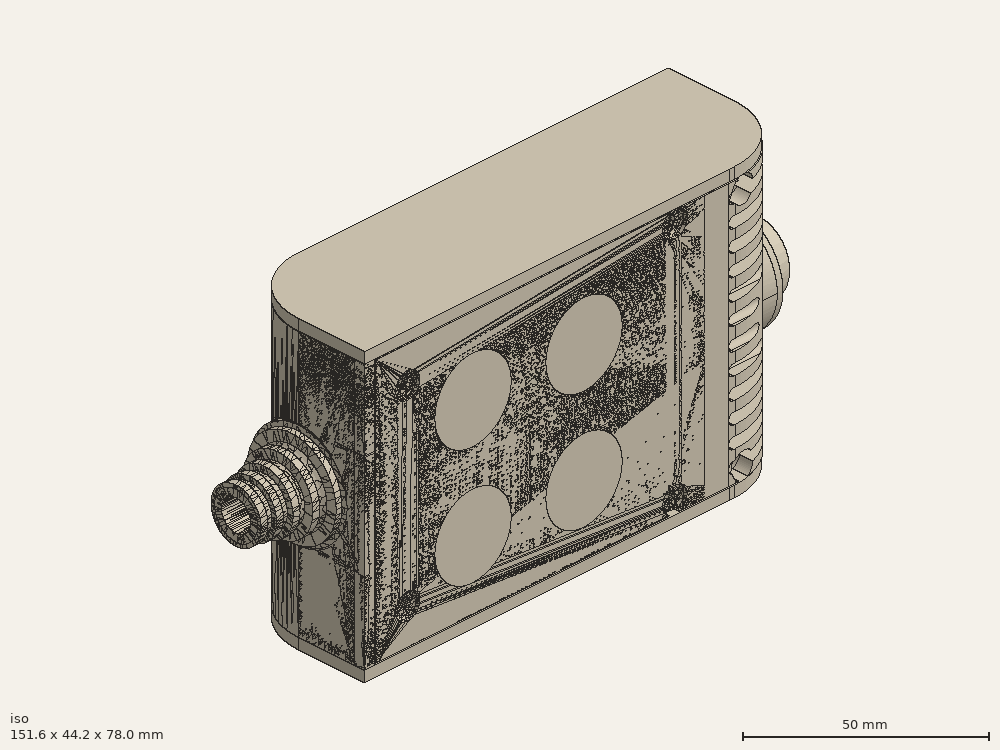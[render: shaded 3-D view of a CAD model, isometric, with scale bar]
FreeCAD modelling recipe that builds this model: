
FCSTD DOCUMENT  (FreeCAD 0.19R0.19.2)
Label: enclosure_185FCStd
License: All rights reserved
LicenseURL: http://en.wikipedia.org/wiki/All_rights_reserved
objects: Part::Revolution×152, Part::MultiFuse×146, Part::Feature×146, Sketcher::SketchObject×84, Part::Cut×70, Part::Cylinder×70, Part::Extrusion×67, Part::Fillet×58, Part::Box×36, App::MeasureDistance×4, PartDesign::Body×2, Image::ImagePlane×1
note: 831 computed .brp shape members not serialized (recipe doc carries the construction recipe); baked Part::Feature solids carry a one-line shape summary decoded from their .brp

FEATURE [Sketcher::SketchObject] Sketch  label="topSketch"
  FullyConstrained = true
  sketch-geometry (20):
    g0: LineSegment StartX=5.21097e-06 StartY=3 StartZ=0 EndX=5.21097e-06 EndY=19 EndZ=0
    g1: ArcOfCircle CenterX=19 CenterY=19 CenterZ=0 NormalX=0 NormalY=0 NormalZ=1 AngleXU=0 Radius=19 StartAngle=1.5708 EndAngle=3.14159
    g2: ArcOfCircle CenterX=19 CenterY=19 CenterZ=0 NormalX=0 NormalY=0 NormalZ=1 AngleXU=0 Radius=16 StartAngle=1.5708 EndAngle=3.14159
    g3: LineSegment StartX=114 StartY=35 StartZ=0 EndX=19 EndY=35 EndZ=0
    g4: LineSegment StartX=5.21097e-06 StartY=3 StartZ=0 EndX=5.21097e-06 EndY=0 EndZ=0
    g5: LineSegment StartX=3 StartY=0 StartZ=0 EndX=5.21097e-06 EndY=0 EndZ=0
    g6: LineSegment StartX=3 StartY=19 StartZ=0 EndX=3 EndY=0 EndZ=0
    g7: LineSegment StartX=19 StartY=38 StartZ=0 EndX=124 EndY=38 EndZ=0
    g8: Circle CenterX=119 CenterY=35 CenterZ=0 NormalX=0 NormalY=0 NormalZ=1 AngleXU=0 Radius=1
    g9: Circle CenterX=121 CenterY=35 CenterZ=0 NormalX=0 NormalY=0 NormalZ=1 AngleXU=0 Radius=1
    g10: Circle CenterX=121 CenterY=33 CenterZ=0 NormalX=0 NormalY=0 NormalZ=1 AngleXU=0 Radius=1
    g11: BSplineCurve PolesCount=3 KnotsCount=2 Degree=2 IsPeriodic=0
    g12: GeomPoint X=119 Y=35 Z=0
    g13: GeomPoint X=121 Y=33 Z=0
    g14: LineSegment StartX=119 StartY=35 StartZ=0 EndX=114 EndY=35 EndZ=0
    g15: ArcOfCircle CenterX=105 CenterY=19 CenterZ=0 NormalX=0 NormalY=0 NormalZ=1 AngleXU=0 Radius=19 StartAngle=5.7297 EndAngle=6.28319
    g16: ArcOfCircle CenterX=105 CenterY=19 CenterZ=0 NormalX=0 NormalY=0 NormalZ=1 AngleXU=0 Radius=16 StartAngle=5.60905 EndAngle=6.28319
    g17: LineSegment StartX=121 StartY=33 StartZ=0 EndX=121 EndY=19 EndZ=0
    g18: LineSegment StartX=124 StartY=38 StartZ=0 EndX=124 EndY=19 EndZ=0
    g19: LineSegment StartX=117.5 StartY=9.01251 StartZ=0 EndX=121.163 EndY=9.0125 EndZ=0
  constraints (46):
    c: Vertical(g0)
    c: Block(g0)
    c: Coincident(g1,g0)
    c: Block(g1)
    c: Coincident(g2,g1)
    c: Block(g2)
    c: Coincident(g3,g2)
    c: Horizontal(g3)
    c: Tangent(g3,g2)
    c: Coincident(g4,g0)
    c: Distance(g4) = 3
    c: Vertical(g4)
    c: Coincident(g5,g4)
    c: Horizontal(g5)
    c: Coincident(g6,g2)
    c: Coincident(g6,g5)
    c: Vertical(g6)
    c: Horizontal(g7)
    c: Distance(g7) = 105
    c: Coincident(g7,g1)
    c: Block(g3)
    c: Weight(g8) = 1
    c: Equal(g8,g9)
    c: Equal(g8,g10)
    c: InternalAlignment(g8,g11)
    c: InternalAlignment(g9,g11)
    c: InternalAlignment(g10,g11)
    c: InternalAlignment(g12,g11)
    c: InternalAlignment(g13,g11)
    c: Block(g11)
    c: Coincident(g14,g11)
    c: Coincident(g14,g3)
    c: Horizontal(g14)
    c: Block(g15)
    c: Coincident(g16,g15)
    c: Block(g16)
    c: Coincident(g17,g11)
    c: Coincident(g17,g16)
    c: Vertical(g17)
    c: Distance(g17) = 14
    c: Coincident(g18,g7)
    c: Coincident(g18,g15)
    c: Vertical(g18)
    c: Distance(g18) = 19
    c: Coincident(g19,g16)
    c: Coincident(g19,g15)
FEATURE [Sketcher::SketchObject] Sketch001  label="bottomSketch"
  FullyConstrained = true
  sketch-geometry (32):
    g0: LineSegment StartX=3.3 StartY=-6.03275e-07 StartZ=0 EndX=98 EndY=-6.03275e-07 EndZ=0
    g1: ArcOfCircle CenterX=98 CenterY=19 CenterZ=0 NormalX=0 NormalY=0 NormalZ=1 AngleXU=0 Radius=19 StartAngle=4.71239 EndAngle=5.71103
    g2: LineSegment StartX=6.3 StartY=8 StartZ=0 EndX=3.3 EndY=8 EndZ=0
    g3: LineSegment StartX=3.3 StartY=8 StartZ=0 EndX=3.3 EndY=-6.03275e-07 EndZ=0
    g4: ArcOfCircle CenterX=8.3 CenterY=5 CenterZ=0 NormalX=0 NormalY=0 NormalZ=1 AngleXU=0 Radius=2 StartAngle=3.14159 EndAngle=4.71239
    g5: LineSegment StartX=6.3 StartY=8 StartZ=0 EndX=6.3 EndY=5 EndZ=0
    g6: ArcOfCircle CenterX=98 CenterY=19 CenterZ=0 NormalX=0 NormalY=0 NormalZ=1 AngleXU=0 Radius=12.7 StartAngle=4.71239 EndAngle=6.28319
    g7: LineSegment StartX=94.7 StartY=3 StartZ=0 EndX=8.3 EndY=3 EndZ=0
    g8-g12: Circle x5 (B-spline internal-alignment scaffolding for g13; pole/knot coordinates omitted)
    g13: BSplineCurve PolesCount=5 KnotsCount=3 Degree=3 IsPeriodic=0
    g14: GeomPoint X=98 Y=6.3 Z=0
    g15: GeomPoint X=96.3938 Y=4.71946 Z=0
    g16: GeomPoint X=94.7 Y=3 Z=0
    g17-g23: Circle x7 (B-spline internal-alignment scaffolding for g24; pole/knot coordinates omitted)
    g24: BSplineCurve PolesCount=7 KnotsCount=5 Degree=3 IsPeriodic=0
    g25-g29: GeomPoint x5 (B-spline internal-alignment scaffolding for g24; pole/knot coordinates omitted)
    g30: ArcOfCircle CenterX=98 CenterY=19 CenterZ=0 NormalX=0 NormalY=0 NormalZ=1 AngleXU=0 Radius=15.7 StartAngle=5.81226 EndAngle=6.28319
    g31: LineSegment StartX=110.7 StartY=19 StartZ=0 EndX=113.7 EndY=19 EndZ=0
  constraints (41):
    c: Horizontal(g0)
    c: Coincident(g1,g0)
    c: Block(g1)
    c: Horizontal(g2)
    c: Distance(g2) = 3
    c: Coincident(g3,g2)
    c: Vertical(g3)
    c: Coincident(g3,g0)
    c: Block(g4)
    c: Block(g2)
    c: Coincident(g5,g2)
    c: Coincident(g5,g4)
    c: Vertical(g5)
    c: Coincident(g6,g1)
    c: Block(g6)
    c: Coincident(g7,g4)
    c: Horizontal(g7)
    c: Block(g0)
    c: Block(g7)
    c: Block(g3)
    c: Coincident(g13,g6)
    c: Weight(g8) = 1
    c: Equal(g8, g9-g12) x4
    c: Coincident(g13,g7)
    c: InternalAlignment(g8-g12 -> g13) x5
    c: InternalAlignment(g14,g13)
    c: InternalAlignment(g15,g13)
    c: InternalAlignment(g16,g13)
    c: Block(g13)
    c: Weight(g17) = 1
    c: Equal(g17, g18-g23) x6
    c: Coincident(g24,g1)
    c: InternalAlignment(g17-g23 -> g24) x7
    c: InternalAlignment(g25-g29 -> g24) x5
    c: Block(g24)
    c: Coincident(g30,g24)
    c: Coincident(g31,g6)
    c: Coincident(g31,g30)
    c: Horizontal(g31)
    c: Block(g31)
    c: Block(g30)
FEATURE [Part::Extrusion] Extrude  label="top"
  Base = -> Sketch
  Dir = (0,0,1)
  DirMode = 2
  FaceMakerClass = Part::FaceMakerBullseye
  LengthFwd = 72
  LengthRev = 0
  Solid = true
  Symmetric = false
FEATURE [Part::Extrusion] Extrude001  label="bottom"
  Base = -> Sketch001
  Dir = (0,0,1)
  DirMode = 2
  FaceMakerClass = Part::FaceMakerBullseye
  LengthFwd = 71.4
  LengthRev = 0
  Placement = pos=(0,0,0.3) rot=(0,0,1;0rad)
  Solid = true
  Symmetric = false
FEATURE [Sketcher::SketchObject] Sketch002  label="topSketch001"
  FullyConstrained = true
  sketch-geometry (8):
    g0: ArcOfCircle CenterX=19 CenterY=19.0975 CenterZ=0 NormalX=0 NormalY=0 NormalZ=1 AngleXU=0 Radius=18.9025 StartAngle=1.5708 EndAngle=3.14674
    g1: LineSegment StartX=0.0977805 StartY=19.0003 StartZ=0 EndX=0.0977805 EndY=0.000251602 EndZ=0
    g2: LineSegment StartX=19 StartY=38 StartZ=0 EndX=124 EndY=38 EndZ=0
    g3: LineSegment StartX=0.0977805 StartY=0.000251602 StartZ=0 EndX=105.098 EndY=0.000251602 EndZ=0
    g4: LineSegment StartX=124 StartY=38 StartZ=0 EndX=125.616 EndY=38 EndZ=0
    g5: LineSegment StartX=105.098 StartY=0.000251602 StartZ=0 EndX=106.713 EndY=0.000251602 EndZ=0
    g6: ArcOfCircle CenterX=106.616 CenterY=19 CenterZ=0 NormalX=0 NormalY=0 NormalZ=1 AngleXU=0 Radius=19 StartAngle=4.71754 EndAngle=6.28319
    g7: LineSegment StartX=125.616 StartY=38 StartZ=0 EndX=125.616 EndY=19 EndZ=0
  constraints (21):
    c: Block(g0)
    c: Coincident(g1,g0)
    c: Vertical(g1)
    c: Horizontal(g2)
    c: Distance(g2) = 105
    c: Coincident(g2,g0)
    c: Distance(g1) = 19
    c: Coincident(g3,g1)
    c: Horizontal(g3)
    c: Distance(g3) = 105
    c: Coincident(g4,g2)
    c: Horizontal(g4)
    c: Distance(g4) = 1.61553
    c: Horizontal(g5)
    c: Equal(g4,g5) = 1.61553
    c: Coincident(g5,g3)
    c: Block(g6)
    c: Coincident(g6,g5)
    c: Coincident(g7,g4)
    c: Coincident(g7,g6)
    c: Vertical(g7)
FEATURE [Part::Extrusion] Extrude002  label="sideA"
  Base = -> Sketch002
  Dir = (0,0,1)
  DirMode = 2
  FaceMakerClass = Part::FaceMakerBullseye
  LengthFwd = 3
  LengthRev = 0
  Placement = pos=(0,0,-3) rot=(0,0,1;0rad)
  Solid = true
  Symmetric = false
FEATURE [Sketcher::SketchObject] Sketch003  label="topSketch002"
  FullyConstrained = true
  sketch-geometry (6):
    g0: LineSegment StartX=19 StartY=38 StartZ=0 EndX=117 EndY=38 EndZ=0
    g1: ArcOfCircle CenterX=19 CenterY=19 CenterZ=0 NormalX=0 NormalY=0 NormalZ=1 AngleXU=0 Radius=19 StartAngle=1.5708 EndAngle=3.14159
    g2: LineSegment StartX=117 StartY=38 StartZ=0 EndX=117 EndY=19 EndZ=0
    g3: LineSegment StartX=98 StartY=1.0161e-12 StartZ=0 EndX=5.22862e-06 EndY=1.0161e-12 EndZ=0
    g4: LineSegment StartX=5.22862e-06 StartY=19 StartZ=0 EndX=5.22862e-06 EndY=1.0161e-12 EndZ=0
    g5: ArcOfCircle CenterX=98 CenterY=19 CenterZ=0 NormalX=0 NormalY=0 NormalZ=1 AngleXU=0 Radius=19 StartAngle=4.71239 EndAngle=6.28319
  constraints (16):
    c: Horizontal(g0)
    c: Distance(g0) = 98
    c: Coincident(g1,g0)
    c: Block(g1)
    c: Coincident(g2,g0)
    c: Vertical(g2)
    c: Distance(g2) = 19
    c: Horizontal(g3)
    c: Coincident(g4,g1)
    c: Vertical(g4)
    c: Coincident(g3,g4)
    c: Block(g3)
    c: Coincident(g5,g2)
    c: Coincident(g5,g3)
    c: Block(g0)
    c: Block(g5)
FEATURE [Sketcher::SketchObject] Sketch004
  FullyConstrained = true
  MapMode = 3
  Placement = pos=(0,0,0) rot=(1,0,0;1.5708rad)
  Support = -> [Extrude]
  sketch-geometry (8):
    g0: Circle CenterX=80.351 CenterY=-67.6202 CenterZ=0 NormalX=0 NormalY=0 NormalZ=1 AngleXU=0 Radius=2
    g1: Circle CenterX=80.351 CenterY=-67.6202 CenterZ=0 NormalX=0 NormalY=0 NormalZ=1 AngleXU=0 Radius=3
    g2: Circle CenterX=80.351 CenterY=-4.92017 CenterZ=0 NormalX=0 NormalY=0 NormalZ=1 AngleXU=0 Radius=2
    g3: Circle CenterX=80.351 CenterY=-4.92017 CenterZ=0 NormalX=0 NormalY=0 NormalZ=1 AngleXU=0 Radius=3
    g4: Circle CenterX=23.851 CenterY=-4.92017 CenterZ=0 NormalX=0 NormalY=0 NormalZ=1 AngleXU=0 Radius=2
    g5: Circle CenterX=23.851 CenterY=-4.92017 CenterZ=0 NormalX=0 NormalY=0 NormalZ=1 AngleXU=0 Radius=3
    g6: Circle CenterX=23.851 CenterY=-67.6202 CenterZ=0 NormalX=0 NormalY=0 NormalZ=1 AngleXU=0 Radius=2
    g7: Circle CenterX=23.851 CenterY=-67.6202 CenterZ=0 NormalX=0 NormalY=0 NormalZ=1 AngleXU=0 Radius=3
  constraints (8):
    c: Block(g3)
    c: Block(g2)
    c: Block(g1)
    c: Block(g0)
    c: Block(g6)
    c: Block(g7)
    c: Block(g4)
    c: Block(g5)
FEATURE [Part::Extrusion] Extrude004
  Base = -> Sketch004
  Dir = (0,-1,2e-16)
  DirMode = 2
  FaceMakerClass = Part::FaceMakerBullseye
  LengthFwd = 6
  LengthRev = 0
  Placement = pos=(0,9,0) rot=(0,0,1;0rad)
  Solid = true
  Symmetric = false
FEATURE [Sketcher::SketchObject] Sketch005
  FullyConstrained = true
  MapMode = 3
  Placement = pos=(0,0,0) rot=(1,0,0;1.5708rad)
  Support = -> [Extrude]
  sketch-geometry (8):
    g0: Circle CenterX=80.351 CenterY=-67.6202 CenterZ=0 NormalX=0 NormalY=0 NormalZ=1 AngleXU=0 Radius=3
    g1: Circle CenterX=80.351 CenterY=-4.92017 CenterZ=0 NormalX=0 NormalY=0 NormalZ=1 AngleXU=0 Radius=3
    g2: Circle CenterX=23.851 CenterY=-4.92017 CenterZ=0 NormalX=0 NormalY=0 NormalZ=1 AngleXU=0 Radius=3
    g3: Circle CenterX=23.851 CenterY=-67.6202 CenterZ=0 NormalX=0 NormalY=0 NormalZ=1 AngleXU=0 Radius=3
    g4: Circle CenterX=23.851 CenterY=-67.6202 CenterZ=0 NormalX=0 NormalY=0 NormalZ=1 AngleXU=0 Radius=5
    g5: Circle CenterX=80.351 CenterY=-67.6202 CenterZ=0 NormalX=0 NormalY=0 NormalZ=1 AngleXU=0 Radius=5
    g6: Circle CenterX=23.851 CenterY=-4.92017 CenterZ=0 NormalX=0 NormalY=0 NormalZ=1 AngleXU=0 Radius=5
    g7: Circle CenterX=80.351 CenterY=-4.92017 CenterZ=0 NormalX=0 NormalY=0 NormalZ=1 AngleXU=0 Radius=5
  constraints (8):
    c: Block(g1)
    c: Block(g0)
    c: Block(g3)
    c: Block(g2)
    c: Block(g5)
    c: Block(g4)
    c: Block(g6)
    c: Block(g7)
FEATURE [Part::Extrusion] Extrude005
  Base = -> Sketch005
  Dir = (0,-1,2e-16)
  DirMode = 2
  FaceMakerClass = Part::FaceMakerBullseye
  LengthFwd = 2
  LengthRev = 0
  Solid = true
  Symmetric = false
FEATURE [Sketcher::SketchObject] Sketch006
  FullyConstrained = true
  MapMode = 3
  Placement = pos=(0,0,0) rot=(1,0,0;1.5708rad)
  sketch-geometry (8):
    g0: Circle CenterX=80.351 CenterY=-67.6202 CenterZ=0 NormalX=0 NormalY=0 NormalZ=1 AngleXU=0 Radius=3
    g1: Circle CenterX=80.351 CenterY=-4.92017 CenterZ=0 NormalX=0 NormalY=0 NormalZ=1 AngleXU=0 Radius=3
    g2: Circle CenterX=23.851 CenterY=-4.92017 CenterZ=0 NormalX=0 NormalY=0 NormalZ=1 AngleXU=0 Radius=3
    g3: Circle CenterX=23.851 CenterY=-67.6202 CenterZ=0 NormalX=0 NormalY=0 NormalZ=1 AngleXU=0 Radius=3
    g4: Circle CenterX=23.851 CenterY=-67.6202 CenterZ=0 NormalX=0 NormalY=0 NormalZ=1 AngleXU=0 Radius=5
    g5: Circle CenterX=80.351 CenterY=-67.6202 CenterZ=0 NormalX=0 NormalY=0 NormalZ=1 AngleXU=0 Radius=5
    g6: Circle CenterX=23.851 CenterY=-4.92017 CenterZ=0 NormalX=0 NormalY=0 NormalZ=1 AngleXU=0 Radius=5
    g7: Circle CenterX=80.351 CenterY=-4.92017 CenterZ=0 NormalX=0 NormalY=0 NormalZ=1 AngleXU=0 Radius=5
  constraints (8):
    c: Block(g1)
    c: Block(g0)
    c: Block(g3)
    c: Block(g2)
    c: Block(g5)
    c: Block(g4)
    c: Block(g6)
    c: Block(g7)
FEATURE [Part::Extrusion] Extrude007
  Base = -> Sketch006
  Dir = (0,-1,2e-16)
  DirMode = 2
  FaceMakerClass = Part::FaceMakerBullseye
  LengthFwd = 2
  LengthRev = 0
  Solid = true
  Symmetric = false
FEATURE [Part::Fillet] Fillet
  Base = -> Extrude007
  Edges = 4 edges r=1.99: [Edge6,Edge12,Edge18,Edge24]
FEATURE [Part::Cut] Cut
  Base = -> Extrude005
  Placement = pos=(0,5,0) rot=(0,0,1;0rad)
  Tool = -> Fillet
FEATURE [Part::MultiFuse] Fusion  label="pCBScrews"
  Placement = pos=(-2.5,0,72.3) rot=(0,0,1;0rad)
  Shapes = -> [Extrude004,Cut]
FEATURE [App::MeasureDistance] Distance  label="Distance: 0.69 mm"
  Distance = 0.685967
  P1 = (24.0138,2.9647,0.3)
  P2 = (23.8901,3,-0.373787)
FEATURE [App::MeasureDistance] Distance001  label="Distance: 0.53 mm"
  Distance = 0.533607
  P1 = (80.2939,3,72.2334)
  P2 = (80.281,2.99661,71.7)
FEATURE [Part::Fillet] Fillet001
  Base = -> Extrude001
  Edges = 1 edges r=2.4: [Edge17]
FEATURE [Part::Fillet] Fillet002  label="bottom001"
  Base = -> Fillet001
  Edges = 1 edges r=2.4: [Edge36]
FEATURE [Part::Fillet] Fillet003  label="top001"
  Base = -> Extrude
  Edges = 1 edges r=2: [Edge1]
FEATURE [Sketcher::SketchObject] Sketch007
  FullyConstrained = true
  sketch-geometry (16):
    g0: LineSegment StartX=4 StartY=0 StartZ=0 EndX=4 EndY=2.4 EndZ=0
    g1: LineSegment StartX=4 StartY=2.4 StartZ=0 EndX=7 EndY=2.4 EndZ=0
    g2: LineSegment StartX=4 StartY=0 StartZ=0 EndX=5.7 EndY=0 EndZ=0
    g3: LineSegment StartX=5.7 StartY=0 StartZ=0 EndX=5.7 EndY=-5.6 EndZ=0
    g4-g8: Circle x5 (B-spline internal-alignment scaffolding for g9; pole/knot coordinates omitted)
    g9: BSplineCurve PolesCount=5 KnotsCount=3 Degree=3 IsPeriodic=0
    g10: GeomPoint X=7 Y=2.4 Z=0
    g11: GeomPoint X=10.4582 Y=-1.55472 Z=0
    g12: GeomPoint X=14 Y=-5.6 Z=0
    g13: LineSegment StartX=14 StartY=-5.6 StartZ=0 EndX=14 EndY=-14.1 EndZ=0
    g14: LineSegment StartX=14 StartY=-14.1 StartZ=0 EndX=6.5 EndY=-14.1 EndZ=0
    g15: LineSegment StartX=5.7 StartY=-5.6 StartZ=0 EndX=6.5 EndY=-14.1 EndZ=0
  constraints (28):
    c: Distance(g0) = 2.4
    c: Vertical(g0)
    c: Block(g0)
    c: Coincident(g1,g0)
    c: Horizontal(g1)
    c: Distance(g1) = 3
    c: Coincident(g2,g0)
    c: Horizontal(g2)
    c: Distance(g2) = 1.7
    c: Coincident(g3,g2)
    c: Vertical(g3)
    c: Distance(g3) = 5.6
    c: Coincident(g9,g1)
    c: Weight(g4) = 1
    c: Equal(g4, g5-g8) x4
    c: InternalAlignment(g4-g8 -> g9) x5
    c: InternalAlignment(g10,g9)
    c: InternalAlignment(g11,g9)
    c: InternalAlignment(g12,g9)
    c: Block(g9)
    c: Coincident(g13,g9)
    c: Vertical(g13)
    c: Distance(g13) = 8.5
    c: Coincident(g14,g13)
    c: Horizontal(g14)
    c: Distance(g14) = 7.5
    c: Coincident(g15,g3)
    c: Coincident(g15,g14)
FEATURE [Part::Feature] Face
  shape: bbox 10 x 16.5 x 2e-07 mm, 1 faces, 0 solids (baked)
FEATURE [Part::Revolution] Revolve  label="plugHousing"
  Angle = 360
  Axis = (0,1,0)
  Base = (0,0,0)
  FaceMakerClass = Part::FaceMakerBullseye
  Placement = pos=(0,0,36.15) rot=(0,0,1;0rad)
  Solid = false
  Source = -> Face
  Symmetric = false
FEATURE [Part::Feature] Face001
  shape: bbox 10 x 16.5 x 2e-07 mm, 1 faces, 0 solids (baked)
FEATURE [Part::Revolution] Revolve001  label="plugHousing001"
  Angle = 360
  Axis = (0,1,0)
  Base = (0,0,0)
  FaceMakerClass = Part::FaceMakerBullseye
  Placement = pos=(0,0,36.15) rot=(0,0,1;0rad)
  Solid = false
  Source = -> Face001
  Symmetric = false
FEATURE [Part::MultiFuse] Fusion001  label="plugHousing002"
  Placement = pos=(0,0,0) rot=(0,0,1;1.5708rad)
  Shapes = -> [Revolve001,Revolve]
FEATURE [Part::Feature] Face002
  shape: bbox 10 x 16.5 x 2e-07 mm, 1 faces, 0 solids (baked)
FEATURE [Part::Revolution] Revolve003  label="plugHousing005"
  Angle = 360
  Axis = (0,1,0)
  Base = (0,0,0)
  FaceMakerClass = Part::FaceMakerBullseye
  Placement = pos=(0,0,36.15) rot=(0,0,1;0rad)
  Solid = false
  Source = -> Face002
  Symmetric = false
FEATURE [Part::Feature] Face003
  shape: bbox 10 x 16.5 x 2e-07 mm, 1 faces, 0 solids (baked)
FEATURE [Part::Revolution] Revolve002  label="plugHousing003"
  Angle = 360
  Axis = (0,1,0)
  Base = (0,0,0)
  FaceMakerClass = Part::FaceMakerBullseye
  Placement = pos=(0,0,36.15) rot=(0,0,1;0rad)
  Solid = false
  Source = -> Face003
  Symmetric = false
FEATURE [Part::MultiFuse] Fusion002  label="plugHousing004"
  Placement = pos=(0,0,0) rot=(0,0,1;1.5708rad)
  Shapes = -> [Revolve002,Revolve003]
FEATURE [Part::MultiFuse] Fusion003  label="plugHousing006"
  Placement = pos=(0,19,0) rot=(0,0,1;3.14159rad)
  Shapes = -> [Fusion002,Fusion001]
FEATURE [Part::Feature] Face004
  shape: bbox 10 x 16.5 x 2e-07 mm, 1 faces, 0 solids (baked)
FEATURE [Part::Revolution] Revolve006  label="plugHousing010"
  Angle = 360
  Axis = (0,1,0)
  Base = (0,0,0)
  FaceMakerClass = Part::FaceMakerBullseye
  Placement = pos=(0,0,36.15) rot=(0,0,1;0rad)
  Solid = false
  Source = -> Face004
  Symmetric = false
FEATURE [Part::Feature] Face005
  shape: bbox 10 x 16.5 x 2e-07 mm, 1 faces, 0 solids (baked)
FEATURE [Part::Revolution] Revolve007  label="plugHousing011"
  Angle = 360
  Axis = (0,1,0)
  Base = (0,0,0)
  FaceMakerClass = Part::FaceMakerBullseye
  Placement = pos=(0,0,36.15) rot=(0,0,1;0rad)
  Solid = false
  Source = -> Face005
  Symmetric = false
FEATURE [Part::Feature] Face006
  shape: bbox 10 x 16.5 x 2e-07 mm, 1 faces, 0 solids (baked)
FEATURE [Part::Revolution] Revolve004  label="plugHousing007"
  Angle = 360
  Axis = (0,1,0)
  Base = (0,0,0)
  FaceMakerClass = Part::FaceMakerBullseye
  Placement = pos=(0,0,36.15) rot=(0,0,1;0rad)
  Solid = false
  Source = -> Face006
  Symmetric = false
FEATURE [Part::MultiFuse] Fusion004  label="plugHousing009"
  Placement = pos=(0,0,0) rot=(0,0,1;1.5708rad)
  Shapes = -> [Revolve004,Revolve007]
FEATURE [Part::Feature] Face007
  shape: bbox 10 x 16.5 x 2e-07 mm, 1 faces, 0 solids (baked)
FEATURE [Part::Revolution] Revolve005  label="plugHousing008"
  Angle = 360
  Axis = (0,1,0)
  Base = (0,0,0)
  FaceMakerClass = Part::FaceMakerBullseye
  Placement = pos=(0,0,36.15) rot=(0,0,1;0rad)
  Solid = false
  Source = -> Face007
  Symmetric = false
FEATURE [Part::MultiFuse] Fusion005  label="plugHousing012"
  Placement = pos=(0,0,0) rot=(0,0,1;1.5708rad)
  Shapes = -> [Revolve006,Revolve005]
FEATURE [Part::MultiFuse] Fusion006  label="plugHousing013"
  Placement = pos=(0,19,0) rot=(0,0,1;3.14159rad)
  Shapes = -> [Fusion005,Fusion004]
FEATURE [Part::MultiFuse] Fusion007  label="plugHousing014"
  Placement = pos=(122.621,0,-0.15) rot=(0,0,1;0rad)
  Shapes = -> [Fusion003,Fusion006]
FEATURE [Part::Cylinder] Cylinder002
  Angle = 360
  AttacherType = Attacher::AttachEngine3D
  Height = 20
  Placement = pos=(0,0,36.15) rot=(0,0,1;0rad)
  Radius = 4
FEATURE [Part::Cylinder] Cylinder003
  Angle = 360
  AttacherType = Attacher::AttachEngine3D
  Height = 10
  Placement = pos=(0,0,36.15) rot=(0,0,1;0rad)
  Radius = 4
FEATURE [Part::MultiFuse] Fusion009  label="removeToCreateHoleForPlugHousing"
  Placement = pos=(70,19,36.15) rot=(0,1,0;1.5708rad)
  Shapes = -> [Cylinder002,Cylinder003]
FEATURE [Part::Cylinder] Cylinder004
  Angle = 360
  AttacherType = Attacher::AttachEngine3D
  Height = 20
  Placement = pos=(0,0,36.15) rot=(0,0,1;0rad)
  Radius = 4
FEATURE [Part::Cylinder] Cylinder005
  Angle = 360
  AttacherType = Attacher::AttachEngine3D
  Height = 10
  Placement = pos=(0,0,36.15) rot=(0,0,1;0rad)
  Radius = 4
FEATURE [Part::MultiFuse] Fusion010  label="removeToCreateHoleForPlugHousing001"
  Placement = pos=(70,19,36.15) rot=(0,1,0;1.5708rad)
  Shapes = -> [Cylinder004,Cylinder005]
FEATURE [Part::Cut] Cut001
  Base = -> Fillet003
  Tool = -> Fusion010
FEATURE [Part::Cut] Cut002  label="Bottom"
  Base = -> Fillet002
  Tool = -> Fusion009
FEATURE [Part::Feature] Face008
  shape: bbox 10 x 16.5 x 2e-07 mm, 1 faces, 0 solids (baked)
FEATURE [Part::Revolution] Revolve011  label="plugHousing021"
  Angle = 360
  Axis = (0,1,0)
  Base = (0,0,0)
  FaceMakerClass = Part::FaceMakerBullseye
  Placement = pos=(0,0,36.15) rot=(0,0,1;0rad)
  Solid = false
  Source = -> Face008
  Symmetric = false
FEATURE [Part::Feature] Face009
  shape: bbox 10 x 16.5 x 2e-07 mm, 1 faces, 0 solids (baked)
FEATURE [Part::Revolution] Revolve012  label="plugHousing022"
  Angle = 360
  Axis = (0,1,0)
  Base = (0,0,0)
  FaceMakerClass = Part::FaceMakerBullseye
  Placement = pos=(0,0,36.15) rot=(0,0,1;0rad)
  Solid = false
  Source = -> Face009
  Symmetric = false
FEATURE [Part::Feature] Face010 .. Face013  x4 (patterned run collapsed; names and placements below)
  shape: bbox 10 x 16.5 x 2e-07 mm, 1 faces, 0 solids (baked)
FEATURE [Part::Revolution] Revolve015  label="plugHousing027"
  Angle = 360
  Axis = (0,1,0)
  Base = (0,0,0)
  FaceMakerClass = Part::FaceMakerBullseye
  Placement = pos=(0,0,36.15) rot=(0,0,1;0rad)
  Solid = false
  Source = -> Face013
  Symmetric = false
FEATURE [Part::Feature] Face014
  shape: bbox 10 x 16.5 x 2e-07 mm, 1 faces, 0 solids (baked)
FEATURE [Part::Feature] Face015
  shape: bbox 10 x 16.5 x 2e-07 mm, 1 faces, 0 solids (baked)
FEATURE [Part::Feature] Face016
  shape: bbox 10 x 16.5 x 2e-07 mm, 1 faces, 0 solids (baked)
FEATURE [Part::Revolution] Revolve019  label="plugHousing033"
  Angle = 360
  Axis = (0,1,0)
  Base = (0,0,0)
  FaceMakerClass = Part::FaceMakerBullseye
  Placement = pos=(0,0,36.15) rot=(0,0,1;0rad)
  Solid = false
  Source = -> Face016
  Symmetric = false
FEATURE [Part::Feature] Face017
  shape: bbox 10 x 16.5 x 2e-07 mm, 1 faces, 0 solids (baked)
FEATURE [Part::Revolution] Revolve020  label="plugHousing034"
  Angle = 360
  Axis = (0,1,0)
  Base = (0,0,0)
  FaceMakerClass = Part::FaceMakerBullseye
  Placement = pos=(0,0,36.15) rot=(0,0,1;0rad)
  Solid = false
  Source = -> Face017
  Symmetric = false
FEATURE [Part::Feature] Face018
  shape: bbox 10 x 16.5 x 2e-07 mm, 1 faces, 0 solids (baked)
FEATURE [Part::Revolution] Revolve016  label="plugHousing030"
  Angle = 360
  Axis = (0,1,0)
  Base = (0,0,0)
  FaceMakerClass = Part::FaceMakerBullseye
  Placement = pos=(0,0,36.15) rot=(0,0,1;0rad)
  Solid = false
  Source = -> Face018
  Symmetric = false
FEATURE [Part::MultiFuse] Fusion020  label="plugHousing038"
  Placement = pos=(0,0,0) rot=(0,0,1;1.5708rad)
  Shapes = -> [Revolve016,Revolve020]
FEATURE [Part::Feature] Face019
  shape: bbox 10 x 16.5 x 2e-07 mm, 1 faces, 0 solids (baked)
FEATURE [Part::Feature] Face020
  shape: bbox 10 x 16.5 x 2e-07 mm, 1 faces, 0 solids (baked)
FEATURE [Part::Revolution] Revolve017  label="plugHousing031"
  Angle = 360
  Axis = (0,1,0)
  Base = (0,0,0)
  FaceMakerClass = Part::FaceMakerBullseye
  Placement = pos=(0,0,36.15) rot=(0,0,1;0rad)
  Solid = false
  Source = -> Face020
  Symmetric = false
FEATURE [Part::MultiFuse] Fusion021  label="plugHousing039"
  Placement = pos=(0,0,0) rot=(0,0,1;1.5708rad)
  Shapes = -> [Revolve019,Revolve017]
FEATURE [Part::MultiFuse] Fusion023  label="plugHousing041"
  Placement = pos=(0,19,0) rot=(0,0,1;3.14159rad)
  Shapes = -> [Fusion021,Fusion020]
FEATURE [Part::Revolution] Revolve022  label="plugHousing043"
  Angle = 360
  Axis = (0,1,0)
  Base = (0,0,0)
  FaceMakerClass = Part::FaceMakerBullseye
  Placement = pos=(0,0,36.15) rot=(0,0,1;0rad)
  Solid = false
  Source = -> Face019
  Symmetric = false
FEATURE [Part::Feature] Face021
  shape: bbox 10 x 16.5 x 2e-07 mm, 1 faces, 0 solids (baked)
FEATURE [Part::Revolution] Revolve023  label="plugHousing044"
  Angle = 360
  Axis = (0,1,0)
  Base = (0,0,0)
  FaceMakerClass = Part::FaceMakerBullseye
  Placement = pos=(0,0,36.15) rot=(0,0,1;0rad)
  Solid = false
  Source = -> Face021
  Symmetric = false
FEATURE [Part::Feature] Face022
  shape: bbox 10 x 16.5 x 2e-07 mm, 1 faces, 0 solids (baked)
FEATURE [Part::Revolution] Revolve018  label="plugHousing032"
  Angle = 360
  Axis = (0,1,0)
  Base = (0,0,0)
  FaceMakerClass = Part::FaceMakerBullseye
  Placement = pos=(0,0,36.15) rot=(0,0,1;0rad)
  Solid = false
  Source = -> Face022
  Symmetric = false
FEATURE [Part::MultiFuse] Fusion022  label="plugHousing040"
  Placement = pos=(0,0,0) rot=(0,0,1;1.5708rad)
  Shapes = -> [Revolve018,Revolve023]
FEATURE [Part::Feature] Face023
  shape: bbox 10 x 16.5 x 2e-07 mm, 1 faces, 0 solids (baked)
FEATURE [Part::Revolution] Revolve021  label="plugHousing035"
  Angle = 360
  Axis = (0,1,0)
  Base = (0,0,0)
  FaceMakerClass = Part::FaceMakerBullseye
  Placement = pos=(0,0,36.15) rot=(0,0,1;0rad)
  Solid = false
  Source = -> Face023
  Symmetric = false
FEATURE [Part::MultiFuse] Fusion018  label="plugHousing036"
  Placement = pos=(0,0,0) rot=(0,0,1;1.5708rad)
  Shapes = -> [Revolve022,Revolve021]
FEATURE [Part::MultiFuse] Fusion019  label="plugHousing037"
  Placement = pos=(0,19,0) rot=(0,0,1;3.14159rad)
  Shapes = -> [Fusion018,Fusion022]
FEATURE [Part::MultiFuse] Fusion024  label="plugHousing042"
  Placement = pos=(122.621,0,-0.15) rot=(0,0,1;0rad)
  Shapes = -> [Fusion023,Fusion019]
FEATURE [Part::Cylinder] Cylinder006
  Angle = 360
  AttacherType = Attacher::AttachEngine3D
  Height = 20
  Placement = pos=(0,0,36.15) rot=(0,0,1;0rad)
  Radius = 14.3
FEATURE [Part::Cylinder] Cylinder007
  Angle = 360
  AttacherType = Attacher::AttachEngine3D
  Height = 10
  Placement = pos=(0,0,36.15) rot=(0,0,1;0rad)
  Radius = 4
FEATURE [Part::MultiFuse] Fusion026  label="removeToCreteHoleForPlugHousing"
  Placement = pos=(70,19,36) rot=(0,1,0;1.5708rad)
  Shapes = -> [Cylinder006,Cylinder007]
FEATURE [Part::Box] Box001  label="Cube001"
  AttacherType = Attacher::AttachEngine3D
  Height = 28
  Length = 3
  Placement = pos=(110.7,19,22) rot=(0,0,1;0rad)
  Width = 15.7
FEATURE [Part::Cut] Cut003  label="top002"
  Base = -> Cut001
  Tool = -> Fusion007
FEATURE [Part::Revolution] Revolve008  label="plugHousing015"
  Angle = 360
  Axis = (0,1,0)
  Base = (0,0,0)
  FaceMakerClass = Part::FaceMakerBullseye
  Placement = pos=(0,0,36.15) rot=(0,0,1;0rad)
  Solid = false
  Source = -> Face010
  Symmetric = false
FEATURE [Part::MultiFuse] Fusion013  label="plugHousing020"
  Placement = pos=(0,0,0) rot=(0,0,1;1.5708rad)
  Shapes = -> [Revolve008,Revolve012]
FEATURE [Part::Cut] Cut004  label="top003"
  Base = -> Cut003
  Placement = pos=(1,0,0) rot=(0,0,1;0rad)
  Tool = -> Fusion026
FEATURE [Part::Cylinder] Cylinder008
  Angle = 360
  AttacherType = Attacher::AttachEngine3D
  Height = 20
  Placement = pos=(0,0,36.15) rot=(0,0,1;0rad)
  Radius = 10.3
FEATURE [Part::Cylinder] Cylinder009
  Angle = 360
  AttacherType = Attacher::AttachEngine3D
  Height = 10
  Placement = pos=(0,0,36.15) rot=(0,0,1;0rad)
  Radius = 4
FEATURE [Part::MultiFuse] Fusion027  label="removeToCreteHoleForPlugHousing001"
  Placement = pos=(70,19,36) rot=(0,1,0;1.5708rad)
  Shapes = -> [Cylinder008,Cylinder009]
FEATURE [Part::Cut] Cut005  label="plugHousingTab"
  Base = -> Box001
  Tool = -> Fusion027
FEATURE [Part::MultiFuse] Fusion028  label="plugHousing045"
  Shapes = -> [Fusion024,Cut005]
FEATURE [Part::Box] Box002  label="Cube002"
  AttacherType = Attacher::AttachEngine3D
  Height = 28.8
  Length = 3
  Placement = pos=(107.3,28,21.6) rot=(0,0,1;0rad)
  Width = 7
FEATURE [Part::Box] Box003  label="Cube003"
  AttacherType = Attacher::AttachEngine3D
  Height = 3
  Length = 6.4
  Placement = pos=(107.3,28,18.6) rot=(0,0,1;0rad)
  Width = 7
FEATURE [Part::Box] Box004  label="Cube004"
  AttacherType = Attacher::AttachEngine3D
  Height = 3
  Length = 6.4
  Placement = pos=(107.3,28,50.4) rot=(0,0,1;0rad)
  Width = 7
FEATURE [Part::MultiFuse] Fusion029  label="plugHousingBracketHolder"
  Shapes = -> [Box004,Box002,Box003]
FEATURE [Part::Cylinder] Cylinder010
  Angle = 360
  AttacherType = Attacher::AttachEngine3D
  Height = 20
  Placement = pos=(0,0,36.15) rot=(0,0,1;0rad)
  Radius = 14.3
FEATURE [Part::Cylinder] Cylinder011
  Angle = 360
  AttacherType = Attacher::AttachEngine3D
  Height = 10
  Placement = pos=(0,0,36.15) rot=(0,0,1;0rad)
  Radius = 4
FEATURE [Part::MultiFuse] Fusion030  label="removeToCreteHoleForPlugHousing002"
  Placement = pos=(70,19,36) rot=(0,1,0;1.5708rad)
  Shapes = -> [Cylinder010,Cylinder011]
FEATURE [Part::Cut] Cut006  label="plugHousingBracketHolder001"
  Base = -> Fusion029
  Tool = -> Fusion030
FEATURE [Part::Cylinder] Cylinder012
  Angle = 360
  AttacherType = Attacher::AttachEngine3D
  Height = 20
  Placement = pos=(0,0,36.15) rot=(0,0,1;0rad)
  Radius = 7
FEATURE [Part::Cylinder] Cylinder013
  Angle = 360
  AttacherType = Attacher::AttachEngine3D
  Height = 10
  Placement = pos=(0,0,36.15) rot=(0,0,1;0rad)
  Radius = 4
FEATURE [Part::MultiFuse] Fusion032  label="removeToCreteHoleForPlugHousing003"
  Placement = pos=(70,19,36) rot=(0,1,0;1.5708rad)
  Shapes = -> [Cylinder012,Cylinder013]
FEATURE [Part::Cut] Cut007  label="bottom002"
  Base = -> Cut002
  Tool = -> Fusion032
FEATURE [Sketcher::SketchObject] Sketch008
  FullyConstrained = true
  sketch-geometry (54):
    g0: LineSegment StartX=-4.2 StartY=0 StartZ=0 EndX=-6.2 EndY=0 EndZ=0
    g1: LineSegment StartX=-14 StartY=-18 StartZ=0 EndX=-14 EndY=-26.5 EndZ=0
    g2: LineSegment StartX=-4.2 StartY=0 StartZ=0 EndX=-4.2 EndY=-13.4877 EndZ=0
    g3: Circle CenterX=-4.2 CenterY=-13.4877 CenterZ=0 NormalX=0 NormalY=0 NormalZ=1 AngleXU=0 Radius=1
    g4: Circle CenterX=-4.2 CenterY=-26.5 CenterZ=0 NormalX=0 NormalY=0 NormalZ=1 AngleXU=0 Radius=1
    g5: Circle CenterX=-8.2 CenterY=-26.5 CenterZ=0 NormalX=0 NormalY=0 NormalZ=1 AngleXU=0 Radius=1
    g6: BSplineCurve PolesCount=3 KnotsCount=2 Degree=2 IsPeriodic=0
    g7: GeomPoint X=-4.2 Y=-13.4877 Z=0
    g8: GeomPoint X=-8.2 Y=-26.5 Z=0
    g9: LineSegment StartX=-14 StartY=-26.5 StartZ=0 EndX=-8.2 EndY=-26.5 EndZ=0
    g10: LineSegment StartX=-10.15 StartY=-12 StartZ=0 EndX=-10.15 EndY=-14 EndZ=0
    g11: LineSegment StartX=-12.8401 StartY=-16 StartZ=0 EndX=-10.1571 EndY=-16 EndZ=0
    g12: LineSegment StartX=-10.15 StartY=-14 StartZ=0 EndX=-8.70761 EndY=-14 EndZ=0
    g13: LineSegment StartX=-12.8401 StartY=-16 StartZ=0 EndX=-12.8401 EndY=-17.6958 EndZ=0
    g14: LineSegment StartX=-10.15 StartY=-12 StartZ=0 EndX=-7.79258 EndY=-12 EndZ=0
    g15: Circle CenterX=-6.2215 CenterY=-2 CenterZ=0 NormalX=0 NormalY=0 NormalZ=1 AngleXU=0 Radius=1
    g16: Circle CenterX=-6.22762 CenterY=-2.58724 CenterZ=0 NormalX=0 NormalY=0 NormalZ=1 AngleXU=0 Radius=1
    g17: Circle CenterX=-6.32538 CenterY=-4 CenterZ=0 NormalX=0 NormalY=0 NormalZ=1 AngleXU=0 Radius=1
    g18: BSplineCurve PolesCount=3 KnotsCount=2 Degree=2 IsPeriodic=0
    g19: GeomPoint X=-6.2215 Y=-2 Z=0
    g20: GeomPoint X=-6.32538 Y=-4 Z=0
    g21: Circle CenterX=-6.48644 CenterY=-5.99526 CenterZ=0 NormalX=0 NormalY=0 NormalZ=1 AngleXU=0 Radius=1
    g22: Circle CenterX=-6.58486 CenterY=-6.99526 CenterZ=0 NormalX=0 NormalY=0 NormalZ=1 AngleXU=0 Radius=1
    g23: Circle CenterX=-6.77343 CenterY=-8 CenterZ=0 NormalX=0 NormalY=0 NormalZ=1 AngleXU=0 Radius=1
    g24: BSplineCurve PolesCount=3 KnotsCount=2 Degree=2 IsPeriodic=0
    g25: GeomPoint X=-6.48644 Y=-5.99526 Z=0
    g26: GeomPoint X=-6.77343 Y=-8 Z=0
    g27: Circle CenterX=-7.19003 CenterY=-10 CenterZ=0 NormalX=0 NormalY=0 NormalZ=1 AngleXU=0 Radius=1
    g28: Circle CenterX=-7.44407 CenterY=-11.0915 CenterZ=0 NormalX=0 NormalY=0 NormalZ=1 AngleXU=0 Radius=1
    g29: Circle CenterX=-7.79258 CenterY=-12 CenterZ=0 NormalX=0 NormalY=0 NormalZ=1 AngleXU=0 Radius=1
    g30: BSplineCurve PolesCount=3 KnotsCount=2 Degree=2 IsPeriodic=0
    g31: GeomPoint X=-7.19003 Y=-10 Z=0
    g32: GeomPoint X=-7.79258 Y=-12 Z=0
    g33: Circle CenterX=-8.70761 CenterY=-14 CenterZ=0 NormalX=0 NormalY=0 NormalZ=1 AngleXU=0 Radius=1
    g34: Circle CenterX=-9.33087 CenterY=-15.1837 CenterZ=0 NormalX=0 NormalY=0 NormalZ=1 AngleXU=0 Radius=1
    g35: Circle CenterX=-10.1571 CenterY=-16 CenterZ=0 NormalX=0 NormalY=0 NormalZ=1 AngleXU=0 Radius=1
    g36: BSplineCurve PolesCount=3 KnotsCount=2 Degree=2 IsPeriodic=0
    g37: GeomPoint X=-8.70761 Y=-14 Z=0
    g38: GeomPoint X=-10.1571 Y=-16 Z=0
    g39: Circle CenterX=-12.8401 CenterY=-17.6958 CenterZ=0 NormalX=0 NormalY=0 NormalZ=1 AngleXU=0 Radius=1
    g40: Circle CenterX=-13.3521 CenterY=-17.9027 CenterZ=0 NormalX=0 NormalY=0 NormalZ=1 AngleXU=0 Radius=1
    g41: Circle CenterX=-14 CenterY=-18 CenterZ=0 NormalX=0 NormalY=0 NormalZ=1 AngleXU=0 Radius=1
    g42: BSplineCurve PolesCount=3 KnotsCount=2 Degree=2 IsPeriodic=0
    g43: GeomPoint X=-12.8401 Y=-17.6958 Z=0
    g44: GeomPoint X=-14 Y=-18 Z=0
    g45: LineSegment StartX=-6.2 StartY=0 StartZ=0 EndX=-7.2 EndY=0 EndZ=0
    g46: LineSegment StartX=-7.2 StartY=0 StartZ=0 EndX=-7.2 EndY=-2 EndZ=0
    g47: LineSegment StartX=-7.2 StartY=-2 StartZ=0 EndX=-6.2215 EndY=-2 EndZ=0
    g48: LineSegment StartX=-6.32538 StartY=-4 StartZ=0 EndX=-7.65538 EndY=-4 EndZ=0
    g49: LineSegment StartX=-7.65538 StartY=-4 StartZ=0 EndX=-7.65538 EndY=-5.99526 EndZ=0
    g50: LineSegment StartX=-7.65538 StartY=-5.99526 StartZ=0 EndX=-6.48644 EndY=-5.99526 EndZ=0
    g51: LineSegment StartX=-6.77343 StartY=-8 StartZ=0 EndX=-8.43343 EndY=-8 EndZ=0
    g52: LineSegment StartX=-8.43343 StartY=-8 StartZ=0 EndX=-8.43343 EndY=-10 EndZ=0
    g53: LineSegment StartX=-8.43343 StartY=-10 StartZ=0 EndX=-7.19003 EndY=-10 EndZ=0
  constraints (112):
    c: Horizontal(g0)
    c: Distance(g0) = 2
    c: Block(g0)
    c: Vertical(g1)
    c: Coincident(g2,g0)
    c: Vertical(g2)
    c: Block(g2)
    c: Coincident(g6,g2)
    c: Weight(g3) = 1
    c: Equal(g3,g4)
    c: Equal(g3,g5)
    c: InternalAlignment(g3,g6)
    c: InternalAlignment(g4,g6)
    c: InternalAlignment(g5,g6)
    c: InternalAlignment(g7,g6)
    c: InternalAlignment(g8,g6)
    c: Block(g6)
    c: Coincident(g9,g1)
    c: Coincident(g9,g6)
    c: Horizontal(g9)
    c: Vertical(g10)
    c: Block(g10)
    c: Horizontal(g11)
    c: Block(g11)
    c: Coincident(g12,g10)
    c: Horizontal(g12)
    c: Block(g12)
    c: Coincident(g13,g11)
    c: Vertical(g13)
    c: Block(g13)
    c: Coincident(g14,g10)
    c: Horizontal(g14)
    c: Block(g14)
    c: Block(g9)
    c: Block(g1)
    c: Weight(g15) = 1
    c: Equal(g15,g16)
    c: Equal(g15,g17)
    c: InternalAlignment(g15,g18)
    c: InternalAlignment(g16,g18)
    c: InternalAlignment(g17,g18)
    c: InternalAlignment(g19,g18)
    c: InternalAlignment(g20,g18)
    c: Weight(g21) = 1
    c: Equal(g21,g22)
    c: Equal(g21,g23)
    c: InternalAlignment(g21,g24)
    c: InternalAlignment(g22,g24)
    c: InternalAlignment(g23,g24)
    c: InternalAlignment(g25,g24)
    c: InternalAlignment(g26,g24)
    c: Weight(g27) = 1
    c: Equal(g27,g28)
    c: Equal(g27,g29)
    c: Coincident(g30,g14)
    c: InternalAlignment(g27,g30)
    c: InternalAlignment(g28,g30)
    c: InternalAlignment(g29,g30)
    c: InternalAlignment(g31,g30)
    c: InternalAlignment(g32,g30)
    c: Coincident(g36,g12)
    c: Weight(g33) = 1
    c: Equal(g33,g34)
    c: Equal(g33,g35)
    c: Coincident(g36,g11)
    c: InternalAlignment(g33,g36)
    c: InternalAlignment(g34,g36)
    c: InternalAlignment(g35,g36)
    c: InternalAlignment(g37,g36)
    c: InternalAlignment(g38,g36)
    c: Coincident(g42,g13)
    c: Weight(g39) = 1
    c: Equal(g39,g40)
    c: Equal(g39,g41)
    c: Coincident(g42,g1)
    c: InternalAlignment(g39,g42)
    c: InternalAlignment(g40,g42)
    c: InternalAlignment(g41,g42)
    c: InternalAlignment(g43,g42)
    c: InternalAlignment(g44,g42)
    c: Block(g18)
    c: Block(g24)
    c: Block(g30)
    c: Block(g36)
    c: Block(g42)
    c: Horizontal(g45)
    c: Coincident(g45,g0)
    c: Vertical(g46)
    c: Coincident(g46,g45)
    c: Coincident(g47,g46)
    c: Coincident(g47,g18)
    c: Horizontal(g47)
    c: Block(g46)
    c: Coincident(g48,g18)
    c: Horizontal(g48)
    c: Distance(g48) = 1.33
    c: Vertical(g49)
    c: Coincident(g49,g48)
    c: Coincident(g50,g49)
    c: Coincident(g50,g24)
    c: Horizontal(g50)
    c: Tangent(g50,g22)
    c: Horizontal(g51)
    c: Coincident(g51,g24)
    c: Block(g51)
    c: Vertical(g52)
    c: Block(g52)
    c: Coincident(g52,g51)
    c: Coincident(g53,g52)
    c: Coincident(g53,g30)
    c: Horizontal(g53)
    c: Distance(g1) = 8.5
FEATURE [Part::Feature] Face024
  shape: bbox 9.8 x 26.5 x 2e-07 mm, 1 faces, 0 solids (baked)
FEATURE [Part::Revolution] Revolve024
  Angle = 360
  Axis = (0,1,0)
  Base = (0,0,0)
  FaceMakerClass = Part::FaceMakerBullseye
  Placement = pos=(0,0,0) rot=(0,0,1;1.5708rad)
  Solid = false
  Source = -> Face024
  Symmetric = false
FEATURE [Part::Feature] Face025
  shape: bbox 9.8 x 26.5 x 2e-07 mm, 1 faces, 0 solids (baked)
FEATURE [Part::Revolution] Revolve025
  Angle = 360
  Axis = (0,1,0)
  Base = (0,0,0)
  FaceMakerClass = Part::FaceMakerBullseye
  Placement = pos=(0,0,0) rot=(0,0,1;1.5708rad)
  Solid = false
  Source = -> Face025
  Symmetric = false
FEATURE [Part::MultiFuse] Fusion033
  Placement = pos=(-18,19,36) rot=(0,0,1;0rad)
  Shapes = -> [Revolve025,Revolve024]
FEATURE [Part::Cylinder] Cylinder014
  Angle = 360
  AttacherType = Attacher::AttachEngine3D
  Height = 20
  Placement = pos=(0,0,36.15) rot=(0,0,1;0rad)
  Radius = 14.3
FEATURE [Part::Cylinder] Cylinder015
  Angle = 360
  AttacherType = Attacher::AttachEngine3D
  Height = 10
  Placement = pos=(0,0,36.15) rot=(0,0,1;0rad)
  Radius = 4
FEATURE [Part::MultiFuse] Fusion034  label="removeToCreteHoleForPlugHousing004"
  Placement = pos=(-42,19,36) rot=(0,1,0;1.5708rad)
  Shapes = -> [Cylinder014,Cylinder015]
FEATURE [Part::Cut] Cut008  label="top004"
  Base = -> Cut004
  Placement = pos=(-1,0,0) rot=(0,0,1;0rad)
  Tool = -> Fusion034
FEATURE [Part::Box] Box005  label="Cube005"
  AttacherType = Attacher::AttachEngine3D
  Height = 28
  Length = 3
  Placement = pos=(110.7,19,22) rot=(0,0,1;0rad)
  Width = 15.7
FEATURE [Part::Cylinder] Cylinder016
  Angle = 360
  AttacherType = Attacher::AttachEngine3D
  Height = 10
  Placement = pos=(0,0,36.15) rot=(0,0,1;0rad)
  Radius = 4
FEATURE [Part::Cylinder] Cylinder017
  Angle = 360
  AttacherType = Attacher::AttachEngine3D
  Height = 20
  Placement = pos=(0,0,36.15) rot=(0,0,1;0rad)
  Radius = 10.3
FEATURE [Part::MultiFuse] Fusion035  label="removeToCreteHoleForPlugHousing005"
  Placement = pos=(70,19,36) rot=(0,1,0;1.5708rad)
  Shapes = -> [Cylinder017,Cylinder016]
FEATURE [Part::Cut] Cut009  label="plugHousingTab001"
  Base = -> Box005
  Placement = pos=(-107.4,-14,0) rot=(0,0,1;0rad)
  Tool = -> Fusion035
FEATURE [Part::Box] Box006  label="Cube006"
  AttacherType = Attacher::AttachEngine3D
  Height = 28
  Length = 3
  Placement = pos=(110.7,19,22) rot=(0,0,1;0rad)
  Width = 15.7
FEATURE [Part::Cylinder] Cylinder018
  Angle = 360
  AttacherType = Attacher::AttachEngine3D
  Height = 10
  Placement = pos=(0,0,36.15) rot=(0,0,1;0rad)
  Radius = 4
FEATURE [Part::Cylinder] Cylinder019
  Angle = 360
  AttacherType = Attacher::AttachEngine3D
  Height = 20
  Placement = pos=(0,0,36.15) rot=(0,0,1;0rad)
  Radius = 10.3
FEATURE [Part::MultiFuse] Fusion036  label="removeToCreteHoleForPlugHousing006"
  Placement = pos=(70,19,36) rot=(0,1,0;1.5708rad)
  Shapes = -> [Cylinder019,Cylinder018]
FEATURE [Part::Cut] Cut010  label="plugHousingTab002"
  Base = -> Box006
  Placement = pos=(-107.4,-14,0) rot=(0,0,1;0rad)
  Tool = -> Fusion036
FEATURE [Part::MultiFuse] Fusion037
  Placement = pos=(9.6,23,0) rot=(0,0,1;3.14159rad)
  Shapes = -> [Cut009,Cut010]
FEATURE [Part::Box] Box  label="Cube"
  AttacherType = Attacher::AttachEngine3D
  Height = 10
  Length = 3
  Placement = pos=(3.3,4,12) rot=(0,0,1;0rad)
  Width = 10
FEATURE [Part::Fillet] Fillet004
  Base = -> Fusion028
  Edges = 1 edges r=2: [Edge25]
FEATURE [Part::Fillet] Fillet005  label="plugHousing046"
  Base = -> Fillet004
  Edges = 1 edges r=2: [Edge8]
FEATURE [Part::Fillet] Fillet006
  Base = -> Box
  Edges = 1 edges r=2: [Edge11]
FEATURE [Part::Box] Box007  label="Cube007"
  AttacherType = Attacher::AttachEngine3D
  Height = 10
  Length = 3
  Placement = pos=(3.3,4,50) rot=(0,0,1;0rad)
  Width = 10
FEATURE [Part::Fillet] Fillet007
  Base = -> Box007
  Edges = 1 edges r=2: [Edge12]
FEATURE [Part::Box] Box008  label="Cube008"
  AttacherType = Attacher::AttachEngine3D
  Height = 28
  Length = 4
  Placement = pos=(5,0,22) rot=(0,0,1;0rad)
  Width = 10
FEATURE [Part::Fillet] Fillet008
  Base = -> Box008
  Edges = 1 edges r=1: [Edge7]
FEATURE [Part::Fillet] Fillet009
  Base = -> Fillet008
  Edges = 1 edges r=2: [Edge5]
FEATURE [Part::Fillet] Fillet010
  Base = -> Fillet009
  Edges = 1 edges r=2: [Edge2]
FEATURE [Sketcher::SketchObject] Sketch009  label="topSketch003"
  FullyConstrained = true
  sketch-geometry (4):
    g0: LineSegment StartX=16.8446 StartY=31.512 StartZ=0 EndX=16.3251 EndY=34.4666 EndZ=0
    g1: ArcOfCircle CenterX=19 CenterY=19.2524 CenterZ=0 NormalX=0 NormalY=0 NormalZ=1 AngleXU=0 Radius=15.4476 StartAngle=1.74483 EndAngle=2.72717
    g2: ArcOfCircle CenterX=19 CenterY=19.2524 CenterZ=0 NormalX=0 NormalY=0 NormalZ=1 AngleXU=0 Radius=12.4476 StartAngle=1.74483 EndAngle=2.73189
    g3: LineSegment StartX=4.86004 StartY=25.4725 StartZ=0 EndX=7.58253 EndY=24.2107 EndZ=0
  constraints (7):
    c: Block(g0)
    c: Coincident(g1,g0)
    c: Coincident(g2,g0)
    c: Coincident(g3,g1)
    c: Coincident(g3,g2)
    c: Block(g1)
    c: Block(g2)
FEATURE [Part::Extrusion] Extrude008
  Base = -> Sketch009
  Dir = (0,0,1)
  DirMode = 2
  FaceMakerClass = Part::FaceMakerBullseye
  LengthFwd = 10
  LengthRev = 0
  Placement = pos=(0,0,31) rot=(0,0,1;0rad)
  Solid = true
  Symmetric = false
FEATURE [Part::Cylinder] Cylinder020
  Angle = 360
  AttacherType = Attacher::AttachEngine3D
  Height = 20
  Placement = pos=(0,0,36.15) rot=(0,0,1;0rad)
  Radius = 8.2
FEATURE [Part::Cylinder] Cylinder021
  Angle = 360
  AttacherType = Attacher::AttachEngine3D
  Height = 10
  Placement = pos=(0,0,36.15) rot=(0,0,1;0rad)
  Radius = 4
FEATURE [Part::MultiFuse] Fusion038  label="removeToCreteHoleForPlugHousing007"
  Placement = pos=(-42,19,36) rot=(0,1,0;1.5708rad)
  Shapes = -> [Cylinder020,Cylinder021]
FEATURE [Part::Cut] Cut011
  Base = -> Extrude008
  Tool = -> Fusion038
FEATURE [Part::Fillet] Fillet011
  Base = -> Cut011
  Edges = 1 edges r=2: [Edge1]
FEATURE [Part::Fillet] Fillet012
  Base = -> Fillet011
  Edges = 1 edges r=2.5: [Edge1]
FEATURE [Part::Fillet] Fillet013
  Base = -> Fillet012
  Edges = 1 edges r=2.5: [Edge2]
FEATURE [Part::Box] Box010  label="Cube010"
  AttacherType = Attacher::AttachEngine3D
  Height = 16
  Length = 8
  Placement = pos=(12.7,31.52,28) rot=(0,0,1;0rad)
  Width = 4
FEATURE [Sketcher::SketchObject] Sketch010  label="topSketch004"
  FullyConstrained = true
  sketch-geometry (4):
    g0: LineSegment StartX=16.8446 StartY=31.512 StartZ=0 EndX=16.3251 EndY=34.4666 EndZ=0
    g1: ArcOfCircle CenterX=19 CenterY=19.2524 CenterZ=0 NormalX=0 NormalY=0 NormalZ=1 AngleXU=0 Radius=15.4476 StartAngle=1.74483 EndAngle=2.72717
    g2: ArcOfCircle CenterX=19 CenterY=19.2524 CenterZ=0 NormalX=0 NormalY=0 NormalZ=1 AngleXU=0 Radius=12.4476 StartAngle=1.74483 EndAngle=2.73189
    g3: LineSegment StartX=4.86004 StartY=25.4725 StartZ=0 EndX=7.58253 EndY=24.2107 EndZ=0
  constraints (7):
    c: Block(g0)
    c: Coincident(g1,g0)
    c: Coincident(g2,g0)
    c: Coincident(g3,g1)
    c: Coincident(g3,g2)
    c: Block(g1)
    c: Block(g2)
FEATURE [Part::Cylinder] Cylinder022
  Angle = 360
  AttacherType = Attacher::AttachEngine3D
  Height = 10
  Placement = pos=(0,0,36.15) rot=(0,0,1;0rad)
  Radius = 4
FEATURE [Sketcher::SketchObject] Sketch011  label="topSketch005"
  FullyConstrained = true
  sketch-geometry (4):
    g0: LineSegment StartX=16.8446 StartY=31.512 StartZ=0 EndX=16.3251 EndY=34.4666 EndZ=0
    g1: ArcOfCircle CenterX=19 CenterY=19.2524 CenterZ=0 NormalX=0 NormalY=0 NormalZ=1 AngleXU=0 Radius=15.4476 StartAngle=1.74483 EndAngle=2.72717
    g2: ArcOfCircle CenterX=19 CenterY=19.2524 CenterZ=0 NormalX=0 NormalY=0 NormalZ=1 AngleXU=0 Radius=12.4476 StartAngle=1.74483 EndAngle=2.73189
    g3: LineSegment StartX=4.86004 StartY=25.4725 StartZ=0 EndX=7.58253 EndY=24.2107 EndZ=0
  constraints (7):
    c: Block(g0)
    c: Coincident(g1,g0)
    c: Coincident(g2,g0)
    c: Coincident(g3,g1)
    c: Coincident(g3,g2)
    c: Block(g1)
    c: Block(g2)
FEATURE [Part::Extrusion] Extrude010
  Base = -> Sketch011
  Dir = (0,0,1)
  DirMode = 2
  FaceMakerClass = Part::FaceMakerBullseye
  LengthFwd = 10.6
  LengthRev = 0
  Placement = pos=(0,0,31) rot=(0,0,1;0rad)
  Solid = true
  Symmetric = false
FEATURE [Part::Cylinder] Cylinder023
  Angle = 360
  AttacherType = Attacher::AttachEngine3D
  Height = 20
  Placement = pos=(0,0,36.15) rot=(0,0,1;0rad)
  Radius = 8.2
FEATURE [Part::MultiFuse] Fusion039  label="removeToCreteHoleForPlugHousing008"
  Placement = pos=(-42,19,36) rot=(0,1,0;1.5708rad)
  Shapes = -> [Cylinder023,Cylinder022]
FEATURE [Part::Cut] Cut012
  Base = -> Extrude010
  Placement = pos=(0,0,-0.3) rot=(0,0,1;0rad)
  Tool = -> Fusion039
FEATURE [Part::Cut] Cut013
  Base = -> Box010
  Tool = -> Cut012
FEATURE [Part::Fillet] Fillet014
  Base = -> Cut013
  Edges = 1 edges r=0.7: [Edge13]
FEATURE [Part::Fillet] Fillet015
  Base = -> Fillet014
  Edges = 1 edges r=0.7: [Edge13]
FEATURE [Part::Fillet] Fillet016
  Base = -> Fillet015
  Edges = 1 edges r=0.7: [Edge16]
FEATURE [Part::Fillet] Fillet017
  Base = -> Fillet016
  Edges = 1 edges r=0.7: [Edge11]
FEATURE [Part::Fillet] Fillet018
  Base = -> Fillet017
  Edges = 1 edges r=0.7: [Edge10]
FEATURE [Part::Fillet] Fillet019
  Base = -> Fillet018
  Edges = 1 edges r=1.2: [Edge5]
FEATURE [Part::Fillet] Fillet020
  Base = -> Fillet019
  Edges = 1 edges r=1.2: [Edge12]
FEATURE [Part::Fillet] Fillet021
  Base = -> Fillet020
  Edges = 1 edges r=2: [Edge1]
  Placement = pos=(0.3,0,0) rot=(0,0,1;0rad)
FEATURE [Part::MultiFuse] Fusion040  label="top005"
  Shapes = -> [Cut008,Fillet021]
FEATURE [Part::MultiFuse] Fusion041  label="wireHolder"
  Shapes = -> [Fusion033,Fillet013]
FEATURE [Part::MultiFuse] Fusion042
  Shapes = -> [Fillet007,Fusion041]
FEATURE [Part::MultiFuse] Fusion043  label="wireHolder001"
  Shapes = -> [Fusion042,Fillet010]
FEATURE [Part::MultiFuse] Fusion044  label="wireHolder002"
  Shapes = -> [Fillet006,Fusion037,Fusion043]
FEATURE [Part::Feature] Face026
  shape: bbox 11 x 6 x 2e-07 mm, 1 faces, 0 solids (baked)
FEATURE [Part::Revolution] Revolve026
  Angle = 360
  Axis = (0,1,0)
  Base = (0,0,0)
  FaceMakerClass = Part::FaceMakerBullseye
  Placement = pos=(30.3,-1,19.7) rot=(0,0,1;0rad)
  Solid = false
  Source = -> Face026
  Symmetric = false
FEATURE [Sketcher::SketchObject] Sketch013  label="topSketch006"
  FullyConstrained = true
  sketch-geometry (13):
    g0: LineSegment StartX=117 StartY=19 StartZ=0 EndX=117 EndY=38 EndZ=0
    g1: ArcOfCircle CenterX=98 CenterY=19 CenterZ=0 NormalX=0 NormalY=0 NormalZ=1 AngleXU=0 Radius=19 StartAngle=5.7297 EndAngle=6.28319
    g2: LineSegment StartX=0 StartY=3 StartZ=0 EndX=0 EndY=19 EndZ=0
    g3: LineSegment StartX=19 StartY=38 StartZ=0 EndX=117 EndY=38 EndZ=0
    g4: ArcOfCircle CenterX=19 CenterY=19 CenterZ=0 NormalX=0 NormalY=0 NormalZ=1 AngleXU=0 Radius=19 StartAngle=1.5708 EndAngle=3.14159
    g5: ArcOfCircle CenterX=19 CenterY=19 CenterZ=0 NormalX=0 NormalY=0 NormalZ=1 AngleXU=0 Radius=16 StartAngle=1.5708 EndAngle=3.14159
    g6: ArcOfCircle CenterX=98 CenterY=19 CenterZ=0 NormalX=0 NormalY=0 NormalZ=1 AngleXU=0 Radius=16 StartAngle=5.60905 EndAngle=6.28319
    g7: LineSegment StartX=114 StartY=19 StartZ=0 EndX=114 EndY=35 EndZ=0
    g8: LineSegment StartX=110.5 StartY=9.01251 StartZ=0 EndX=114.163 EndY=9.01251 EndZ=0
    g9: LineSegment StartX=114 StartY=35 StartZ=0 EndX=19 EndY=35 EndZ=0
    g10: LineSegment StartX=0 StartY=3 StartZ=0 EndX=0 EndY=0 EndZ=0
    g11: LineSegment StartX=3 StartY=0 StartZ=0 EndX=0 EndY=0 EndZ=0
    g12: LineSegment StartX=3 StartY=19 StartZ=0 EndX=3 EndY=0 EndZ=0
  constraints (33):
    c: Vertical(g0)
    c: Distance(g0) = 19
    c: Block(g0)
    c: Coincident(g1,g0)
    c: Block(g1)
    c: Vertical(g2)
    c: Block(g2)
    c: Coincident(g3,g0)
    c: Horizontal(g3)
    c: Distance(g3) = 98
    c: Coincident(g4,g3)
    c: Coincident(g4,g2)
    c: Block(g4)
    c: Coincident(g5,g4)
    c: Coincident(g6,g1)
    c: Block(g6)
    c: Block(g5)
    c: Coincident(g7,g6)
    c: Vertical(g7)
    c: Coincident(g8,g6)
    c: Coincident(g8,g1)
    c: Coincident(g9,g7)
    c: Coincident(g9,g5)
    c: Horizontal(g9)
    c: Tangent(g9,g5)
    c: Coincident(g10,g2)
    c: Distance(g10) = 3
    c: Vertical(g10)
    c: Coincident(g11,g10)
    c: Horizontal(g11)
    c: Coincident(g12,g5)
    c: Coincident(g12,g11)
    c: Vertical(g12)
FEATURE [Part::Extrusion] Extrude011  label="top006"
  Base = -> Sketch013
  Dir = (0,0,1)
  DirMode = 2
  FaceMakerClass = Part::FaceMakerBullseye
  LengthFwd = 72
  LengthRev = 0
  Solid = true
  Symmetric = false
FEATURE [Sketcher::SketchObject] Sketch014
  FullyConstrained = true
  MapMode = 3
  Placement = pos=(0,0,0) rot=(1,0,0;1.5708rad)
  Support = -> [Extrude011]
  sketch-geometry (8):
    g0: Circle CenterX=80.351 CenterY=-67.6202 CenterZ=0 NormalX=0 NormalY=0 NormalZ=1 AngleXU=0 Radius=2
    g1: Circle CenterX=80.351 CenterY=-67.6202 CenterZ=0 NormalX=0 NormalY=0 NormalZ=1 AngleXU=0 Radius=3
    g2: Circle CenterX=80.351 CenterY=-4.92017 CenterZ=0 NormalX=0 NormalY=0 NormalZ=1 AngleXU=0 Radius=2
    g3: Circle CenterX=80.351 CenterY=-4.92017 CenterZ=0 NormalX=0 NormalY=0 NormalZ=1 AngleXU=0 Radius=3
    g4: Circle CenterX=23.851 CenterY=-4.92017 CenterZ=0 NormalX=0 NormalY=0 NormalZ=1 AngleXU=0 Radius=2
    g5: Circle CenterX=23.851 CenterY=-4.92017 CenterZ=0 NormalX=0 NormalY=0 NormalZ=1 AngleXU=0 Radius=3
    g6: Circle CenterX=23.851 CenterY=-67.6202 CenterZ=0 NormalX=0 NormalY=0 NormalZ=1 AngleXU=0 Radius=2
    g7: Circle CenterX=23.851 CenterY=-67.6202 CenterZ=0 NormalX=0 NormalY=0 NormalZ=1 AngleXU=0 Radius=3
  constraints (8):
    c: Block(g3)
    c: Block(g2)
    c: Block(g1)
    c: Block(g0)
    c: Block(g6)
    c: Block(g7)
    c: Block(g4)
    c: Block(g5)
FEATURE [Part::Feature] Face027
  shape: bbox 11 x 6 x 2e-07 mm, 1 faces, 0 solids (baked)
FEATURE [Part::Revolution] Revolve027
  Angle = 360
  Axis = (0,1,0)
  Base = (0,0,0)
  FaceMakerClass = Part::FaceMakerBullseye
  Placement = pos=(30.3,-1,51.7) rot=(0,0,1;0rad)
  Solid = false
  Source = -> Face027
  Symmetric = false
FEATURE [Part::Feature] Face028
  shape: bbox 11 x 6 x 2e-07 mm, 1 faces, 0 solids (baked)
FEATURE [Part::Revolution] Revolve028
  Angle = 360
  Axis = (0,1,0)
  Base = (0,0,0)
  FaceMakerClass = Part::FaceMakerBullseye
  Placement = pos=(62.3,-1,19.7) rot=(0,0,1;0rad)
  Solid = false
  Source = -> Face028
  Symmetric = false
FEATURE [Part::Feature] Face029
  shape: bbox 11 x 6 x 2e-07 mm, 1 faces, 0 solids (baked)
FEATURE [Part::Revolution] Revolve029
  Angle = 360
  Axis = (0,1,0)
  Base = (0,0,0)
  FaceMakerClass = Part::FaceMakerBullseye
  Placement = pos=(62.3,-1,51.7) rot=(0,0,1;0rad)
  Solid = false
  Source = -> Face029
  Symmetric = false
FEATURE [Part::Feature] Wire
  shape: bbox 11 x 5.2 x 2e-07 mm, 0 faces, 0 solids (baked)
FEATURE [Part::Revolution] Revolve030
  Angle = 360
  Axis = (0,1,0)
  Base = (0,0,0)
  FaceMakerClass = Part::FaceMakerBullseye
  Placement = pos=(30.3,38,19.7) rot=(0,0,1;0rad)
  Solid = true
  Source = -> Wire
  Symmetric = false
FEATURE [Part::Feature] Wire001
  shape: bbox 11 x 5.2 x 2e-07 mm, 0 faces, 0 solids (baked)
FEATURE [Part::Revolution] Revolve031
  Angle = 360
  Axis = (0,1,0)
  Base = (0,0,0)
  FaceMakerClass = Part::FaceMakerBullseye
  Placement = pos=(30.3,38,51.7) rot=(0,0,1;0rad)
  Solid = true
  Source = -> Wire001
  Symmetric = false
FEATURE [Part::Feature] Wire002
  shape: bbox 11 x 5.2 x 2e-07 mm, 0 faces, 0 solids (baked)
FEATURE [Part::Revolution] Revolve032
  Angle = 360
  Axis = (0,1,0)
  Base = (0,0,0)
  FaceMakerClass = Part::FaceMakerBullseye
  Placement = pos=(62.3,38,51.7) rot=(0,0,1;0rad)
  Solid = true
  Source = -> Wire002
  Symmetric = false
FEATURE [Part::Feature] Wire003
  shape: bbox 11 x 5.2 x 2e-07 mm, 0 faces, 0 solids (baked)
FEATURE [Part::Revolution] Revolve033
  Angle = 360
  Axis = (0,1,0)
  Base = (0,0,0)
  FaceMakerClass = Part::FaceMakerBullseye
  Placement = pos=(62.3,38,19.7) rot=(0,0,1;0rad)
  Solid = true
  Source = -> Wire003
  Symmetric = false
FEATURE [Part::MultiFuse] Fusion045  label="altRandScrewHousing"
  Shapes = -> [Revolve029,Revolve027,Revolve028,Revolve026]
FEATURE [Part::MultiFuse] Fusion046  label="fanScrewHousing"
  Shapes = -> [Revolve033,Revolve032,Revolve031,Revolve030]
FEATURE [Sketcher::SketchObject] Sketch015
  FullyConstrained = true
  sketch-geometry (17):
    g0: Circle CenterX=-3.5 CenterY=23.5 CenterZ=0 NormalX=0 NormalY=0 NormalZ=1 AngleXU=0 Radius=1
    g1: Circle CenterX=-1 CenterY=15.25 CenterZ=0 NormalX=0 NormalY=0 NormalZ=1 AngleXU=0 Radius=1
    g2: Circle CenterX=-3.5 CenterY=7 CenterZ=0 NormalX=0 NormalY=0 NormalZ=1 AngleXU=0 Radius=1
    g3: BSplineCurve PolesCount=3 KnotsCount=2 Degree=2 IsPeriodic=0
    g4: GeomPoint X=-3.5 Y=23.5 Z=0
    g5: GeomPoint X=-3.5 Y=7 Z=0
    g6: Circle CenterX=-4.8 CenterY=30.5 CenterZ=0 NormalX=0 NormalY=0 NormalZ=1 AngleXU=0 Radius=1
    g7: Circle CenterX=-3.5 CenterY=30.5 CenterZ=0 NormalX=0 NormalY=0 NormalZ=1 AngleXU=0 Radius=1
    g8: Circle CenterX=-3.5 CenterY=29.2 CenterZ=0 NormalX=0 NormalY=0 NormalZ=1 AngleXU=0 Radius=1
    g9: BSplineCurve PolesCount=3 KnotsCount=2 Degree=2 IsPeriodic=0
    g10: GeomPoint X=-4.8 Y=30.5 Z=0
    g11: GeomPoint X=-3.5 Y=29.2 Z=0
    g12: LineSegment StartX=-3.5 StartY=29.2 StartZ=0 EndX=-3.5 EndY=23.5 EndZ=0
    g13: LineSegment StartX=-4.8 StartY=30.5 StartZ=0 EndX=0 EndY=30.5 EndZ=0
    g14: LineSegment StartX=-3.5 StartY=0.3 StartZ=0 EndX=0 EndY=0.3 EndZ=0
    g15: LineSegment StartX=-3.5 StartY=0.3 StartZ=0 EndX=-3.5 EndY=7 EndZ=0
    g16: LineSegment StartX=0 StartY=0.3 StartZ=0 EndX=0 EndY=30.5 EndZ=0
  constraints (33):
    c: Weight(g0) = 1
    c: Equal(g0,g1)
    c: Equal(g0,g2)
    c: InternalAlignment(g0,g3)
    c: InternalAlignment(g1,g3)
    c: InternalAlignment(g2,g3)
    c: InternalAlignment(g4,g3)
    c: InternalAlignment(g5,g3)
    c: Block(g3)
    c: Weight(g6) = 1
    c: Equal(g6,g7)
    c: Equal(g6,g8)
    c: InternalAlignment(g6,g9)
    c: InternalAlignment(g7,g9)
    c: InternalAlignment(g8,g9)
    c: InternalAlignment(g10,g9)
    c: InternalAlignment(g11,g9)
    c: Block(g9)
    c: Coincident(g12,g9)
    c: Coincident(g12,g3)
    c: Vertical(g12)
    c: Coincident(g13,g9)
    c: Horizontal(g13)
    c: Distance(g13) = 4.8
    c: Horizontal(g14)
    c: Block(g14)
    c: Coincident(g15,g14)
    c: Coincident(g15,g3)
    c: Vertical(g15)
    c: Coincident(g16,g14)
    c: Coincident(g16,g13)
    c: Vertical(g16)
    c: Tangent(g16,g1)
FEATURE [Sketcher::SketchObject] Sketch016
  FullyConstrained = true
  sketch-geometry (16):
    g0: Circle CenterX=-3.5 CenterY=23.5 CenterZ=0 NormalX=0 NormalY=0 NormalZ=1 AngleXU=0 Radius=1
    g1: Circle CenterX=-1 CenterY=15.25 CenterZ=0 NormalX=0 NormalY=0 NormalZ=1 AngleXU=0 Radius=1
    g2: Circle CenterX=-3.5 CenterY=7 CenterZ=0 NormalX=0 NormalY=0 NormalZ=1 AngleXU=0 Radius=1
    g3: BSplineCurve PolesCount=3 KnotsCount=2 Degree=2 IsPeriodic=0
    g4: GeomPoint X=-3.5 Y=23.5 Z=0
    g5: GeomPoint X=-3.5 Y=7 Z=0
    g6: LineSegment StartX=-3.5 StartY=28.2 StartZ=0 EndX=-3.5 EndY=23.5 EndZ=0
    g7: LineSegment StartX=0 StartY=29.5 StartZ=0 EndX=0 EndY=30 EndZ=0
    g8: LineSegment StartX=-3.5 StartY=28.2 StartZ=0 EndX=-3.5 EndY=30 EndZ=0
    g9: LineSegment StartX=0 StartY=30 StartZ=0 EndX=0 EndY=30.5 EndZ=0
    g10: LineSegment StartX=0 StartY=30.5 StartZ=0 EndX=-3.5 EndY=30.5 EndZ=0
    g11: LineSegment StartX=-3.5 StartY=30.5 StartZ=0 EndX=-3.5 EndY=30 EndZ=0
    g12: LineSegment StartX=0 StartY=29.5 StartZ=0 EndX=0 EndY=5 EndZ=0
    g13: LineSegment StartX=-3.5 StartY=0.3 StartZ=0 EndX=-3.5 EndY=7 EndZ=0
    g14: LineSegment StartX=-3.5 StartY=0.3 StartZ=0 EndX=0 EndY=0.3 EndZ=0
    g15: LineSegment StartX=0 StartY=5 StartZ=0 EndX=0 EndY=0.3 EndZ=0
  constraints (39):
    c: Weight(g0) = 1
    c: Equal(g0,g1)
    c: Equal(g0,g2)
    c: InternalAlignment(g0,g3)
    c: InternalAlignment(g1,g3)
    c: InternalAlignment(g2,g3)
    c: InternalAlignment(g4,g3)
    c: InternalAlignment(g5,g3)
    c: Block(g3)
    c: Coincident(g6,g3)
    c: Vertical(g6)
    c: Vertical(g7)
    c: Distance(g7) = 0.5
    c: Coincident(g8,g6)
    c: Vertical(g8)
    c: Block(g6)
    c: Block(g7)
    c: Vertical(g9)
    c: Equal(g7,g9) = 0.5
    c: Block(g9)
    c: Coincident(g9,g7)
    c: Horizontal(g10)
    c: Coincident(g10,g9)
    c: Coincident(g11,g10)
    c: Coincident(g11,g8)
    c: Vertical(g11)
    c: Block(g11)
    c: Coincident(g12,g7)
    c: Vertical(g12)
    c: Coincident(g13,g3)
    c: Vertical(g13)
    c: Distance(g13) = 6.7
    c: Coincident(g14,g13)
    c: Horizontal(g14)
    c: Block(g14)
    c: Coincident(g15,g12)
    c: Coincident(g15,g14)
    c: Vertical(g15)
    c: Block(g15)
FEATURE [Sketcher::SketchObject] Sketch017
  FullyConstrained = true
  sketch-geometry (11):
    g0: LineSegment StartX=-3.5 StartY=1e-16 StartZ=0 EndX=-1.6 EndY=1e-16 EndZ=0
    g1: LineSegment StartX=-1.6 StartY=1e-16 StartZ=0 EndX=-1.6 EndY=1.5 EndZ=0
    g2: LineSegment StartX=-3.5 StartY=1.5 StartZ=0 EndX=-1.6 EndY=1.5 EndZ=0
    g3: LineSegment StartX=-3.5 StartY=1e-16 StartZ=0 EndX=-4.8 EndY=1e-16 EndZ=0
    g4: Circle CenterX=-3.5 CenterY=1.3 CenterZ=0 NormalX=0 NormalY=0 NormalZ=1 AngleXU=0 Radius=1
    g5: Circle CenterX=-3.5 CenterY=1e-16 CenterZ=0 NormalX=0 NormalY=0 NormalZ=1 AngleXU=0 Radius=1
    g6: Circle CenterX=-4.8 CenterY=1e-16 CenterZ=0 NormalX=0 NormalY=0 NormalZ=1 AngleXU=0 Radius=1
    g7: BSplineCurve PolesCount=3 KnotsCount=2 Degree=2 IsPeriodic=0
    g8: GeomPoint X=-3.5 Y=1.3 Z=0
    g9: GeomPoint X=-4.8 Y=1e-16 Z=0
    g10: LineSegment StartX=-3.5 StartY=1.3 StartZ=0 EndX=-3.5 EndY=1.5 EndZ=0
  constraints (24):
    c: Horizontal(g0)
    c: Distance(g0) = 1.9
    c: Block(g0)
    c: Coincident(g1,g0)
    c: Vertical(g1)
    c: Coincident(g2,g1)
    c: Horizontal(g2)
    c: Coincident(g3,g0)
    c: Horizontal(g3)
    c: Distance(g3) = 1.3
    c: Weight(g4) = 1
    c: Equal(g4,g5)
    c: Coincident(g5,g0)
    c: Equal(g4,g6)
    c: Coincident(g7,g3)
    c: InternalAlignment(g4,g7)
    c: InternalAlignment(g5,g7)
    c: InternalAlignment(g6,g7)
    c: InternalAlignment(g8,g7)
    c: InternalAlignment(g9,g7)
    c: Coincident(g10,g7)
    c: Coincident(g10,g2)
    c: Vertical(g10)
    c: Block(g10)
FEATURE [Part::Feature] Face035
  shape: bbox 3.2 x 1.5 x 2e-07 mm, 1 faces, 0 solids (baked)
FEATURE [Part::Revolution] Revolve039  label="backCaseScrewRetainer"
  Angle = 360
  Axis = (0,1,0)
  Base = (0,0,0)
  FaceMakerClass = Part::FaceMakerBullseye
  Placement = pos=(12.5,3,62) rot=(0,0,1;0rad)
  Solid = false
  Source = -> Face035
  Symmetric = false
FEATURE [Part::Feature] Face036
  shape: bbox 3.2 x 1.5 x 2e-07 mm, 1 faces, 0 solids (baked)
FEATURE [Part::Feature] Face039
  shape: bbox 4.8 x 30.2 x 2e-07 mm, 1 faces, 0 solids (baked)
FEATURE [Part::Revolution] Revolve043  label="frontCaseScrewPost002"
  Angle = 360
  Axis = (0,1,0)
  Base = (0,0,0)
  FaceMakerClass = Part::FaceMakerBullseye
  Placement = pos=(89.5,4.5,3.5) rot=(0,0,1;0rad)
  Solid = false
  Source = -> Face039
  Symmetric = false
FEATURE [Part::Feature] Face042
  shape: bbox 4.8 x 30.2 x 2e-07 mm, 1 faces, 0 solids (baked)
FEATURE [Part::Revolution] Revolve046  label="frontCaseScrewPost003"
  Angle = 360
  Axis = (0,1,0)
  Base = (0,0,0)
  FaceMakerClass = Part::FaceMakerBullseye
  Placement = pos=(89.5,4.5,68.5) rot=(0,0,1;0rad)
  Solid = false
  Source = -> Face042
  Symmetric = false
FEATURE [Part::Feature] Face043
  shape: bbox 3.2 x 1.5 x 2e-07 mm, 1 faces, 0 solids (baked)
FEATURE [Part::Revolution] Revolve047  label="frontCaseScrewRetainer002"
  Angle = 360
  Axis = (0,1,0)
  Base = (0,0,0)
  FaceMakerClass = Part::FaceMakerBullseye
  Placement = pos=(89.5,3,68.5) rot=(0,0,1;0rad)
  Solid = false
  Source = -> Face043
  Symmetric = false
FEATURE [Part::Feature] Face044
  shape: bbox 3.2 x 1.5 x 2e-07 mm, 1 faces, 0 solids (baked)
FEATURE [Part::Revolution] Revolve048  label="frontCaseScrewRetainer003"
  Angle = 360
  Axis = (0,1,0)
  Base = (0,0,0)
  FaceMakerClass = Part::FaceMakerBullseye
  Placement = pos=(89.5,3,3.5) rot=(0,0,1;0rad)
  Solid = false
  Source = -> Face044
  Symmetric = false
FEATURE [App::MeasureDistance] Distance002  label="Distance: 1.67 mm"
  Distance = 1.66921
  P1 = (99.2361,4.7524,71.7)
  P2 = (99.2347,6.42161,71.7)
FEATURE [Sketcher::SketchObject] Sketch018
  FullyConstrained = true
  sketch-geometry (7):
    g0: LineSegment StartX=0 StartY=0 StartZ=0 EndX=0 EndY=6 EndZ=0
    g1: Circle CenterX=0 CenterY=0 CenterZ=0 NormalX=0 NormalY=0 NormalZ=1 AngleXU=0 Radius=1
    g2: Circle CenterX=8 CenterY=6 CenterZ=0 NormalX=0 NormalY=0 NormalZ=1 AngleXU=0 Radius=1
    g3: BSplineCurve PolesCount=3 KnotsCount=2 Degree=2 IsPeriodic=0
    g4: GeomPoint X=0 Y=0 Z=0
    g5: GeomPoint X=8 Y=6 Z=0
    g6: LineSegment StartX=0 StartY=6 StartZ=0 EndX=8 EndY=6 EndZ=0
  constraints (14):
    c: Coincident(g0,g-1)
    c: Distance(g0) = 6
    c: Vertical(g0)
    c: Coincident(g3,g0)
    c: Weight(g1) = 1
    c: Equal(g1,g2)
    c: InternalAlignment(g1,g3)
    c: InternalAlignment(g2,g3)
    c: InternalAlignment(g4,g3)
    c: InternalAlignment(g5,g3)
    c: Block(g3)
    c: Coincident(g6,g0)
    c: Coincident(g6,g3)
    c: Horizontal(g6)
FEATURE [Part::Extrusion] Extrude012  label="caseScrewPillarBracket"
  Base = -> Sketch018
  Dir = (0,0,1)
  DirMode = 2
  FaceMakerClass = Part::FaceMakerBullseye
  LengthFwd = 2.4
  LengthRev = 0
  Placement = pos=(15.76,29,8.8) rot=(0,1,0;0rad)
  Solid = true
  Symmetric = false
FEATURE [Sketcher::SketchObject] Sketch019
  FullyConstrained = true
  sketch-geometry (7):
    g0: LineSegment StartX=0 StartY=0 StartZ=0 EndX=0 EndY=6 EndZ=0
    g1: Circle CenterX=0 CenterY=0 CenterZ=0 NormalX=0 NormalY=0 NormalZ=1 AngleXU=0 Radius=1
    g2: Circle CenterX=8 CenterY=6 CenterZ=0 NormalX=0 NormalY=0 NormalZ=1 AngleXU=0 Radius=1
    g3: BSplineCurve PolesCount=3 KnotsCount=2 Degree=2 IsPeriodic=0
    g4: GeomPoint X=0 Y=0 Z=0
    g5: GeomPoint X=8 Y=6 Z=0
    g6: LineSegment StartX=0 StartY=6 StartZ=0 EndX=8 EndY=6 EndZ=0
  constraints (14):
    c: Coincident(g0,g-1)
    c: Distance(g0) = 6
    c: Vertical(g0)
    c: Coincident(g3,g0)
    c: Weight(g1) = 1
    c: Equal(g1,g2)
    c: InternalAlignment(g1,g3)
    c: InternalAlignment(g2,g3)
    c: InternalAlignment(g4,g3)
    c: InternalAlignment(g5,g3)
    c: Block(g3)
    c: Coincident(g6,g0)
    c: Coincident(g6,g3)
    c: Horizontal(g6)
FEATURE [Part::Extrusion] Extrude013  label="caseScrewPillarBracket001"
  Base = -> Sketch019
  Dir = (0,0,1)
  DirMode = 2
  FaceMakerClass = Part::FaceMakerBullseye
  LengthFwd = 2.4
  LengthRev = 0
  Placement = pos=(15.76,29,60.8) rot=(0,0,1;0rad)
  Solid = true
  Symmetric = false
FEATURE [Sketcher::SketchObject] Sketch020
  FullyConstrained = true
  sketch-geometry (7):
    g0: LineSegment StartX=0 StartY=0 StartZ=0 EndX=0 EndY=6 EndZ=0
    g1: Circle CenterX=0 CenterY=0 CenterZ=0 NormalX=0 NormalY=0 NormalZ=1 AngleXU=0 Radius=1
    g2: Circle CenterX=8 CenterY=6 CenterZ=0 NormalX=0 NormalY=0 NormalZ=1 AngleXU=0 Radius=1
    g3: BSplineCurve PolesCount=3 KnotsCount=2 Degree=2 IsPeriodic=0
    g4: GeomPoint X=0 Y=0 Z=0
    g5: GeomPoint X=8 Y=6 Z=0
    g6: LineSegment StartX=0 StartY=6 StartZ=0 EndX=8 EndY=6 EndZ=0
  constraints (14):
    c: Coincident(g0,g-1)
    c: Distance(g0) = 6
    c: Vertical(g0)
    c: Coincident(g3,g0)
    c: Weight(g1) = 1
    c: Equal(g1,g2)
    c: InternalAlignment(g1,g3)
    c: InternalAlignment(g2,g3)
    c: InternalAlignment(g4,g3)
    c: InternalAlignment(g5,g3)
    c: Block(g3)
    c: Coincident(g6,g0)
    c: Coincident(g6,g3)
    c: Horizontal(g6)
FEATURE [Part::Extrusion] Extrude014  label="caseScrewPillarBracket002"
  Base = -> Sketch020
  Dir = (0,0,1)
  DirMode = 2
  FaceMakerClass = Part::FaceMakerBullseye
  LengthFwd = 2.4
  LengthRev = 0
  Placement = pos=(13.7,29,13.26) rot=(0,-1,0;1.5708rad)
  Solid = true
  Symmetric = false
FEATURE [Sketcher::SketchObject] Sketch021
  FullyConstrained = true
  sketch-geometry (7):
    g0: LineSegment StartX=0 StartY=0 StartZ=0 EndX=0 EndY=6 EndZ=0
    g1: Circle CenterX=0 CenterY=0 CenterZ=0 NormalX=0 NormalY=0 NormalZ=1 AngleXU=0 Radius=1
    g2: Circle CenterX=8 CenterY=6 CenterZ=0 NormalX=0 NormalY=0 NormalZ=1 AngleXU=0 Radius=1
    g3: BSplineCurve PolesCount=3 KnotsCount=2 Degree=2 IsPeriodic=0
    g4: GeomPoint X=0 Y=0 Z=0
    g5: GeomPoint X=8 Y=6 Z=0
    g6: LineSegment StartX=0 StartY=6 StartZ=0 EndX=8 EndY=6 EndZ=0
  constraints (14):
    c: Coincident(g0,g-1)
    c: Distance(g0) = 6
    c: Vertical(g0)
    c: Coincident(g3,g0)
    c: Weight(g1) = 1
    c: Equal(g1,g2)
    c: InternalAlignment(g1,g3)
    c: InternalAlignment(g2,g3)
    c: InternalAlignment(g4,g3)
    c: InternalAlignment(g5,g3)
    c: Block(g3)
    c: Coincident(g6,g0)
    c: Coincident(g6,g3)
    c: Horizontal(g6)
FEATURE [Part::Extrusion] Extrude015  label="caseScrewPillarBracket003"
  Base = -> Sketch021
  Dir = (0,0,1)
  DirMode = 2
  FaceMakerClass = Part::FaceMakerBullseye
  LengthFwd = 2.4
  LengthRev = 0
  Placement = pos=(11.3,29,58.74) rot=(0,1,0;1.5708rad)
  Solid = true
  Symmetric = false
FEATURE [Sketcher::SketchObject] Sketch022
  FullyConstrained = true
  sketch-geometry (7):
    g0: LineSegment StartX=0 StartY=0 StartZ=0 EndX=0 EndY=6 EndZ=0
    g1: Circle CenterX=0 CenterY=0 CenterZ=0 NormalX=0 NormalY=0 NormalZ=1 AngleXU=0 Radius=1
    g2: Circle CenterX=8 CenterY=6 CenterZ=0 NormalX=0 NormalY=0 NormalZ=1 AngleXU=0 Radius=1
    g3: BSplineCurve PolesCount=3 KnotsCount=2 Degree=2 IsPeriodic=0
    g4: GeomPoint X=0 Y=0 Z=0
    g5: GeomPoint X=8 Y=6 Z=0
    g6: LineSegment StartX=0 StartY=6 StartZ=0 EndX=8 EndY=6 EndZ=0
  constraints (14):
    c: Coincident(g0,g-1)
    c: Distance(g0) = 6
    c: Vertical(g0)
    c: Coincident(g3,g0)
    c: Weight(g1) = 1
    c: Equal(g1,g2)
    c: InternalAlignment(g1,g3)
    c: InternalAlignment(g2,g3)
    c: InternalAlignment(g4,g3)
    c: InternalAlignment(g5,g3)
    c: Block(g3)
    c: Coincident(g6,g0)
    c: Coincident(g6,g3)
    c: Horizontal(g6)
FEATURE [Part::Extrusion] Extrude016  label="caseScrewPillarBracket004"
  Base = -> Sketch022
  Dir = (0,0,1)
  DirMode = 2
  FaceMakerClass = Part::FaceMakerBullseye
  LengthFwd = 2.4
  LengthRev = 0
  Placement = pos=(88.3,29,65.23) rot=(0,1,0;1.5708rad)
  Solid = true
  Symmetric = false
FEATURE [Sketcher::SketchObject] Sketch023
  FullyConstrained = true
  sketch-geometry (7):
    g0: LineSegment StartX=0 StartY=0 StartZ=0 EndX=0 EndY=6 EndZ=0
    g1: Circle CenterX=0 CenterY=0 CenterZ=0 NormalX=0 NormalY=0 NormalZ=1 AngleXU=0 Radius=1
    g2: Circle CenterX=8 CenterY=6 CenterZ=0 NormalX=0 NormalY=0 NormalZ=1 AngleXU=0 Radius=1
    g3: BSplineCurve PolesCount=3 KnotsCount=2 Degree=2 IsPeriodic=0
    g4: GeomPoint X=0 Y=0 Z=0
    g5: GeomPoint X=8 Y=6 Z=0
    g6: LineSegment StartX=0 StartY=6 StartZ=0 EndX=8 EndY=6 EndZ=0
  constraints (14):
    c: Coincident(g0,g-1)
    c: Distance(g0) = 6
    c: Vertical(g0)
    c: Coincident(g3,g0)
    c: Weight(g1) = 1
    c: Equal(g1,g2)
    c: InternalAlignment(g1,g3)
    c: InternalAlignment(g2,g3)
    c: InternalAlignment(g4,g3)
    c: InternalAlignment(g5,g3)
    c: Block(g3)
    c: Coincident(g6,g0)
    c: Coincident(g6,g3)
    c: Horizontal(g6)
FEATURE [Part::Extrusion] Extrude017  label="caseScrewPillarBracket005"
  Base = -> Sketch023
  Dir = (0,0,1)
  DirMode = 2
  FaceMakerClass = Part::FaceMakerBullseye
  LengthFwd = 2.4
  LengthRev = 0
  Placement = pos=(90.7,29,6.77) rot=(0,-1,0;1.5708rad)
  Solid = true
  Symmetric = false
FEATURE [Sketcher::SketchObject] Sketch024
  FullyConstrained = true
  sketch-geometry (7):
    g0: LineSegment StartX=0 StartY=0 StartZ=0 EndX=0 EndY=6 EndZ=0
    g1: Circle CenterX=0 CenterY=0 CenterZ=0 NormalX=0 NormalY=0 NormalZ=1 AngleXU=0 Radius=1
    g2: Circle CenterX=8 CenterY=6 CenterZ=0 NormalX=0 NormalY=0 NormalZ=1 AngleXU=0 Radius=1
    g3: BSplineCurve PolesCount=3 KnotsCount=2 Degree=2 IsPeriodic=0
    g4: GeomPoint X=0 Y=0 Z=0
    g5: GeomPoint X=8 Y=6 Z=0
    g6: LineSegment StartX=0 StartY=6 StartZ=0 EndX=8 EndY=6 EndZ=0
  constraints (14):
    c: Coincident(g0,g-1)
    c: Distance(g0) = 6
    c: Vertical(g0)
    c: Coincident(g3,g0)
    c: Weight(g1) = 1
    c: Equal(g1,g2)
    c: InternalAlignment(g1,g3)
    c: InternalAlignment(g2,g3)
    c: InternalAlignment(g4,g3)
    c: InternalAlignment(g5,g3)
    c: Block(g3)
    c: Coincident(g6,g0)
    c: Coincident(g6,g3)
    c: Horizontal(g6)
FEATURE [Part::Extrusion] Extrude018  label="caseScrewPillarBracket006"
  Base = -> Sketch024
  Dir = (0,0,1)
  DirMode = 2
  FaceMakerClass = Part::FaceMakerBullseye
  LengthFwd = 2.4
  LengthRev = 0
  Placement = pos=(103.7,29,6.77) rot=(0,-1,0;1.5708rad)
  Solid = true
  Symmetric = false
FEATURE [Sketcher::SketchObject] Sketch025
  FullyConstrained = true
  sketch-geometry (7):
    g0: LineSegment StartX=0 StartY=0 StartZ=0 EndX=0 EndY=6 EndZ=0
    g1: Circle CenterX=0 CenterY=0 CenterZ=0 NormalX=0 NormalY=0 NormalZ=1 AngleXU=0 Radius=1
    g2: Circle CenterX=8 CenterY=6 CenterZ=0 NormalX=0 NormalY=0 NormalZ=1 AngleXU=0 Radius=1
    g3: BSplineCurve PolesCount=3 KnotsCount=2 Degree=2 IsPeriodic=0
    g4: GeomPoint X=0 Y=0 Z=0
    g5: GeomPoint X=8 Y=6 Z=0
    g6: LineSegment StartX=0 StartY=6 StartZ=0 EndX=8 EndY=6 EndZ=0
  constraints (14):
    c: Coincident(g0,g-1)
    c: Distance(g0) = 6
    c: Vertical(g0)
    c: Coincident(g3,g0)
    c: Weight(g1) = 1
    c: Equal(g1,g2)
    c: InternalAlignment(g1,g3)
    c: InternalAlignment(g2,g3)
    c: InternalAlignment(g4,g3)
    c: InternalAlignment(g5,g3)
    c: Block(g3)
    c: Coincident(g6,g0)
    c: Coincident(g6,g3)
    c: Horizontal(g6)
FEATURE [Part::Extrusion] Extrude019  label="caseScrewPillarBracket007"
  Base = -> Sketch025
  Dir = (0,0,1)
  DirMode = 2
  FaceMakerClass = Part::FaceMakerBullseye
  LengthFwd = 2.4
  LengthRev = 0
  Placement = pos=(101.3,29,65.23) rot=(0,1,0;1.5708rad)
  Solid = true
  Symmetric = false
FEATURE [Part::Box] Box011  label="frontCaseScrewPillarBracket"
  AttacherType = Attacher::AttachEngine3D
  Height = 2.4
  Length = 16
  Placement = pos=(87,28,2.3) rot=(0,0,1;0rad)
  Width = 7
FEATURE [Part::Box] Box012  label="frontCaseScrewPillarBracket001"
  AttacherType = Attacher::AttachEngine3D
  Height = 2.4
  Length = 16
  Placement = pos=(87,28,67.3) rot=(0,0,1;0rad)
  Width = 7
FEATURE [Sketcher::SketchObject] Sketch026
  FullyConstrained = true
  sketch-geometry (17):
    g0: Circle CenterX=-3.5 CenterY=23.5 CenterZ=0 NormalX=0 NormalY=0 NormalZ=1 AngleXU=0 Radius=1
    g1: Circle CenterX=-1 CenterY=15.25 CenterZ=0 NormalX=0 NormalY=0 NormalZ=1 AngleXU=0 Radius=1
    g2: Circle CenterX=-3.5 CenterY=7 CenterZ=0 NormalX=0 NormalY=0 NormalZ=1 AngleXU=0 Radius=1
    g3: BSplineCurve PolesCount=3 KnotsCount=2 Degree=2 IsPeriodic=0
    g4: GeomPoint X=-3.5 Y=23.5 Z=0
    g5: GeomPoint X=-3.5 Y=7 Z=0
    g6: Circle CenterX=-4.8 CenterY=30.5 CenterZ=0 NormalX=0 NormalY=0 NormalZ=1 AngleXU=0 Radius=1
    g7: Circle CenterX=-3.5 CenterY=30.5 CenterZ=0 NormalX=0 NormalY=0 NormalZ=1 AngleXU=0 Radius=1
    g8: Circle CenterX=-3.5 CenterY=29.2 CenterZ=0 NormalX=0 NormalY=0 NormalZ=1 AngleXU=0 Radius=1
    g9: BSplineCurve PolesCount=3 KnotsCount=2 Degree=2 IsPeriodic=0
    g10: GeomPoint X=-4.8 Y=30.5 Z=0
    g11: GeomPoint X=-3.5 Y=29.2 Z=0
    g12: LineSegment StartX=-3.5 StartY=29.2 StartZ=0 EndX=-3.5 EndY=23.5 EndZ=0
    g13: LineSegment StartX=-4.8 StartY=30.5 StartZ=0 EndX=0 EndY=30.5 EndZ=0
    g14: LineSegment StartX=-3.5 StartY=5 StartZ=0 EndX=-3.5 EndY=7 EndZ=0
    g15: LineSegment StartX=0 StartY=5 StartZ=0 EndX=0 EndY=30.5 EndZ=0
    g16: LineSegment StartX=-3.5 StartY=5 StartZ=0 EndX=0 EndY=5 EndZ=0
  constraints (33):
    c: Weight(g0) = 1
    c: Equal(g0,g1)
    c: Equal(g0,g2)
    c: InternalAlignment(g0,g3)
    c: InternalAlignment(g1,g3)
    c: InternalAlignment(g2,g3)
    c: InternalAlignment(g4,g3)
    c: InternalAlignment(g5,g3)
    c: Block(g3)
    c: Weight(g6) = 1
    c: Equal(g6,g7)
    c: Equal(g6,g8)
    c: InternalAlignment(g6,g9)
    c: InternalAlignment(g7,g9)
    c: InternalAlignment(g8,g9)
    c: InternalAlignment(g10,g9)
    c: InternalAlignment(g11,g9)
    c: Block(g9)
    c: Coincident(g12,g9)
    c: Coincident(g12,g3)
    c: Vertical(g12)
    c: Coincident(g13,g9)
    c: Horizontal(g13)
    c: Distance(g13) = 4.8
    c: Coincident(g14,g3)
    c: Vertical(g14)
    c: Coincident(g15,g13)
    c: Vertical(g15)
    c: Tangent(g15,g1)
    c: Distance(g14) = 2
    c: Coincident(g16,g14)
    c: Horizontal(g16)
    c: Coincident(g15,g16)
FEATURE [Part::Feature] Face050
  shape: bbox 4.8 x 25.5 x 2e-07 mm, 1 faces, 0 solids (baked)
FEATURE [Part::Revolution] Revolve054  label="moreFrontCaseScrewPost001"
  Angle = 360
  Axis = (0,1,0)
  Base = (0,0,0)
  FaceMakerClass = Part::FaceMakerBullseye
  Placement = pos=(102.5,4.5,3.5) rot=(0,0,1;0rad)
  Solid = false
  Source = -> Face050
  Symmetric = false
FEATURE [Part::Feature] Face051
  shape: bbox 4.8 x 25.5 x 2e-07 mm, 1 faces, 0 solids (baked)
FEATURE [Part::Revolution] Revolve055  label="moreFrontCaseScrewPost002"
  Angle = 360
  Axis = (0,1,0)
  Base = (0,0,0)
  FaceMakerClass = Part::FaceMakerBullseye
  Placement = pos=(102.5,4.5,68.5) rot=(0,0,1;0rad)
  Solid = false
  Source = -> Face051
  Symmetric = false
FEATURE [Sketcher::SketchObject] Sketch027
  FullyConstrained = true
  sketch-geometry (10):
    g0: LineSegment StartX=-1.6 StartY=4.7 StartZ=0 EndX=-1.6 EndY=1.7 EndZ=0
    g1: LineSegment StartX=-3.5 StartY=4.7 StartZ=0 EndX=-1.6 EndY=4.7 EndZ=0
    g2: LineSegment StartX=-1.6 StartY=1.7 StartZ=0 EndX=-1.6 EndY=1.5 EndZ=0
    g3: LineSegment StartX=-1.6 StartY=1.5 StartZ=0 EndX=-5.2 EndY=1.5 EndZ=0
    g4: Circle CenterX=-3.5 CenterY=4.7 CenterZ=0 NormalX=0 NormalY=0 NormalZ=1 AngleXU=0 Radius=1
    g5: Circle CenterX=-3.59627 CenterY=2.99743 CenterZ=0 NormalX=0 NormalY=0 NormalZ=1 AngleXU=0 Radius=1
    g6: Circle CenterX=-5.2 CenterY=1.5 CenterZ=0 NormalX=0 NormalY=0 NormalZ=1 AngleXU=0 Radius=1
    g7: BSplineCurve PolesCount=3 KnotsCount=2 Degree=2 IsPeriodic=0
    g8: GeomPoint X=-3.5 Y=4.7 Z=0
    g9: GeomPoint X=-5.2 Y=1.5 Z=0
  constraints (23):
    c: Vertical(g0)
    c: Distance(g0) = 3
    c: Coincident(g1,g0)
    c: Horizontal(g1)
    c: Block(g0)
    c: Block(g1)
    c: Coincident(g2,g0)
    c: Vertical(g2)
    c: Distance(g2) = 0.2
    c: Coincident(g3,g2)
    c: Horizontal(g3)
    c: Block(g3)
    c: Coincident(g7,g1)
    c: Weight(g4) = 1
    c: Equal(g4,g5)
    c: Equal(g4,g6)
    c: Coincident(g7,g3)
    c: InternalAlignment(g4,g7)
    c: InternalAlignment(g5,g7)
    c: InternalAlignment(g6,g7)
    c: InternalAlignment(g8,g7)
    c: InternalAlignment(g9,g7)
    c: Block(g7)
FEATURE [Sketcher::SketchObject] Sketch028
  FullyConstrained = true
  sketch-geometry (18):
    g0: LineSegment StartX=0 StartY=3e-16 StartZ=0 EndX=0 EndY=1.7 EndZ=0
    g1: LineSegment StartX=-3.5 StartY=0 StartZ=0 EndX=-3.5 EndY=0.9 EndZ=0
    g2: Circle CenterX=-2.7 CenterY=1.7 CenterZ=0 NormalX=0 NormalY=0 NormalZ=1 AngleXU=0 Radius=1
    g3: Circle CenterX=-3.5 CenterY=1.7 CenterZ=0 NormalX=0 NormalY=0 NormalZ=1 AngleXU=0 Radius=1
    g4: Circle CenterX=-3.5 CenterY=0.9 CenterZ=0 NormalX=0 NormalY=0 NormalZ=1 AngleXU=0 Radius=1
    g5: BSplineCurve PolesCount=3 KnotsCount=2 Degree=2 IsPeriodic=0
    g6: GeomPoint X=-2.7 Y=1.7 Z=0
    g7: GeomPoint X=-3.5 Y=0.9 Z=0
    g8: LineSegment StartX=-3.5 StartY=0 StartZ=0 EndX=-3.5 EndY=-7 EndZ=0
    g9: LineSegment StartX=0 StartY=3e-16 StartZ=0 EndX=0 EndY=-7 EndZ=0
    g10: LineSegment StartX=-3.5 StartY=-7 StartZ=0 EndX=0 EndY=-7 EndZ=0
    g11: LineSegment StartX=-2.7 StartY=1.7 StartZ=0 EndX=-1.6 EndY=1.7 EndZ=0
    g12: LineSegment StartX=0 StartY=1.7 StartZ=0 EndX=0 EndY=4.5 EndZ=0
    g13: LineSegment StartX=0 StartY=4.5 StartZ=0 EndX=0 EndY=10.8 EndZ=0
    g14: LineSegment StartX=0 StartY=10.8 StartZ=0 EndX=-2 EndY=10.8 EndZ=0
    g15: LineSegment StartX=-1.6 StartY=4.7 StartZ=0 EndX=-1.6 EndY=1.7 EndZ=0
    g16: LineSegment StartX=-1.6 StartY=4.7 StartZ=0 EndX=-2 EndY=4.7 EndZ=0
    g17: LineSegment StartX=-2 StartY=4.7 StartZ=0 EndX=-2 EndY=10.8 EndZ=0
  constraints (44):
    c: Vertical(g0)
    c: Vertical(g1)
    c: Distance(g1) = 0.9
    c: Block(g0)
    c: Distance(g0) = 1.7
    c: Weight(g2) = 1
    c: Equal(g2,g3)
    c: Equal(g2,g4)
    c: Coincident(g5,g1)
    c: InternalAlignment(g2,g5)
    c: InternalAlignment(g3,g5)
    c: InternalAlignment(g4,g5)
    c: InternalAlignment(g6,g5)
    c: InternalAlignment(g7,g5)
    c: Block(g5)
    c: Coincident(g8,g1)
    c: Vertical(g8)
    c: Distance(g8) = 7
    c: Vertical(g9)
    c: Equal(g8,g9) = 7
    c: Coincident(g9,g0)
    c: Coincident(g10,g8)
    c: Coincident(g10,g9)
    c: Horizontal(g10)
    c: Coincident(g11,g5)
    c: Horizontal(g11)
    c: Coincident(g12,g0)
    c: Vertical(g12)
    c: Distance(g12) = 2.8
    c: Coincident(g13,g12)
    c: Vertical(g13)
    c: Distance(g13) = 6.3
    c: Coincident(g14,g13)
    c: Horizontal(g14)
    c: Distance(g14) = 2
    c: Vertical(g15)
    c: Distance(g15) = 3
    c: Block(g11)
    c: Coincident(g15,g11)
    c: Coincident(g16,g15)
    c: Horizontal(g16)
    c: Coincident(g17,g16)
    c: Coincident(g17,g14)
    c: Vertical(g17)
FEATURE [Part::Revolution] Revolve040  label="backCaseScrewRetainer001"
  Angle = 360
  Axis = (0,1,0)
  Base = (0,0,0)
  FaceMakerClass = Part::FaceMakerBullseye
  Placement = pos=(12.5,3,10) rot=(0,0,1;0rad)
  Solid = false
  Source = -> Face036
  Symmetric = false
FEATURE [Part::Feature] Face055
  shape: bbox 3.5 x 30.2 x 2e-07 mm, 1 faces, 0 solids (baked)
FEATURE [Part::Revolution] Revolve059  label="backCaseScrewPost"
  Angle = 360
  Axis = (0,1,0)
  Base = (0,0,0)
  FaceMakerClass = Part::FaceMakerBullseye
  Placement = pos=(12.5,4.5,10) rot=(0,0,1;0rad)
  Solid = false
  Source = -> Face055
  Symmetric = false
FEATURE [Part::Feature] Face056
  shape: bbox 3.5 x 30.2 x 2e-07 mm, 1 faces, 0 solids (baked)
FEATURE [Part::Revolution] Revolve060  label="backCaseScrewPost001"
  Angle = 360
  Axis = (0,1,0)
  Base = (0,0,0)
  FaceMakerClass = Part::FaceMakerBullseye
  Placement = pos=(12.5,4.5,62) rot=(0,0,1;0rad)
  Solid = false
  Source = -> Face056
  Symmetric = false
FEATURE [Part::Feature] Face057
  shape: bbox 3.5 x 17.8 x 2e-07 mm, 1 faces, 0 solids (baked)
FEATURE [Part::Revolution] Revolve061  label="removeToCreateScrewAndThreadedInsertHole"
  Angle = 360
  Axis = (0,1,0)
  Base = (0,0,0)
  FaceMakerClass = Part::FaceMakerBullseye
  Placement = pos=(12.5,0,10) rot=(0,0,1;0rad)
  Solid = false
  Source = -> Face057
  Symmetric = false
FEATURE [Part::Feature] Face058
  shape: bbox 3.5 x 17.8 x 2e-07 mm, 1 faces, 0 solids (baked)
FEATURE [Part::Revolution] Revolve062  label="removeToCreateScrewAndThreadedInsertHole001"
  Angle = 360
  Axis = (0,1,0)
  Base = (0,0,0)
  FaceMakerClass = Part::FaceMakerBullseye
  Placement = pos=(12.5,0,62) rot=(0,0,1;0rad)
  Solid = false
  Source = -> Face058
  Symmetric = false
FEATURE [Part::Feature] Face059
  shape: bbox 3.5 x 17.8 x 2e-07 mm, 1 faces, 0 solids (baked)
FEATURE [Part::Revolution] Revolve063  label="removeToCreateScrewAndThreadedInsertHole002"
  Angle = 360
  Axis = (0,1,0)
  Base = (0,0,0)
  FaceMakerClass = Part::FaceMakerBullseye
  Placement = pos=(89.5,0,68.5) rot=(0,0,1;0rad)
  Solid = false
  Source = -> Face059
  Symmetric = false
FEATURE [Part::Feature] Face060
  shape: bbox 3.5 x 17.8 x 2e-07 mm, 1 faces, 0 solids (baked)
FEATURE [Part::Revolution] Revolve064  label="removeToCreateScrewAndThreadedInsertHole003"
  Angle = 360
  Axis = (0,1,0)
  Base = (0,0,0)
  FaceMakerClass = Part::FaceMakerBullseye
  Placement = pos=(89.5,0,3.5) rot=(0,0,1;0rad)
  Solid = false
  Source = -> Face060
  Symmetric = false
FEATURE [Part::Feature] Face061
  shape: bbox 3.5 x 17.8 x 2e-07 mm, 1 faces, 0 solids (baked)
FEATURE [Part::Revolution] Revolve065  label="removeToCreateScrewAndThreadedInsertHole004"
  Angle = 360
  Axis = (0,1,0)
  Base = (0,0,0)
  FaceMakerClass = Part::FaceMakerBullseye
  Placement = pos=(102.5,4.7,3.5) rot=(0,0,1;0rad)
  Solid = false
  Source = -> Face061
  Symmetric = false
FEATURE [Part::Feature] Face062
  shape: bbox 3.5 x 17.8 x 2e-07 mm, 1 faces, 0 solids (baked)
FEATURE [Part::Revolution] Revolve066  label="removeToCreateScrewAndThreadedInsertHole005"
  Angle = 360
  Axis = (0,1,0)
  Base = (0,0,0)
  FaceMakerClass = Part::FaceMakerBullseye
  Placement = pos=(102.5,4.7,68.5) rot=(0,0,1;0rad)
  Solid = false
  Source = -> Face062
  Symmetric = false
FEATURE [Part::MultiFuse] Fusion047  label="makeHoles"
  Shapes = -> [Revolve066,Revolve065,Revolve064,Revolve063,Revolve062,Revolve061]
FEATURE [Part::Feature] Face063
  shape: bbox 3.6 x 3.2 x 2e-07 mm, 1 faces, 0 solids (baked)
FEATURE [Part::Revolution] Revolve067  label="moreFrontCaseScrewRetainer002"
  Angle = 360
  Axis = (0,1,0)
  Base = (0,0,0)
  FaceMakerClass = Part::FaceMakerBullseye
  Placement = pos=(102.5,4.5,68.5) rot=(0,0,1;0rad)
  Solid = false
  Source = -> Face063
  Symmetric = false
FEATURE [Part::Feature] Face064
  shape: bbox 3.6 x 3.2 x 2e-07 mm, 1 faces, 0 solids (baked)
FEATURE [Part::Revolution] Revolve068  label="moreFrontCaseScrewRetainer003"
  Angle = 360
  Axis = (0,1,0)
  Base = (0,0,0)
  FaceMakerClass = Part::FaceMakerBullseye
  Placement = pos=(102.5,4.5,3.5) rot=(0,0,1;0rad)
  Solid = false
  Source = -> Face064
  Symmetric = false
FEATURE [Part::Feature] Face065
  shape: bbox 3.5 x 17.8 x 2e-07 mm, 1 faces, 0 solids (baked)
FEATURE [Part::Revolution] Revolve069  label="removeToCreateScrewAndThreadedInsertHole006"
  Angle = 360
  Axis = (0,1,0)
  Base = (0,0,0)
  FaceMakerClass = Part::FaceMakerBullseye
  Placement = pos=(12.5,0,10) rot=(0,0,1;0rad)
  Solid = false
  Source = -> Face065
  Symmetric = false
FEATURE [Part::Feature] Face066
  shape: bbox 3.5 x 17.8 x 2e-07 mm, 1 faces, 0 solids (baked)
FEATURE [Part::Revolution] Revolve070  label="removeToCreateScrewAndThreadedInsertHole007"
  Angle = 360
  Axis = (0,1,0)
  Base = (0,0,0)
  FaceMakerClass = Part::FaceMakerBullseye
  Placement = pos=(12.5,0,62) rot=(0,0,1;0rad)
  Solid = false
  Source = -> Face066
  Symmetric = false
FEATURE [Part::Feature] Face067
  shape: bbox 3.5 x 17.8 x 2e-07 mm, 1 faces, 0 solids (baked)
FEATURE [Part::Revolution] Revolve071  label="removeToCreateScrewAndThreadedInsertHole008"
  Angle = 360
  Axis = (0,1,0)
  Base = (0,0,0)
  FaceMakerClass = Part::FaceMakerBullseye
  Placement = pos=(89.5,0,68.5) rot=(0,0,1;0rad)
  Solid = false
  Source = -> Face067
  Symmetric = false
FEATURE [Part::Feature] Face068
  shape: bbox 3.5 x 17.8 x 2e-07 mm, 1 faces, 0 solids (baked)
FEATURE [Part::Revolution] Revolve072  label="removeToCreateScrewAndThreadedInsertHole009"
  Angle = 360
  Axis = (0,1,0)
  Base = (0,0,0)
  FaceMakerClass = Part::FaceMakerBullseye
  Placement = pos=(89.5,0,3.5) rot=(0,0,1;0rad)
  Solid = false
  Source = -> Face068
  Symmetric = false
FEATURE [Part::Feature] Face069
  shape: bbox 3.5 x 17.8 x 2e-07 mm, 1 faces, 0 solids (baked)
FEATURE [Part::Feature] Face070
  shape: bbox 3.5 x 17.8 x 2e-07 mm, 1 faces, 0 solids (baked)
FEATURE [Part::Revolution] Revolve073  label="removeToCreateScrewAndThreadedInsertHole010"
  Angle = 360
  Axis = (0,1,0)
  Base = (0,0,0)
  FaceMakerClass = Part::FaceMakerBullseye
  Placement = pos=(102.5,4.7,3.5) rot=(0,0,1;0rad)
  Solid = false
  Source = -> Face069
  Symmetric = false
FEATURE [Part::Revolution] Revolve074  label="removeToCreateScrewAndThreadedInsertHole011"
  Angle = 360
  Axis = (0,1,0)
  Base = (0,0,0)
  FaceMakerClass = Part::FaceMakerBullseye
  Placement = pos=(102.5,4.7,68.5) rot=(0,0,1;0rad)
  Solid = false
  Source = -> Face070
  Symmetric = false
FEATURE [Part::MultiFuse] Fusion048  label="makeHoles001"
  Shapes = -> [Revolve074,Revolve073,Revolve072,Revolve071,Revolve070,Revolve069]
FEATURE [Part::MultiFuse] Fusion049  label="caseScrewRetainers"
  Shapes = -> [Revolve067,Revolve068,Revolve048,Revolve047,Revolve039,Revolve040]
FEATURE [Part::Cut] Cut015  label="caseScrewRetainers001"
  Base = -> Fusion049
  Tool = -> Fusion048
FEATURE [Part::MultiFuse] Fusion050  label="casePillars"
  Shapes = -> [Revolve055,Revolve054,Revolve043,Revolve046,Revolve059,Revolve060]
FEATURE [Part::Feature] Face071 .. Face076  x6 (patterned run collapsed; names and placements below)
  shape: bbox 3.5 x 17.8 x 2e-07 mm, 1 faces, 0 solids (baked)
FEATURE [Part::Revolution] Revolve075  label="removeToCreateScrewAndThreadedInsertHole012"
  Angle = 360
  Axis = (0,1,0)
  Base = (0,0,0)
  FaceMakerClass = Part::FaceMakerBullseye
  Placement = pos=(12.5,0,10) rot=(0,0,1;0rad)
  Solid = false
  Source = -> Face071
  Symmetric = false
FEATURE [Part::Revolution] Revolve076  label="removeToCreateScrewAndThreadedInsertHole013"
  Angle = 360
  Axis = (0,1,0)
  Base = (0,0,0)
  FaceMakerClass = Part::FaceMakerBullseye
  Placement = pos=(12.5,0,62) rot=(0,0,1;0rad)
  Solid = false
  Source = -> Face072
  Symmetric = false
FEATURE [Part::Revolution] Revolve077  label="removeToCreateScrewAndThreadedInsertHole014"
  Angle = 360
  Axis = (0,1,0)
  Base = (0,0,0)
  FaceMakerClass = Part::FaceMakerBullseye
  Placement = pos=(89.5,0,68.5) rot=(0,0,1;0rad)
  Solid = false
  Source = -> Face073
  Symmetric = false
FEATURE [Part::Revolution] Revolve078  label="removeToCreateScrewAndThreadedInsertHole015"
  Angle = 360
  Axis = (0,1,0)
  Base = (0,0,0)
  FaceMakerClass = Part::FaceMakerBullseye
  Placement = pos=(89.5,0,3.5) rot=(0,0,1;0rad)
  Solid = false
  Source = -> Face074
  Symmetric = false
FEATURE [Part::Revolution] Revolve079  label="removeToCreateScrewAndThreadedInsertHole016"
  Angle = 360
  Axis = (0,1,0)
  Base = (0,0,0)
  FaceMakerClass = Part::FaceMakerBullseye
  Placement = pos=(102.5,4.7,3.5) rot=(0,0,1;0rad)
  Solid = false
  Source = -> Face075
  Symmetric = false
FEATURE [Part::Revolution] Revolve080  label="removeToCreateScrewAndThreadedInsertHole017"
  Angle = 360
  Axis = (0,1,0)
  Base = (0,0,0)
  FaceMakerClass = Part::FaceMakerBullseye
  Placement = pos=(102.5,4.7,68.5) rot=(0,0,1;0rad)
  Solid = false
  Source = -> Face076
  Symmetric = false
FEATURE [Part::MultiFuse] Fusion051  label="makeHoles002"
  Shapes = -> [Revolve080,Revolve079,Revolve078,Revolve077,Revolve076,Revolve075]
FEATURE [Part::Cut] Cut016  label="caesPillars"
  Base = -> Fusion050
  Tool = -> Fusion051
FEATURE [Part::Revolution] Revolve009  label="plugHousing016"
  Angle = 360
  Axis = (0,1,0)
  Base = (0,0,0)
  FaceMakerClass = Part::FaceMakerBullseye
  Placement = pos=(0,0,36.15) rot=(0,0,1;0rad)
  Solid = false
  Source = -> Face012
  Symmetric = false
FEATURE [Part::MultiFuse] Fusion014  label="plugHousing023"
  Placement = pos=(0,0,0) rot=(0,0,1;1.5708rad)
  Shapes = -> [Revolve011,Revolve009]
FEATURE [Part::Revolution] Revolve010  label="plugHousing017"
  Angle = 360
  Axis = (0,1,0)
  Base = (0,0,0)
  FaceMakerClass = Part::FaceMakerBullseye
  Placement = pos=(0,0,36.15) rot=(0,0,1;0rad)
  Solid = false
  Source = -> Face014
  Symmetric = false
FEATURE [Part::MultiFuse] Fusion015  label="plugHousing024"
  Placement = pos=(0,0,0) rot=(0,0,1;1.5708rad)
  Shapes = -> [Revolve010,Revolve015]
FEATURE [Part::Revolution] Revolve014  label="plugHousing026"
  Angle = 360
  Axis = (0,1,0)
  Base = (0,0,0)
  FaceMakerClass = Part::FaceMakerBullseye
  Placement = pos=(0,0,36.15) rot=(0,0,1;0rad)
  Solid = false
  Source = -> Face011
  Symmetric = false
FEATURE [Part::Revolution] Revolve013  label="plugHousing025"
  Angle = 360
  Axis = (0,1,0)
  Base = (0,0,0)
  FaceMakerClass = Part::FaceMakerBullseye
  Placement = pos=(0,0,36.15) rot=(0,0,1;0rad)
  Solid = false
  Source = -> Face015
  Symmetric = false
FEATURE [Part::MultiFuse] Fusion016  label="plugHousing028"
  Placement = pos=(0,19,0) rot=(0,0,1;3.14159rad)
  Shapes = -> [Fusion014,Fusion013]
FEATURE [Part::MultiFuse] Fusion011  label="plugHousing018"
  Placement = pos=(0,0,0) rot=(0,0,1;1.5708rad)
  Shapes = -> [Revolve014,Revolve013]
FEATURE [Part::MultiFuse] Fusion012  label="plugHousing019"
  Placement = pos=(0,19,0) rot=(0,0,1;3.14159rad)
  Shapes = -> [Fusion011,Fusion015]
FEATURE [Part::MultiFuse] Fusion017  label="plugHousing029"
  Placement = pos=(122.621,0,-0.15) rot=(0,0,1;0rad)
  Shapes = -> [Fusion016,Fusion012]
FEATURE [Part::MultiFuse] Fusion052  label="casePillarRetainers"
  Shapes = -> [Extrude012,Extrude013,Extrude014,Extrude015,Extrude016,Extrude017,Extrude018,Extrude019,Box011,Box012]
FEATURE [Part::Feature] Face077
  shape: bbox 3.5 x 17.8 x 2e-07 mm, 1 faces, 0 solids (baked)
FEATURE [Part::Revolution] Revolve081  label="removeToCreateScrewAndThreadedInsertHole018"
  Angle = 360
  Axis = (0,1,0)
  Base = (0,0,0)
  FaceMakerClass = Part::FaceMakerBullseye
  Placement = pos=(62.3,30.3,19.7) rot=(0,0,1;0rad)
  Solid = false
  Source = -> Face077
  Symmetric = false
FEATURE [Part::Feature] Face078
  shape: bbox 3.5 x 17.8 x 2e-07 mm, 1 faces, 0 solids (baked)
FEATURE [Part::Revolution] Revolve082  label="removeToCreateScrewAndThreadedInsertHole019"
  Angle = 360
  Axis = (0,1,0)
  Base = (0,0,0)
  FaceMakerClass = Part::FaceMakerBullseye
  Placement = pos=(62.3,30.3,51.7) rot=(0,0,1;0rad)
  Solid = false
  Source = -> Face078
  Symmetric = false
FEATURE [Part::Feature] Face079
  shape: bbox 3.5 x 17.8 x 2e-07 mm, 1 faces, 0 solids (baked)
FEATURE [Part::Revolution] Revolve083  label="removeToCreateScrewAndThreadedInsertHole020"
  Angle = 360
  Axis = (0,1,0)
  Base = (0,0,0)
  FaceMakerClass = Part::FaceMakerBullseye
  Placement = pos=(30.3,30.3,19.7) rot=(0,0,1;0rad)
  Solid = false
  Source = -> Face079
  Symmetric = false
FEATURE [Part::Feature] Face080
  shape: bbox 3.5 x 17.8 x 2e-07 mm, 1 faces, 0 solids (baked)
FEATURE [Part::Revolution] Revolve084  label="removeToCreateScrewAndThreadedInsertHole021"
  Angle = 360
  Axis = (0,1,0)
  Base = (0,0,0)
  FaceMakerClass = Part::FaceMakerBullseye
  Placement = pos=(30.3,30.3,51.7) rot=(0,0,1;0rad)
  Solid = false
  Source = -> Face080
  Symmetric = false
FEATURE [Part::MultiFuse] Fusion053  label="createThreadedInsertHolesForFan"
  Shapes = -> [Revolve081,Revolve082,Revolve083,Revolve084]
FEATURE [Part::Cut] Cut017  label="fanScrewHousing001"
  Base = -> Fusion046
  Tool = -> Fusion053
FEATURE [Part::Feature] Face081
  shape: bbox 3.5 x 17.8 x 2e-07 mm, 1 faces, 0 solids (baked)
FEATURE [Part::Revolution] Revolve085  label="removeToCreateScrewAndThreadedInsertHole022"
  Angle = 360
  Axis = (0,1,0)
  Base = (0,0,0)
  FaceMakerClass = Part::FaceMakerBullseye
  Placement = pos=(62.3,30.3,19.7) rot=(0,0,1;0rad)
  Solid = false
  Source = -> Face081
  Symmetric = false
FEATURE [Part::Feature] Face082
  shape: bbox 3.5 x 17.8 x 2e-07 mm, 1 faces, 0 solids (baked)
FEATURE [Part::Revolution] Revolve086  label="removeToCreateScrewAndThreadedInsertHole023"
  Angle = 360
  Axis = (0,1,0)
  Base = (0,0,0)
  FaceMakerClass = Part::FaceMakerBullseye
  Placement = pos=(62.3,30.3,51.7) rot=(0,0,1;0rad)
  Solid = false
  Source = -> Face082
  Symmetric = false
FEATURE [Part::Feature] Face083
  shape: bbox 3.5 x 17.8 x 2e-07 mm, 1 faces, 0 solids (baked)
FEATURE [Part::Revolution] Revolve087  label="removeToCreateScrewAndThreadedInsertHole024"
  Angle = 360
  Axis = (0,1,0)
  Base = (0,0,0)
  FaceMakerClass = Part::FaceMakerBullseye
  Placement = pos=(30.3,30.3,19.7) rot=(0,0,1;0rad)
  Solid = false
  Source = -> Face083
  Symmetric = false
FEATURE [Part::Feature] Face084
  shape: bbox 3.5 x 17.8 x 2e-07 mm, 1 faces, 0 solids (baked)
FEATURE [Part::Revolution] Revolve088  label="removeToCreateScrewAndThreadedInsertHole025"
  Angle = 360
  Axis = (0,1,0)
  Base = (0,0,0)
  FaceMakerClass = Part::FaceMakerBullseye
  Placement = pos=(30.3,30.3,51.7) rot=(0,0,1;0rad)
  Solid = false
  Source = -> Face084
  Symmetric = false
FEATURE [Part::MultiFuse] Fusion054  label="createThreadedInsertHolesForFan001"
  Shapes = -> [Revolve085,Revolve086,Revolve087,Revolve088]
FEATURE [Part::Cut] Cut018  label="top007"
  Base = -> Fusion040
  Tool = -> Fusion054
FEATURE [Sketcher::SketchObject] Sketch029
  FullyConstrained = false
  Placement = pos=(0,0,0) rot=(1,0,0;1.5708rad)
  sketch-geometry (24):
    g0: ArcOfCircle CenterX=-4 CenterY=-10.5 CenterZ=0 NormalX=0 NormalY=0 NormalZ=1 AngleXU=0 Radius=1.5 StartAngle=6e-16 EndAngle=3.14159
    g1: ArcOfCircle CenterX=-34.2 CenterY=-10.5 CenterZ=0 NormalX=0 NormalY=0 NormalZ=1 AngleXU=0 Radius=1.5 StartAngle=0 EndAngle=3.14159
    g2: ArcOfCircle CenterX=-34.2 CenterY=-27.7 CenterZ=0 NormalX=0 NormalY=0 NormalZ=1 AngleXU=0 Radius=1.5 StartAngle=3.14159 EndAngle=6.28319
    g3: ArcOfCircle CenterX=-4 CenterY=-27.7 CenterZ=0 NormalX=0 NormalY=0 NormalZ=1 AngleXU=0 Radius=1.5 StartAngle=3.1416 EndAngle=6.28319
    g4: ArcOfCircle CenterX=-10 CenterY=-4.3 CenterZ=0 NormalX=0 NormalY=0 NormalZ=1 AngleXU=0 Radius=1.5 StartAngle=2e-16 EndAngle=3.14159
    g5: ArcOfCircle CenterX=-16.1 CenterY=-1.8 CenterZ=0 NormalX=0 NormalY=0 NormalZ=1 AngleXU=0 Radius=1.5 StartAngle=5e-16 EndAngle=3.14159
    g6: ArcOfCircle CenterX=-22.1 CenterY=-1.8 CenterZ=0 NormalX=0 NormalY=0 NormalZ=1 AngleXU=0 Radius=1.5 StartAngle=5e-16 EndAngle=3.14159
    g7: ArcOfCircle CenterX=-28.2 CenterY=-4.3 CenterZ=0 NormalX=0 NormalY=0 NormalZ=1 AngleXU=0 Radius=1.5 StartAngle=2e-16 EndAngle=3.14159
    g8: ArcOfCircle CenterX=-10 CenterY=-33.9 CenterZ=0 NormalX=0 NormalY=0 NormalZ=1 AngleXU=0 Radius=1.5 StartAngle=3.14159 EndAngle=6.28319
    g9: ArcOfCircle CenterX=-16.1 CenterY=-36.4 CenterZ=0 NormalX=0 NormalY=0 NormalZ=1 AngleXU=0 Radius=1.5 StartAngle=3.14159 EndAngle=6.28319
    g10: ArcOfCircle CenterX=-22.1 CenterY=-36.4 CenterZ=0 NormalX=0 NormalY=0 NormalZ=1 AngleXU=0 Radius=1.5 StartAngle=3.14159 EndAngle=6.28319
    g11: ArcOfCircle CenterX=-28.2 CenterY=-33.9 CenterZ=0 NormalX=0 NormalY=0 NormalZ=1 AngleXU=0 Radius=1.5 StartAngle=3.14159 EndAngle=6.28319
    g12: LineSegment StartX=-35.7 StartY=-10.5 StartZ=0 EndX=-35.7 EndY=-27.7 EndZ=0
    g13: LineSegment StartX=-32.7 StartY=-10.5 StartZ=0 EndX=-32.7 EndY=-27.7 EndZ=0
    g14: LineSegment StartX=-29.7 StartY=-33.9 StartZ=0 EndX=-29.7 EndY=-4.3 EndZ=0
    g15: LineSegment StartX=-26.7 StartY=-33.9 StartZ=0 EndX=-26.7 EndY=-4.3 EndZ=0
    g16: LineSegment StartX=-2.5 StartY=-10.5 StartZ=0 EndX=-2.5 EndY=-27.7 EndZ=0
    g17: LineSegment StartX=-8.5 StartY=-4.3 StartZ=0 EndX=-8.5 EndY=-33.9 EndZ=0
    g18: LineSegment StartX=-5.5 StartY=-10.5 StartZ=0 EndX=-5.5 EndY=-27.7 EndZ=0
    g19: LineSegment StartX=-11.5 StartY=-4.3 StartZ=0 EndX=-11.5 EndY=-33.9 EndZ=0
    g20: LineSegment StartX=-14.6 StartY=-1.8 StartZ=0 EndX=-14.6 EndY=-36.4 EndZ=0
    g21: LineSegment StartX=-17.6 StartY=-1.8 StartZ=0 EndX=-17.6 EndY=-36.4 EndZ=0
    g22: LineSegment StartX=-20.6 StartY=-36.4 StartZ=0 EndX=-20.6 EndY=-1.8 EndZ=0
    g23: LineSegment StartX=-23.6 StartY=-1.8 StartZ=0 EndX=-23.6 EndY=-36.4 EndZ=0
  constraints (48):
    c: Block(g0)
    c: Block(g1)
    c: Block(g2)
    c: Block(g3)
    c: Block(g4)
    c: Block(g5)
    c: Block(g6)
    c: Block(g7)
    c: Block(g8)
    c: Block(g9)
    c: Block(g10)
    c: Block(g11)
    c: Coincident(g12,g1)
    c: Coincident(g12,g2)
    c: Vertical(g12)
    c: Coincident(g13,g1)
    c: Coincident(g13,g2)
    c: Vertical(g13)
    c: Coincident(g14,g11)
    c: Coincident(g14,g7)
    c: Vertical(g14)
    c: Coincident(g15,g11)
    c: Coincident(g15,g7)
    c: Vertical(g15)
    c: Coincident(g16,g0)
    c: Coincident(g16,g3)
    c: Vertical(g16)
    c: Coincident(g17,g4)
    c: Coincident(g17,g8)
    c: Vertical(g17)
    c: Coincident(g18,g0)
    c: Coincident(g18,g3)
    c: Vertical(g18)
    c: Coincident(g19,g4)
    c: Coincident(g19,g8)
    c: Vertical(g19)
    c: Coincident(g20,g5)
    c: Coincident(g20,g9)
    c: Vertical(g20)
    c: Coincident(g21,g5)
    c: Coincident(g21,g9)
    c: Vertical(g21)
    c: Coincident(g22,g10)
    c: Coincident(g22,g6)
    c: Vertical(g22)
    c: Coincident(g23,g6)
    c: Coincident(g23,g10)
    c: Vertical(g23)
FEATURE [Part::Extrusion] Extrude020  label="removeToCreateFanGrillHoles"
  Base = -> Sketch029
  Dir = (0,-1,6e-16)
  DirMode = 2
  FaceMakerClass = Part::FaceMakerBullseye
  LengthFwd = 10
  LengthRev = 0
  Placement = pos=(65.4,44,54.82) rot=(0,0,1;0rad)
  Solid = true
  Symmetric = false
FEATURE [Part::MultiFuse] Fusion055  label="top008"
  Shapes = -> [Cut017,Cut018]
FEATURE [Part::Cut] Cut019  label="top009"
  Base = -> Fusion055
  Tool = -> Extrude020
FEATURE [App::MeasureDistance] Distance003  label="Distance: 71.95 mm"
  Distance = 71.9513
  P1 = (117,38,72)
  P2 = (117,38,0.0487319)
FEATURE [Sketcher::SketchObject] Sketch030
  FullyConstrained = true
  Placement = pos=(117,19,0) rot=(0.57735,0.57735,0.57735;2.0944rad)
  sketch-geometry (48):
    g0: LineSegment StartX=-49.19 StartY=69.25 StartZ=0 EndX=-49.19 EndY=66.25 EndZ=0
    g1: LineSegment StartX=-49.19 StartY=63.5 StartZ=0 EndX=-49.19 EndY=60.5 EndZ=0
    g2: LineSegment StartX=-49.19 StartY=57.75 StartZ=0 EndX=-49.19 EndY=54.75 EndZ=0
    g3: LineSegment StartX=-49.19 StartY=52 StartZ=0 EndX=-49.19 EndY=49 EndZ=0
    g4: LineSegment StartX=-49.19 StartY=46.25 StartZ=0 EndX=-49.19 EndY=43.25 EndZ=0
    g5: LineSegment StartX=-49.19 StartY=40.5 StartZ=0 EndX=-49.19 EndY=37.5 EndZ=0
    g6: LineSegment StartX=-49.19 StartY=34.5 StartZ=0 EndX=-49.19 EndY=31.5 EndZ=0
    g7: LineSegment StartX=-49.19 StartY=28.75 StartZ=0 EndX=-49.19 EndY=25.75 EndZ=0
    g8: LineSegment StartX=-49.19 StartY=23 StartZ=0 EndX=-49.19 EndY=20 EndZ=0
    g9: LineSegment StartX=-49.19 StartY=17.25 StartZ=0 EndX=-49.19 EndY=14.25 EndZ=0
    g10: LineSegment StartX=-49.19 StartY=11.5 StartZ=0 EndX=-49.19 EndY=8.5 EndZ=0
    g11: LineSegment StartX=-49.19 StartY=5.75 StartZ=0 EndX=-49.19 EndY=2.75 EndZ=0
    g12: ArcOfCircle CenterX=-1.5 CenterY=67.75 CenterZ=0 NormalX=0 NormalY=0 NormalZ=1 AngleXU=0 Radius=1.5 StartAngle=4.71239 EndAngle=7.85398
    g13: ArcOfCircle CenterX=-1.5 CenterY=62 CenterZ=0 NormalX=0 NormalY=0 NormalZ=1 AngleXU=0 Radius=1.5 StartAngle=4.71239 EndAngle=7.85398
    g14: ArcOfCircle CenterX=-1.5 CenterY=56.25 CenterZ=0 NormalX=0 NormalY=0 NormalZ=1 AngleXU=0 Radius=1.5 StartAngle=4.71239 EndAngle=7.85398
    g15: ArcOfCircle CenterX=-11.49 CenterY=50.5 CenterZ=0 NormalX=0 NormalY=0 NormalZ=1 AngleXU=0 Radius=1.5 StartAngle=4.71239 EndAngle=7.85398
    g16: ArcOfCircle CenterX=-16.28 CenterY=44.75 CenterZ=0 NormalX=0 NormalY=0 NormalZ=1 AngleXU=0 Radius=1.5 StartAngle=4.71239 EndAngle=7.85398
    g17: ArcOfCircle CenterX=-18.2337 CenterY=39 CenterZ=0 NormalX=0 NormalY=0 NormalZ=1 AngleXU=0 Radius=1.5 StartAngle=4.71485 EndAngle=7.85398
    g18: ArcOfCircle CenterX=-16.2837 CenterY=27.25 CenterZ=0 NormalX=0 NormalY=0 NormalZ=1 AngleXU=0 Radius=1.5 StartAngle=4.71485 EndAngle=7.85398
    g19: ArcOfCircle CenterX=-18.2337 CenterY=33 CenterZ=0 NormalX=0 NormalY=0 NormalZ=1 AngleXU=0 Radius=1.5 StartAngle=4.71485 EndAngle=7.85398
    g20: ArcOfCircle CenterX=-11.49 CenterY=21.5 CenterZ=0 NormalX=0 NormalY=0 NormalZ=1 AngleXU=0 Radius=1.5 StartAngle=4.71239 EndAngle=7.85398
    g21: ArcOfCircle CenterX=-1.5 CenterY=4.25 CenterZ=0 NormalX=0 NormalY=0 NormalZ=1 AngleXU=0 Radius=1.5 StartAngle=4.71239 EndAngle=7.85398
    g22: ArcOfCircle CenterX=-1.5 CenterY=10 CenterZ=0 NormalX=0 NormalY=0 NormalZ=1 AngleXU=0 Radius=1.5 StartAngle=4.71239 EndAngle=7.85398
    g23: ArcOfCircle CenterX=-1.5 CenterY=15.75 CenterZ=0 NormalX=0 NormalY=0 NormalZ=1 AngleXU=0 Radius=1.5 StartAngle=4.71239 EndAngle=7.85398
    g24: LineSegment StartX=-49.19 StartY=69.25 StartZ=0 EndX=-1.5 EndY=69.25 EndZ=0
    g25: LineSegment StartX=-49.19 StartY=66.25 StartZ=0 EndX=-1.5 EndY=66.25 EndZ=0
    g26: LineSegment StartX=-49.19 StartY=63.5 StartZ=0 EndX=-1.5 EndY=63.5 EndZ=0
    g27: LineSegment StartX=-49.19 StartY=60.5 StartZ=0 EndX=-1.5 EndY=60.5 EndZ=0
    g28: LineSegment StartX=-49.19 StartY=57.75 StartZ=0 EndX=-1.5 EndY=57.75 EndZ=0
    g29: LineSegment StartX=-49.19 StartY=54.75 StartZ=0 EndX=-1.5 EndY=54.75 EndZ=0
    g30: LineSegment StartX=-49.19 StartY=52 StartZ=0 EndX=-11.49 EndY=52 EndZ=0
    g31: LineSegment StartX=-49.19 StartY=49 StartZ=0 EndX=-11.49 EndY=49 EndZ=0
    g32: LineSegment StartX=-49.19 StartY=46.25 StartZ=0 EndX=-16.28 EndY=46.25 EndZ=0
    g33: LineSegment StartX=-49.19 StartY=43.25 StartZ=0 EndX=-16.28 EndY=43.25 EndZ=0
    g34: LineSegment StartX=-49.19 StartY=40.5 StartZ=0 EndX=-18.2337 EndY=40.5 EndZ=0
    g35: LineSegment StartX=-49.19 StartY=37.5 StartZ=0 EndX=-18.23 EndY=37.5 EndZ=0
    g36: LineSegment StartX=-49.19 StartY=34.5 StartZ=0 EndX=-18.2337 EndY=34.5 EndZ=0
    g37: LineSegment StartX=-49.19 StartY=31.5 StartZ=0 EndX=-18.23 EndY=31.5 EndZ=0
    g38: LineSegment StartX=-49.19 StartY=28.75 StartZ=0 EndX=-16.2837 EndY=28.75 EndZ=0
    g39: LineSegment StartX=-49.19 StartY=25.75 StartZ=0 EndX=-16.28 EndY=25.75 EndZ=0
    g40: LineSegment StartX=-49.19 StartY=23 StartZ=0 EndX=-11.49 EndY=23 EndZ=0
    g41: LineSegment StartX=-49.19 StartY=20 StartZ=0 EndX=-11.49 EndY=20 EndZ=0
    g42: LineSegment StartX=-49.19 StartY=17.25 StartZ=0 EndX=-1.5 EndY=17.25 EndZ=0
    g43: LineSegment StartX=-49.19 StartY=14.25 StartZ=0 EndX=-1.5 EndY=14.25 EndZ=0
    g44: LineSegment StartX=-49.19 StartY=11.5 StartZ=0 EndX=-1.5 EndY=11.5 EndZ=0
    g45: LineSegment StartX=-49.19 StartY=8.5 StartZ=0 EndX=-1.5 EndY=8.5 EndZ=0
    g46: LineSegment StartX=-49.19 StartY=5.75 StartZ=0 EndX=-1.5 EndY=5.75 EndZ=0
    g47: LineSegment StartX=-49.19 StartY=2.75 StartZ=0 EndX=-1.5 EndY=2.75 EndZ=0
  constraints (120):
    c: Vertical(g0)
    c: Distance(g0) = 3
    c: Block(g0)
    c: Vertical(g1)
    c: Distance(g1) = 3
    c: Vertical(g2)
    c: Equal(g0,g2) = 3
    c: Block(g2)
    c: Vertical(g3)
    c: Equal(g1,g3) = 3
    c: Vertical(g4)
    c: Equal(g0,g4) = 3
    c: Block(g4)
    c: Vertical(g5)
    c: Equal(g1,g5) = 3
    c: Vertical(g6)
    c: Equal(g0,g6) = 3
    c: Block(g6)
    c: Vertical(g7)
    c: Equal(g1,g7) = 3
    c: Vertical(g8)
    c: Equal(g0,g8) = 3
    c: Block(g8)
    c: Vertical(g9)
    c: Equal(g1,g9) = 3
    c: Vertical(g10)
    c: Equal(g0,g10) = 3
    c: Block(g10)
    c: Vertical(g11)
    c: Equal(g1,g11) = 3
    c: Block(g12)
    c: Block(g13)
    c: Block(g14)
    c: Block(g15)
    c: Block(g16)
    c: Block(g17)
    c: Block(g18)
    c: Block(g19)
    c: Block(g20)
    c: Block(g21)
    c: Block(g22)
    c: Block(g23)
    c: Block(g11)
    c: Block(g9)
    c: Block(g7)
    c: Block(g5)
    c: Block(g3)
    c: Block(g1)
    c: Coincident(g24,g0)
    c: Coincident(g24,g12)
    c: Horizontal(g24)
    c: Coincident(g25,g0)
    c: Coincident(g25,g12)
    c: Horizontal(g25)
    c: Coincident(g26,g1)
    c: Coincident(g26,g13)
    c: Horizontal(g26)
    c: Coincident(g27,g1)
    c: Coincident(g27,g13)
    c: Horizontal(g27)
    c: Coincident(g28,g2)
    c: Coincident(g28,g14)
    c: Horizontal(g28)
    c: Coincident(g29,g2)
    c: Coincident(g29,g14)
    c: Horizontal(g29)
    c: Coincident(g30,g3)
    c: Coincident(g30,g15)
    c: Horizontal(g30)
    c: Coincident(g31,g3)
    c: Coincident(g31,g15)
    c: Horizontal(g31)
    c: Coincident(g32,g4)
    c: Coincident(g32,g16)
    c: Horizontal(g32)
    c: Coincident(g33,g4)
    c: Coincident(g33,g16)
    c: Horizontal(g33)
    c: Coincident(g34,g5)
    c: Coincident(g34,g17)
    c: Horizontal(g34)
    c: Coincident(g35,g5)
    c: Coincident(g35,g17)
    c: Horizontal(g35)
    c: Coincident(g36,g6)
    c: Coincident(g36,g19)
    c: Horizontal(g36)
    c: Coincident(g37,g6)
    c: Coincident(g37,g19)
    c: Horizontal(g37)
    c: Coincident(g38,g7)
    c: Coincident(g38,g18)
    c: Horizontal(g38)
    c: Coincident(g39,g7)
    c: Coincident(g39,g18)
    c: Horizontal(g39)
    c: Coincident(g40,g8)
    c: Coincident(g40,g20)
    c: Horizontal(g40)
    c: Coincident(g41,g8)
    c: Coincident(g41,g20)
    c: Horizontal(g41)
    c: Coincident(g42,g9)
    c: Coincident(g42,g23)
    c: Horizontal(g42)
    c: Coincident(g43,g9)
    c: Coincident(g43,g23)
    c: Horizontal(g43)
    c: Coincident(g44,g10)
    c: Coincident(g44,g22)
    c: Horizontal(g44)
    c: Coincident(g45,g10)
    c: Coincident(g45,g22)
    c: Horizontal(g45)
    c: Coincident(g46,g11)
    c: Coincident(g46,g21)
    c: Horizontal(g46)
    c: Coincident(g47,g11)
    c: Coincident(g47,g21)
    c: Horizontal(g47)
FEATURE [Sketcher::SketchObject] Sketch031
  FullyConstrained = true
  Placement = pos=(117,19,0) rot=(0.57735,0.57735,0.57735;2.0944rad)
  sketch-geometry (24):
    g0: ArcOfCircle CenterX=-49.19 CenterY=67.75 CenterZ=0 NormalX=0 NormalY=0 NormalZ=1 AngleXU=0 Radius=1.5 StartAngle=1.5708 EndAngle=4.71239
    g1: ArcOfCircle CenterX=-49.19 CenterY=62 CenterZ=0 NormalX=0 NormalY=0 NormalZ=1 AngleXU=0 Radius=1.5 StartAngle=1.5708 EndAngle=4.71239
    g2: ArcOfCircle CenterX=-49.19 CenterY=56.25 CenterZ=0 NormalX=0 NormalY=0 NormalZ=1 AngleXU=0 Radius=1.5 StartAngle=1.5708 EndAngle=4.71239
    g3: ArcOfCircle CenterX=-49.19 CenterY=50.5 CenterZ=0 NormalX=0 NormalY=0 NormalZ=1 AngleXU=0 Radius=1.5 StartAngle=1.5708 EndAngle=4.71239
    g4: ArcOfCircle CenterX=-49.19 CenterY=44.75 CenterZ=0 NormalX=0 NormalY=0 NormalZ=1 AngleXU=0 Radius=1.5 StartAngle=1.5708 EndAngle=4.71239
    g5: ArcOfCircle CenterX=-49.19 CenterY=39 CenterZ=0 NormalX=0 NormalY=0 NormalZ=1 AngleXU=0 Radius=1.5 StartAngle=1.5708 EndAngle=4.71239
    g6: ArcOfCircle CenterX=-49.19 CenterY=33 CenterZ=0 NormalX=0 NormalY=0 NormalZ=1 AngleXU=0 Radius=1.5 StartAngle=1.5708 EndAngle=4.71239
    g7: ArcOfCircle CenterX=-49.19 CenterY=27.25 CenterZ=0 NormalX=0 NormalY=0 NormalZ=1 AngleXU=0 Radius=1.5 StartAngle=1.5708 EndAngle=4.71239
    g8: ArcOfCircle CenterX=-49.19 CenterY=21.5 CenterZ=0 NormalX=0 NormalY=0 NormalZ=1 AngleXU=0 Radius=1.5 StartAngle=1.5708 EndAngle=4.71239
    g9: ArcOfCircle CenterX=-49.19 CenterY=15.75 CenterZ=0 NormalX=0 NormalY=0 NormalZ=1 AngleXU=0 Radius=1.5 StartAngle=1.5708 EndAngle=4.71239
    g10: ArcOfCircle CenterX=-49.19 CenterY=10 CenterZ=0 NormalX=0 NormalY=0 NormalZ=1 AngleXU=0 Radius=1.5 StartAngle=1.5708 EndAngle=4.71239
    g11: ArcOfCircle CenterX=-49.19 CenterY=4.25 CenterZ=0 NormalX=0 NormalY=0 NormalZ=1 AngleXU=0 Radius=1.5 StartAngle=1.5708 EndAngle=4.71239
    g12: LineSegment StartX=-49.19 StartY=69.25 StartZ=0 EndX=-49.19 EndY=66.25 EndZ=0
    g13: LineSegment StartX=-49.19 StartY=63.5 StartZ=0 EndX=-49.19 EndY=60.5 EndZ=0
    g14: LineSegment StartX=-49.19 StartY=57.75 StartZ=0 EndX=-49.19 EndY=54.75 EndZ=0
    g15: LineSegment StartX=-49.19 StartY=52 StartZ=0 EndX=-49.19 EndY=49 EndZ=0
    g16: LineSegment StartX=-49.19 StartY=46.25 StartZ=0 EndX=-49.19 EndY=43.25 EndZ=0
    g17: LineSegment StartX=-49.19 StartY=40.5 StartZ=0 EndX=-49.19 EndY=37.5 EndZ=0
    g18: LineSegment StartX=-49.19 StartY=34.5 StartZ=0 EndX=-49.19 EndY=31.5 EndZ=0
    g19: LineSegment StartX=-49.19 StartY=28.75 StartZ=0 EndX=-49.19 EndY=25.75 EndZ=0
    g20: LineSegment StartX=-49.19 StartY=23 StartZ=0 EndX=-49.19 EndY=20 EndZ=0
    g21: LineSegment StartX=-49.19 StartY=17.25 StartZ=0 EndX=-49.19 EndY=14.25 EndZ=0
    g22: LineSegment StartX=-49.19 StartY=11.5 StartZ=0 EndX=-49.19 EndY=8.5 EndZ=0
    g23: LineSegment StartX=-49.19 StartY=5.75 StartZ=0 EndX=-49.19 EndY=2.75 EndZ=0
  constraints (48):
    c: Block(g0)
    c: Block(g1)
    c: Block(g2)
    c: Block(g3)
    c: Block(g4)
    c: Block(g5)
    c: Block(g6)
    c: Block(g7)
    c: Block(g8)
    c: Block(g9)
    c: Block(g10)
    c: Block(g11)
    c: Coincident(g12,g0)
    c: Coincident(g12,g0)
    c: Vertical(g12)
    c: Vertical(g13)
    c: Coincident(g13,g1)
    c: Vertical(g14)
    c: Coincident(g14,g2)
    c: Vertical(g15)
    c: Coincident(g15,g3)
    c: Vertical(g16)
    c: Coincident(g16,g4)
    c: Vertical(g17)
    c: Coincident(g17,g5)
    c: Vertical(g18)
    c: Coincident(g18,g6)
    c: Vertical(g19)
    c: Coincident(g19,g7)
    c: Vertical(g20)
    c: Coincident(g20,g8)
    c: Vertical(g21)
    c: Coincident(g21,g9)
    c: Vertical(g22)
    c: Coincident(g22,g10)
    c: Vertical(g23)
    c: Coincident(g23,g11)
    c: Block(g23)
    c: Block(g22)
    c: Block(g21)
    c: Block(g20)
    c: Block(g13)
    c: Block(g14)
    c: Block(g15)
    c: Block(g16)
    c: Block(g17)
    c: Block(g18)
    c: Block(g19)
FEATURE [Part::Extrusion] Extrude022
  Base = -> Sketch030
  Dir = (1,-2e-16,2e-16)
  DirMode = 2
  FaceMakerClass = Part::FaceMakerBullseye
  LengthFwd = 19
  LengthRev = 0
  Placement = pos=(-19,0,0) rot=(0,0,1;0rad)
  Solid = true
  Symmetric = false
FEATURE [Part::Fillet] Fillet022
  Base = -> Extrude022
  Edges = 24 edges r=1.49: [Edge6,Edge11,Edge18,Edge23,Edge30,Edge35,Edge42,Edge47,Edge54,Edge59,Edge66,Edge71,Edge78,Edge83,Edge90,Edge95,Edge102,Edge107,Edge114,Edge119,Edge126,Edge131,Edge138,Edge143]
FEATURE [Part::Cut] Cut020  label="top010"
  Base = -> Cut019
  Tool = -> Fillet022
FEATURE [Sketcher::SketchObject] Sketch032
  FullyConstrained = true
  Placement = pos=(117,19,0) rot=(0.57735,0.57735,0.57735;2.0944rad)
  sketch-geometry (48):
    g0: LineSegment StartX=-49.19 StartY=69.25 StartZ=0 EndX=-49.19 EndY=66.25 EndZ=0
    g1: LineSegment StartX=-49.19 StartY=63.5 StartZ=0 EndX=-49.19 EndY=60.5 EndZ=0
    g2: LineSegment StartX=-49.19 StartY=57.75 StartZ=0 EndX=-49.19 EndY=54.75 EndZ=0
    g3: LineSegment StartX=-49.19 StartY=52 StartZ=0 EndX=-49.19 EndY=49 EndZ=0
    g4: LineSegment StartX=-49.19 StartY=46.25 StartZ=0 EndX=-49.19 EndY=43.25 EndZ=0
    g5: LineSegment StartX=-49.19 StartY=40.5 StartZ=0 EndX=-49.19 EndY=37.5 EndZ=0
    g6: LineSegment StartX=-49.19 StartY=34.5 StartZ=0 EndX=-49.19 EndY=31.5 EndZ=0
    g7: LineSegment StartX=-49.19 StartY=28.75 StartZ=0 EndX=-49.19 EndY=25.75 EndZ=0
    g8: LineSegment StartX=-49.19 StartY=23 StartZ=0 EndX=-49.19 EndY=20 EndZ=0
    g9: LineSegment StartX=-49.19 StartY=17.25 StartZ=0 EndX=-49.19 EndY=14.25 EndZ=0
    g10: LineSegment StartX=-49.19 StartY=11.5 StartZ=0 EndX=-49.19 EndY=8.5 EndZ=0
    g11: LineSegment StartX=-49.19 StartY=5.75 StartZ=0 EndX=-49.19 EndY=2.75 EndZ=0
    g12: ArcOfCircle CenterX=-1.5 CenterY=67.75 CenterZ=0 NormalX=0 NormalY=0 NormalZ=1 AngleXU=0 Radius=1.5 StartAngle=4.71239 EndAngle=7.85398
    g13: ArcOfCircle CenterX=-1.5 CenterY=62 CenterZ=0 NormalX=0 NormalY=0 NormalZ=1 AngleXU=0 Radius=1.5 StartAngle=4.71239 EndAngle=7.85398
    g14: ArcOfCircle CenterX=-1.5 CenterY=56.25 CenterZ=0 NormalX=0 NormalY=0 NormalZ=1 AngleXU=0 Radius=1.5 StartAngle=4.71239 EndAngle=7.85398
    g15: ArcOfCircle CenterX=-11.49 CenterY=50.5 CenterZ=0 NormalX=0 NormalY=0 NormalZ=1 AngleXU=0 Radius=1.5 StartAngle=4.71239 EndAngle=7.85398
    g16: ArcOfCircle CenterX=-16.28 CenterY=44.75 CenterZ=0 NormalX=0 NormalY=0 NormalZ=1 AngleXU=0 Radius=1.5 StartAngle=4.71239 EndAngle=7.85398
    g17: ArcOfCircle CenterX=-18.2337 CenterY=39 CenterZ=0 NormalX=0 NormalY=0 NormalZ=1 AngleXU=0 Radius=1.5 StartAngle=4.71485 EndAngle=7.85398
    g18: ArcOfCircle CenterX=-16.2837 CenterY=27.25 CenterZ=0 NormalX=0 NormalY=0 NormalZ=1 AngleXU=0 Radius=1.5 StartAngle=4.71485 EndAngle=7.85398
    g19: ArcOfCircle CenterX=-18.2337 CenterY=33 CenterZ=0 NormalX=0 NormalY=0 NormalZ=1 AngleXU=0 Radius=1.5 StartAngle=4.71485 EndAngle=7.85398
    g20: ArcOfCircle CenterX=-11.49 CenterY=21.5 CenterZ=0 NormalX=0 NormalY=0 NormalZ=1 AngleXU=0 Radius=1.5 StartAngle=4.71239 EndAngle=7.85398
    g21: ArcOfCircle CenterX=-1.5 CenterY=4.25 CenterZ=0 NormalX=0 NormalY=0 NormalZ=1 AngleXU=0 Radius=1.5 StartAngle=4.71239 EndAngle=7.85398
    g22: ArcOfCircle CenterX=-1.5 CenterY=10 CenterZ=0 NormalX=0 NormalY=0 NormalZ=1 AngleXU=0 Radius=1.5 StartAngle=4.71239 EndAngle=7.85398
    g23: ArcOfCircle CenterX=-1.5 CenterY=15.75 CenterZ=0 NormalX=0 NormalY=0 NormalZ=1 AngleXU=0 Radius=1.5 StartAngle=4.71239 EndAngle=7.85398
    g24: LineSegment StartX=-49.19 StartY=69.25 StartZ=0 EndX=-1.5 EndY=69.25 EndZ=0
    g25: LineSegment StartX=-49.19 StartY=66.25 StartZ=0 EndX=-1.5 EndY=66.25 EndZ=0
    g26: LineSegment StartX=-49.19 StartY=63.5 StartZ=0 EndX=-1.5 EndY=63.5 EndZ=0
    g27: LineSegment StartX=-49.19 StartY=60.5 StartZ=0 EndX=-1.5 EndY=60.5 EndZ=0
    g28: LineSegment StartX=-49.19 StartY=57.75 StartZ=0 EndX=-1.5 EndY=57.75 EndZ=0
    g29: LineSegment StartX=-49.19 StartY=54.75 StartZ=0 EndX=-1.5 EndY=54.75 EndZ=0
    g30: LineSegment StartX=-49.19 StartY=52 StartZ=0 EndX=-11.49 EndY=52 EndZ=0
    g31: LineSegment StartX=-49.19 StartY=49 StartZ=0 EndX=-11.49 EndY=49 EndZ=0
    g32: LineSegment StartX=-49.19 StartY=46.25 StartZ=0 EndX=-16.28 EndY=46.25 EndZ=0
    g33: LineSegment StartX=-49.19 StartY=43.25 StartZ=0 EndX=-16.28 EndY=43.25 EndZ=0
    g34: LineSegment StartX=-49.19 StartY=40.5 StartZ=0 EndX=-18.2337 EndY=40.5 EndZ=0
    g35: LineSegment StartX=-49.19 StartY=37.5 StartZ=0 EndX=-18.23 EndY=37.5 EndZ=0
    g36: LineSegment StartX=-49.19 StartY=34.5 StartZ=0 EndX=-18.2337 EndY=34.5 EndZ=0
    g37: LineSegment StartX=-49.19 StartY=31.5 StartZ=0 EndX=-18.23 EndY=31.5 EndZ=0
    g38: LineSegment StartX=-49.19 StartY=28.75 StartZ=0 EndX=-16.2837 EndY=28.75 EndZ=0
    g39: LineSegment StartX=-49.19 StartY=25.75 StartZ=0 EndX=-16.28 EndY=25.75 EndZ=0
    g40: LineSegment StartX=-49.19 StartY=23 StartZ=0 EndX=-11.49 EndY=23 EndZ=0
    g41: LineSegment StartX=-49.19 StartY=20 StartZ=0 EndX=-11.49 EndY=20 EndZ=0
    g42: LineSegment StartX=-49.19 StartY=17.25 StartZ=0 EndX=-1.5 EndY=17.25 EndZ=0
    g43: LineSegment StartX=-49.19 StartY=14.25 StartZ=0 EndX=-1.5 EndY=14.25 EndZ=0
    g44: LineSegment StartX=-49.19 StartY=11.5 StartZ=0 EndX=-1.5 EndY=11.5 EndZ=0
    g45: LineSegment StartX=-49.19 StartY=8.5 StartZ=0 EndX=-1.5 EndY=8.5 EndZ=0
    g46: LineSegment StartX=-49.19 StartY=5.75 StartZ=0 EndX=-1.5 EndY=5.75 EndZ=0
    g47: LineSegment StartX=-49.19 StartY=2.75 StartZ=0 EndX=-1.5 EndY=2.75 EndZ=0
  constraints (120):
    c: Vertical(g0)
    c: Distance(g0) = 3
    c: Block(g0)
    c: Vertical(g1)
    c: Distance(g1) = 3
    c: Vertical(g2)
    c: Equal(g0,g2) = 3
    c: Block(g2)
    c: Vertical(g3)
    c: Equal(g1,g3) = 3
    c: Vertical(g4)
    c: Equal(g0,g4) = 3
    c: Block(g4)
    c: Vertical(g5)
    c: Equal(g1,g5) = 3
    c: Vertical(g6)
    c: Equal(g0,g6) = 3
    c: Block(g6)
    c: Vertical(g7)
    c: Equal(g1,g7) = 3
    c: Vertical(g8)
    c: Equal(g0,g8) = 3
    c: Block(g8)
    c: Vertical(g9)
    c: Equal(g1,g9) = 3
    c: Vertical(g10)
    c: Equal(g0,g10) = 3
    c: Block(g10)
    c: Vertical(g11)
    c: Equal(g1,g11) = 3
    c: Block(g12)
    c: Block(g13)
    c: Block(g14)
    c: Block(g15)
    c: Block(g16)
    c: Block(g17)
    c: Block(g18)
    c: Block(g19)
    c: Block(g20)
    c: Block(g21)
    c: Block(g22)
    c: Block(g23)
    c: Block(g11)
    c: Block(g9)
    c: Block(g7)
    c: Block(g5)
    c: Block(g3)
    c: Block(g1)
    c: Coincident(g24,g0)
    c: Coincident(g24,g12)
    c: Horizontal(g24)
    c: Coincident(g25,g0)
    c: Coincident(g25,g12)
    c: Horizontal(g25)
    c: Coincident(g26,g1)
    c: Coincident(g26,g13)
    c: Horizontal(g26)
    c: Coincident(g27,g1)
    c: Coincident(g27,g13)
    c: Horizontal(g27)
    c: Coincident(g28,g2)
    c: Coincident(g28,g14)
    c: Horizontal(g28)
    c: Coincident(g29,g2)
    c: Coincident(g29,g14)
    c: Horizontal(g29)
    c: Coincident(g30,g3)
    c: Coincident(g30,g15)
    c: Horizontal(g30)
    c: Coincident(g31,g3)
    c: Coincident(g31,g15)
    c: Horizontal(g31)
    c: Coincident(g32,g4)
    c: Coincident(g32,g16)
    c: Horizontal(g32)
    c: Coincident(g33,g4)
    c: Coincident(g33,g16)
    c: Horizontal(g33)
    c: Coincident(g34,g5)
    c: Coincident(g34,g17)
    c: Horizontal(g34)
    c: Coincident(g35,g5)
    c: Coincident(g35,g17)
    c: Horizontal(g35)
    c: Coincident(g36,g6)
    c: Coincident(g36,g19)
    c: Horizontal(g36)
    c: Coincident(g37,g6)
    c: Coincident(g37,g19)
    c: Horizontal(g37)
    c: Coincident(g38,g7)
    c: Coincident(g38,g18)
    c: Horizontal(g38)
    c: Coincident(g39,g7)
    c: Coincident(g39,g18)
    c: Horizontal(g39)
    c: Coincident(g40,g8)
    c: Coincident(g40,g20)
    c: Horizontal(g40)
    c: Coincident(g41,g8)
    c: Coincident(g41,g20)
    c: Horizontal(g41)
    c: Coincident(g42,g9)
    c: Coincident(g42,g23)
    c: Horizontal(g42)
    c: Coincident(g43,g9)
    c: Coincident(g43,g23)
    c: Horizontal(g43)
    c: Coincident(g44,g10)
    c: Coincident(g44,g22)
    c: Horizontal(g44)
    c: Coincident(g45,g10)
    c: Coincident(g45,g22)
    c: Horizontal(g45)
    c: Coincident(g46,g11)
    c: Coincident(g46,g21)
    c: Horizontal(g46)
    c: Coincident(g47,g11)
    c: Coincident(g47,g21)
    c: Horizontal(g47)
FEATURE [Part::Extrusion] Extrude023
  Base = -> Sketch032
  Dir = (1,-2e-16,2e-16)
  DirMode = 2
  FaceMakerClass = Part::FaceMakerBullseye
  LengthFwd = 19
  LengthRev = 0
  Placement = pos=(-19,0,0) rot=(0,0,1;0rad)
  Solid = true
  Symmetric = false
FEATURE [Part::Fillet] Fillet023
  Base = -> Extrude023
  Edges = <same value as first occurrence — deduplicated (x6 in doc)>
  Placement = pos=(0,0.05,0) rot=(0,0,1;0rad)
FEATURE [Part::Cut] Cut014  label="bottom003"
  Base = -> Cut007
  Tool = -> Fusion047
FEATURE [Part::Cut] Cut021  label="bottom004"
  Base = -> Cut014
  Tool = -> Fillet023
FEATURE [Sketcher::SketchObject] Sketch033
  FullyConstrained = true
  Placement = pos=(117,19,0) rot=(0.57735,0.57735,0.57735;2.0944rad)
  sketch-geometry (8):
    g0: LineSegment StartX=-49.19 StartY=69.25 StartZ=0 EndX=-49.19 EndY=66.25 EndZ=0
    g1: LineSegment StartX=-49.19 StartY=5.75 StartZ=0 EndX=-49.19 EndY=2.75 EndZ=0
    g2: ArcOfCircle CenterX=-1.5 CenterY=67.75 CenterZ=0 NormalX=0 NormalY=0 NormalZ=1 AngleXU=0 Radius=1.5 StartAngle=4.71239 EndAngle=7.85398
    g3: ArcOfCircle CenterX=-1.5 CenterY=4.25 CenterZ=0 NormalX=0 NormalY=0 NormalZ=1 AngleXU=0 Radius=1.5 StartAngle=4.71239 EndAngle=7.85398
    g4: LineSegment StartX=-49.19 StartY=69.25 StartZ=0 EndX=-1.5 EndY=69.25 EndZ=0
    g5: LineSegment StartX=-49.19 StartY=66.25 StartZ=0 EndX=-1.5 EndY=66.25 EndZ=0
    g6: LineSegment StartX=-49.19 StartY=5.75 StartZ=0 EndX=-1.5 EndY=5.75 EndZ=0
    g7: LineSegment StartX=-49.19 StartY=2.75 StartZ=0 EndX=-1.5 EndY=2.75 EndZ=0
  constraints (19):
    c: Vertical(g0)
    c: Distance(g0) = 3
    c: Block(g0)
    c: Vertical(g1)
    c: Block(g2)
    c: Block(g3)
    c: Block(g1)
    c: Coincident(g4,g0)
    c: Coincident(g4,g2)
    c: Horizontal(g4)
    c: Coincident(g5,g0)
    c: Coincident(g5,g2)
    c: Horizontal(g5)
    c: Coincident(g6,g1)
    c: Coincident(g6,g3)
    c: Horizontal(g6)
    c: Coincident(g7,g1)
    c: Coincident(g7,g3)
    c: Horizontal(g7)
FEATURE [Sketcher::SketchObject] Sketch034
  FullyConstrained = true
  Placement = pos=(117,19,0) rot=(0.57735,0.57735,0.57735;2.0944rad)
  sketch-geometry (8):
    g0: LineSegment StartX=-49.19 StartY=63.5 StartZ=0 EndX=-49.19 EndY=60.5 EndZ=0
    g1: LineSegment StartX=-49.19 StartY=11.5 StartZ=0 EndX=-49.19 EndY=8.5 EndZ=0
    g2: ArcOfCircle CenterX=-1.5 CenterY=62 CenterZ=0 NormalX=0 NormalY=0 NormalZ=1 AngleXU=0 Radius=1.5 StartAngle=4.71239 EndAngle=7.85398
    g3: ArcOfCircle CenterX=-1.5 CenterY=10 CenterZ=0 NormalX=0 NormalY=0 NormalZ=1 AngleXU=0 Radius=1.5 StartAngle=4.71239 EndAngle=7.85398
    g4: LineSegment StartX=-49.19 StartY=63.5 StartZ=0 EndX=-1.5 EndY=63.5 EndZ=0
    g5: LineSegment StartX=-49.19 StartY=60.5 StartZ=0 EndX=-1.5 EndY=60.5 EndZ=0
    g6: LineSegment StartX=-49.19 StartY=11.5 StartZ=0 EndX=-1.5 EndY=11.5 EndZ=0
    g7: LineSegment StartX=-49.19 StartY=8.5 StartZ=0 EndX=-1.5 EndY=8.5 EndZ=0
  constraints (19):
    c: Vertical(g0)
    c: Distance(g0) = 3
    c: Vertical(g1)
    c: Block(g1)
    c: Block(g2)
    c: Block(g3)
    c: Block(g0)
    c: Coincident(g4,g0)
    c: Coincident(g4,g2)
    c: Horizontal(g4)
    c: Coincident(g5,g0)
    c: Coincident(g5,g2)
    c: Horizontal(g5)
    c: Coincident(g6,g1)
    c: Coincident(g6,g3)
    c: Horizontal(g6)
    c: Coincident(g7,g1)
    c: Coincident(g7,g3)
    c: Horizontal(g7)
FEATURE [Part::Extrusion] Extrude024
  Base = -> Sketch033
  Dir = (1,0,0)
  DirMode = 2
  FaceMakerClass = Part::FaceMakerBullseye
  LengthFwd = 10
  LengthRev = 0
  Solid = true
  Symmetric = false
FEATURE [Part::Extrusion] Extrude025
  Base = -> Sketch034
  Dir = (1,0,0)
  DirMode = 2
  FaceMakerClass = Part::FaceMakerBullseye
  LengthFwd = 10
  LengthRev = 0
  Solid = true
  Symmetric = false
FEATURE [Part::Fillet] Fillet024  label="removeFromtMoreFrontCaseScrewRetainers"
  Base = -> Extrude024
  Edges = 4 edges r=1.49: [Edge6,Edge11,Edge18,Edge23]
  Placement = pos=(-11,0,0) rot=(0,0,1;0rad)
FEATURE [Part::Fillet] Fillet025  label="removeFromtMoreFrontCaseScrewRetainers001"
  Base = -> Extrude025
  Edges = 4 edges r=1.49: [Edge6,Edge11,Edge18,Edge23]
  Placement = pos=(-19,0,0) rot=(0,0,1;0rad)
FEATURE [Part::Cut] Cut022
  Base = -> Cut015
  Tool = -> Fillet025
FEATURE [Part::Cut] Cut023  label="screwRetainers"
  Base = -> Cut022
  Tool = -> Fillet024
FEATURE [Part::MultiFuse] Fusion056  label="bottom005"
  Shapes = -> [Fusion044,Cut021]
FEATURE [Part::MultiFuse] Fusion057  label="casePillars001"
  Shapes = -> [Cut016,Fusion052]
FEATURE [Part::MultiFuse] Fusion058  label="bottom006"
  Shapes = -> [Fusion056,Cut023]
FEATURE [Part::MultiFuse] Fusion059  label="bottom007"
  Shapes = -> [Fusion058,Fillet005]
FEATURE [Part::MultiFuse] Fusion060  label="bottom008"
  Shapes = -> [Fusion059,Fusion]
FEATURE [Part::MultiFuse] Fusion061  label="top011"
  Shapes = -> [Cut006,Cut020]
FEATURE [Part::MultiFuse] Fusion062  label="top012"
  Shapes = -> [Fusion057,Fusion061]
FEATURE [Sketcher::SketchObject] Sketch035  label="topSketch007"
  FullyConstrained = true
  sketch-geometry (6):
    g0: LineSegment StartX=19 StartY=38 StartZ=0 EndX=117 EndY=38 EndZ=0
    g1: ArcOfCircle CenterX=19 CenterY=19 CenterZ=0 NormalX=0 NormalY=0 NormalZ=1 AngleXU=0 Radius=19 StartAngle=1.5708 EndAngle=3.14159
    g2: LineSegment StartX=117 StartY=38 StartZ=0 EndX=117 EndY=19 EndZ=0
    g3: LineSegment StartX=98 StartY=1.0161e-12 StartZ=0 EndX=5.22862e-06 EndY=1.0161e-12 EndZ=0
    g4: LineSegment StartX=5.22862e-06 StartY=19 StartZ=0 EndX=5.22862e-06 EndY=1.0161e-12 EndZ=0
    g5: ArcOfCircle CenterX=98 CenterY=19 CenterZ=0 NormalX=0 NormalY=0 NormalZ=1 AngleXU=0 Radius=19 StartAngle=4.71239 EndAngle=6.28319
  constraints (16):
    c: Horizontal(g0)
    c: Distance(g0) = 98
    c: Coincident(g1,g0)
    c: Block(g1)
    c: Coincident(g2,g0)
    c: Vertical(g2)
    c: Distance(g2) = 19
    c: Horizontal(g3)
    c: Coincident(g4,g1)
    c: Vertical(g4)
    c: Coincident(g3,g4)
    c: Block(g3)
    c: Coincident(g5,g2)
    c: Coincident(g5,g3)
    c: Block(g0)
    c: Block(g5)
FEATURE [Part::Extrusion] Extrude026  label="sideA001"
  Base = -> Sketch035
  Dir = (0,0,1)
  DirMode = 2
  FaceMakerClass = Part::FaceMakerBullseye
  LengthFwd = 3
  LengthRev = 0
  Placement = pos=(0,0,-2.7) rot=(0,0,1;0rad)
  Solid = true
  Symmetric = false
FEATURE [Sketcher::SketchObject] Sketch036  label="topSketch008"
  FullyConstrained = true
  sketch-geometry (6):
    g0: LineSegment StartX=19 StartY=38 StartZ=0 EndX=117 EndY=38 EndZ=0
    g1: ArcOfCircle CenterX=19 CenterY=19 CenterZ=0 NormalX=0 NormalY=0 NormalZ=1 AngleXU=0 Radius=19 StartAngle=1.5708 EndAngle=3.14159
    g2: LineSegment StartX=117 StartY=38 StartZ=0 EndX=117 EndY=19 EndZ=0
    g3: LineSegment StartX=98 StartY=1.0161e-12 StartZ=0 EndX=5.22862e-06 EndY=1.0161e-12 EndZ=0
    g4: LineSegment StartX=5.22862e-06 StartY=19 StartZ=0 EndX=5.22862e-06 EndY=1.0161e-12 EndZ=0
    g5: ArcOfCircle CenterX=98 CenterY=19 CenterZ=0 NormalX=0 NormalY=0 NormalZ=1 AngleXU=0 Radius=19 StartAngle=4.71239 EndAngle=6.28319
  constraints (16):
    c: Horizontal(g0)
    c: Distance(g0) = 98
    c: Coincident(g1,g0)
    c: Block(g1)
    c: Coincident(g2,g0)
    c: Vertical(g2)
    c: Distance(g2) = 19
    c: Horizontal(g3)
    c: Coincident(g4,g1)
    c: Vertical(g4)
    c: Coincident(g3,g4)
    c: Block(g3)
    c: Coincident(g5,g2)
    c: Coincident(g5,g3)
    c: Block(g0)
    c: Block(g5)
FEATURE [Part::Extrusion] Extrude027  label="sideB001"
  Base = -> Sketch036
  Dir = (0,0,1)
  DirMode = 2
  FaceMakerClass = Part::FaceMakerBullseye
  LengthFwd = 3
  LengthRev = 0
  Placement = pos=(0,0,71.7) rot=(0,0,1;0rad)
  Solid = true
  Symmetric = false
FEATURE [Part::MultiFuse] Fusion064  label="removeFromBottom"
  Shapes = -> [Extrude026,Extrude027]
FEATURE [Part::Cut] Cut024  label="bottom009"
  Base = -> Fusion060
  Tool = -> Fusion064
FEATURE [Sketcher::SketchObject] Sketch037  label="topSketch009"
  FullyConstrained = true
  sketch-geometry (8):
    g0: ArcOfCircle CenterX=19 CenterY=19.1201 CenterZ=0 NormalX=0 NormalY=0 NormalZ=1 AngleXU=0 Radius=18.8799 StartAngle=1.5708 EndAngle=3.14793
    g1: LineSegment StartX=0.120501 StartY=19.0004 StartZ=0 EndX=0.120501 EndY=0.000382114 EndZ=0
    g2: LineSegment StartX=19 StartY=38 StartZ=0 EndX=124 EndY=38 EndZ=0
    g3: LineSegment StartX=0.120501 StartY=0.000382114 StartZ=0 EndX=105.121 EndY=0.000382114 EndZ=0
    g4: LineSegment StartX=124 StartY=38 StartZ=0 EndX=125.616 EndY=38 EndZ=0
    g5: LineSegment StartX=105.121 StartY=0.000382114 StartZ=0 EndX=106.736 EndY=0.000382114 EndZ=0
    g6: ArcOfCircle CenterX=106.616 CenterY=19 CenterZ=0 NormalX=0 NormalY=0 NormalZ=1 AngleXU=0 Radius=19 StartAngle=4.71873 EndAngle=6.28319
    g7: LineSegment StartX=125.616 StartY=38 StartZ=0 EndX=125.616 EndY=19 EndZ=0
  constraints (21):
    c: Block(g0)
    c: Coincident(g1,g0)
    c: Vertical(g1)
    c: Horizontal(g2)
    c: Distance(g2) = 105
    c: Coincident(g2,g0)
    c: Distance(g1) = 19
    c: Coincident(g3,g1)
    c: Horizontal(g3)
    c: Distance(g3) = 105
    c: Coincident(g4,g2)
    c: Horizontal(g4)
    c: Distance(g4) = 1.61553
    c: Horizontal(g5)
    c: Equal(g4,g5) = 1.61553
    c: Coincident(g5,g3)
    c: Block(g6)
    c: Coincident(g6,g5)
    c: Coincident(g7,g4)
    c: Coincident(g7,g6)
    c: Vertical(g7)
FEATURE [Part::Extrusion] Extrude028  label="sideB"
  Base = -> Sketch037
  Dir = (0,0,1)
  DirMode = 2
  FaceMakerClass = Part::FaceMakerBullseye
  LengthFwd = 3
  LengthRev = 0
  Placement = pos=(0,0,72) rot=(0,0,1;0rad)
  Solid = true
  Symmetric = false
FEATURE [Sketcher::SketchObject] Sketch038  label="topSketch010"
  FullyConstrained = true
  sketch-geometry (22):
    g0: LineSegment StartX=5.21097e-06 StartY=3 StartZ=0 EndX=5.21097e-06 EndY=19 EndZ=0
    g1: ArcOfCircle CenterX=19 CenterY=19 CenterZ=0 NormalX=0 NormalY=0 NormalZ=1 AngleXU=0 Radius=19 StartAngle=1.5708 EndAngle=3.14159
    g2: ArcOfCircle CenterX=19 CenterY=19 CenterZ=0 NormalX=0 NormalY=0 NormalZ=1 AngleXU=0 Radius=16 StartAngle=1.5708 EndAngle=3.14159
    g3: LineSegment StartX=114 StartY=35 StartZ=0 EndX=19 EndY=35 EndZ=0
    g4: LineSegment StartX=5.21097e-06 StartY=3 StartZ=0 EndX=5.21097e-06 EndY=0 EndZ=0
    g5: LineSegment StartX=3 StartY=0 StartZ=0 EndX=5.21097e-06 EndY=0 EndZ=0
    g6: LineSegment StartX=3 StartY=19 StartZ=0 EndX=3 EndY=0 EndZ=0
    g7: LineSegment StartX=19 StartY=38 StartZ=0 EndX=124 EndY=38 EndZ=0
    g8: Circle CenterX=119 CenterY=35 CenterZ=0 NormalX=0 NormalY=0 NormalZ=1 AngleXU=0 Radius=1
    g9: Circle CenterX=121 CenterY=35 CenterZ=0 NormalX=0 NormalY=0 NormalZ=1 AngleXU=0 Radius=1
    g10: Circle CenterX=121 CenterY=33 CenterZ=0 NormalX=0 NormalY=0 NormalZ=1 AngleXU=0 Radius=1
    g11: BSplineCurve PolesCount=3 KnotsCount=2 Degree=2 IsPeriodic=0
    g12: GeomPoint X=119 Y=35 Z=0
    g13: GeomPoint X=121 Y=33 Z=0
    g14: LineSegment StartX=119 StartY=35 StartZ=0 EndX=114 EndY=35 EndZ=0
    g15: ArcOfCircle CenterX=105 CenterY=19 CenterZ=0 NormalX=0 NormalY=0 NormalZ=1 AngleXU=0 Radius=16 StartAngle=5.60905 EndAngle=6.28319
    g16: LineSegment StartX=121 StartY=33 StartZ=0 EndX=121 EndY=19 EndZ=0
    g17: LineSegment StartX=117.5 StartY=9.01251 StartZ=0 EndX=121.163 EndY=9.0125 EndZ=0
    g18: ArcOfCircle CenterX=105 CenterY=19 CenterZ=0 NormalX=0 NormalY=0 NormalZ=1 AngleXU=0 Radius=20.6155 StartAngle=5.7297 EndAngle=6.28319
    g19: LineSegment StartX=121.163 StartY=9.0125 StartZ=0 EndX=122.538 EndY=8.16329 EndZ=0
    g20: LineSegment StartX=124 StartY=38 StartZ=0 EndX=125.616 EndY=38 EndZ=0
    g21: LineSegment StartX=125.616 StartY=19 StartZ=0 EndX=125.616 EndY=38 EndZ=0
  constraints (49):
    c: Vertical(g0)
    c: Block(g0)
    c: Coincident(g1,g0)
    c: Block(g1)
    c: Coincident(g2,g1)
    c: Block(g2)
    c: Coincident(g3,g2)
    c: Horizontal(g3)
    c: Tangent(g3,g2)
    c: Coincident(g4,g0)
    c: Distance(g4) = 3
    c: Vertical(g4)
    c: Coincident(g5,g4)
    c: Horizontal(g5)
    c: Coincident(g6,g2)
    c: Coincident(g6,g5)
    c: Vertical(g6)
    c: Horizontal(g7)
    c: Distance(g7) = 105
    c: Coincident(g7,g1)
    c: Block(g3)
    c: Weight(g8) = 1
    c: Equal(g8,g9)
    c: Equal(g8,g10)
    c: InternalAlignment(g8,g11)
    c: InternalAlignment(g9,g11)
    c: InternalAlignment(g10,g11)
    c: InternalAlignment(g12,g11)
    c: InternalAlignment(g13,g11)
    c: Block(g11)
    c: Coincident(g14,g11)
    c: Coincident(g14,g3)
    c: Horizontal(g14)
    c: Block(g15)
    c: Coincident(g16,g11)
    c: Coincident(g16,g15)
    c: Vertical(g16)
    c: Distance(g16) = 14
    c: Coincident(g17,g15)
    c: Block(g18)
    c: Coincident(g19,g18)
    c: Coincident(g20,g7)
    c: Horizontal(g20)
    c: Vertical(g21)
    c: Coincident(g20,g21)
    c: Block(g20)
    c: Block(g21)
    c: Block(g19)
    c: Block(g17)
FEATURE [Part::Extrusion] Extrude029
  Base = -> Sketch038
  Dir = (0,0,1)
  DirMode = 2
  FaceMakerClass = Part::FaceMakerBullseye
  LengthFwd = 72
  LengthRev = 0
  Solid = true
  Symmetric = false
FEATURE [Part::Feature] Face085
  shape: bbox 4.8 x 25.5 x 2e-07 mm, 1 faces, 0 solids (baked)
FEATURE [Part::Revolution] Revolve089  label="moreFrontCaseScrewPost003"
  Angle = 360
  Axis = (0,1,0)
  Base = (0,0,0)
  FaceMakerClass = Part::FaceMakerBullseye
  Placement = pos=(109.5,4.5,3.5) rot=(0,0,1;0rad)
  Solid = false
  Source = -> Face085
  Symmetric = false
FEATURE [Part::Feature] Face086
  shape: bbox 4.8 x 25.5 x 2e-07 mm, 1 faces, 0 solids (baked)
FEATURE [Part::Revolution] Revolve090  label="moreFrontCaseScrewPost004"
  Angle = 360
  Axis = (0,1,0)
  Base = (0,0,0)
  FaceMakerClass = Part::FaceMakerBullseye
  Placement = pos=(109.5,4.5,68.5) rot=(0,0,1;0rad)
  Solid = false
  Source = -> Face086
  Symmetric = false
FEATURE [Part::Fillet] Fillet026  label="top013"
  Base = -> Extrude029
  Edges = 1 edges r=2: [Edge35]
FEATURE [Sketcher::SketchObject] Sketch039
  FullyConstrained = true
  sketch-geometry (7):
    g0: LineSegment StartX=0 StartY=0 StartZ=0 EndX=0 EndY=6 EndZ=0
    g1: Circle CenterX=0 CenterY=0 CenterZ=0 NormalX=0 NormalY=0 NormalZ=1 AngleXU=0 Radius=1
    g2: Circle CenterX=8 CenterY=6 CenterZ=0 NormalX=0 NormalY=0 NormalZ=1 AngleXU=0 Radius=1
    g3: BSplineCurve PolesCount=3 KnotsCount=2 Degree=2 IsPeriodic=0
    g4: GeomPoint X=0 Y=0 Z=0
    g5: GeomPoint X=8 Y=6 Z=0
    g6: LineSegment StartX=0 StartY=6 StartZ=0 EndX=8 EndY=6 EndZ=0
  constraints (14):
    c: Coincident(g0,g-1)
    c: Distance(g0) = 6
    c: Vertical(g0)
    c: Coincident(g3,g0)
    c: Weight(g1) = 1
    c: Equal(g1,g2)
    c: InternalAlignment(g1,g3)
    c: InternalAlignment(g2,g3)
    c: InternalAlignment(g4,g3)
    c: InternalAlignment(g5,g3)
    c: Block(g3)
    c: Coincident(g6,g0)
    c: Coincident(g6,g3)
    c: Horizontal(g6)
FEATURE [Sketcher::SketchObject] Sketch040
  FullyConstrained = true
  sketch-geometry (7):
    g0: LineSegment StartX=0 StartY=0 StartZ=0 EndX=0 EndY=6 EndZ=0
    g1: Circle CenterX=0 CenterY=0 CenterZ=0 NormalX=0 NormalY=0 NormalZ=1 AngleXU=0 Radius=1
    g2: Circle CenterX=8 CenterY=6 CenterZ=0 NormalX=0 NormalY=0 NormalZ=1 AngleXU=0 Radius=1
    g3: BSplineCurve PolesCount=3 KnotsCount=2 Degree=2 IsPeriodic=0
    g4: GeomPoint X=0 Y=0 Z=0
    g5: GeomPoint X=8 Y=6 Z=0
    g6: LineSegment StartX=0 StartY=6 StartZ=0 EndX=8 EndY=6 EndZ=0
  constraints (14):
    c: Coincident(g0,g-1)
    c: Distance(g0) = 6
    c: Vertical(g0)
    c: Coincident(g3,g0)
    c: Weight(g1) = 1
    c: Equal(g1,g2)
    c: InternalAlignment(g1,g3)
    c: InternalAlignment(g2,g3)
    c: InternalAlignment(g4,g3)
    c: InternalAlignment(g5,g3)
    c: Block(g3)
    c: Coincident(g6,g0)
    c: Coincident(g6,g3)
    c: Horizontal(g6)
FEATURE [Sketcher::SketchObject] Sketch041
  FullyConstrained = true
  sketch-geometry (7):
    g0: LineSegment StartX=0 StartY=0 StartZ=0 EndX=0 EndY=6 EndZ=0
    g1: Circle CenterX=0 CenterY=0 CenterZ=0 NormalX=0 NormalY=0 NormalZ=1 AngleXU=0 Radius=1
    g2: Circle CenterX=8 CenterY=6 CenterZ=0 NormalX=0 NormalY=0 NormalZ=1 AngleXU=0 Radius=1
    g3: BSplineCurve PolesCount=3 KnotsCount=2 Degree=2 IsPeriodic=0
    g4: GeomPoint X=0 Y=0 Z=0
    g5: GeomPoint X=8 Y=6 Z=0
    g6: LineSegment StartX=0 StartY=6 StartZ=0 EndX=8 EndY=6 EndZ=0
  constraints (14):
    c: Coincident(g0,g-1)
    c: Distance(g0) = 6
    c: Vertical(g0)
    c: Coincident(g3,g0)
    c: Weight(g1) = 1
    c: Equal(g1,g2)
    c: InternalAlignment(g1,g3)
    c: InternalAlignment(g2,g3)
    c: InternalAlignment(g4,g3)
    c: InternalAlignment(g5,g3)
    c: Block(g3)
    c: Coincident(g6,g0)
    c: Coincident(g6,g3)
    c: Horizontal(g6)
FEATURE [Sketcher::SketchObject] Sketch042
  FullyConstrained = true
  sketch-geometry (7):
    g0: LineSegment StartX=0 StartY=0 StartZ=0 EndX=0 EndY=6 EndZ=0
    g1: Circle CenterX=0 CenterY=0 CenterZ=0 NormalX=0 NormalY=0 NormalZ=1 AngleXU=0 Radius=1
    g2: Circle CenterX=8 CenterY=6 CenterZ=0 NormalX=0 NormalY=0 NormalZ=1 AngleXU=0 Radius=1
    g3: BSplineCurve PolesCount=3 KnotsCount=2 Degree=2 IsPeriodic=0
    g4: GeomPoint X=0 Y=0 Z=0
    g5: GeomPoint X=8 Y=6 Z=0
    g6: LineSegment StartX=0 StartY=6 StartZ=0 EndX=8 EndY=6 EndZ=0
  constraints (14):
    c: Coincident(g0,g-1)
    c: Distance(g0) = 6
    c: Vertical(g0)
    c: Coincident(g3,g0)
    c: Weight(g1) = 1
    c: Equal(g1,g2)
    c: InternalAlignment(g1,g3)
    c: InternalAlignment(g2,g3)
    c: InternalAlignment(g4,g3)
    c: InternalAlignment(g5,g3)
    c: Block(g3)
    c: Coincident(g6,g0)
    c: Coincident(g6,g3)
    c: Horizontal(g6)
FEATURE [Part::Extrusion] Extrude030  label="caseScrewPillarBracket008"
  Base = -> Sketch039
  Dir = (0,0,1)
  DirMode = 2
  FaceMakerClass = Part::FaceMakerBullseye
  LengthFwd = 2.4
  LengthRev = 0
  Placement = pos=(15.76,29,8.8) rot=(0,1,0;0rad)
  Solid = true
  Symmetric = false
FEATURE [Part::Extrusion] Extrude031  label="caseScrewPillarBracket009"
  Base = -> Sketch040
  Dir = (0,0,1)
  DirMode = 2
  FaceMakerClass = Part::FaceMakerBullseye
  LengthFwd = 2.4
  LengthRev = 0
  Placement = pos=(15.76,29,60.8) rot=(0,0,1;0rad)
  Solid = true
  Symmetric = false
FEATURE [Part::Extrusion] Extrude032  label="caseScrewPillarBracket010"
  Base = -> Sketch041
  Dir = (0,0,1)
  DirMode = 2
  FaceMakerClass = Part::FaceMakerBullseye
  LengthFwd = 2.4
  LengthRev = 0
  Placement = pos=(13.7,29,13.26) rot=(0,-1,0;1.5708rad)
  Solid = true
  Symmetric = false
FEATURE [Part::Extrusion] Extrude033  label="caseScrewPillarBracket011"
  Base = -> Sketch042
  Dir = (0,0,1)
  DirMode = 2
  FaceMakerClass = Part::FaceMakerBullseye
  LengthFwd = 2.4
  LengthRev = 0
  Placement = pos=(11.3,29,58.74) rot=(0,1,0;1.5708rad)
  Solid = true
  Symmetric = false
FEATURE [Sketcher::SketchObject] Sketch043
  FullyConstrained = true
  sketch-geometry (7):
    g0: LineSegment StartX=0 StartY=0 StartZ=0 EndX=0 EndY=6 EndZ=0
    g1: Circle CenterX=0 CenterY=0 CenterZ=0 NormalX=0 NormalY=0 NormalZ=1 AngleXU=0 Radius=1
    g2: Circle CenterX=8 CenterY=6 CenterZ=0 NormalX=0 NormalY=0 NormalZ=1 AngleXU=0 Radius=1
    g3: BSplineCurve PolesCount=3 KnotsCount=2 Degree=2 IsPeriodic=0
    g4: GeomPoint X=0 Y=0 Z=0
    g5: GeomPoint X=8 Y=6 Z=0
    g6: LineSegment StartX=0 StartY=6 StartZ=0 EndX=8 EndY=6 EndZ=0
  constraints (14):
    c: Coincident(g0,g-1)
    c: Distance(g0) = 6
    c: Vertical(g0)
    c: Coincident(g3,g0)
    c: Weight(g1) = 1
    c: Equal(g1,g2)
    c: InternalAlignment(g1,g3)
    c: InternalAlignment(g2,g3)
    c: InternalAlignment(g4,g3)
    c: InternalAlignment(g5,g3)
    c: Block(g3)
    c: Coincident(g6,g0)
    c: Coincident(g6,g3)
    c: Horizontal(g6)
FEATURE [Part::Extrusion] Extrude034  label="caseScrewPillarBracket012"
  Base = -> Sketch043
  Dir = (0,0,1)
  DirMode = 2
  FaceMakerClass = Part::FaceMakerBullseye
  LengthFwd = 2.4
  LengthRev = 0
  Placement = pos=(88.3,29,65.23) rot=(0,1,0;1.5708rad)
  Solid = true
  Symmetric = false
FEATURE [Sketcher::SketchObject] Sketch044
  FullyConstrained = true
  sketch-geometry (7):
    g0: LineSegment StartX=0 StartY=0 StartZ=0 EndX=0 EndY=6 EndZ=0
    g1: Circle CenterX=0 CenterY=0 CenterZ=0 NormalX=0 NormalY=0 NormalZ=1 AngleXU=0 Radius=1
    g2: Circle CenterX=8 CenterY=6 CenterZ=0 NormalX=0 NormalY=0 NormalZ=1 AngleXU=0 Radius=1
    g3: BSplineCurve PolesCount=3 KnotsCount=2 Degree=2 IsPeriodic=0
    g4: GeomPoint X=0 Y=0 Z=0
    g5: GeomPoint X=8 Y=6 Z=0
    g6: LineSegment StartX=0 StartY=6 StartZ=0 EndX=8 EndY=6 EndZ=0
  constraints (14):
    c: Coincident(g0,g-1)
    c: Distance(g0) = 6
    c: Vertical(g0)
    c: Coincident(g3,g0)
    c: Weight(g1) = 1
    c: Equal(g1,g2)
    c: InternalAlignment(g1,g3)
    c: InternalAlignment(g2,g3)
    c: InternalAlignment(g4,g3)
    c: InternalAlignment(g5,g3)
    c: Block(g3)
    c: Coincident(g6,g0)
    c: Coincident(g6,g3)
    c: Horizontal(g6)
FEATURE [Part::Extrusion] Extrude035  label="caseScrewPillarBracket013"
  Base = -> Sketch044
  Dir = (0,0,1)
  DirMode = 2
  FaceMakerClass = Part::FaceMakerBullseye
  LengthFwd = 2.4
  LengthRev = 0
  Placement = pos=(90.7,29,6.77) rot=(0,-1,0;1.5708rad)
  Solid = true
  Symmetric = false
FEATURE [Sketcher::SketchObject] Sketch045
  FullyConstrained = true
  sketch-geometry (7):
    g0: LineSegment StartX=0 StartY=0 StartZ=0 EndX=0 EndY=6 EndZ=0
    g1: Circle CenterX=0 CenterY=0 CenterZ=0 NormalX=0 NormalY=0 NormalZ=1 AngleXU=0 Radius=1
    g2: Circle CenterX=8 CenterY=6 CenterZ=0 NormalX=0 NormalY=0 NormalZ=1 AngleXU=0 Radius=1
    g3: BSplineCurve PolesCount=3 KnotsCount=2 Degree=2 IsPeriodic=0
    g4: GeomPoint X=0 Y=0 Z=0
    g5: GeomPoint X=8 Y=6 Z=0
    g6: LineSegment StartX=0 StartY=6 StartZ=0 EndX=8 EndY=6 EndZ=0
  constraints (14):
    c: Coincident(g0,g-1)
    c: Distance(g0) = 6
    c: Vertical(g0)
    c: Coincident(g3,g0)
    c: Weight(g1) = 1
    c: Equal(g1,g2)
    c: InternalAlignment(g1,g3)
    c: InternalAlignment(g2,g3)
    c: InternalAlignment(g4,g3)
    c: InternalAlignment(g5,g3)
    c: Block(g3)
    c: Coincident(g6,g0)
    c: Coincident(g6,g3)
    c: Horizontal(g6)
FEATURE [Sketcher::SketchObject] Sketch046
  FullyConstrained = true
  sketch-geometry (7):
    g0: LineSegment StartX=0 StartY=0 StartZ=0 EndX=0 EndY=6 EndZ=0
    g1: Circle CenterX=0 CenterY=0 CenterZ=0 NormalX=0 NormalY=0 NormalZ=1 AngleXU=0 Radius=1
    g2: Circle CenterX=8 CenterY=6 CenterZ=0 NormalX=0 NormalY=0 NormalZ=1 AngleXU=0 Radius=1
    g3: BSplineCurve PolesCount=3 KnotsCount=2 Degree=2 IsPeriodic=0
    g4: GeomPoint X=0 Y=0 Z=0
    g5: GeomPoint X=8 Y=6 Z=0
    g6: LineSegment StartX=0 StartY=6 StartZ=0 EndX=8 EndY=6 EndZ=0
  constraints (14):
    c: Coincident(g0,g-1)
    c: Distance(g0) = 6
    c: Vertical(g0)
    c: Coincident(g3,g0)
    c: Weight(g1) = 1
    c: Equal(g1,g2)
    c: InternalAlignment(g1,g3)
    c: InternalAlignment(g2,g3)
    c: InternalAlignment(g4,g3)
    c: InternalAlignment(g5,g3)
    c: Block(g3)
    c: Coincident(g6,g0)
    c: Coincident(g6,g3)
    c: Horizontal(g6)
FEATURE [Part::Extrusion] Extrude036  label="caseScrewPillarBracket014"
  Base = -> Sketch045
  Dir = (0,0,1)
  DirMode = 2
  FaceMakerClass = Part::FaceMakerBullseye
  LengthFwd = 2.4
  LengthRev = 0
  Placement = pos=(110.7,29,6.77) rot=(0,-1,0;1.5708rad)
  Solid = true
  Symmetric = false
FEATURE [Part::Extrusion] Extrude037  label="caseScrewPillarBracket015"
  Base = -> Sketch046
  Dir = (0,0,1)
  DirMode = 2
  FaceMakerClass = Part::FaceMakerBullseye
  LengthFwd = 2.4
  LengthRev = 0
  Placement = pos=(108.3,29,65.23) rot=(0,1,0;1.5708rad)
  Solid = true
  Symmetric = false
FEATURE [Part::Box] Box013  label="frontCaseScrewPillarBracket002"
  AttacherType = Attacher::AttachEngine3D
  Height = 2.4
  Length = 22
  Placement = pos=(87,28,2.3) rot=(0,0,1;0rad)
  Width = 7
FEATURE [Part::Box] Box014  label="frontCaseScrewPillarBracket003"
  AttacherType = Attacher::AttachEngine3D
  Height = 2.4
  Length = 22
  Placement = pos=(87,28,67.3) rot=(0,0,1;0rad)
  Width = 7
FEATURE [Part::Feature] Face087
  shape: bbox 4.8 x 30.2 x 2e-07 mm, 1 faces, 0 solids (baked)
FEATURE [Part::Revolution] Revolve091  label="frontCaseScrewPost004"
  Angle = 360
  Axis = (0,1,0)
  Base = (0,0,0)
  FaceMakerClass = Part::FaceMakerBullseye
  Placement = pos=(89.5,4.5,3.5) rot=(0,0,1;0rad)
  Solid = false
  Source = -> Face087
  Symmetric = false
FEATURE [Part::Feature] Face088
  shape: bbox 4.8 x 30.2 x 2e-07 mm, 1 faces, 0 solids (baked)
FEATURE [Part::Revolution] Revolve092  label="frontCaseScrewPost005"
  Angle = 360
  Axis = (0,1,0)
  Base = (0,0,0)
  FaceMakerClass = Part::FaceMakerBullseye
  Placement = pos=(89.5,4.5,68.5) rot=(0,0,1;0rad)
  Solid = false
  Source = -> Face088
  Symmetric = false
FEATURE [Part::Feature] Face089
  shape: bbox 3.5 x 30.2 x 2e-07 mm, 1 faces, 0 solids (baked)
FEATURE [Part::Revolution] Revolve093  label="backCaseScrewPost002"
  Angle = 360
  Axis = (0,1,0)
  Base = (0,0,0)
  FaceMakerClass = Part::FaceMakerBullseye
  Placement = pos=(12.5,4.5,10) rot=(0,0,1;0rad)
  Solid = false
  Source = -> Face089
  Symmetric = false
FEATURE [Part::Feature] Face090
  shape: bbox 3.5 x 30.2 x 2e-07 mm, 1 faces, 0 solids (baked)
FEATURE [Part::Revolution] Revolve094  label="backCaseScrewPost003"
  Angle = 360
  Axis = (0,1,0)
  Base = (0,0,0)
  FaceMakerClass = Part::FaceMakerBullseye
  Placement = pos=(12.5,4.5,62) rot=(0,0,1;0rad)
  Solid = false
  Source = -> Face090
  Symmetric = false
FEATURE [Part::Box] Box015  label="Cube011"
  AttacherType = Attacher::AttachEngine3D
  Height = 28.8
  Length = 3
  Placement = pos=(107.3,28,21.6) rot=(0,0,1;0rad)
  Width = 7
FEATURE [Part::Box] Box016  label="Cube012"
  AttacherType = Attacher::AttachEngine3D
  Height = 3
  Length = 7.4
  Placement = pos=(107.3,28,18.6) rot=(0,0,1;0rad)
  Width = 7
FEATURE [Part::Box] Box017  label="Cube013"
  AttacherType = Attacher::AttachEngine3D
  Height = 3
  Length = 7.4
  Placement = pos=(107.3,28,50.4) rot=(0,0,1;0rad)
  Width = 7
FEATURE [Part::Cylinder] Cylinder024
  Angle = 360
  AttacherType = Attacher::AttachEngine3D
  Height = 20
  Placement = pos=(0,0,36.15) rot=(0,0,1;0rad)
  Radius = 14.3
FEATURE [Part::Cylinder] Cylinder025
  Angle = 360
  AttacherType = Attacher::AttachEngine3D
  Height = 10
  Placement = pos=(0,0,36.15) rot=(0,0,1;0rad)
  Radius = 4
FEATURE [Part::MultiFuse] Fusion066  label="removeToCreteHoleForPlugHousing009"
  Placement = pos=(70,19,36) rot=(0,1,0;1.5708rad)
  Shapes = -> [Cylinder024,Cylinder025]
FEATURE [Part::MultiFuse] Fusion065  label="plugHousingBracketHolder002"
  Shapes = -> [Box017,Box015,Box016]
FEATURE [Part::Cut] Cut025  label="plugHousingBracketHolder003"
  Base = -> Fusion065
  Placement = pos=(7,0,0) rot=(0,0,1;0rad)
  Tool = -> Fusion066
FEATURE [Sketcher::SketchObject] Sketch047
  FullyConstrained = false
  Placement = pos=(0,0,0) rot=(1,0,0;1.5708rad)
  sketch-geometry (24):
    g0: ArcOfCircle CenterX=-4 CenterY=-10.5 CenterZ=0 NormalX=0 NormalY=0 NormalZ=1 AngleXU=0 Radius=1.5 StartAngle=6e-16 EndAngle=3.14159
    g1: ArcOfCircle CenterX=-34.2 CenterY=-10.5 CenterZ=0 NormalX=0 NormalY=0 NormalZ=1 AngleXU=0 Radius=1.5 StartAngle=0 EndAngle=3.14159
    g2: ArcOfCircle CenterX=-34.2 CenterY=-27.7 CenterZ=0 NormalX=0 NormalY=0 NormalZ=1 AngleXU=0 Radius=1.5 StartAngle=3.14159 EndAngle=6.28319
    g3: ArcOfCircle CenterX=-4 CenterY=-27.7 CenterZ=0 NormalX=0 NormalY=0 NormalZ=1 AngleXU=0 Radius=1.5 StartAngle=3.1416 EndAngle=6.28319
    g4: ArcOfCircle CenterX=-10 CenterY=-4.3 CenterZ=0 NormalX=0 NormalY=0 NormalZ=1 AngleXU=0 Radius=1.5 StartAngle=2e-16 EndAngle=3.14159
    g5: ArcOfCircle CenterX=-16.1 CenterY=-1.8 CenterZ=0 NormalX=0 NormalY=0 NormalZ=1 AngleXU=0 Radius=1.5 StartAngle=5e-16 EndAngle=3.14159
    g6: ArcOfCircle CenterX=-22.1 CenterY=-1.8 CenterZ=0 NormalX=0 NormalY=0 NormalZ=1 AngleXU=0 Radius=1.5 StartAngle=5e-16 EndAngle=3.14159
    g7: ArcOfCircle CenterX=-28.2 CenterY=-4.3 CenterZ=0 NormalX=0 NormalY=0 NormalZ=1 AngleXU=0 Radius=1.5 StartAngle=2e-16 EndAngle=3.14159
    g8: ArcOfCircle CenterX=-10 CenterY=-33.9 CenterZ=0 NormalX=0 NormalY=0 NormalZ=1 AngleXU=0 Radius=1.5 StartAngle=3.14159 EndAngle=6.28319
    g9: ArcOfCircle CenterX=-16.1 CenterY=-36.4 CenterZ=0 NormalX=0 NormalY=0 NormalZ=1 AngleXU=0 Radius=1.5 StartAngle=3.14159 EndAngle=6.28319
    g10: ArcOfCircle CenterX=-22.1 CenterY=-36.4 CenterZ=0 NormalX=0 NormalY=0 NormalZ=1 AngleXU=0 Radius=1.5 StartAngle=3.14159 EndAngle=6.28319
    g11: ArcOfCircle CenterX=-28.2 CenterY=-33.9 CenterZ=0 NormalX=0 NormalY=0 NormalZ=1 AngleXU=0 Radius=1.5 StartAngle=3.14159 EndAngle=6.28319
    g12: LineSegment StartX=-35.7 StartY=-10.5 StartZ=0 EndX=-35.7 EndY=-27.7 EndZ=0
    g13: LineSegment StartX=-32.7 StartY=-10.5 StartZ=0 EndX=-32.7 EndY=-27.7 EndZ=0
    g14: LineSegment StartX=-29.7 StartY=-33.9 StartZ=0 EndX=-29.7 EndY=-4.3 EndZ=0
    g15: LineSegment StartX=-26.7 StartY=-33.9 StartZ=0 EndX=-26.7 EndY=-4.3 EndZ=0
    g16: LineSegment StartX=-2.5 StartY=-10.5 StartZ=0 EndX=-2.5 EndY=-27.7 EndZ=0
    g17: LineSegment StartX=-8.5 StartY=-4.3 StartZ=0 EndX=-8.5 EndY=-33.9 EndZ=0
    g18: LineSegment StartX=-5.5 StartY=-10.5 StartZ=0 EndX=-5.5 EndY=-27.7 EndZ=0
    g19: LineSegment StartX=-11.5 StartY=-4.3 StartZ=0 EndX=-11.5 EndY=-33.9 EndZ=0
    g20: LineSegment StartX=-14.6 StartY=-1.8 StartZ=0 EndX=-14.6 EndY=-36.4 EndZ=0
    g21: LineSegment StartX=-17.6 StartY=-1.8 StartZ=0 EndX=-17.6 EndY=-36.4 EndZ=0
    g22: LineSegment StartX=-20.6 StartY=-36.4 StartZ=0 EndX=-20.6 EndY=-1.8 EndZ=0
    g23: LineSegment StartX=-23.6 StartY=-1.8 StartZ=0 EndX=-23.6 EndY=-36.4 EndZ=0
  constraints (48):
    c: Block(g0)
    c: Block(g1)
    c: Block(g2)
    c: Block(g3)
    c: Block(g4)
    c: Block(g5)
    c: Block(g6)
    c: Block(g7)
    c: Block(g8)
    c: Block(g9)
    c: Block(g10)
    c: Block(g11)
    c: Coincident(g12,g1)
    c: Coincident(g12,g2)
    c: Vertical(g12)
    c: Coincident(g13,g1)
    c: Coincident(g13,g2)
    c: Vertical(g13)
    c: Coincident(g14,g11)
    c: Coincident(g14,g7)
    c: Vertical(g14)
    c: Coincident(g15,g11)
    c: Coincident(g15,g7)
    c: Vertical(g15)
    c: Coincident(g16,g0)
    c: Coincident(g16,g3)
    c: Vertical(g16)
    c: Coincident(g17,g4)
    c: Coincident(g17,g8)
    c: Vertical(g17)
    c: Coincident(g18,g0)
    c: Coincident(g18,g3)
    c: Vertical(g18)
    c: Coincident(g19,g4)
    c: Coincident(g19,g8)
    c: Vertical(g19)
    c: Coincident(g20,g5)
    c: Coincident(g20,g9)
    c: Vertical(g20)
    c: Coincident(g21,g5)
    c: Coincident(g21,g9)
    c: Vertical(g21)
    c: Coincident(g22,g10)
    c: Coincident(g22,g6)
    c: Vertical(g22)
    c: Coincident(g23,g6)
    c: Coincident(g23,g10)
    c: Vertical(g23)
FEATURE [Part::Extrusion] Extrude038  label="removeToCreateFanGrillHoles001"
  Base = -> Sketch047
  Dir = (0,-1,6e-16)
  DirMode = 2
  FaceMakerClass = Part::FaceMakerBullseye
  LengthFwd = 10
  LengthRev = 0
  Placement = pos=(65.4,44,54.82) rot=(0,0,1;0rad)
  Solid = true
  Symmetric = false
FEATURE [Part::Feature] Wire004
  shape: bbox 11 x 5.2 x 2e-07 mm, 0 faces, 0 solids (baked)
FEATURE [Part::Revolution] Revolve095
  Angle = 360
  Axis = (0,1,0)
  Base = (0,0,0)
  FaceMakerClass = Part::FaceMakerBullseye
  Placement = pos=(30.3,38,19.7) rot=(0,0,1;0rad)
  Solid = true
  Source = -> Wire004
  Symmetric = false
FEATURE [Part::Feature] Wire005
  shape: bbox 11 x 5.2 x 2e-07 mm, 0 faces, 0 solids (baked)
FEATURE [Part::Revolution] Revolve096
  Angle = 360
  Axis = (0,1,0)
  Base = (0,0,0)
  FaceMakerClass = Part::FaceMakerBullseye
  Placement = pos=(30.3,38,51.7) rot=(0,0,1;0rad)
  Solid = true
  Source = -> Wire005
  Symmetric = false
FEATURE [Part::Feature] Wire006
  shape: bbox 11 x 5.2 x 2e-07 mm, 0 faces, 0 solids (baked)
FEATURE [Part::Revolution] Revolve097
  Angle = 360
  Axis = (0,1,0)
  Base = (0,0,0)
  FaceMakerClass = Part::FaceMakerBullseye
  Placement = pos=(62.3,38,51.7) rot=(0,0,1;0rad)
  Solid = true
  Source = -> Wire006
  Symmetric = false
FEATURE [Part::Feature] Wire007
  shape: bbox 11 x 5.2 x 2e-07 mm, 0 faces, 0 solids (baked)
FEATURE [Part::Revolution] Revolve098
  Angle = 360
  Axis = (0,1,0)
  Base = (0,0,0)
  FaceMakerClass = Part::FaceMakerBullseye
  Placement = pos=(62.3,38,19.7) rot=(0,0,1;0rad)
  Solid = true
  Source = -> Wire007
  Symmetric = false
FEATURE [Part::MultiFuse] Fusion067  label="fanScrewHousing002"
  Shapes = -> [Revolve098,Revolve097,Revolve096,Revolve095]
FEATURE [Part::Feature] Face091 .. Face094  x4 (patterned run collapsed; names and placements below)
  shape: bbox 3.5 x 17.8 x 2e-07 mm, 1 faces, 0 solids (baked)
FEATURE [Part::Revolution] Revolve099  label="removeToCreateScrewAndThreadedInsertHole026"
  Angle = 360
  Axis = (0,1,0)
  Base = (0,0,0)
  FaceMakerClass = Part::FaceMakerBullseye
  Placement = pos=(62.3,30.3,19.7) rot=(0,0,1;0rad)
  Solid = false
  Source = -> Face091
  Symmetric = false
FEATURE [Part::Revolution] Revolve100  label="removeToCreateScrewAndThreadedInsertHole027"
  Angle = 360
  Axis = (0,1,0)
  Base = (0,0,0)
  FaceMakerClass = Part::FaceMakerBullseye
  Placement = pos=(62.3,30.3,51.7) rot=(0,0,1;0rad)
  Solid = false
  Source = -> Face092
  Symmetric = false
FEATURE [Part::Revolution] Revolve101  label="removeToCreateScrewAndThreadedInsertHole028"
  Angle = 360
  Axis = (0,1,0)
  Base = (0,0,0)
  FaceMakerClass = Part::FaceMakerBullseye
  Placement = pos=(30.3,30.3,19.7) rot=(0,0,1;0rad)
  Solid = false
  Source = -> Face093
  Symmetric = false
FEATURE [Part::Revolution] Revolve102  label="removeToCreateScrewAndThreadedInsertHole029"
  Angle = 360
  Axis = (0,1,0)
  Base = (0,0,0)
  FaceMakerClass = Part::FaceMakerBullseye
  Placement = pos=(30.3,30.3,51.7) rot=(0,0,1;0rad)
  Solid = false
  Source = -> Face094
  Symmetric = false
FEATURE [Part::MultiFuse] Fusion068  label="createThreadedInsertHolesForFan002"
  Shapes = -> [Revolve099,Revolve100,Revolve101,Revolve102]
FEATURE [Part::Cut] Cut026  label="fanScrewHousing003"
  Base = -> Fusion067
  Tool = -> Fusion068
FEATURE [Sketcher::SketchObject] Sketch048
  FullyConstrained = false
  Placement = pos=(0,0,0) rot=(1,0,0;1.5708rad)
  sketch-geometry (24):
    g0: ArcOfCircle CenterX=-4 CenterY=-10.5 CenterZ=0 NormalX=0 NormalY=0 NormalZ=1 AngleXU=0 Radius=1.5 StartAngle=6e-16 EndAngle=3.14159
    g1: ArcOfCircle CenterX=-34.2 CenterY=-10.5 CenterZ=0 NormalX=0 NormalY=0 NormalZ=1 AngleXU=0 Radius=1.5 StartAngle=0 EndAngle=3.14159
    g2: ArcOfCircle CenterX=-34.2 CenterY=-27.7 CenterZ=0 NormalX=0 NormalY=0 NormalZ=1 AngleXU=0 Radius=1.5 StartAngle=3.14159 EndAngle=6.28319
    g3: ArcOfCircle CenterX=-4 CenterY=-27.7 CenterZ=0 NormalX=0 NormalY=0 NormalZ=1 AngleXU=0 Radius=1.5 StartAngle=3.1416 EndAngle=6.28319
    g4: ArcOfCircle CenterX=-10 CenterY=-4.3 CenterZ=0 NormalX=0 NormalY=0 NormalZ=1 AngleXU=0 Radius=1.5 StartAngle=2e-16 EndAngle=3.14159
    g5: ArcOfCircle CenterX=-16.1 CenterY=-1.8 CenterZ=0 NormalX=0 NormalY=0 NormalZ=1 AngleXU=0 Radius=1.5 StartAngle=5e-16 EndAngle=3.14159
    g6: ArcOfCircle CenterX=-22.1 CenterY=-1.8 CenterZ=0 NormalX=0 NormalY=0 NormalZ=1 AngleXU=0 Radius=1.5 StartAngle=5e-16 EndAngle=3.14159
    g7: ArcOfCircle CenterX=-28.2 CenterY=-4.3 CenterZ=0 NormalX=0 NormalY=0 NormalZ=1 AngleXU=0 Radius=1.5 StartAngle=2e-16 EndAngle=3.14159
    g8: ArcOfCircle CenterX=-10 CenterY=-33.9 CenterZ=0 NormalX=0 NormalY=0 NormalZ=1 AngleXU=0 Radius=1.5 StartAngle=3.14159 EndAngle=6.28319
    g9: ArcOfCircle CenterX=-16.1 CenterY=-36.4 CenterZ=0 NormalX=0 NormalY=0 NormalZ=1 AngleXU=0 Radius=1.5 StartAngle=3.14159 EndAngle=6.28319
    g10: ArcOfCircle CenterX=-22.1 CenterY=-36.4 CenterZ=0 NormalX=0 NormalY=0 NormalZ=1 AngleXU=0 Radius=1.5 StartAngle=3.14159 EndAngle=6.28319
    g11: ArcOfCircle CenterX=-28.2 CenterY=-33.9 CenterZ=0 NormalX=0 NormalY=0 NormalZ=1 AngleXU=0 Radius=1.5 StartAngle=3.14159 EndAngle=6.28319
    g12: LineSegment StartX=-35.7 StartY=-10.5 StartZ=0 EndX=-35.7 EndY=-27.7 EndZ=0
    g13: LineSegment StartX=-32.7 StartY=-10.5 StartZ=0 EndX=-32.7 EndY=-27.7 EndZ=0
    g14: LineSegment StartX=-29.7 StartY=-33.9 StartZ=0 EndX=-29.7 EndY=-4.3 EndZ=0
    g15: LineSegment StartX=-26.7 StartY=-33.9 StartZ=0 EndX=-26.7 EndY=-4.3 EndZ=0
    g16: LineSegment StartX=-2.5 StartY=-10.5 StartZ=0 EndX=-2.5 EndY=-27.7 EndZ=0
    g17: LineSegment StartX=-8.5 StartY=-4.3 StartZ=0 EndX=-8.5 EndY=-33.9 EndZ=0
    g18: LineSegment StartX=-5.5 StartY=-10.5 StartZ=0 EndX=-5.5 EndY=-27.7 EndZ=0
    g19: LineSegment StartX=-11.5 StartY=-4.3 StartZ=0 EndX=-11.5 EndY=-33.9 EndZ=0
    g20: LineSegment StartX=-14.6 StartY=-1.8 StartZ=0 EndX=-14.6 EndY=-36.4 EndZ=0
    g21: LineSegment StartX=-17.6 StartY=-1.8 StartZ=0 EndX=-17.6 EndY=-36.4 EndZ=0
    g22: LineSegment StartX=-20.6 StartY=-36.4 StartZ=0 EndX=-20.6 EndY=-1.8 EndZ=0
    g23: LineSegment StartX=-23.6 StartY=-1.8 StartZ=0 EndX=-23.6 EndY=-36.4 EndZ=0
  constraints (48):
    c: Block(g0)
    c: Block(g1)
    c: Block(g2)
    c: Block(g3)
    c: Block(g4)
    c: Block(g5)
    c: Block(g6)
    c: Block(g7)
    c: Block(g8)
    c: Block(g9)
    c: Block(g10)
    c: Block(g11)
    c: Coincident(g12,g1)
    c: Coincident(g12,g2)
    c: Vertical(g12)
    c: Coincident(g13,g1)
    c: Coincident(g13,g2)
    c: Vertical(g13)
    c: Coincident(g14,g11)
    c: Coincident(g14,g7)
    c: Vertical(g14)
    c: Coincident(g15,g11)
    c: Coincident(g15,g7)
    c: Vertical(g15)
    c: Coincident(g16,g0)
    c: Coincident(g16,g3)
    c: Vertical(g16)
    c: Coincident(g17,g4)
    c: Coincident(g17,g8)
    c: Vertical(g17)
    c: Coincident(g18,g0)
    c: Coincident(g18,g3)
    c: Vertical(g18)
    c: Coincident(g19,g4)
    c: Coincident(g19,g8)
    c: Vertical(g19)
    c: Coincident(g20,g5)
    c: Coincident(g20,g9)
    c: Vertical(g20)
    c: Coincident(g21,g5)
    c: Coincident(g21,g9)
    c: Vertical(g21)
    c: Coincident(g22,g10)
    c: Coincident(g22,g6)
    c: Vertical(g22)
    c: Coincident(g23,g6)
    c: Coincident(g23,g10)
    c: Vertical(g23)
FEATURE [Part::Extrusion] Extrude039  label="removeToCreateFanGrillHoles002"
  Base = -> Sketch048
  Dir = (0,-1,6e-16)
  DirMode = 2
  FaceMakerClass = Part::FaceMakerBullseye
  LengthFwd = 10
  LengthRev = 0
  Placement = pos=(65.4,44,54.82) rot=(0,0,1;0rad)
  Solid = true
  Symmetric = false
FEATURE [Part::Cut] Cut027  label="fanScrewHousing004"
  Base = -> Cut026
  Tool = -> Extrude038
FEATURE [Part::Cut] Cut028  label="top014"
  Base = -> Fillet026
  Tool = -> Extrude039
FEATURE [Part::Feature] Face095 .. Face098  x4 (patterned run collapsed; names and placements below)
  shape: bbox 3.5 x 17.8 x 2e-07 mm, 1 faces, 0 solids (baked)
FEATURE [Part::Revolution] Revolve103  label="removeToCreateScrewAndThreadedInsertHole030"
  Angle = 360
  Axis = (0,1,0)
  Base = (0,0,0)
  FaceMakerClass = Part::FaceMakerBullseye
  Placement = pos=(62.3,30.3,19.7) rot=(0,0,1;0rad)
  Solid = false
  Source = -> Face095
  Symmetric = false
FEATURE [Part::Revolution] Revolve104  label="removeToCreateScrewAndThreadedInsertHole031"
  Angle = 360
  Axis = (0,1,0)
  Base = (0,0,0)
  FaceMakerClass = Part::FaceMakerBullseye
  Placement = pos=(62.3,30.3,51.7) rot=(0,0,1;0rad)
  Solid = false
  Source = -> Face096
  Symmetric = false
FEATURE [Part::Revolution] Revolve105  label="removeToCreateScrewAndThreadedInsertHole032"
  Angle = 360
  Axis = (0,1,0)
  Base = (0,0,0)
  FaceMakerClass = Part::FaceMakerBullseye
  Placement = pos=(30.3,30.3,19.7) rot=(0,0,1;0rad)
  Solid = false
  Source = -> Face097
  Symmetric = false
FEATURE [Part::Revolution] Revolve106  label="removeToCreateScrewAndThreadedInsertHole033"
  Angle = 360
  Axis = (0,1,0)
  Base = (0,0,0)
  FaceMakerClass = Part::FaceMakerBullseye
  Placement = pos=(30.3,30.3,51.7) rot=(0,0,1;0rad)
  Solid = false
  Source = -> Face098
  Symmetric = false
FEATURE [Part::MultiFuse] Fusion069  label="createThreadedInsertHolesForFan003"
  Shapes = -> [Revolve103,Revolve104,Revolve105,Revolve106]
FEATURE [Part::Cut] Cut029  label="top015"
  Base = -> Cut028
  Tool = -> Fusion054
FEATURE [Part::Cut] Cut030  label="fanScrewHousing005"
  Base = -> Cut027
  Tool = -> Fusion069
FEATURE [Part::Cylinder] Cylinder026  label="removeToCreteHoleForPlugHousing010"
  Angle = 360
  AttacherType = Attacher::AttachEngine3D
  Height = 20
  Placement = pos=(-2,19,36) rot=(0,1,0;1.5708rad)
  Radius = 14.3
FEATURE [Part::Box] Box018  label="removeToCreteHoleForPlugHousing011"
  AttacherType = Attacher::AttachEngine3D
  Height = 28.6
  Length = 10
  Placement = pos=(-2,0,21.7) rot=(0,0,1;0rad)
  Width = 19
FEATURE [Part::Box] Box019  label="wireHolderBottomCaseBit"
  AttacherType = Attacher::AttachEngine3D
  Height = 28
  Length = 3
  Placement = pos=(0,0,22) rot=(0,0,1;0rad)
  Width = 21
FEATURE [Part::Cylinder] Cylinder027  label="removeToCreteHoleForPlugHousing012"
  Angle = 360
  AttacherType = Attacher::AttachEngine3D
  Height = 20
  Placement = pos=(-2,19,36) rot=(0,1,0;1.5708rad)
  Radius = 14.3
FEATURE [Part::Cut] Cut031  label="wireHolderBottomCaseBit001"
  Base = -> Box019
  Tool = -> Cylinder027
FEATURE [Part::MultiFuse] Fusion070  label="removeToCreteHoleForPlugHousing013"
  Shapes = -> [Box018,Cylinder026]
FEATURE [Part::Cut] Cut032  label="top016"
  Base = -> Cut029
  Tool = -> Fusion070
FEATURE [Part::Cylinder] Cylinder028
  Angle = 360
  AttacherType = Attacher::AttachEngine3D
  Height = 20
  Placement = pos=(0,0,36.15) rot=(0,0,1;0rad)
  Radius = 14.3
FEATURE [Part::Cylinder] Cylinder029
  Angle = 360
  AttacherType = Attacher::AttachEngine3D
  Height = 10
  Placement = pos=(0,0,36.15) rot=(0,0,1;0rad)
  Radius = 4
FEATURE [Part::MultiFuse] Fusion071  label="removeToCreteHoleForPlugHousing014"
  Placement = pos=(70,19,36) rot=(0,1,0;1.5708rad)
  Shapes = -> [Cylinder028,Cylinder029]
FEATURE [Sketcher::SketchObject] Sketch049  label="topSketch011"
  FullyConstrained = true
  sketch-geometry (4):
    g0: ArcOfCircle CenterX=105 CenterY=19 CenterZ=0 NormalX=0 NormalY=0 NormalZ=1 AngleXU=0 Radius=20.6155 StartAngle=5.54125 EndAngle=6.28319
    g1: ArcOfCircle CenterX=105 CenterY=19 CenterZ=0 NormalX=0 NormalY=0 NormalZ=1 AngleXU=0 Radius=13 StartAngle=5.54125 EndAngle=6.28319
    g2: LineSegment StartX=118 StartY=19 StartZ=0 EndX=125.616 EndY=19 EndZ=0
    g3: LineSegment StartX=114.583 StartY=10.2157 StartZ=0 EndX=120.197 EndY=5.06982 EndZ=0
  constraints (7):
    c: Block(g0)
    c: Block(g1)
    c: Coincident(g2,g1)
    c: Coincident(g2,g0)
    c: Horizontal(g2)
    c: Coincident(g3,g1)
    c: Coincident(g3,g0)
FEATURE [Part::Box] Box020  label="removeToCreteHoleForPlugHousing015"
  AttacherType = Attacher::AttachEngine3D
  Height = 28.6
  Length = 20
  Placement = pos=(106.15,0,21.7) rot=(0,0,1;0rad)
  Width = 19
FEATURE [Part::MultiFuse] Fusion072  label="removeToCreteHoleForPlugHousing016"
  Shapes = -> [Box020,Fusion071]
FEATURE [Part::Cut] Cut033  label="removeToCreteHoleForPlugHousing017"
  Base = -> Cut032
  Tool = -> Fusion072
FEATURE [Part::Cylinder] Cylinder030
  Angle = 360
  AttacherType = Attacher::AttachEngine3D
  Height = 20
  Placement = pos=(0,0,36.15) rot=(0,0,1;0rad)
  Radius = 14.3
FEATURE [Part::Cylinder] Cylinder031
  Angle = 360
  AttacherType = Attacher::AttachEngine3D
  Height = 10
  Placement = pos=(0,0,36.15) rot=(0,0,1;0rad)
  Radius = 4
FEATURE [Part::Box] Box021  label="removeToCreteHoleForPlugHousing019"
  AttacherType = Attacher::AttachEngine3D
  Height = 28.6
  Length = 20
  Placement = pos=(106.15,0,21.7) rot=(0,0,1;0rad)
  Width = 19
FEATURE [Part::MultiFuse] Fusion074  label="removeToCreteHoleForPlugHousing020"
  Placement = pos=(70,19,36) rot=(0,1,0;1.5708rad)
  Shapes = -> [Cylinder030,Cylinder031]
FEATURE [Part::MultiFuse] Fusion073  label="removeToCreteHoleForPlugHousing018"
  Placement = pos=(0,0,28.3) rot=(0,0,1;0rad)
  Shapes = -> [Box021,Fusion074]
FEATURE [Part::Cylinder] Cylinder032
  Angle = 360
  AttacherType = Attacher::AttachEngine3D
  Height = 20
  Placement = pos=(0,0,36.15) rot=(0,0,1;0rad)
  Radius = 14.3
FEATURE [Part::Cylinder] Cylinder033
  Angle = 360
  AttacherType = Attacher::AttachEngine3D
  Height = 10
  Placement = pos=(0,0,36.15) rot=(0,0,1;0rad)
  Radius = 4
FEATURE [Part::Box] Box022  label="removeToCreteHoleForPlugHousing021"
  AttacherType = Attacher::AttachEngine3D
  Height = 28.6
  Length = 20
  Placement = pos=(106.15,0,21.7) rot=(0,0,1;0rad)
  Width = 19
FEATURE [Part::MultiFuse] Fusion076  label="removeToCreteHoleForPlugHousing023"
  Placement = pos=(70,19,36) rot=(0,1,0;1.5708rad)
  Shapes = -> [Cylinder032,Cylinder033]
FEATURE [Part::MultiFuse] Fusion075  label="removeToCreteHoleForPlugHousing022"
  Placement = pos=(0,0,-28.3) rot=(0,0,1;0rad)
  Shapes = -> [Box022,Fusion076]
FEATURE [Part::MultiFuse] Fusion077  label="removeToCreatePlugHousingBottomBit"
  Shapes = -> [Fusion075,Fusion073]
FEATURE [Part::Cylinder] Cylinder034
  Angle = 360
  AttacherType = Attacher::AttachEngine3D
  Height = 20
  Placement = pos=(0,0,36.15) rot=(0,0,1;0rad)
  Radius = 14
FEATURE [Part::Cylinder] Cylinder035
  Angle = 360
  AttacherType = Attacher::AttachEngine3D
  Height = 10
  Placement = pos=(0,0,36.15) rot=(0,0,1;0rad)
  Radius = 4
FEATURE [Part::MultiFuse] Fusion078  label="removeToCreteHoleForPlugHousing024"
  Placement = pos=(70,19,36) rot=(0,1,0;1.5708rad)
  Shapes = -> [Cylinder034,Cylinder035]
FEATURE [Part::MultiFuse] Fusion079  label="removeToCreatePlugHousingBottomBit001"
  Shapes = -> [Fusion078,Fusion077]
FEATURE [Part::Extrusion] Extrude040  label="bottomPlugHousingBit"
  Base = -> Sketch049
  Dir = (0,0,1)
  DirMode = 2
  FaceMakerClass = Part::FaceMakerBullseye
  LengthFwd = 72
  LengthRev = 0
  Solid = true
  Symmetric = false
FEATURE [Part::Cut] Cut034  label="bottomPlugHousingBit001"
  Base = -> Extrude040
  Placement = pos=(-0.09,0,0) rot=(0,0,1;0rad)
  Tool = -> Fusion079
FEATURE [Part::Box] Box023  label="Cube014"
  AttacherType = Attacher::AttachEngine3D
  Height = 16
  Length = 8
  Placement = pos=(12.7,31.52,28) rot=(0,0,1;0rad)
  Width = 4
FEATURE [Part::Cylinder] Cylinder036
  Angle = 360
  AttacherType = Attacher::AttachEngine3D
  Height = 10
  Placement = pos=(0,0,36.15) rot=(0,0,1;0rad)
  Radius = 4
FEATURE [Part::Cylinder] Cylinder037
  Angle = 360
  AttacherType = Attacher::AttachEngine3D
  Height = 20
  Placement = pos=(0,0,36.15) rot=(0,0,1;0rad)
  Radius = 8.2
FEATURE [Part::MultiFuse] Fusion080  label="removeToCreteHoleForPlugHousing025"
  Placement = pos=(-42,19,36) rot=(0,1,0;1.5708rad)
  Shapes = -> [Cylinder037,Cylinder036]
FEATURE [Sketcher::SketchObject] Sketch050  label="topSketch012"
  FullyConstrained = true
  sketch-geometry (4):
    g0: LineSegment StartX=16.8446 StartY=31.512 StartZ=0 EndX=16.3251 EndY=34.4666 EndZ=0
    g1: ArcOfCircle CenterX=19 CenterY=19.2524 CenterZ=0 NormalX=0 NormalY=0 NormalZ=1 AngleXU=0 Radius=15.4476 StartAngle=1.74483 EndAngle=2.72717
    g2: ArcOfCircle CenterX=19 CenterY=19.2524 CenterZ=0 NormalX=0 NormalY=0 NormalZ=1 AngleXU=0 Radius=12.4476 StartAngle=1.74483 EndAngle=2.73189
    g3: LineSegment StartX=4.86004 StartY=25.4725 StartZ=0 EndX=7.58253 EndY=24.2107 EndZ=0
  constraints (7):
    c: Block(g0)
    c: Coincident(g1,g0)
    c: Coincident(g2,g0)
    c: Coincident(g3,g1)
    c: Coincident(g3,g2)
    c: Block(g1)
    c: Block(g2)
FEATURE [Part::Extrusion] Extrude041
  Base = -> Sketch050
  Dir = (0,0,1)
  DirMode = 2
  FaceMakerClass = Part::FaceMakerBullseye
  LengthFwd = 10.6
  LengthRev = 0
  Placement = pos=(0,0,31) rot=(0,0,1;0rad)
  Solid = true
  Symmetric = false
FEATURE [Part::Cut] Cut035
  Base = -> Extrude041
  Placement = pos=(0,0,-0.3) rot=(0,0,1;0rad)
  Tool = -> Fusion080
FEATURE [Part::Cut] Cut036
  Base = -> Box023
  Tool = -> Cut035
FEATURE [Part::Fillet] Fillet027
  Base = -> Cut036
  Edges = 1 edges r=0.7: [Edge13]
FEATURE [Part::Fillet] Fillet028
  Base = -> Fillet027
  Edges = 1 edges r=0.7: [Edge13]
FEATURE [Part::Fillet] Fillet029
  Base = -> Fillet028
  Edges = 1 edges r=0.7: [Edge16]
FEATURE [Part::Fillet] Fillet030
  Base = -> Fillet029
  Edges = 1 edges r=0.7: [Edge11]
FEATURE [Part::Fillet] Fillet031
  Base = -> Fillet030
  Edges = 1 edges r=0.7: [Edge10]
FEATURE [Part::Fillet] Fillet032
  Base = -> Fillet031
  Edges = 1 edges r=1.2: [Edge5]
FEATURE [Part::Fillet] Fillet033
  Base = -> Fillet032
  Edges = 1 edges r=1.2: [Edge12]
FEATURE [Part::Fillet] Fillet034  label="wireHousingRetainer"
  Base = -> Fillet033
  Edges = 1 edges r=2: [Edge1]
  Placement = pos=(0.3,0,0) rot=(0,0,1;0rad)
FEATURE [Part::Feature] Face099
  shape: bbox 3.5 x 17.8 x 2e-07 mm, 1 faces, 0 solids (baked)
FEATURE [Part::Revolution] Revolve107  label="removeToCreateScrewAndThreadedInsertHole034"
  Angle = 360
  Axis = (0,1,0)
  Base = (0,0,0)
  FaceMakerClass = Part::FaceMakerBullseye
  Placement = pos=(12.5,0,10) rot=(0,0,1;0rad)
  Solid = false
  Source = -> Face099
  Symmetric = false
FEATURE [Part::Feature] Face100
  shape: bbox 3.5 x 17.8 x 2e-07 mm, 1 faces, 0 solids (baked)
FEATURE [Part::Revolution] Revolve108  label="removeToCreateScrewAndThreadedInsertHole035"
  Angle = 360
  Axis = (0,1,0)
  Base = (0,0,0)
  FaceMakerClass = Part::FaceMakerBullseye
  Placement = pos=(12.5,0,62) rot=(0,0,1;0rad)
  Solid = false
  Source = -> Face100
  Symmetric = false
FEATURE [Part::Feature] Face101
  shape: bbox 3.5 x 17.8 x 2e-07 mm, 1 faces, 0 solids (baked)
FEATURE [Part::Revolution] Revolve109  label="removeToCreateScrewAndThreadedInsertHole036"
  Angle = 360
  Axis = (0,1,0)
  Base = (0,0,0)
  FaceMakerClass = Part::FaceMakerBullseye
  Placement = pos=(89.5,0,68.5) rot=(0,0,1;0rad)
  Solid = false
  Source = -> Face101
  Symmetric = false
FEATURE [Part::Feature] Face102
  shape: bbox 3.5 x 17.8 x 2e-07 mm, 1 faces, 0 solids (baked)
FEATURE [Part::Revolution] Revolve110  label="removeToCreateScrewAndThreadedInsertHole037"
  Angle = 360
  Axis = (0,1,0)
  Base = (0,0,0)
  FaceMakerClass = Part::FaceMakerBullseye
  Placement = pos=(89.5,0,3.5) rot=(0,0,1;0rad)
  Solid = false
  Source = -> Face102
  Symmetric = false
FEATURE [Part::Feature] Face103
  shape: bbox 3.5 x 17.8 x 2e-07 mm, 1 faces, 0 solids (baked)
FEATURE [Part::Revolution] Revolve111  label="removeToCreateScrewAndThreadedInsertHole038"
  Angle = 360
  Axis = (0,1,0)
  Base = (0,0,0)
  FaceMakerClass = Part::FaceMakerBullseye
  Placement = pos=(109.5,4.7,3.5) rot=(0,0,1;0rad)
  Solid = false
  Source = -> Face103
  Symmetric = false
FEATURE [Part::Feature] Face104
  shape: bbox 3.5 x 17.8 x 2e-07 mm, 1 faces, 0 solids (baked)
FEATURE [Part::Revolution] Revolve112  label="removeToCreateScrewAndThreadedInsertHole039"
  Angle = 360
  Axis = (0,1,0)
  Base = (0,0,0)
  FaceMakerClass = Part::FaceMakerBullseye
  Placement = pos=(109.5,4.7,68.5) rot=(0,0,1;0rad)
  Solid = false
  Source = -> Face104
  Symmetric = false
FEATURE [Part::MultiFuse] Fusion081  label="removeToCreateScrewAndThreadedInsertHole040"
  Shapes = -> [Revolve107,Revolve108,Revolve109,Revolve110,Revolve111,Revolve112]
FEATURE [Part::MultiFuse] Fusion082  label="casePillars002"
  Shapes = -> [Revolve094,Revolve092,Revolve090,Revolve089,Revolve091,Revolve093]
FEATURE [Part::Cut] Cut037  label="casePillars003"
  Base = -> Fusion082
  Tool = -> Fusion081
FEATURE [Sketcher::SketchObject] Sketch051
  FullyConstrained = true
  Placement = pos=(117,19,0) rot=(0.57735,0.57735,0.57735;2.0944rad)
  sketch-geometry (48):
    g0: LineSegment StartX=-49.19 StartY=69.25 StartZ=0 EndX=-49.19 EndY=66.25 EndZ=0
    g1: LineSegment StartX=-49.19 StartY=63.5 StartZ=0 EndX=-49.19 EndY=60.5 EndZ=0
    g2: LineSegment StartX=-49.19 StartY=57.75 StartZ=0 EndX=-49.19 EndY=54.75 EndZ=0
    g3: LineSegment StartX=-49.19 StartY=52 StartZ=0 EndX=-49.19 EndY=49 EndZ=0
    g4: LineSegment StartX=-49.19 StartY=46.25 StartZ=0 EndX=-49.19 EndY=43.25 EndZ=0
    g5: LineSegment StartX=-49.19 StartY=40.5 StartZ=0 EndX=-49.19 EndY=37.5 EndZ=0
    g6: LineSegment StartX=-49.19 StartY=34.5 StartZ=0 EndX=-49.19 EndY=31.5 EndZ=0
    g7: LineSegment StartX=-49.19 StartY=28.75 StartZ=0 EndX=-49.19 EndY=25.75 EndZ=0
    g8: LineSegment StartX=-49.19 StartY=23 StartZ=0 EndX=-49.19 EndY=20 EndZ=0
    g9: LineSegment StartX=-49.19 StartY=17.25 StartZ=0 EndX=-49.19 EndY=14.25 EndZ=0
    g10: LineSegment StartX=-49.19 StartY=11.5 StartZ=0 EndX=-49.19 EndY=8.5 EndZ=0
    g11: LineSegment StartX=-49.19 StartY=5.75 StartZ=0 EndX=-49.19 EndY=2.75 EndZ=0
    g12: ArcOfCircle CenterX=-1.5 CenterY=67.75 CenterZ=0 NormalX=0 NormalY=0 NormalZ=1 AngleXU=0 Radius=1.5 StartAngle=4.71239 EndAngle=7.85398
    g13: ArcOfCircle CenterX=-1.5 CenterY=62 CenterZ=0 NormalX=0 NormalY=0 NormalZ=1 AngleXU=0 Radius=1.5 StartAngle=4.71239 EndAngle=7.85398
    g14: ArcOfCircle CenterX=-1.5 CenterY=56.25 CenterZ=0 NormalX=0 NormalY=0 NormalZ=1 AngleXU=0 Radius=1.5 StartAngle=4.71239 EndAngle=7.85398
    g15: ArcOfCircle CenterX=-11.49 CenterY=50.5 CenterZ=0 NormalX=0 NormalY=0 NormalZ=1 AngleXU=0 Radius=1.5 StartAngle=4.71239 EndAngle=7.85398
    g16: ArcOfCircle CenterX=-16.28 CenterY=44.75 CenterZ=0 NormalX=0 NormalY=0 NormalZ=1 AngleXU=0 Radius=1.5 StartAngle=4.71239 EndAngle=7.85398
    g17: ArcOfCircle CenterX=-18.2337 CenterY=39 CenterZ=0 NormalX=0 NormalY=0 NormalZ=1 AngleXU=0 Radius=1.5 StartAngle=4.71485 EndAngle=7.85398
    g18: ArcOfCircle CenterX=-16.2837 CenterY=27.25 CenterZ=0 NormalX=0 NormalY=0 NormalZ=1 AngleXU=0 Radius=1.5 StartAngle=4.71485 EndAngle=7.85398
    g19: ArcOfCircle CenterX=-18.2337 CenterY=33 CenterZ=0 NormalX=0 NormalY=0 NormalZ=1 AngleXU=0 Radius=1.5 StartAngle=4.71485 EndAngle=7.85398
    g20: ArcOfCircle CenterX=-11.49 CenterY=21.5 CenterZ=0 NormalX=0 NormalY=0 NormalZ=1 AngleXU=0 Radius=1.5 StartAngle=4.71239 EndAngle=7.85398
    g21: ArcOfCircle CenterX=-1.5 CenterY=4.25 CenterZ=0 NormalX=0 NormalY=0 NormalZ=1 AngleXU=0 Radius=1.5 StartAngle=4.71239 EndAngle=7.85398
    g22: ArcOfCircle CenterX=-1.5 CenterY=10 CenterZ=0 NormalX=0 NormalY=0 NormalZ=1 AngleXU=0 Radius=1.5 StartAngle=4.71239 EndAngle=7.85398
    g23: ArcOfCircle CenterX=-1.5 CenterY=15.75 CenterZ=0 NormalX=0 NormalY=0 NormalZ=1 AngleXU=0 Radius=1.5 StartAngle=4.71239 EndAngle=7.85398
    g24: LineSegment StartX=-49.19 StartY=69.25 StartZ=0 EndX=-1.5 EndY=69.25 EndZ=0
    g25: LineSegment StartX=-49.19 StartY=66.25 StartZ=0 EndX=-1.5 EndY=66.25 EndZ=0
    g26: LineSegment StartX=-49.19 StartY=63.5 StartZ=0 EndX=-1.5 EndY=63.5 EndZ=0
    g27: LineSegment StartX=-49.19 StartY=60.5 StartZ=0 EndX=-1.5 EndY=60.5 EndZ=0
    g28: LineSegment StartX=-49.19 StartY=57.75 StartZ=0 EndX=-1.5 EndY=57.75 EndZ=0
    g29: LineSegment StartX=-49.19 StartY=54.75 StartZ=0 EndX=-1.5 EndY=54.75 EndZ=0
    g30: LineSegment StartX=-49.19 StartY=52 StartZ=0 EndX=-11.49 EndY=52 EndZ=0
    g31: LineSegment StartX=-49.19 StartY=49 StartZ=0 EndX=-11.49 EndY=49 EndZ=0
    g32: LineSegment StartX=-49.19 StartY=46.25 StartZ=0 EndX=-16.28 EndY=46.25 EndZ=0
    g33: LineSegment StartX=-49.19 StartY=43.25 StartZ=0 EndX=-16.28 EndY=43.25 EndZ=0
    g34: LineSegment StartX=-49.19 StartY=40.5 StartZ=0 EndX=-18.2337 EndY=40.5 EndZ=0
    g35: LineSegment StartX=-49.19 StartY=37.5 StartZ=0 EndX=-18.23 EndY=37.5 EndZ=0
    g36: LineSegment StartX=-49.19 StartY=34.5 StartZ=0 EndX=-18.2337 EndY=34.5 EndZ=0
    g37: LineSegment StartX=-49.19 StartY=31.5 StartZ=0 EndX=-18.23 EndY=31.5 EndZ=0
    g38: LineSegment StartX=-49.19 StartY=28.75 StartZ=0 EndX=-16.2837 EndY=28.75 EndZ=0
    g39: LineSegment StartX=-49.19 StartY=25.75 StartZ=0 EndX=-16.28 EndY=25.75 EndZ=0
    g40: LineSegment StartX=-49.19 StartY=23 StartZ=0 EndX=-11.49 EndY=23 EndZ=0
    g41: LineSegment StartX=-49.19 StartY=20 StartZ=0 EndX=-11.49 EndY=20 EndZ=0
    g42: LineSegment StartX=-49.19 StartY=17.25 StartZ=0 EndX=-1.5 EndY=17.25 EndZ=0
    g43: LineSegment StartX=-49.19 StartY=14.25 StartZ=0 EndX=-1.5 EndY=14.25 EndZ=0
    g44: LineSegment StartX=-49.19 StartY=11.5 StartZ=0 EndX=-1.5 EndY=11.5 EndZ=0
    g45: LineSegment StartX=-49.19 StartY=8.5 StartZ=0 EndX=-1.5 EndY=8.5 EndZ=0
    g46: LineSegment StartX=-49.19 StartY=5.75 StartZ=0 EndX=-1.5 EndY=5.75 EndZ=0
    g47: LineSegment StartX=-49.19 StartY=2.75 StartZ=0 EndX=-1.5 EndY=2.75 EndZ=0
  constraints (120):
    c: Vertical(g0)
    c: Distance(g0) = 3
    c: Block(g0)
    c: Vertical(g1)
    c: Distance(g1) = 3
    c: Vertical(g2)
    c: Equal(g0,g2) = 3
    c: Block(g2)
    c: Vertical(g3)
    c: Equal(g1,g3) = 3
    c: Vertical(g4)
    c: Equal(g0,g4) = 3
    c: Block(g4)
    c: Vertical(g5)
    c: Equal(g1,g5) = 3
    c: Vertical(g6)
    c: Equal(g0,g6) = 3
    c: Block(g6)
    c: Vertical(g7)
    c: Equal(g1,g7) = 3
    c: Vertical(g8)
    c: Equal(g0,g8) = 3
    c: Block(g8)
    c: Vertical(g9)
    c: Equal(g1,g9) = 3
    c: Vertical(g10)
    c: Equal(g0,g10) = 3
    c: Block(g10)
    c: Vertical(g11)
    c: Equal(g1,g11) = 3
    c: Block(g12)
    c: Block(g13)
    c: Block(g14)
    c: Block(g15)
    c: Block(g16)
    c: Block(g17)
    c: Block(g18)
    c: Block(g19)
    c: Block(g20)
    c: Block(g21)
    c: Block(g22)
    c: Block(g23)
    c: Block(g11)
    c: Block(g9)
    c: Block(g7)
    c: Block(g5)
    c: Block(g3)
    c: Block(g1)
    c: Coincident(g24,g0)
    c: Coincident(g24,g12)
    c: Horizontal(g24)
    c: Coincident(g25,g0)
    c: Coincident(g25,g12)
    c: Horizontal(g25)
    c: Coincident(g26,g1)
    c: Coincident(g26,g13)
    c: Horizontal(g26)
    c: Coincident(g27,g1)
    c: Coincident(g27,g13)
    c: Horizontal(g27)
    c: Coincident(g28,g2)
    c: Coincident(g28,g14)
    c: Horizontal(g28)
    c: Coincident(g29,g2)
    c: Coincident(g29,g14)
    c: Horizontal(g29)
    c: Coincident(g30,g3)
    c: Coincident(g30,g15)
    c: Horizontal(g30)
    c: Coincident(g31,g3)
    c: Coincident(g31,g15)
    c: Horizontal(g31)
    c: Coincident(g32,g4)
    c: Coincident(g32,g16)
    c: Horizontal(g32)
    c: Coincident(g33,g4)
    c: Coincident(g33,g16)
    c: Horizontal(g33)
    c: Coincident(g34,g5)
    c: Coincident(g34,g17)
    c: Horizontal(g34)
    c: Coincident(g35,g5)
    c: Coincident(g35,g17)
    c: Horizontal(g35)
    c: Coincident(g36,g6)
    c: Coincident(g36,g19)
    c: Horizontal(g36)
    c: Coincident(g37,g6)
    c: Coincident(g37,g19)
    c: Horizontal(g37)
    c: Coincident(g38,g7)
    c: Coincident(g38,g18)
    c: Horizontal(g38)
    c: Coincident(g39,g7)
    c: Coincident(g39,g18)
    c: Horizontal(g39)
    c: Coincident(g40,g8)
    c: Coincident(g40,g20)
    c: Horizontal(g40)
    c: Coincident(g41,g8)
    c: Coincident(g41,g20)
    c: Horizontal(g41)
    c: Coincident(g42,g9)
    c: Coincident(g42,g23)
    c: Horizontal(g42)
    c: Coincident(g43,g9)
    c: Coincident(g43,g23)
    c: Horizontal(g43)
    c: Coincident(g44,g10)
    c: Coincident(g44,g22)
    c: Horizontal(g44)
    c: Coincident(g45,g10)
    c: Coincident(g45,g22)
    c: Horizontal(g45)
    c: Coincident(g46,g11)
    c: Coincident(g46,g21)
    c: Horizontal(g46)
    c: Coincident(g47,g11)
    c: Coincident(g47,g21)
    c: Horizontal(g47)
FEATURE [Part::Extrusion] Extrude042
  Base = -> Sketch051
  Dir = (1,-2e-16,2e-16)
  DirMode = 2
  FaceMakerClass = Part::FaceMakerBullseye
  LengthFwd = 19
  LengthRev = 0
  Placement = pos=(-19,0,0) rot=(0,0,1;0rad)
  Solid = true
  Symmetric = false
FEATURE [Part::Fillet] Fillet035  label="removeToCreateVentalationHoles"
  Base = -> Extrude042
  Edges = <same value as first occurrence — deduplicated (x6 in doc)>
  Placement = pos=(7,0,0) rot=(0,0,1;0rad)
FEATURE [Part::Cut] Cut038  label="top017"
  Base = -> Cut033
  Tool = -> Fillet035
FEATURE [Sketcher::SketchObject] Sketch052  label="bottomSketch001"
  FullyConstrained = true
  sketch-geometry (45):
    g0: LineSegment StartX=6.29999 StartY=8 StartZ=0 EndX=3.29999 EndY=8 EndZ=0
    g1: LineSegment StartX=3.29999 StartY=8 StartZ=0 EndX=3.29999 EndY=-6.03275e-07 EndZ=0
    g2: ArcOfCircle CenterX=8.29999 CenterY=5 CenterZ=0 NormalX=0 NormalY=0 NormalZ=1 AngleXU=0 Radius=2 StartAngle=3.14159 EndAngle=4.71239
    g3: LineSegment StartX=6.29999 StartY=8 StartZ=0 EndX=6.29999 EndY=5 EndZ=0
    g4: ArcOfCircle CenterX=105 CenterY=19 CenterZ=0 NormalX=0 NormalY=0 NormalZ=1 AngleXU=0 Radius=12.7 StartAngle=4.71239 EndAngle=5.94289
    g5-g11: Circle x7 (B-spline internal-alignment scaffolding for g12; pole/knot coordinates omitted)
    g12: BSplineCurve PolesCount=7 KnotsCount=5 Degree=3 IsPeriodic=0
    g13-g17: GeomPoint x5 (B-spline internal-alignment scaffolding for g12; pole/knot coordinates omitted)
    g18: ArcOfCircle CenterX=105 CenterY=19 CenterZ=0 NormalX=0 NormalY=0 NormalZ=1 AngleXU=0 Radius=15.7 StartAngle=5.81226 EndAngle=6.28319
    g19: BSplineCurve PolesCount=5 KnotsCount=3 Degree=3 IsPeriodic=0
    g20: LineSegment StartX=8.29999 StartY=3 StartZ=0 EndX=101.7 EndY=3 EndZ=0
    g21: LineSegment StartX=3.29999 StartY=-6.03275e-07 StartZ=0 EndX=105 EndY=-6.03275e-07 EndZ=0
    g22: LineSegment StartX=120.974 StartY=8.71251 StartZ=0 EndX=122.332 EndY=7.83778 EndZ=0
    g23: LineSegment StartX=105 StartY=-6.03274e-07 StartZ=0 EndX=113 EndY=-6.03274e-07 EndZ=0
    g24: ArcOfCircle CenterX=105 CenterY=19 CenterZ=0 NormalX=0 NormalY=0 NormalZ=1 AngleXU=0 Radius=20.6155 StartAngle=5.11091 EndAngle=5.71103
    g25: ArcOfCircle CenterX=117.7 CenterY=19 CenterZ=0 NormalX=0 NormalY=0 NormalZ=1 AngleXU=0 Radius=3 StartAngle=1.2e-15 EndAngle=2.10468
    g26: Circle CenterX=116.345 CenterY=16.3232 CenterZ=0 NormalX=0 NormalY=0 NormalZ=1 AngleXU=0 Radius=1
    g27: Circle CenterX=117.24 CenterY=15.7584 CenterZ=0 NormalX=0 NormalY=0 NormalZ=1 AngleXU=0 Radius=1
    g28: Circle CenterX=116.972 CenterY=14.7612 CenterZ=0 NormalX=0 NormalY=0 NormalZ=1 AngleXU=0 Radius=1
    g29: BSplineCurve PolesCount=3 KnotsCount=2 Degree=2 IsPeriodic=0
    g30: GeomPoint X=116.345 Y=16.3232 Z=0
    g31: GeomPoint X=116.972 Y=14.7612 Z=0
    g32: Circle CenterX=115.828 CenterY=17.157 CenterZ=0 NormalX=0 NormalY=0 NormalZ=1 AngleXU=0 Radius=1
    g33: Circle CenterX=115.841 CenterY=16.639 CenterZ=0 NormalX=0 NormalY=0 NormalZ=1 AngleXU=0 Radius=1
    g34: Circle CenterX=116.345 CenterY=16.3232 CenterZ=0 NormalX=0 NormalY=0 NormalZ=1 AngleXU=0 Radius=1
    g35: BSplineCurve PolesCount=3 KnotsCount=2 Degree=2 IsPeriodic=0
    g36: GeomPoint X=115.828 Y=17.157 Z=0
    g37: GeomPoint X=116.345 Y=16.3232 Z=0
    g38: LineSegment StartX=115.828 StartY=17.157 StartZ=0 EndX=115.828 EndY=20.8307 EndZ=0
    g39: Circle CenterX=115.828 CenterY=20.8307 CenterZ=0 NormalX=0 NormalY=0 NormalZ=1 AngleXU=0 Radius=1
    g40: Circle CenterX=115.831 CenterY=21.3396 CenterZ=0 NormalX=0 NormalY=0 NormalZ=1 AngleXU=0 Radius=1
    g41: Circle CenterX=116.173 CenterY=21.5825 CenterZ=0 NormalX=0 NormalY=0 NormalZ=1 AngleXU=0 Radius=1
    g42: BSplineCurve PolesCount=3 KnotsCount=2 Degree=2 IsPeriodic=0
    g43: GeomPoint X=115.828 Y=20.8307 Z=0
    g44: GeomPoint X=116.173 Y=21.5825 Z=0
  constraints (70):
    c: Horizontal(g0)
    c: Distance(g0) = 3
    c: Coincident(g1,g0)
    c: Vertical(g1)
    c: Block(g2)
    c: Block(g0)
    c: Coincident(g3,g0)
    c: Coincident(g3,g2)
    c: Vertical(g3)
    c: Block(g1)
    c: Block(g4)
    c: Coincident(g19,g4)
    c: Block(g19)
    c: Equal(g5, g6-g11) x6
    c: InternalAlignment(g5-g11 -> g12) x7
    c: InternalAlignment(g13-g17 -> g12) x5
    c: Block(g12)
    c: Coincident(g18,g12)
    c: Block(g18)
    c: Coincident(g20,g2)
    c: Coincident(g20,g19)
    c: Horizontal(g20)
    c: Distance(g20) = 93.4
    c: Coincident(g21,g1)
    c: Horizontal(g21)
    c: Distance(g21) = 101.7
    c: Horizontal(g23)
    c: Distance(g23) = 8
    c: Coincident(g24,g23)
    c: Block(g23)
    c: Coincident(g22,g24)
    c: Block(g24)
    c: Block(g22)
    c: Distance(g22) = 1.61553
    c: Coincident(g25,g18)
    c: Block(g25)
    c: Weight(g26) = 1
    c: Equal(g26,g27)
    c: Equal(g26,g28)
    c: Coincident(g29,g4)
    c: InternalAlignment(g26,g29)
    c: InternalAlignment(g27,g29)
    c: InternalAlignment(g28,g29)
    c: InternalAlignment(g30,g29)
    c: InternalAlignment(g31,g29)
    c: Block(g29)
    c: Weight(g32) = 1
    c: Equal(g32,g33)
    c: Equal(g32,g34)
    c: Coincident(g35,g29)
    c: InternalAlignment(g32,g35)
    c: InternalAlignment(g33,g35)
    c: InternalAlignment(g34,g35)
    c: InternalAlignment(g36,g35)
    c: InternalAlignment(g37,g35)
    c: Block(g35)
    c: Coincident(g38,g35)
    c: Vertical(g38)
    c: Block(g38)
    c: Coincident(g42,g38)
    c: Weight(g39) = 1
    c: Equal(g39,g40)
    c: Equal(g39,g41)
    c: Coincident(g42,g25)
    c: InternalAlignment(g39,g42)
    c: InternalAlignment(g40,g42)
    c: InternalAlignment(g41,g42)
    c: InternalAlignment(g43,g42)
    c: InternalAlignment(g44,g42)
    c: Block(g42)
FEATURE [Part::Extrusion] Extrude043  label="bottom010"
  Base = -> Sketch052
  Dir = (0,0,1)
  DirMode = 2
  FaceMakerClass = Part::FaceMakerBullseye
  LengthFwd = 71.4
  LengthRev = 0
  Placement = pos=(0,0,0.3) rot=(0,0,1;0rad)
  Solid = true
  Symmetric = false
FEATURE [Sketcher::SketchObject] Sketch053  label="topSketch013"
  FullyConstrained = true
  sketch-geometry (22):
    g0: LineSegment StartX=5.21097e-06 StartY=3 StartZ=0 EndX=5.21097e-06 EndY=19 EndZ=0
    g1: ArcOfCircle CenterX=19 CenterY=19 CenterZ=0 NormalX=0 NormalY=0 NormalZ=1 AngleXU=0 Radius=19 StartAngle=1.5708 EndAngle=3.14159
    g2: ArcOfCircle CenterX=19 CenterY=19 CenterZ=0 NormalX=0 NormalY=0 NormalZ=1 AngleXU=0 Radius=16 StartAngle=1.5708 EndAngle=3.14159
    g3: LineSegment StartX=114 StartY=35 StartZ=0 EndX=19 EndY=35 EndZ=0
    g4: LineSegment StartX=5.21097e-06 StartY=3 StartZ=0 EndX=5.21097e-06 EndY=0 EndZ=0
    g5: LineSegment StartX=3 StartY=0 StartZ=0 EndX=5.21097e-06 EndY=0 EndZ=0
    g6: LineSegment StartX=3 StartY=19 StartZ=0 EndX=3 EndY=0 EndZ=0
    g7: LineSegment StartX=19 StartY=38 StartZ=0 EndX=124 EndY=38 EndZ=0
    g8: Circle CenterX=119 CenterY=35 CenterZ=0 NormalX=0 NormalY=0 NormalZ=1 AngleXU=0 Radius=1
    g9: Circle CenterX=121 CenterY=35 CenterZ=0 NormalX=0 NormalY=0 NormalZ=1 AngleXU=0 Radius=1
    g10: Circle CenterX=121 CenterY=33 CenterZ=0 NormalX=0 NormalY=0 NormalZ=1 AngleXU=0 Radius=1
    g11: BSplineCurve PolesCount=3 KnotsCount=2 Degree=2 IsPeriodic=0
    g12: GeomPoint X=119 Y=35 Z=0
    g13: GeomPoint X=121 Y=33 Z=0
    g14: LineSegment StartX=119 StartY=35 StartZ=0 EndX=114 EndY=35 EndZ=0
    g15: ArcOfCircle CenterX=105 CenterY=19 CenterZ=0 NormalX=0 NormalY=0 NormalZ=1 AngleXU=0 Radius=16 StartAngle=5.60905 EndAngle=6.28319
    g16: LineSegment StartX=121 StartY=33 StartZ=0 EndX=121 EndY=19 EndZ=0
    g17: LineSegment StartX=117.5 StartY=9.01251 StartZ=0 EndX=121.163 EndY=9.0125 EndZ=0
    g18: ArcOfCircle CenterX=105 CenterY=19 CenterZ=0 NormalX=0 NormalY=0 NormalZ=1 AngleXU=0 Radius=20.6155 StartAngle=5.7297 EndAngle=6.28319
    g19: LineSegment StartX=121.163 StartY=9.0125 StartZ=0 EndX=122.538 EndY=8.16329 EndZ=0
    g20: LineSegment StartX=124 StartY=38 StartZ=0 EndX=125.616 EndY=38 EndZ=0
    g21: LineSegment StartX=125.616 StartY=19 StartZ=0 EndX=125.616 EndY=38 EndZ=0
  constraints (50):
    c: Vertical(g0)
    c: Block(g0)
    c: Coincident(g1,g0)
    c: Block(g1)
    c: Coincident(g2,g1)
    c: Block(g2)
    c: Coincident(g3,g2)
    c: Horizontal(g3)
    c: Tangent(g3,g2)
    c: Coincident(g4,g0)
    c: Distance(g4) = 3
    c: Vertical(g4)
    c: Coincident(g5,g4)
    c: Horizontal(g5)
    c: Coincident(g6,g2)
    c: Coincident(g6,g5)
    c: Vertical(g6)
    c: Horizontal(g7)
    c: Distance(g7) = 105
    c: Coincident(g7,g1)
    c: Block(g3)
    c: Weight(g8) = 1
    c: Equal(g8,g9)
    c: Equal(g8,g10)
    c: InternalAlignment(g8,g11)
    c: InternalAlignment(g9,g11)
    c: InternalAlignment(g10,g11)
    c: InternalAlignment(g12,g11)
    c: InternalAlignment(g13,g11)
    c: Block(g11)
    c: Coincident(g14,g11)
    c: Coincident(g14,g3)
    c: Horizontal(g14)
    c: Block(g15)
    c: Coincident(g16,g11)
    c: Coincident(g16,g15)
    c: Vertical(g16)
    c: Distance(g16) = 14
    c: Coincident(g17,g15)
    c: Block(g18)
    c: Coincident(g19,g18)
    c: Coincident(g20,g7)
    c: Horizontal(g20)
    c: Vertical(g21)
    c: Coincident(g20,g21)
    c: Block(g20)
    c: Block(g21)
    c: Block(g19)
    c: Block(g17)
    c: Distance(g20) = 1.61553
FEATURE [Part::Extrusion] Extrude044
  Base = -> Sketch053
  Dir = (0,0,1)
  DirMode = 2
  FaceMakerClass = Part::FaceMakerBullseye
  LengthFwd = 72
  LengthRev = 0
  Solid = true
  Symmetric = false
FEATURE [Part::Fillet] Fillet036  label="top018"
  Base = -> Extrude044
  Edges = 1 edges r=2: [Edge41]
FEATURE [Sketcher::SketchObject] Sketch054
  FullyConstrained = false
  Placement = pos=(0,0,0) rot=(1,0,0;1.5708rad)
  sketch-geometry (24):
    g0: ArcOfCircle CenterX=-4 CenterY=-10.5 CenterZ=0 NormalX=0 NormalY=0 NormalZ=1 AngleXU=0 Radius=1.5 StartAngle=6e-16 EndAngle=3.14159
    g1: ArcOfCircle CenterX=-34.2 CenterY=-10.5 CenterZ=0 NormalX=0 NormalY=0 NormalZ=1 AngleXU=0 Radius=1.5 StartAngle=0 EndAngle=3.14159
    g2: ArcOfCircle CenterX=-34.2 CenterY=-27.7 CenterZ=0 NormalX=0 NormalY=0 NormalZ=1 AngleXU=0 Radius=1.5 StartAngle=3.14159 EndAngle=6.28319
    g3: ArcOfCircle CenterX=-4 CenterY=-27.7 CenterZ=0 NormalX=0 NormalY=0 NormalZ=1 AngleXU=0 Radius=1.5 StartAngle=3.1416 EndAngle=6.28319
    g4: ArcOfCircle CenterX=-10 CenterY=-4.3 CenterZ=0 NormalX=0 NormalY=0 NormalZ=1 AngleXU=0 Radius=1.5 StartAngle=2e-16 EndAngle=3.14159
    g5: ArcOfCircle CenterX=-16.1 CenterY=-1.8 CenterZ=0 NormalX=0 NormalY=0 NormalZ=1 AngleXU=0 Radius=1.5 StartAngle=5e-16 EndAngle=3.14159
    g6: ArcOfCircle CenterX=-22.1 CenterY=-1.8 CenterZ=0 NormalX=0 NormalY=0 NormalZ=1 AngleXU=0 Radius=1.5 StartAngle=5e-16 EndAngle=3.14159
    g7: ArcOfCircle CenterX=-28.2 CenterY=-4.3 CenterZ=0 NormalX=0 NormalY=0 NormalZ=1 AngleXU=0 Radius=1.5 StartAngle=2e-16 EndAngle=3.14159
    g8: ArcOfCircle CenterX=-10 CenterY=-33.9 CenterZ=0 NormalX=0 NormalY=0 NormalZ=1 AngleXU=0 Radius=1.5 StartAngle=3.14159 EndAngle=6.28319
    g9: ArcOfCircle CenterX=-16.1 CenterY=-36.4 CenterZ=0 NormalX=0 NormalY=0 NormalZ=1 AngleXU=0 Radius=1.5 StartAngle=3.14159 EndAngle=6.28319
    g10: ArcOfCircle CenterX=-22.1 CenterY=-36.4 CenterZ=0 NormalX=0 NormalY=0 NormalZ=1 AngleXU=0 Radius=1.5 StartAngle=3.14159 EndAngle=6.28319
    g11: ArcOfCircle CenterX=-28.2 CenterY=-33.9 CenterZ=0 NormalX=0 NormalY=0 NormalZ=1 AngleXU=0 Radius=1.5 StartAngle=3.14159 EndAngle=6.28319
    g12: LineSegment StartX=-35.7 StartY=-10.5 StartZ=0 EndX=-35.7 EndY=-27.7 EndZ=0
    g13: LineSegment StartX=-32.7 StartY=-10.5 StartZ=0 EndX=-32.7 EndY=-27.7 EndZ=0
    g14: LineSegment StartX=-29.7 StartY=-33.9 StartZ=0 EndX=-29.7 EndY=-4.3 EndZ=0
    g15: LineSegment StartX=-26.7 StartY=-33.9 StartZ=0 EndX=-26.7 EndY=-4.3 EndZ=0
    g16: LineSegment StartX=-2.5 StartY=-10.5 StartZ=0 EndX=-2.5 EndY=-27.7 EndZ=0
    g17: LineSegment StartX=-8.5 StartY=-4.3 StartZ=0 EndX=-8.5 EndY=-33.9 EndZ=0
    g18: LineSegment StartX=-5.5 StartY=-10.5 StartZ=0 EndX=-5.5 EndY=-27.7 EndZ=0
    g19: LineSegment StartX=-11.5 StartY=-4.3 StartZ=0 EndX=-11.5 EndY=-33.9 EndZ=0
    g20: LineSegment StartX=-14.6 StartY=-1.8 StartZ=0 EndX=-14.6 EndY=-36.4 EndZ=0
    g21: LineSegment StartX=-17.6 StartY=-1.8 StartZ=0 EndX=-17.6 EndY=-36.4 EndZ=0
    g22: LineSegment StartX=-20.6 StartY=-36.4 StartZ=0 EndX=-20.6 EndY=-1.8 EndZ=0
    g23: LineSegment StartX=-23.6 StartY=-1.8 StartZ=0 EndX=-23.6 EndY=-36.4 EndZ=0
  constraints (48):
    c: Block(g0)
    c: Block(g1)
    c: Block(g2)
    c: Block(g3)
    c: Block(g4)
    c: Block(g5)
    c: Block(g6)
    c: Block(g7)
    c: Block(g8)
    c: Block(g9)
    c: Block(g10)
    c: Block(g11)
    c: Coincident(g12,g1)
    c: Coincident(g12,g2)
    c: Vertical(g12)
    c: Coincident(g13,g1)
    c: Coincident(g13,g2)
    c: Vertical(g13)
    c: Coincident(g14,g11)
    c: Coincident(g14,g7)
    c: Vertical(g14)
    c: Coincident(g15,g11)
    c: Coincident(g15,g7)
    c: Vertical(g15)
    c: Coincident(g16,g0)
    c: Coincident(g16,g3)
    c: Vertical(g16)
    c: Coincident(g17,g4)
    c: Coincident(g17,g8)
    c: Vertical(g17)
    c: Coincident(g18,g0)
    c: Coincident(g18,g3)
    c: Vertical(g18)
    c: Coincident(g19,g4)
    c: Coincident(g19,g8)
    c: Vertical(g19)
    c: Coincident(g20,g5)
    c: Coincident(g20,g9)
    c: Vertical(g20)
    c: Coincident(g21,g5)
    c: Coincident(g21,g9)
    c: Vertical(g21)
    c: Coincident(g22,g10)
    c: Coincident(g22,g6)
    c: Vertical(g22)
    c: Coincident(g23,g6)
    c: Coincident(g23,g10)
    c: Vertical(g23)
FEATURE [Part::Extrusion] Extrude045  label="removeToCreateFanGrillHoles003"
  Base = -> Sketch054
  Dir = (0,-1,6e-16)
  DirMode = 2
  FaceMakerClass = Part::FaceMakerBullseye
  LengthFwd = 10
  LengthRev = 0
  Placement = pos=(65.4,44,54.82) rot=(0,0,1;0rad)
  Solid = true
  Symmetric = false
FEATURE [Part::Feature] Face105 .. Face108  x4 (patterned run collapsed; names and placements below)
  shape: bbox 3.5 x 17.8 x 2e-07 mm, 1 faces, 0 solids (baked)
FEATURE [Part::Revolution] Revolve113  label="removeToCreateScrewAndThreadedInsertHole041"
  Angle = 360
  Axis = (0,1,0)
  Base = (0,0,0)
  FaceMakerClass = Part::FaceMakerBullseye
  Placement = pos=(62.3,30.3,19.7) rot=(0,0,1;0rad)
  Solid = false
  Source = -> Face105
  Symmetric = false
FEATURE [Part::Revolution] Revolve114  label="removeToCreateScrewAndThreadedInsertHole042"
  Angle = 360
  Axis = (0,1,0)
  Base = (0,0,0)
  FaceMakerClass = Part::FaceMakerBullseye
  Placement = pos=(62.3,30.3,51.7) rot=(0,0,1;0rad)
  Solid = false
  Source = -> Face106
  Symmetric = false
FEATURE [Part::Revolution] Revolve115  label="removeToCreateScrewAndThreadedInsertHole043"
  Angle = 360
  Axis = (0,1,0)
  Base = (0,0,0)
  FaceMakerClass = Part::FaceMakerBullseye
  Placement = pos=(30.3,30.3,19.7) rot=(0,0,1;0rad)
  Solid = false
  Source = -> Face107
  Symmetric = false
FEATURE [Part::Revolution] Revolve116  label="removeToCreateScrewAndThreadedInsertHole044"
  Angle = 360
  Axis = (0,1,0)
  Base = (0,0,0)
  FaceMakerClass = Part::FaceMakerBullseye
  Placement = pos=(30.3,30.3,51.7) rot=(0,0,1;0rad)
  Solid = false
  Source = -> Face108
  Symmetric = false
FEATURE [Part::MultiFuse] Fusion083  label="createThreadedInsertHolesForFan004"
  Shapes = -> [Revolve113,Revolve114,Revolve115,Revolve116]
FEATURE [Part::Box] Box024  label="removeToCreteHoleForPlugHousing026"
  AttacherType = Attacher::AttachEngine3D
  Height = 28.6
  Length = 10
  Placement = pos=(-2,0,21.7) rot=(0,0,1;0rad)
  Width = 19
FEATURE [Part::Cylinder] Cylinder038  label="removeToCreteHoleForPlugHousing027"
  Angle = 360
  AttacherType = Attacher::AttachEngine3D
  Height = 20
  Placement = pos=(-2,19,36) rot=(0,1,0;1.5708rad)
  Radius = 14.3
FEATURE [Part::MultiFuse] Fusion084  label="removeToCreteHoleForPlugHousing028"
  Shapes = -> [Box024,Cylinder038]
FEATURE [Part::Cylinder] Cylinder039
  Angle = 360
  AttacherType = Attacher::AttachEngine3D
  Height = 20
  Placement = pos=(0,0,36.15) rot=(0,0,1;0rad)
  Radius = 14.3
FEATURE [Part::Cylinder] Cylinder040
  Angle = 360
  AttacherType = Attacher::AttachEngine3D
  Height = 10
  Placement = pos=(0,0,36.15) rot=(0,0,1;0rad)
  Radius = 4
FEATURE [Part::Box] Box025  label="removeToCreteHoleForPlugHousing030"
  AttacherType = Attacher::AttachEngine3D
  Height = 28.6
  Length = 20
  Placement = pos=(106.15,0,21.7) rot=(0,0,1;0rad)
  Width = 19
FEATURE [Part::MultiFuse] Fusion086  label="removeToCreteHoleForPlugHousing031"
  Placement = pos=(70,19,36) rot=(0,1,0;1.5708rad)
  Shapes = -> [Cylinder039,Cylinder040]
FEATURE [Part::MultiFuse] Fusion085  label="removeToCreteHoleForPlugHousing029"
  Shapes = -> [Box025,Fusion086]
FEATURE [Sketcher::SketchObject] Sketch055
  FullyConstrained = true
  Placement = pos=(117,19,0) rot=(0.57735,0.57735,0.57735;2.0944rad)
  sketch-geometry (48):
    g0: LineSegment StartX=-49.19 StartY=69.25 StartZ=0 EndX=-49.19 EndY=66.25 EndZ=0
    g1: LineSegment StartX=-49.19 StartY=63.5 StartZ=0 EndX=-49.19 EndY=60.5 EndZ=0
    g2: LineSegment StartX=-49.19 StartY=57.75 StartZ=0 EndX=-49.19 EndY=54.75 EndZ=0
    g3: LineSegment StartX=-49.19 StartY=52 StartZ=0 EndX=-49.19 EndY=49 EndZ=0
    g4: LineSegment StartX=-49.19 StartY=46.25 StartZ=0 EndX=-49.19 EndY=43.25 EndZ=0
    g5: LineSegment StartX=-49.19 StartY=40.5 StartZ=0 EndX=-49.19 EndY=37.5 EndZ=0
    g6: LineSegment StartX=-49.19 StartY=34.5 StartZ=0 EndX=-49.19 EndY=31.5 EndZ=0
    g7: LineSegment StartX=-49.19 StartY=28.75 StartZ=0 EndX=-49.19 EndY=25.75 EndZ=0
    g8: LineSegment StartX=-49.19 StartY=23 StartZ=0 EndX=-49.19 EndY=20 EndZ=0
    g9: LineSegment StartX=-49.19 StartY=17.25 StartZ=0 EndX=-49.19 EndY=14.25 EndZ=0
    g10: LineSegment StartX=-49.19 StartY=11.5 StartZ=0 EndX=-49.19 EndY=8.5 EndZ=0
    g11: LineSegment StartX=-49.19 StartY=5.75 StartZ=0 EndX=-49.19 EndY=2.75 EndZ=0
    g12: ArcOfCircle CenterX=-1.5 CenterY=67.75 CenterZ=0 NormalX=0 NormalY=0 NormalZ=1 AngleXU=0 Radius=1.5 StartAngle=4.71239 EndAngle=7.85398
    g13: ArcOfCircle CenterX=-1.5 CenterY=62 CenterZ=0 NormalX=0 NormalY=0 NormalZ=1 AngleXU=0 Radius=1.5 StartAngle=4.71239 EndAngle=7.85398
    g14: ArcOfCircle CenterX=-1.5 CenterY=56.25 CenterZ=0 NormalX=0 NormalY=0 NormalZ=1 AngleXU=0 Radius=1.5 StartAngle=4.71239 EndAngle=7.85398
    g15: ArcOfCircle CenterX=-11.49 CenterY=50.5 CenterZ=0 NormalX=0 NormalY=0 NormalZ=1 AngleXU=0 Radius=1.5 StartAngle=4.71239 EndAngle=7.85398
    g16: ArcOfCircle CenterX=-16.28 CenterY=44.75 CenterZ=0 NormalX=0 NormalY=0 NormalZ=1 AngleXU=0 Radius=1.5 StartAngle=4.71239 EndAngle=7.85398
    g17: ArcOfCircle CenterX=-18.2337 CenterY=39 CenterZ=0 NormalX=0 NormalY=0 NormalZ=1 AngleXU=0 Radius=1.5 StartAngle=4.71485 EndAngle=7.85398
    g18: ArcOfCircle CenterX=-16.2837 CenterY=27.25 CenterZ=0 NormalX=0 NormalY=0 NormalZ=1 AngleXU=0 Radius=1.5 StartAngle=4.71485 EndAngle=7.85398
    g19: ArcOfCircle CenterX=-18.2337 CenterY=33 CenterZ=0 NormalX=0 NormalY=0 NormalZ=1 AngleXU=0 Radius=1.5 StartAngle=4.71485 EndAngle=7.85398
    g20: ArcOfCircle CenterX=-11.49 CenterY=21.5 CenterZ=0 NormalX=0 NormalY=0 NormalZ=1 AngleXU=0 Radius=1.5 StartAngle=4.71239 EndAngle=7.85398
    g21: ArcOfCircle CenterX=-1.5 CenterY=4.25 CenterZ=0 NormalX=0 NormalY=0 NormalZ=1 AngleXU=0 Radius=1.5 StartAngle=4.71239 EndAngle=7.85398
    g22: ArcOfCircle CenterX=-1.5 CenterY=10 CenterZ=0 NormalX=0 NormalY=0 NormalZ=1 AngleXU=0 Radius=1.5 StartAngle=4.71239 EndAngle=7.85398
    g23: ArcOfCircle CenterX=-1.5 CenterY=15.75 CenterZ=0 NormalX=0 NormalY=0 NormalZ=1 AngleXU=0 Radius=1.5 StartAngle=4.71239 EndAngle=7.85398
    g24: LineSegment StartX=-49.19 StartY=69.25 StartZ=0 EndX=-1.5 EndY=69.25 EndZ=0
    g25: LineSegment StartX=-49.19 StartY=66.25 StartZ=0 EndX=-1.5 EndY=66.25 EndZ=0
    g26: LineSegment StartX=-49.19 StartY=63.5 StartZ=0 EndX=-1.5 EndY=63.5 EndZ=0
    g27: LineSegment StartX=-49.19 StartY=60.5 StartZ=0 EndX=-1.5 EndY=60.5 EndZ=0
    g28: LineSegment StartX=-49.19 StartY=57.75 StartZ=0 EndX=-1.5 EndY=57.75 EndZ=0
    g29: LineSegment StartX=-49.19 StartY=54.75 StartZ=0 EndX=-1.5 EndY=54.75 EndZ=0
    g30: LineSegment StartX=-49.19 StartY=52 StartZ=0 EndX=-11.49 EndY=52 EndZ=0
    g31: LineSegment StartX=-49.19 StartY=49 StartZ=0 EndX=-11.49 EndY=49 EndZ=0
    g32: LineSegment StartX=-49.19 StartY=46.25 StartZ=0 EndX=-16.28 EndY=46.25 EndZ=0
    g33: LineSegment StartX=-49.19 StartY=43.25 StartZ=0 EndX=-16.28 EndY=43.25 EndZ=0
    g34: LineSegment StartX=-49.19 StartY=40.5 StartZ=0 EndX=-18.2337 EndY=40.5 EndZ=0
    g35: LineSegment StartX=-49.19 StartY=37.5 StartZ=0 EndX=-18.23 EndY=37.5 EndZ=0
    g36: LineSegment StartX=-49.19 StartY=34.5 StartZ=0 EndX=-18.2337 EndY=34.5 EndZ=0
    g37: LineSegment StartX=-49.19 StartY=31.5 StartZ=0 EndX=-18.23 EndY=31.5 EndZ=0
    g38: LineSegment StartX=-49.19 StartY=28.75 StartZ=0 EndX=-16.2837 EndY=28.75 EndZ=0
    g39: LineSegment StartX=-49.19 StartY=25.75 StartZ=0 EndX=-16.28 EndY=25.75 EndZ=0
    g40: LineSegment StartX=-49.19 StartY=23 StartZ=0 EndX=-11.49 EndY=23 EndZ=0
    g41: LineSegment StartX=-49.19 StartY=20 StartZ=0 EndX=-11.49 EndY=20 EndZ=0
    g42: LineSegment StartX=-49.19 StartY=17.25 StartZ=0 EndX=-1.5 EndY=17.25 EndZ=0
    g43: LineSegment StartX=-49.19 StartY=14.25 StartZ=0 EndX=-1.5 EndY=14.25 EndZ=0
    g44: LineSegment StartX=-49.19 StartY=11.5 StartZ=0 EndX=-1.5 EndY=11.5 EndZ=0
    g45: LineSegment StartX=-49.19 StartY=8.5 StartZ=0 EndX=-1.5 EndY=8.5 EndZ=0
    g46: LineSegment StartX=-49.19 StartY=5.75 StartZ=0 EndX=-1.5 EndY=5.75 EndZ=0
    g47: LineSegment StartX=-49.19 StartY=2.75 StartZ=0 EndX=-1.5 EndY=2.75 EndZ=0
  constraints (120):
    c: Vertical(g0)
    c: Distance(g0) = 3
    c: Block(g0)
    c: Vertical(g1)
    c: Distance(g1) = 3
    c: Vertical(g2)
    c: Equal(g0,g2) = 3
    c: Block(g2)
    c: Vertical(g3)
    c: Equal(g1,g3) = 3
    c: Vertical(g4)
    c: Equal(g0,g4) = 3
    c: Block(g4)
    c: Vertical(g5)
    c: Equal(g1,g5) = 3
    c: Vertical(g6)
    c: Equal(g0,g6) = 3
    c: Block(g6)
    c: Vertical(g7)
    c: Equal(g1,g7) = 3
    c: Vertical(g8)
    c: Equal(g0,g8) = 3
    c: Block(g8)
    c: Vertical(g9)
    c: Equal(g1,g9) = 3
    c: Vertical(g10)
    c: Equal(g0,g10) = 3
    c: Block(g10)
    c: Vertical(g11)
    c: Equal(g1,g11) = 3
    c: Block(g12)
    c: Block(g13)
    c: Block(g14)
    c: Block(g15)
    c: Block(g16)
    c: Block(g17)
    c: Block(g18)
    c: Block(g19)
    c: Block(g20)
    c: Block(g21)
    c: Block(g22)
    c: Block(g23)
    c: Block(g11)
    c: Block(g9)
    c: Block(g7)
    c: Block(g5)
    c: Block(g3)
    c: Block(g1)
    c: Coincident(g24,g0)
    c: Coincident(g24,g12)
    c: Horizontal(g24)
    c: Coincident(g25,g0)
    c: Coincident(g25,g12)
    c: Horizontal(g25)
    c: Coincident(g26,g1)
    c: Coincident(g26,g13)
    c: Horizontal(g26)
    c: Coincident(g27,g1)
    c: Coincident(g27,g13)
    c: Horizontal(g27)
    c: Coincident(g28,g2)
    c: Coincident(g28,g14)
    c: Horizontal(g28)
    c: Coincident(g29,g2)
    c: Coincident(g29,g14)
    c: Horizontal(g29)
    c: Coincident(g30,g3)
    c: Coincident(g30,g15)
    c: Horizontal(g30)
    c: Coincident(g31,g3)
    c: Coincident(g31,g15)
    c: Horizontal(g31)
    c: Coincident(g32,g4)
    c: Coincident(g32,g16)
    c: Horizontal(g32)
    c: Coincident(g33,g4)
    c: Coincident(g33,g16)
    c: Horizontal(g33)
    c: Coincident(g34,g5)
    c: Coincident(g34,g17)
    c: Horizontal(g34)
    c: Coincident(g35,g5)
    c: Coincident(g35,g17)
    c: Horizontal(g35)
    c: Coincident(g36,g6)
    c: Coincident(g36,g19)
    c: Horizontal(g36)
    c: Coincident(g37,g6)
    c: Coincident(g37,g19)
    c: Horizontal(g37)
    c: Coincident(g38,g7)
    c: Coincident(g38,g18)
    c: Horizontal(g38)
    c: Coincident(g39,g7)
    c: Coincident(g39,g18)
    c: Horizontal(g39)
    c: Coincident(g40,g8)
    c: Coincident(g40,g20)
    c: Horizontal(g40)
    c: Coincident(g41,g8)
    c: Coincident(g41,g20)
    c: Horizontal(g41)
    c: Coincident(g42,g9)
    c: Coincident(g42,g23)
    c: Horizontal(g42)
    c: Coincident(g43,g9)
    c: Coincident(g43,g23)
    c: Horizontal(g43)
    c: Coincident(g44,g10)
    c: Coincident(g44,g22)
    c: Horizontal(g44)
    c: Coincident(g45,g10)
    c: Coincident(g45,g22)
    c: Horizontal(g45)
    c: Coincident(g46,g11)
    c: Coincident(g46,g21)
    c: Horizontal(g46)
    c: Coincident(g47,g11)
    c: Coincident(g47,g21)
    c: Horizontal(g47)
FEATURE [Part::Extrusion] Extrude046
  Base = -> Sketch055
  Dir = (1,0,0)
  DirMode = 2
  FaceMakerClass = Part::FaceMakerBullseye
  LengthFwd = 23
  LengthRev = 0
  Placement = pos=(-19,0,0) rot=(0,0,1;0rad)
  Solid = true
  Symmetric = false
FEATURE [Part::Fillet] Fillet038  label="removeToCreateVentalationHoles001"
  Base = -> Extrude046
  Edges = <same value as first occurrence — deduplicated (x6 in doc)>
  Placement = pos=(7,0,0) rot=(0,0,1;0rad)
FEATURE [Sketcher::SketchObject] Sketch056  label="topSketch014"
  FullyConstrained = true
  sketch-geometry (22):
    g0: LineSegment StartX=5.21097e-06 StartY=3 StartZ=0 EndX=5.21097e-06 EndY=19 EndZ=0
    g1: ArcOfCircle CenterX=19 CenterY=19 CenterZ=0 NormalX=0 NormalY=0 NormalZ=1 AngleXU=0 Radius=19 StartAngle=1.5708 EndAngle=3.14159
    g2: ArcOfCircle CenterX=19 CenterY=19 CenterZ=0 NormalX=0 NormalY=0 NormalZ=1 AngleXU=0 Radius=16 StartAngle=1.5708 EndAngle=3.14159
    g3: LineSegment StartX=114 StartY=35 StartZ=0 EndX=19 EndY=35 EndZ=0
    g4: LineSegment StartX=5.21097e-06 StartY=3 StartZ=0 EndX=5.21097e-06 EndY=0 EndZ=0
    g5: LineSegment StartX=3 StartY=0 StartZ=0 EndX=5.21097e-06 EndY=0 EndZ=0
    g6: LineSegment StartX=3 StartY=19 StartZ=0 EndX=3 EndY=0 EndZ=0
    g7: LineSegment StartX=19 StartY=38 StartZ=0 EndX=124 EndY=38 EndZ=0
    g8: Circle CenterX=119 CenterY=35 CenterZ=0 NormalX=0 NormalY=0 NormalZ=1 AngleXU=0 Radius=1
    g9: Circle CenterX=121 CenterY=35 CenterZ=0 NormalX=0 NormalY=0 NormalZ=1 AngleXU=0 Radius=1
    g10: Circle CenterX=121 CenterY=33 CenterZ=0 NormalX=0 NormalY=0 NormalZ=1 AngleXU=0 Radius=1
    g11: BSplineCurve PolesCount=3 KnotsCount=2 Degree=2 IsPeriodic=0
    g12: GeomPoint X=119 Y=35 Z=0
    g13: GeomPoint X=121 Y=33 Z=0
    g14: LineSegment StartX=119 StartY=35 StartZ=0 EndX=114 EndY=35 EndZ=0
    g15: ArcOfCircle CenterX=105 CenterY=19 CenterZ=0 NormalX=0 NormalY=0 NormalZ=1 AngleXU=0 Radius=16 StartAngle=5.60905 EndAngle=6.28319
    g16: LineSegment StartX=121 StartY=33 StartZ=0 EndX=121 EndY=19 EndZ=0
    g17: LineSegment StartX=117.5 StartY=9.01251 StartZ=0 EndX=121.163 EndY=9.0125 EndZ=0
    g18: ArcOfCircle CenterX=105 CenterY=19 CenterZ=0 NormalX=0 NormalY=0 NormalZ=1 AngleXU=0 Radius=20.6155 StartAngle=5.7297 EndAngle=6.28319
    g19: LineSegment StartX=121.163 StartY=9.0125 StartZ=0 EndX=122.538 EndY=8.16329 EndZ=0
    g20: LineSegment StartX=124 StartY=38 StartZ=0 EndX=125.616 EndY=38 EndZ=0
    g21: LineSegment StartX=125.616 StartY=19 StartZ=0 EndX=125.616 EndY=38 EndZ=0
  constraints (49):
    c: Vertical(g0)
    c: Block(g0)
    c: Coincident(g1,g0)
    c: Block(g1)
    c: Coincident(g2,g1)
    c: Block(g2)
    c: Coincident(g3,g2)
    c: Horizontal(g3)
    c: Tangent(g3,g2)
    c: Coincident(g4,g0)
    c: Distance(g4) = 3
    c: Vertical(g4)
    c: Coincident(g5,g4)
    c: Horizontal(g5)
    c: Coincident(g6,g2)
    c: Coincident(g6,g5)
    c: Vertical(g6)
    c: Horizontal(g7)
    c: Distance(g7) = 105
    c: Coincident(g7,g1)
    c: Block(g3)
    c: Weight(g8) = 1
    c: Equal(g8,g9)
    c: Equal(g8,g10)
    c: InternalAlignment(g8,g11)
    c: InternalAlignment(g9,g11)
    c: InternalAlignment(g10,g11)
    c: InternalAlignment(g12,g11)
    c: InternalAlignment(g13,g11)
    c: Block(g11)
    c: Coincident(g14,g11)
    c: Coincident(g14,g3)
    c: Horizontal(g14)
    c: Block(g15)
    c: Coincident(g16,g11)
    c: Coincident(g16,g15)
    c: Vertical(g16)
    c: Distance(g16) = 14
    c: Coincident(g17,g15)
    c: Block(g18)
    c: Coincident(g19,g18)
    c: Coincident(g20,g7)
    c: Horizontal(g20)
    c: Vertical(g21)
    c: Coincident(g20,g21)
    c: Block(g20)
    c: Block(g21)
    c: Block(g19)
    c: Block(g17)
FEATURE [Part::Box] Box026  label="removeToCreteHoleForPlugHousing032"
  AttacherType = Attacher::AttachEngine3D
  Height = 28.6
  Length = 10
  Placement = pos=(-2,0,21.7) rot=(0,0,1;0rad)
  Width = 19
FEATURE [Part::Feature] Face109 .. Face112  x4 (patterned run collapsed; names and placements below)
  shape: bbox 3.5 x 17.8 x 2e-07 mm, 1 faces, 0 solids (baked)
FEATURE [Part::Revolution] Revolve117  label="removeToCreateScrewAndThreadedInsertHole045"
  Angle = 360
  Axis = (0,1,0)
  Base = (0,0,0)
  FaceMakerClass = Part::FaceMakerBullseye
  Placement = pos=(62.3,30.3,19.7) rot=(0,0,1;0rad)
  Solid = false
  Source = -> Face109
  Symmetric = false
FEATURE [Part::Revolution] Revolve118  label="removeToCreateScrewAndThreadedInsertHole046"
  Angle = 360
  Axis = (0,1,0)
  Base = (0,0,0)
  FaceMakerClass = Part::FaceMakerBullseye
  Placement = pos=(62.3,30.3,51.7) rot=(0,0,1;0rad)
  Solid = false
  Source = -> Face110
  Symmetric = false
FEATURE [Part::Revolution] Revolve119  label="removeToCreateScrewAndThreadedInsertHole047"
  Angle = 360
  Axis = (0,1,0)
  Base = (0,0,0)
  FaceMakerClass = Part::FaceMakerBullseye
  Placement = pos=(30.3,30.3,19.7) rot=(0,0,1;0rad)
  Solid = false
  Source = -> Face111
  Symmetric = false
FEATURE [Part::Revolution] Revolve120  label="removeToCreateScrewAndThreadedInsertHole048"
  Angle = 360
  Axis = (0,1,0)
  Base = (0,0,0)
  FaceMakerClass = Part::FaceMakerBullseye
  Placement = pos=(30.3,30.3,51.7) rot=(0,0,1;0rad)
  Solid = false
  Source = -> Face112
  Symmetric = false
FEATURE [Part::MultiFuse] Fusion087  label="createThreadedInsertHolesForFan005"
  Shapes = -> [Revolve117,Revolve118,Revolve119,Revolve120]
FEATURE [Part::Extrusion] Extrude047
  Base = -> Sketch056
  Dir = (0,0,1)
  DirMode = 2
  FaceMakerClass = Part::FaceMakerBullseye
  LengthFwd = 72
  LengthRev = 0
  Solid = true
  Symmetric = false
FEATURE [Part::Fillet] Fillet039  label="top019"
  Base = -> Extrude047
  Edges = 1 edges r=2: [Edge35]
FEATURE [Sketcher::SketchObject] Sketch057
  FullyConstrained = false
  Placement = pos=(0,0,0) rot=(1,0,0;1.5708rad)
  sketch-geometry (24):
    g0: ArcOfCircle CenterX=-4 CenterY=-10.5 CenterZ=0 NormalX=0 NormalY=0 NormalZ=1 AngleXU=0 Radius=1.5 StartAngle=6e-16 EndAngle=3.14159
    g1: ArcOfCircle CenterX=-34.2 CenterY=-10.5 CenterZ=0 NormalX=0 NormalY=0 NormalZ=1 AngleXU=0 Radius=1.5 StartAngle=0 EndAngle=3.14159
    g2: ArcOfCircle CenterX=-34.2 CenterY=-27.7 CenterZ=0 NormalX=0 NormalY=0 NormalZ=1 AngleXU=0 Radius=1.5 StartAngle=3.14159 EndAngle=6.28319
    g3: ArcOfCircle CenterX=-4 CenterY=-27.7 CenterZ=0 NormalX=0 NormalY=0 NormalZ=1 AngleXU=0 Radius=1.5 StartAngle=3.1416 EndAngle=6.28319
    g4: ArcOfCircle CenterX=-10 CenterY=-4.3 CenterZ=0 NormalX=0 NormalY=0 NormalZ=1 AngleXU=0 Radius=1.5 StartAngle=2e-16 EndAngle=3.14159
    g5: ArcOfCircle CenterX=-16.1 CenterY=-1.8 CenterZ=0 NormalX=0 NormalY=0 NormalZ=1 AngleXU=0 Radius=1.5 StartAngle=5e-16 EndAngle=3.14159
    g6: ArcOfCircle CenterX=-22.1 CenterY=-1.8 CenterZ=0 NormalX=0 NormalY=0 NormalZ=1 AngleXU=0 Radius=1.5 StartAngle=5e-16 EndAngle=3.14159
    g7: ArcOfCircle CenterX=-28.2 CenterY=-4.3 CenterZ=0 NormalX=0 NormalY=0 NormalZ=1 AngleXU=0 Radius=1.5 StartAngle=2e-16 EndAngle=3.14159
    g8: ArcOfCircle CenterX=-10 CenterY=-33.9 CenterZ=0 NormalX=0 NormalY=0 NormalZ=1 AngleXU=0 Radius=1.5 StartAngle=3.14159 EndAngle=6.28319
    g9: ArcOfCircle CenterX=-16.1 CenterY=-36.4 CenterZ=0 NormalX=0 NormalY=0 NormalZ=1 AngleXU=0 Radius=1.5 StartAngle=3.14159 EndAngle=6.28319
    g10: ArcOfCircle CenterX=-22.1 CenterY=-36.4 CenterZ=0 NormalX=0 NormalY=0 NormalZ=1 AngleXU=0 Radius=1.5 StartAngle=3.14159 EndAngle=6.28319
    g11: ArcOfCircle CenterX=-28.2 CenterY=-33.9 CenterZ=0 NormalX=0 NormalY=0 NormalZ=1 AngleXU=0 Radius=1.5 StartAngle=3.14159 EndAngle=6.28319
    g12: LineSegment StartX=-35.7 StartY=-10.5 StartZ=0 EndX=-35.7 EndY=-27.7 EndZ=0
    g13: LineSegment StartX=-32.7 StartY=-10.5 StartZ=0 EndX=-32.7 EndY=-27.7 EndZ=0
    g14: LineSegment StartX=-29.7 StartY=-33.9 StartZ=0 EndX=-29.7 EndY=-4.3 EndZ=0
    g15: LineSegment StartX=-26.7 StartY=-33.9 StartZ=0 EndX=-26.7 EndY=-4.3 EndZ=0
    g16: LineSegment StartX=-2.5 StartY=-10.5 StartZ=0 EndX=-2.5 EndY=-27.7 EndZ=0
    g17: LineSegment StartX=-8.5 StartY=-4.3 StartZ=0 EndX=-8.5 EndY=-33.9 EndZ=0
    g18: LineSegment StartX=-5.5 StartY=-10.5 StartZ=0 EndX=-5.5 EndY=-27.7 EndZ=0
    g19: LineSegment StartX=-11.5 StartY=-4.3 StartZ=0 EndX=-11.5 EndY=-33.9 EndZ=0
    g20: LineSegment StartX=-14.6 StartY=-1.8 StartZ=0 EndX=-14.6 EndY=-36.4 EndZ=0
    g21: LineSegment StartX=-17.6 StartY=-1.8 StartZ=0 EndX=-17.6 EndY=-36.4 EndZ=0
    g22: LineSegment StartX=-20.6 StartY=-36.4 StartZ=0 EndX=-20.6 EndY=-1.8 EndZ=0
    g23: LineSegment StartX=-23.6 StartY=-1.8 StartZ=0 EndX=-23.6 EndY=-36.4 EndZ=0
  constraints (48):
    c: Block(g0)
    c: Block(g1)
    c: Block(g2)
    c: Block(g3)
    c: Block(g4)
    c: Block(g5)
    c: Block(g6)
    c: Block(g7)
    c: Block(g8)
    c: Block(g9)
    c: Block(g10)
    c: Block(g11)
    c: Coincident(g12,g1)
    c: Coincident(g12,g2)
    c: Vertical(g12)
    c: Coincident(g13,g1)
    c: Coincident(g13,g2)
    c: Vertical(g13)
    c: Coincident(g14,g11)
    c: Coincident(g14,g7)
    c: Vertical(g14)
    c: Coincident(g15,g11)
    c: Coincident(g15,g7)
    c: Vertical(g15)
    c: Coincident(g16,g0)
    c: Coincident(g16,g3)
    c: Vertical(g16)
    c: Coincident(g17,g4)
    c: Coincident(g17,g8)
    c: Vertical(g17)
    c: Coincident(g18,g0)
    c: Coincident(g18,g3)
    c: Vertical(g18)
    c: Coincident(g19,g4)
    c: Coincident(g19,g8)
    c: Vertical(g19)
    c: Coincident(g20,g5)
    c: Coincident(g20,g9)
    c: Vertical(g20)
    c: Coincident(g21,g5)
    c: Coincident(g21,g9)
    c: Vertical(g21)
    c: Coincident(g22,g10)
    c: Coincident(g22,g6)
    c: Vertical(g22)
    c: Coincident(g23,g6)
    c: Coincident(g23,g10)
    c: Vertical(g23)
FEATURE [Part::Extrusion] Extrude048  label="removeToCreateFanGrillHoles004"
  Base = -> Sketch057
  Dir = (0,-1,6e-16)
  DirMode = 2
  FaceMakerClass = Part::FaceMakerBullseye
  LengthFwd = 10
  LengthRev = 0
  Placement = pos=(65.4,44,54.82) rot=(0,0,1;0rad)
  Solid = true
  Symmetric = false
FEATURE [Part::Cut] Cut040  label="top021"
  Base = -> Fillet039
  Tool = -> Extrude048
FEATURE [Part::Cylinder] Cylinder041  label="removeToCreteHoleForPlugHousing034"
  Angle = 360
  AttacherType = Attacher::AttachEngine3D
  Height = 20
  Placement = pos=(-2,19,36) rot=(0,1,0;1.5708rad)
  Radius = 14.3
FEATURE [Part::MultiFuse] Fusion089  label="removeToCreteHoleForPlugHousing035"
  Shapes = -> [Box026,Cylinder041]
FEATURE [Part::Cylinder] Cylinder042
  Angle = 360
  AttacherType = Attacher::AttachEngine3D
  Height = 20
  Placement = pos=(0,0,36.15) rot=(0,0,1;0rad)
  Radius = 14.3
FEATURE [Part::Cylinder] Cylinder043
  Angle = 360
  AttacherType = Attacher::AttachEngine3D
  Height = 10
  Placement = pos=(0,0,36.15) rot=(0,0,1;0rad)
  Radius = 4
FEATURE [Part::Box] Box027  label="removeToCreteHoleForPlugHousing036"
  AttacherType = Attacher::AttachEngine3D
  Height = 28.6
  Length = 20
  Placement = pos=(106.15,0,21.7) rot=(0,0,1;0rad)
  Width = 19
FEATURE [Part::Cut] Cut041  label="top022"
  Base = -> Cut040
  Tool = -> Fusion087
FEATURE [Part::Cut] Cut039  label="top020"
  Base = -> Cut041
  Tool = -> Fusion089
FEATURE [Part::MultiFuse] Fusion090  label="removeToCreteHoleForPlugHousing037"
  Placement = pos=(70,19,36) rot=(0,1,0;1.5708rad)
  Shapes = -> [Cylinder042,Cylinder043]
FEATURE [Part::MultiFuse] Fusion088  label="removeToCreteHoleForPlugHousing033"
  Shapes = -> [Box027,Fusion090]
FEATURE [Part::Cut] Cut042  label="removeToCreteHoleForPlugHousing038"
  Base = -> Cut039
  Tool = -> Fusion088
FEATURE [Part::MultiFuse] Fusion091  label="removeFromTop"
  Shapes = -> [Fillet038,Fusion085,Fusion084,Fusion083,Extrude045]
FEATURE [Part::Cut] Cut043  label="REAL TOP ====="
  Base = -> Fillet036
  Tool = -> Fusion091
FEATURE [Part::MultiFuse] Fusion092  label="caseScrewPillarBracket016"
  Shapes = -> [Extrude030,Extrude031,Extrude032,Extrude033,Extrude034,Extrude035,Extrude036,Extrude037,Box013,Box014]
FEATURE [Sketcher::SketchObject] Sketch058  label="topSketch015"
  FullyConstrained = true
  sketch-geometry (20):
    g0: LineSegment StartX=5.21097e-06 StartY=3 StartZ=0 EndX=5.21097e-06 EndY=19 EndZ=0
    g1: ArcOfCircle CenterX=19 CenterY=19 CenterZ=0 NormalX=0 NormalY=0 NormalZ=1 AngleXU=0 Radius=19 StartAngle=1.5708 EndAngle=3.14159
    g2: ArcOfCircle CenterX=19 CenterY=19 CenterZ=0 NormalX=0 NormalY=0 NormalZ=1 AngleXU=0 Radius=16 StartAngle=1.5708 EndAngle=3.14159
    g3: LineSegment StartX=114 StartY=35 StartZ=0 EndX=19 EndY=35 EndZ=0
    g4: LineSegment StartX=5.21097e-06 StartY=3 StartZ=0 EndX=5.21097e-06 EndY=0 EndZ=0
    g5: LineSegment StartX=3 StartY=0 StartZ=0 EndX=5.21097e-06 EndY=0 EndZ=0
    g6: LineSegment StartX=3 StartY=19 StartZ=0 EndX=3 EndY=0 EndZ=0
    g7: LineSegment StartX=19 StartY=38 StartZ=0 EndX=124 EndY=38 EndZ=0
    g8: Circle CenterX=119 CenterY=35 CenterZ=0 NormalX=0 NormalY=0 NormalZ=1 AngleXU=0 Radius=1
    g9: Circle CenterX=121 CenterY=35 CenterZ=0 NormalX=0 NormalY=0 NormalZ=1 AngleXU=0 Radius=1
    g10: Circle CenterX=121 CenterY=33 CenterZ=0 NormalX=0 NormalY=0 NormalZ=1 AngleXU=0 Radius=1
    g11: BSplineCurve PolesCount=3 KnotsCount=2 Degree=2 IsPeriodic=0
    g12: GeomPoint X=119 Y=35 Z=0
    g13: GeomPoint X=121 Y=33 Z=0
    g14: LineSegment StartX=119 StartY=35 StartZ=0 EndX=114 EndY=35 EndZ=0
    g15: ArcOfCircle CenterX=105 CenterY=19 CenterZ=0 NormalX=0 NormalY=0 NormalZ=1 AngleXU=0 Radius=19 StartAngle=5.7297 EndAngle=6.28319
    g16: ArcOfCircle CenterX=105 CenterY=19 CenterZ=0 NormalX=0 NormalY=0 NormalZ=1 AngleXU=0 Radius=16 StartAngle=5.60905 EndAngle=6.28319
    g17: LineSegment StartX=121 StartY=33 StartZ=0 EndX=121 EndY=19 EndZ=0
    g18: LineSegment StartX=124 StartY=38 StartZ=0 EndX=124 EndY=19 EndZ=0
    g19: LineSegment StartX=117.5 StartY=9.01251 StartZ=0 EndX=121.163 EndY=9.0125 EndZ=0
  constraints (46):
    c: Vertical(g0)
    c: Block(g0)
    c: Coincident(g1,g0)
    c: Block(g1)
    c: Coincident(g2,g1)
    c: Block(g2)
    c: Coincident(g3,g2)
    c: Horizontal(g3)
    c: Tangent(g3,g2)
    c: Coincident(g4,g0)
    c: Distance(g4) = 3
    c: Vertical(g4)
    c: Coincident(g5,g4)
    c: Horizontal(g5)
    c: Coincident(g6,g2)
    c: Coincident(g6,g5)
    c: Vertical(g6)
    c: Horizontal(g7)
    c: Distance(g7) = 105
    c: Coincident(g7,g1)
    c: Block(g3)
    c: Weight(g8) = 1
    c: Equal(g8,g9)
    c: Equal(g8,g10)
    c: InternalAlignment(g8,g11)
    c: InternalAlignment(g9,g11)
    c: InternalAlignment(g10,g11)
    c: InternalAlignment(g12,g11)
    c: InternalAlignment(g13,g11)
    c: Block(g11)
    c: Coincident(g14,g11)
    c: Coincident(g14,g3)
    c: Horizontal(g14)
    c: Block(g15)
    c: Coincident(g16,g15)
    c: Block(g16)
    c: Coincident(g17,g11)
    c: Coincident(g17,g16)
    c: Vertical(g17)
    c: Distance(g17) = 14
    c: Coincident(g18,g7)
    c: Coincident(g18,g15)
    c: Vertical(g18)
    c: Distance(g18) = 19
    c: Coincident(g19,g16)
    c: Coincident(g19,g15)
FEATURE [Part::Extrusion] Extrude049  label="top023"
  Base = -> Sketch058
  Dir = (0,0,1)
  DirMode = 2
  FaceMakerClass = Part::FaceMakerBullseye
  LengthFwd = 72
  LengthRev = 0
  Solid = true
  Symmetric = false
FEATURE [Sketcher::SketchObject] Sketch059
  FullyConstrained = true
  MapMode = 3
  Placement = pos=(0,0,0) rot=(1,0,0;1.5708rad)
  Support = -> [Extrude049]
  sketch-geometry (8):
    g0: Circle CenterX=80.351 CenterY=-67.6202 CenterZ=0 NormalX=0 NormalY=0 NormalZ=1 AngleXU=0 Radius=2
    g1: Circle CenterX=80.351 CenterY=-67.6202 CenterZ=0 NormalX=0 NormalY=0 NormalZ=1 AngleXU=0 Radius=3
    g2: Circle CenterX=80.351 CenterY=-4.92017 CenterZ=0 NormalX=0 NormalY=0 NormalZ=1 AngleXU=0 Radius=2
    g3: Circle CenterX=80.351 CenterY=-4.92017 CenterZ=0 NormalX=0 NormalY=0 NormalZ=1 AngleXU=0 Radius=3
    g4: Circle CenterX=23.851 CenterY=-4.92017 CenterZ=0 NormalX=0 NormalY=0 NormalZ=1 AngleXU=0 Radius=2
    g5: Circle CenterX=23.851 CenterY=-4.92017 CenterZ=0 NormalX=0 NormalY=0 NormalZ=1 AngleXU=0 Radius=3
    g6: Circle CenterX=23.851 CenterY=-67.6202 CenterZ=0 NormalX=0 NormalY=0 NormalZ=1 AngleXU=0 Radius=2
    g7: Circle CenterX=23.851 CenterY=-67.6202 CenterZ=0 NormalX=0 NormalY=0 NormalZ=1 AngleXU=0 Radius=3
  constraints (8):
    c: Block(g3)
    c: Block(g2)
    c: Block(g1)
    c: Block(g0)
    c: Block(g6)
    c: Block(g7)
    c: Block(g4)
    c: Block(g5)
FEATURE [Sketcher::SketchObject] Sketch060
  FullyConstrained = true
  MapMode = 3
  Placement = pos=(0,0,0) rot=(1,0,0;1.5708rad)
  Support = -> [Extrude049]
  sketch-geometry (8):
    g0: Circle CenterX=80.351 CenterY=-67.6202 CenterZ=0 NormalX=0 NormalY=0 NormalZ=1 AngleXU=0 Radius=3
    g1: Circle CenterX=80.351 CenterY=-4.92017 CenterZ=0 NormalX=0 NormalY=0 NormalZ=1 AngleXU=0 Radius=3
    g2: Circle CenterX=23.851 CenterY=-4.92017 CenterZ=0 NormalX=0 NormalY=0 NormalZ=1 AngleXU=0 Radius=3
    g3: Circle CenterX=23.851 CenterY=-67.6202 CenterZ=0 NormalX=0 NormalY=0 NormalZ=1 AngleXU=0 Radius=3
    g4: Circle CenterX=23.851 CenterY=-67.6202 CenterZ=0 NormalX=0 NormalY=0 NormalZ=1 AngleXU=0 Radius=5
    g5: Circle CenterX=80.351 CenterY=-67.6202 CenterZ=0 NormalX=0 NormalY=0 NormalZ=1 AngleXU=0 Radius=5
    g6: Circle CenterX=23.851 CenterY=-4.92017 CenterZ=0 NormalX=0 NormalY=0 NormalZ=1 AngleXU=0 Radius=5
    g7: Circle CenterX=80.351 CenterY=-4.92017 CenterZ=0 NormalX=0 NormalY=0 NormalZ=1 AngleXU=0 Radius=5
  constraints (8):
    c: Block(g1)
    c: Block(g0)
    c: Block(g3)
    c: Block(g2)
    c: Block(g5)
    c: Block(g4)
    c: Block(g6)
    c: Block(g7)
FEATURE [Sketcher::SketchObject] Sketch061
  FullyConstrained = true
  MapMode = 3
  Placement = pos=(0,0,0) rot=(1,0,0;1.5708rad)
  sketch-geometry (8):
    g0: Circle CenterX=80.351 CenterY=-67.6202 CenterZ=0 NormalX=0 NormalY=0 NormalZ=1 AngleXU=0 Radius=3
    g1: Circle CenterX=80.351 CenterY=-4.92017 CenterZ=0 NormalX=0 NormalY=0 NormalZ=1 AngleXU=0 Radius=3
    g2: Circle CenterX=23.851 CenterY=-4.92017 CenterZ=0 NormalX=0 NormalY=0 NormalZ=1 AngleXU=0 Radius=3
    g3: Circle CenterX=23.851 CenterY=-67.6202 CenterZ=0 NormalX=0 NormalY=0 NormalZ=1 AngleXU=0 Radius=3
    g4: Circle CenterX=23.851 CenterY=-67.6202 CenterZ=0 NormalX=0 NormalY=0 NormalZ=1 AngleXU=0 Radius=5
    g5: Circle CenterX=80.351 CenterY=-67.6202 CenterZ=0 NormalX=0 NormalY=0 NormalZ=1 AngleXU=0 Radius=5
    g6: Circle CenterX=23.851 CenterY=-4.92017 CenterZ=0 NormalX=0 NormalY=0 NormalZ=1 AngleXU=0 Radius=5
    g7: Circle CenterX=80.351 CenterY=-4.92017 CenterZ=0 NormalX=0 NormalY=0 NormalZ=1 AngleXU=0 Radius=5
  constraints (8):
    c: Block(g1)
    c: Block(g0)
    c: Block(g3)
    c: Block(g2)
    c: Block(g5)
    c: Block(g4)
    c: Block(g6)
    c: Block(g7)
FEATURE [Sketcher::SketchObject] Sketch062  label="topSketch016"
  FullyConstrained = true
  sketch-geometry (20):
    g0: LineSegment StartX=5.21097e-06 StartY=3 StartZ=0 EndX=5.21097e-06 EndY=19 EndZ=0
    g1: ArcOfCircle CenterX=19 CenterY=19 CenterZ=0 NormalX=0 NormalY=0 NormalZ=1 AngleXU=0 Radius=19 StartAngle=1.5708 EndAngle=3.14159
    g2: ArcOfCircle CenterX=19 CenterY=19 CenterZ=0 NormalX=0 NormalY=0 NormalZ=1 AngleXU=0 Radius=16 StartAngle=1.5708 EndAngle=3.14159
    g3: LineSegment StartX=114 StartY=35 StartZ=0 EndX=19 EndY=35 EndZ=0
    g4: LineSegment StartX=5.21097e-06 StartY=3 StartZ=0 EndX=5.21097e-06 EndY=0 EndZ=0
    g5: LineSegment StartX=3 StartY=0 StartZ=0 EndX=5.21097e-06 EndY=0 EndZ=0
    g6: LineSegment StartX=3 StartY=19 StartZ=0 EndX=3 EndY=0 EndZ=0
    g7: LineSegment StartX=19 StartY=38 StartZ=0 EndX=124 EndY=38 EndZ=0
    g8: Circle CenterX=119 CenterY=35 CenterZ=0 NormalX=0 NormalY=0 NormalZ=1 AngleXU=0 Radius=1
    g9: Circle CenterX=121 CenterY=35 CenterZ=0 NormalX=0 NormalY=0 NormalZ=1 AngleXU=0 Radius=1
    g10: Circle CenterX=121 CenterY=33 CenterZ=0 NormalX=0 NormalY=0 NormalZ=1 AngleXU=0 Radius=1
    g11: BSplineCurve PolesCount=3 KnotsCount=2 Degree=2 IsPeriodic=0
    g12: GeomPoint X=119 Y=35 Z=0
    g13: GeomPoint X=121 Y=33 Z=0
    g14: LineSegment StartX=119 StartY=35 StartZ=0 EndX=114 EndY=35 EndZ=0
    g15: ArcOfCircle CenterX=105 CenterY=19 CenterZ=0 NormalX=0 NormalY=0 NormalZ=1 AngleXU=0 Radius=19 StartAngle=5.7297 EndAngle=6.28319
    g16: ArcOfCircle CenterX=105 CenterY=19 CenterZ=0 NormalX=0 NormalY=0 NormalZ=1 AngleXU=0 Radius=16 StartAngle=5.60905 EndAngle=6.28319
    g17: LineSegment StartX=121 StartY=33 StartZ=0 EndX=121 EndY=19 EndZ=0
    g18: LineSegment StartX=124 StartY=38 StartZ=0 EndX=124 EndY=19 EndZ=0
    g19: LineSegment StartX=117.5 StartY=9.01251 StartZ=0 EndX=121.163 EndY=9.0125 EndZ=0
  constraints (46):
    c: Vertical(g0)
    c: Block(g0)
    c: Coincident(g1,g0)
    c: Block(g1)
    c: Coincident(g2,g1)
    c: Block(g2)
    c: Coincident(g3,g2)
    c: Horizontal(g3)
    c: Tangent(g3,g2)
    c: Coincident(g4,g0)
    c: Distance(g4) = 3
    c: Vertical(g4)
    c: Coincident(g5,g4)
    c: Horizontal(g5)
    c: Coincident(g6,g2)
    c: Coincident(g6,g5)
    c: Vertical(g6)
    c: Horizontal(g7)
    c: Distance(g7) = 105
    c: Coincident(g7,g1)
    c: Block(g3)
    c: Weight(g8) = 1
    c: Equal(g8,g9)
    c: Equal(g8,g10)
    c: InternalAlignment(g8,g11)
    c: InternalAlignment(g9,g11)
    c: InternalAlignment(g10,g11)
    c: InternalAlignment(g12,g11)
    c: InternalAlignment(g13,g11)
    c: Block(g11)
    c: Coincident(g14,g11)
    c: Coincident(g14,g3)
    c: Horizontal(g14)
    c: Block(g15)
    c: Coincident(g16,g15)
    c: Block(g16)
    c: Coincident(g17,g11)
    c: Coincident(g17,g16)
    c: Vertical(g17)
    c: Distance(g17) = 14
    c: Coincident(g18,g7)
    c: Coincident(g18,g15)
    c: Vertical(g18)
    c: Distance(g18) = 19
    c: Coincident(g19,g16)
    c: Coincident(g19,g15)
FEATURE [Part::Extrusion] Extrude053  label="top024"
  Base = -> Sketch062
  Dir = (0,0,1)
  DirMode = 2
  FaceMakerClass = Part::FaceMakerBullseye
  LengthFwd = 72
  LengthRev = 0
  Solid = true
  Symmetric = false
FEATURE [Sketcher::SketchObject] Sketch063
  FullyConstrained = true
  MapMode = 3
  Placement = pos=(0,0,0) rot=(1,0,0;1.5708rad)
  Support = -> [Extrude053]
  sketch-geometry (8):
    g0: Circle CenterX=80.351 CenterY=-67.6202 CenterZ=0 NormalX=0 NormalY=0 NormalZ=1 AngleXU=0 Radius=2
    g1: Circle CenterX=80.351 CenterY=-67.6202 CenterZ=0 NormalX=0 NormalY=0 NormalZ=1 AngleXU=0 Radius=3
    g2: Circle CenterX=80.351 CenterY=-4.92017 CenterZ=0 NormalX=0 NormalY=0 NormalZ=1 AngleXU=0 Radius=2
    g3: Circle CenterX=80.351 CenterY=-4.92017 CenterZ=0 NormalX=0 NormalY=0 NormalZ=1 AngleXU=0 Radius=3
    g4: Circle CenterX=23.851 CenterY=-4.92017 CenterZ=0 NormalX=0 NormalY=0 NormalZ=1 AngleXU=0 Radius=2
    g5: Circle CenterX=23.851 CenterY=-4.92017 CenterZ=0 NormalX=0 NormalY=0 NormalZ=1 AngleXU=0 Radius=3
    g6: Circle CenterX=23.851 CenterY=-67.6202 CenterZ=0 NormalX=0 NormalY=0 NormalZ=1 AngleXU=0 Radius=2
    g7: Circle CenterX=23.851 CenterY=-67.6202 CenterZ=0 NormalX=0 NormalY=0 NormalZ=1 AngleXU=0 Radius=3
  constraints (8):
    c: Block(g3)
    c: Block(g2)
    c: Block(g1)
    c: Block(g0)
    c: Block(g6)
    c: Block(g7)
    c: Block(g4)
    c: Block(g5)
FEATURE [Part::Extrusion] Extrude054
  Base = -> Sketch063
  Dir = (0,-1,2e-16)
  DirMode = 2
  FaceMakerClass = Part::FaceMakerBullseye
  LengthFwd = 6
  LengthRev = 0
  Placement = pos=(0,9,0) rot=(0,0,1;0rad)
  Solid = true
  Symmetric = false
FEATURE [Sketcher::SketchObject] Sketch064  label="topSketch017"
  FullyConstrained = true
  sketch-geometry (20):
    g0: LineSegment StartX=5.21097e-06 StartY=3 StartZ=0 EndX=5.21097e-06 EndY=19 EndZ=0
    g1: ArcOfCircle CenterX=19 CenterY=19 CenterZ=0 NormalX=0 NormalY=0 NormalZ=1 AngleXU=0 Radius=19 StartAngle=1.5708 EndAngle=3.14159
    g2: ArcOfCircle CenterX=19 CenterY=19 CenterZ=0 NormalX=0 NormalY=0 NormalZ=1 AngleXU=0 Radius=16 StartAngle=1.5708 EndAngle=3.14159
    g3: LineSegment StartX=114 StartY=35 StartZ=0 EndX=19 EndY=35 EndZ=0
    g4: LineSegment StartX=5.21097e-06 StartY=3 StartZ=0 EndX=5.21097e-06 EndY=0 EndZ=0
    g5: LineSegment StartX=3 StartY=0 StartZ=0 EndX=5.21097e-06 EndY=0 EndZ=0
    g6: LineSegment StartX=3 StartY=19 StartZ=0 EndX=3 EndY=0 EndZ=0
    g7: LineSegment StartX=19 StartY=38 StartZ=0 EndX=124 EndY=38 EndZ=0
    g8: Circle CenterX=119 CenterY=35 CenterZ=0 NormalX=0 NormalY=0 NormalZ=1 AngleXU=0 Radius=1
    g9: Circle CenterX=121 CenterY=35 CenterZ=0 NormalX=0 NormalY=0 NormalZ=1 AngleXU=0 Radius=1
    g10: Circle CenterX=121 CenterY=33 CenterZ=0 NormalX=0 NormalY=0 NormalZ=1 AngleXU=0 Radius=1
    g11: BSplineCurve PolesCount=3 KnotsCount=2 Degree=2 IsPeriodic=0
    g12: GeomPoint X=119 Y=35 Z=0
    g13: GeomPoint X=121 Y=33 Z=0
    g14: LineSegment StartX=119 StartY=35 StartZ=0 EndX=114 EndY=35 EndZ=0
    g15: ArcOfCircle CenterX=105 CenterY=19 CenterZ=0 NormalX=0 NormalY=0 NormalZ=1 AngleXU=0 Radius=19 StartAngle=5.7297 EndAngle=6.28319
    g16: ArcOfCircle CenterX=105 CenterY=19 CenterZ=0 NormalX=0 NormalY=0 NormalZ=1 AngleXU=0 Radius=16 StartAngle=5.60905 EndAngle=6.28319
    g17: LineSegment StartX=121 StartY=33 StartZ=0 EndX=121 EndY=19 EndZ=0
    g18: LineSegment StartX=124 StartY=38 StartZ=0 EndX=124 EndY=19 EndZ=0
    g19: LineSegment StartX=117.5 StartY=9.01251 StartZ=0 EndX=121.163 EndY=9.0125 EndZ=0
  constraints (46):
    c: Vertical(g0)
    c: Block(g0)
    c: Coincident(g1,g0)
    c: Block(g1)
    c: Coincident(g2,g1)
    c: Block(g2)
    c: Coincident(g3,g2)
    c: Horizontal(g3)
    c: Tangent(g3,g2)
    c: Coincident(g4,g0)
    c: Distance(g4) = 3
    c: Vertical(g4)
    c: Coincident(g5,g4)
    c: Horizontal(g5)
    c: Coincident(g6,g2)
    c: Coincident(g6,g5)
    c: Vertical(g6)
    c: Horizontal(g7)
    c: Distance(g7) = 105
    c: Coincident(g7,g1)
    c: Block(g3)
    c: Weight(g8) = 1
    c: Equal(g8,g9)
    c: Equal(g8,g10)
    c: InternalAlignment(g8,g11)
    c: InternalAlignment(g9,g11)
    c: InternalAlignment(g10,g11)
    c: InternalAlignment(g12,g11)
    c: InternalAlignment(g13,g11)
    c: Block(g11)
    c: Coincident(g14,g11)
    c: Coincident(g14,g3)
    c: Horizontal(g14)
    c: Block(g15)
    c: Coincident(g16,g15)
    c: Block(g16)
    c: Coincident(g17,g11)
    c: Coincident(g17,g16)
    c: Vertical(g17)
    c: Distance(g17) = 14
    c: Coincident(g18,g7)
    c: Coincident(g18,g15)
    c: Vertical(g18)
    c: Distance(g18) = 19
    c: Coincident(g19,g16)
    c: Coincident(g19,g15)
FEATURE [Sketcher::SketchObject] Sketch065
  FullyConstrained = true
  MapMode = 3
  Placement = pos=(0,0,0) rot=(1,0,0;1.5708rad)
  sketch-geometry (8):
    g0: Circle CenterX=80.351 CenterY=-67.6202 CenterZ=0 NormalX=0 NormalY=0 NormalZ=1 AngleXU=0 Radius=3
    g1: Circle CenterX=80.351 CenterY=-4.92017 CenterZ=0 NormalX=0 NormalY=0 NormalZ=1 AngleXU=0 Radius=3
    g2: Circle CenterX=23.851 CenterY=-4.92017 CenterZ=0 NormalX=0 NormalY=0 NormalZ=1 AngleXU=0 Radius=3
    g3: Circle CenterX=23.851 CenterY=-67.6202 CenterZ=0 NormalX=0 NormalY=0 NormalZ=1 AngleXU=0 Radius=3
    g4: Circle CenterX=23.851 CenterY=-67.6202 CenterZ=0 NormalX=0 NormalY=0 NormalZ=1 AngleXU=0 Radius=5
    g5: Circle CenterX=80.351 CenterY=-67.6202 CenterZ=0 NormalX=0 NormalY=0 NormalZ=1 AngleXU=0 Radius=5
    g6: Circle CenterX=23.851 CenterY=-4.92017 CenterZ=0 NormalX=0 NormalY=0 NormalZ=1 AngleXU=0 Radius=5
    g7: Circle CenterX=80.351 CenterY=-4.92017 CenterZ=0 NormalX=0 NormalY=0 NormalZ=1 AngleXU=0 Radius=5
  constraints (8):
    c: Block(g1)
    c: Block(g0)
    c: Block(g3)
    c: Block(g2)
    c: Block(g5)
    c: Block(g4)
    c: Block(g6)
    c: Block(g7)
FEATURE [Part::Extrusion] Extrude056
  Base = -> Sketch065
  Dir = (0,-1,2e-16)
  DirMode = 2
  FaceMakerClass = Part::FaceMakerBullseye
  LengthFwd = 2
  LengthRev = 0
  Solid = true
  Symmetric = false
FEATURE [Part::Extrusion] Extrude057  label="top025"
  Base = -> Sketch064
  Dir = (0,0,1)
  DirMode = 2
  FaceMakerClass = Part::FaceMakerBullseye
  LengthFwd = 72
  LengthRev = 0
  Solid = true
  Symmetric = false
FEATURE [Sketcher::SketchObject] Sketch066
  FullyConstrained = true
  MapMode = 3
  Placement = pos=(0,0,0) rot=(1,0,0;1.5708rad)
  Support = -> [Extrude057]
  sketch-geometry (8):
    g0: Circle CenterX=80.351 CenterY=-67.6202 CenterZ=0 NormalX=0 NormalY=0 NormalZ=1 AngleXU=0 Radius=3
    g1: Circle CenterX=80.351 CenterY=-4.92017 CenterZ=0 NormalX=0 NormalY=0 NormalZ=1 AngleXU=0 Radius=3
    g2: Circle CenterX=23.851 CenterY=-4.92017 CenterZ=0 NormalX=0 NormalY=0 NormalZ=1 AngleXU=0 Radius=3
    g3: Circle CenterX=23.851 CenterY=-67.6202 CenterZ=0 NormalX=0 NormalY=0 NormalZ=1 AngleXU=0 Radius=3
    g4: Circle CenterX=23.851 CenterY=-67.6202 CenterZ=0 NormalX=0 NormalY=0 NormalZ=1 AngleXU=0 Radius=5
    g5: Circle CenterX=80.351 CenterY=-67.6202 CenterZ=0 NormalX=0 NormalY=0 NormalZ=1 AngleXU=0 Radius=5
    g6: Circle CenterX=23.851 CenterY=-4.92017 CenterZ=0 NormalX=0 NormalY=0 NormalZ=1 AngleXU=0 Radius=5
    g7: Circle CenterX=80.351 CenterY=-4.92017 CenterZ=0 NormalX=0 NormalY=0 NormalZ=1 AngleXU=0 Radius=5
  constraints (8):
    c: Block(g1)
    c: Block(g0)
    c: Block(g3)
    c: Block(g2)
    c: Block(g5)
    c: Block(g4)
    c: Block(g6)
    c: Block(g7)
FEATURE [Part::Extrusion] Extrude055
  Base = -> Sketch066
  Dir = (0,-1,2e-16)
  DirMode = 2
  FaceMakerClass = Part::FaceMakerBullseye
  LengthFwd = 2
  LengthRev = 0
  Solid = true
  Symmetric = false
FEATURE [Part::Fillet] Fillet041
  Base = -> Extrude056
  Edges = 4 edges r=1.99: [Edge6,Edge12,Edge18,Edge24]
FEATURE [Part::Cut] Cut045
  Base = -> Extrude055
  Placement = pos=(0,6,0) rot=(0,0,1;0rad)
  Tool = -> Fillet041
FEATURE [Part::MultiFuse] Fusion095  label="pcbScrewPillars"
  Placement = pos=(-3.2,-1,72.3) rot=(0,0,1;0rad)
  Shapes = -> [Cut045,Extrude054]
FEATURE [Part::Feature] Face113
  shape: bbox 3.2 x 1.5 x 2e-07 mm, 1 faces, 0 solids (baked)
FEATURE [Part::Revolution] Revolve121  label="backCaseScrewRetainer002"
  Angle = 360
  Axis = (0,1,0)
  Base = (0,0,0)
  FaceMakerClass = Part::FaceMakerBullseye
  Placement = pos=(12.5,3,62) rot=(0,0,1;0rad)
  Solid = false
  Source = -> Face113
  Symmetric = false
FEATURE [Part::Feature] Face114
  shape: bbox 3.2 x 1.5 x 2e-07 mm, 1 faces, 0 solids (baked)
FEATURE [Part::Feature] Face115
  shape: bbox 3.2 x 1.5 x 2e-07 mm, 1 faces, 0 solids (baked)
FEATURE [Part::Feature] Face116
  shape: bbox 3.2 x 1.5 x 2e-07 mm, 1 faces, 0 solids (baked)
FEATURE [Part::Revolution] Revolve122  label="frontCaseScrewRetainer004"
  Angle = 360
  Axis = (0,1,0)
  Base = (0,0,0)
  FaceMakerClass = Part::FaceMakerBullseye
  Placement = pos=(89.5,3,68.5) rot=(0,0,1;0rad)
  Solid = false
  Source = -> Face115
  Symmetric = false
FEATURE [Part::Revolution] Revolve123  label="frontCaseScrewRetainer005"
  Angle = 360
  Axis = (0,1,0)
  Base = (0,0,0)
  FaceMakerClass = Part::FaceMakerBullseye
  Placement = pos=(89.5,3,3.5) rot=(0,0,1;0rad)
  Solid = false
  Source = -> Face116
  Symmetric = false
FEATURE [Part::Revolution] Revolve124  label="backCaseScrewRetainer003"
  Angle = 360
  Axis = (0,1,0)
  Base = (0,0,0)
  FaceMakerClass = Part::FaceMakerBullseye
  Placement = pos=(12.5,3,10) rot=(0,0,1;0rad)
  Solid = false
  Source = -> Face114
  Symmetric = false
FEATURE [Part::Feature] Face117
  shape: bbox 3.6 x 3.2 x 2e-07 mm, 1 faces, 0 solids (baked)
FEATURE [Part::Revolution] Revolve125  label="moreFrontCaseScrewRetainer004"
  Angle = 360
  Axis = (0,1,0)
  Base = (0,0,0)
  FaceMakerClass = Part::FaceMakerBullseye
  Placement = pos=(109.5,4.5,68.5) rot=(0,0,1;0rad)
  Solid = false
  Source = -> Face117
  Symmetric = false
FEATURE [Part::Feature] Face118
  shape: bbox 3.6 x 3.2 x 2e-07 mm, 1 faces, 0 solids (baked)
FEATURE [Part::Revolution] Revolve126  label="moreFrontCaseScrewRetainer005"
  Angle = 360
  Axis = (0,1,0)
  Base = (0,0,0)
  FaceMakerClass = Part::FaceMakerBullseye
  Placement = pos=(109.5,4.5,3.5) rot=(0,0,1;0rad)
  Solid = false
  Source = -> Face118
  Symmetric = false
FEATURE [Part::MultiFuse] Fusion096  label="screwRetainers001"
  Shapes = -> [Revolve126,Revolve125,Revolve124,Revolve123,Revolve122,Revolve121]
FEATURE [Part::Feature] Face119
  shape: bbox 10 x 16.5 x 2e-07 mm, 1 faces, 0 solids (baked)
FEATURE [Part::Revolution] Revolve130  label="plugHousing050"
  Angle = 360
  Axis = (0,1,0)
  Base = (0,0,0)
  FaceMakerClass = Part::FaceMakerBullseye
  Placement = pos=(0,0,36.15) rot=(0,0,1;0rad)
  Solid = false
  Source = -> Face119
  Symmetric = false
FEATURE [Part::Feature] Face120
  shape: bbox 10 x 16.5 x 2e-07 mm, 1 faces, 0 solids (baked)
FEATURE [Part::Feature] Face121
  shape: bbox 10 x 16.5 x 2e-07 mm, 1 faces, 0 solids (baked)
FEATURE [Part::Revolution] Revolve127  label="plugHousing047"
  Angle = 360
  Axis = (0,1,0)
  Base = (0,0,0)
  FaceMakerClass = Part::FaceMakerBullseye
  Placement = pos=(0,0,36.15) rot=(0,0,1;0rad)
  Solid = false
  Source = -> Face121
  Symmetric = false
FEATURE [Part::Feature] Face122
  shape: bbox 10 x 16.5 x 2e-07 mm, 1 faces, 0 solids (baked)
FEATURE [Part::Feature] Face123
  shape: bbox 10 x 16.5 x 2e-07 mm, 1 faces, 0 solids (baked)
FEATURE [Part::Revolution] Revolve128  label="plugHousing048"
  Angle = 360
  Axis = (0,1,0)
  Base = (0,0,0)
  FaceMakerClass = Part::FaceMakerBullseye
  Placement = pos=(0,0,36.15) rot=(0,0,1;0rad)
  Solid = false
  Source = -> Face123
  Symmetric = false
FEATURE [Part::MultiFuse] Fusion100  label="plugHousing054"
  Placement = pos=(0,0,0) rot=(0,0,1;1.5708rad)
  Shapes = -> [Revolve130,Revolve128]
FEATURE [Part::Feature] Face124
  shape: bbox 10 x 16.5 x 2e-07 mm, 1 faces, 0 solids (baked)
FEATURE [Part::Feature] Face125
  shape: bbox 10 x 16.5 x 2e-07 mm, 1 faces, 0 solids (baked)
FEATURE [Part::Revolution] Revolve129  label="plugHousing049"
  Angle = 360
  Axis = (0,1,0)
  Base = (0,0,0)
  FaceMakerClass = Part::FaceMakerBullseye
  Placement = pos=(0,0,36.15) rot=(0,0,1;0rad)
  Solid = false
  Source = -> Face125
  Symmetric = false
FEATURE [Part::Feature] Face126
  shape: bbox 10 x 16.5 x 2e-07 mm, 1 faces, 0 solids (baked)
FEATURE [Part::Revolution] Revolve131  label="plugHousing058"
  Angle = 360
  Axis = (0,1,0)
  Base = (0,0,0)
  FaceMakerClass = Part::FaceMakerBullseye
  Placement = pos=(0,0,36.15) rot=(0,0,1;0rad)
  Solid = false
  Source = -> Face120
  Symmetric = false
FEATURE [Part::MultiFuse] Fusion099  label="plugHousing053"
  Placement = pos=(0,0,0) rot=(0,0,1;1.5708rad)
  Shapes = -> [Revolve127,Revolve131]
FEATURE [Part::MultiFuse] Fusion102  label="plugHousing056"
  Placement = pos=(0,19,0) rot=(0,0,1;3.14159rad)
  Shapes = -> [Fusion100,Fusion099]
FEATURE [Part::Revolution] Revolve132  label="plugHousing059"
  Angle = 360
  Axis = (0,1,0)
  Base = (0,0,0)
  FaceMakerClass = Part::FaceMakerBullseye
  Placement = pos=(0,0,36.15) rot=(0,0,1;0rad)
  Solid = false
  Source = -> Face126
  Symmetric = false
FEATURE [Part::Revolution] Revolve133  label="plugHousing060"
  Angle = 360
  Axis = (0,1,0)
  Base = (0,0,0)
  FaceMakerClass = Part::FaceMakerBullseye
  Placement = pos=(0,0,36.15) rot=(0,0,1;0rad)
  Solid = false
  Source = -> Face122
  Symmetric = false
FEATURE [Part::MultiFuse] Fusion097  label="plugHousing051"
  Placement = pos=(0,0,0) rot=(0,0,1;1.5708rad)
  Shapes = -> [Revolve133,Revolve132]
FEATURE [Part::Revolution] Revolve134  label="plugHousing061"
  Angle = 360
  Axis = (0,1,0)
  Base = (0,0,0)
  FaceMakerClass = Part::FaceMakerBullseye
  Placement = pos=(0,0,36.15) rot=(0,0,1;0rad)
  Solid = false
  Source = -> Face124
  Symmetric = false
FEATURE [Part::MultiFuse] Fusion101  label="plugHousing055"
  Placement = pos=(0,0,0) rot=(0,0,1;1.5708rad)
  Shapes = -> [Revolve129,Revolve134]
FEATURE [Part::MultiFuse] Fusion098  label="plugHousing052"
  Placement = pos=(0,19,0) rot=(0,0,1;3.14159rad)
  Shapes = -> [Fusion097,Fusion101]
FEATURE [Part::MultiFuse] Fusion103  label="plugHousing057"
  Placement = pos=(122.621,0,-0.15) rot=(0,0,1;0rad)
  Shapes = -> [Fusion102,Fusion098]
FEATURE [Part::Box] Box028  label="Cube015"
  AttacherType = Attacher::AttachEngine3D
  Height = 28
  Length = 3
  Placement = pos=(110.7,19,22) rot=(0,0,1;0rad)
  Width = 15.7
FEATURE [Part::Cylinder] Cylinder044
  Angle = 360
  AttacherType = Attacher::AttachEngine3D
  Height = 20
  Placement = pos=(0,0,36.15) rot=(0,0,1;0rad)
  Radius = 10.3
FEATURE [Part::Cylinder] Cylinder045
  Angle = 360
  AttacherType = Attacher::AttachEngine3D
  Height = 10
  Placement = pos=(0,0,36.15) rot=(0,0,1;0rad)
  Radius = 4
FEATURE [Part::MultiFuse] Fusion104  label="removeToCreteHoleForPlugHousing040"
  Placement = pos=(70,19,36) rot=(0,1,0;1.5708rad)
  Shapes = -> [Cylinder044,Cylinder045]
FEATURE [Part::Cut] Cut046  label="plugHousingTab003"
  Base = -> Box028
  Tool = -> Fusion104
FEATURE [Part::MultiFuse] Fusion105  label="plugHousing062"
  Shapes = -> [Fusion103,Cut046]
FEATURE [Part::Fillet] Fillet042
  Base = -> Fusion105
  Edges = 1 edges r=2: [Edge25]
FEATURE [Part::Fillet] Fillet043  label="plugHousing063"
  Base = -> Fillet042
  Edges = 1 edges r=2: [Edge8]
  Placement = pos=(7,0,0) rot=(0,0,1;0rad)
FEATURE [Part::Feature] Face127
  shape: bbox 10 x 16.5 x 2e-07 mm, 1 faces, 0 solids (baked)
FEATURE [Part::Feature] Face128
  shape: bbox 10 x 16.5 x 2e-07 mm, 1 faces, 0 solids (baked)
FEATURE [Part::Revolution] Revolve137  label="plugHousing070"
  Angle = 360
  Axis = (0,1,0)
  Base = (0,0,0)
  FaceMakerClass = Part::FaceMakerBullseye
  Placement = pos=(0,0,36.15) rot=(0,0,1;0rad)
  Solid = false
  Source = -> Face127
  Symmetric = false
FEATURE [Part::Revolution] Revolve140  label="plugHousing073"
  Angle = 360
  Axis = (0,1,0)
  Base = (0,0,0)
  FaceMakerClass = Part::FaceMakerBullseye
  Placement = pos=(0,0,36.15) rot=(0,0,1;0rad)
  Solid = false
  Source = -> Face128
  Symmetric = false
FEATURE [Part::Feature] Face129
  shape: bbox 10 x 16.5 x 2e-07 mm, 1 faces, 0 solids (baked)
FEATURE [Part::Revolution] Revolve138  label="plugHousing071"
  Angle = 360
  Axis = (0,1,0)
  Base = (0,0,0)
  FaceMakerClass = Part::FaceMakerBullseye
  Placement = pos=(0,0,36.15) rot=(0,0,1;0rad)
  Solid = false
  Source = -> Face129
  Symmetric = false
FEATURE [Part::Feature] Face130
  shape: bbox 10 x 16.5 x 2e-07 mm, 1 faces, 0 solids (baked)
FEATURE [Part::Revolution] Revolve139  label="plugHousing072"
  Angle = 360
  Axis = (0,1,0)
  Base = (0,0,0)
  FaceMakerClass = Part::FaceMakerBullseye
  Placement = pos=(0,0,36.15) rot=(0,0,1;0rad)
  Solid = false
  Source = -> Face130
  Symmetric = false
FEATURE [Part::Feature] Face131
  shape: bbox 10 x 16.5 x 2e-07 mm, 1 faces, 0 solids (baked)
FEATURE [Part::Revolution] Revolve135  label="plugHousing068"
  Angle = 360
  Axis = (0,1,0)
  Base = (0,0,0)
  FaceMakerClass = Part::FaceMakerBullseye
  Placement = pos=(0,0,36.15) rot=(0,0,1;0rad)
  Solid = false
  Source = -> Face131
  Symmetric = false
FEATURE [Part::MultiFuse] Fusion112  label="plugHousing078"
  Placement = pos=(0,0,0) rot=(0,0,1;1.5708rad)
  Shapes = -> [Revolve135,Revolve139]
FEATURE [Part::Feature] Face132
  shape: bbox 10 x 16.5 x 2e-07 mm, 1 faces, 0 solids (baked)
FEATURE [Part::Revolution] Revolve141  label="plugHousing074"
  Angle = 360
  Axis = (0,1,0)
  Base = (0,0,0)
  FaceMakerClass = Part::FaceMakerBullseye
  Placement = pos=(0,0,36.15) rot=(0,0,1;0rad)
  Solid = false
  Source = -> Face132
  Symmetric = false
FEATURE [Part::MultiFuse] Fusion110  label="plugHousing076"
  Placement = pos=(0,0,0) rot=(0,0,1;1.5708rad)
  Shapes = -> [Revolve141,Revolve140]
FEATURE [Part::Feature] Face133
  shape: bbox 10 x 16.5 x 2e-07 mm, 1 faces, 0 solids (baked)
FEATURE [Part::Revolution] Revolve136  label="plugHousing069"
  Angle = 360
  Axis = (0,1,0)
  Base = (0,0,0)
  FaceMakerClass = Part::FaceMakerBullseye
  Placement = pos=(0,0,36.15) rot=(0,0,1;0rad)
  Solid = false
  Source = -> Face133
  Symmetric = false
FEATURE [Part::MultiFuse] Fusion106  label="plugHousing064"
  Placement = pos=(0,0,0) rot=(0,0,1;1.5708rad)
  Shapes = -> [Revolve138,Revolve136]
FEATURE [Part::MultiFuse] Fusion108  label="plugHousing066"
  Placement = pos=(0,19,0) rot=(0,0,1;3.14159rad)
  Shapes = -> [Fusion106,Fusion112]
FEATURE [Part::Feature] Face134
  shape: bbox 10 x 16.5 x 2e-07 mm, 1 faces, 0 solids (baked)
FEATURE [Part::Revolution] Revolve142  label="plugHousing075"
  Angle = 360
  Axis = (0,1,0)
  Base = (0,0,0)
  FaceMakerClass = Part::FaceMakerBullseye
  Placement = pos=(0,0,36.15) rot=(0,0,1;0rad)
  Solid = false
  Source = -> Face134
  Symmetric = false
FEATURE [Part::MultiFuse] Fusion107  label="plugHousing065"
  Placement = pos=(0,0,0) rot=(0,0,1;1.5708rad)
  Shapes = -> [Revolve137,Revolve142]
FEATURE [Part::MultiFuse] Fusion111  label="plugHousing077"
  Placement = pos=(0,19,0) rot=(0,0,1;3.14159rad)
  Shapes = -> [Fusion110,Fusion107]
FEATURE [Part::MultiFuse] Fusion109  label="plugHousing067"
  Placement = pos=(131.236,0,-0.15) rot=(0,0,1;0rad)
  Shapes = -> [Fusion108,Fusion111]
FEATURE [Part::MultiFuse] Fusion113  label="plugHousing079"
  Shapes = -> [Fillet043,Fusion109]
FEATURE [Part::Feature] Face135
  shape: bbox 3.5 x 17.8 x 2e-07 mm, 1 faces, 0 solids (baked)
FEATURE [Part::Revolution] Revolve143  label="removeToCreateScrewAndThreadedInsertHole049"
  Angle = 360
  Axis = (0,1,0)
  Base = (0,0,0)
  FaceMakerClass = Part::FaceMakerBullseye
  Placement = pos=(12.5,0,10) rot=(0,0,1;0rad)
  Solid = false
  Source = -> Face135
  Symmetric = false
FEATURE [Part::Feature] Face136
  shape: bbox 3.5 x 17.8 x 2e-07 mm, 1 faces, 0 solids (baked)
FEATURE [Part::Revolution] Revolve144  label="removeToCreateScrewAndThreadedInsertHole050"
  Angle = 360
  Axis = (0,1,0)
  Base = (0,0,0)
  FaceMakerClass = Part::FaceMakerBullseye
  Placement = pos=(12.5,0,62) rot=(0,0,1;0rad)
  Solid = false
  Source = -> Face136
  Symmetric = false
FEATURE [Part::Feature] Face137
  shape: bbox 3.5 x 17.8 x 2e-07 mm, 1 faces, 0 solids (baked)
FEATURE [Part::Revolution] Revolve145  label="removeToCreateScrewAndThreadedInsertHole051"
  Angle = 360
  Axis = (0,1,0)
  Base = (0,0,0)
  FaceMakerClass = Part::FaceMakerBullseye
  Placement = pos=(89.5,0,68.5) rot=(0,0,1;0rad)
  Solid = false
  Source = -> Face137
  Symmetric = false
FEATURE [Part::Feature] Face138
  shape: bbox 3.5 x 17.8 x 2e-07 mm, 1 faces, 0 solids (baked)
FEATURE [Part::Revolution] Revolve146  label="removeToCreateScrewAndThreadedInsertHole052"
  Angle = 360
  Axis = (0,1,0)
  Base = (0,0,0)
  FaceMakerClass = Part::FaceMakerBullseye
  Placement = pos=(89.5,0,3.5) rot=(0,0,1;0rad)
  Solid = false
  Source = -> Face138
  Symmetric = false
FEATURE [Part::Feature] Face139
  shape: bbox 3.5 x 17.8 x 2e-07 mm, 1 faces, 0 solids (baked)
FEATURE [Part::Revolution] Revolve147  label="removeToCreateScrewAndThreadedInsertHole053"
  Angle = 360
  Axis = (0,1,0)
  Base = (0,0,0)
  FaceMakerClass = Part::FaceMakerBullseye
  Placement = pos=(109.5,4.7,3.5) rot=(0,0,1;0rad)
  Solid = false
  Source = -> Face139
  Symmetric = false
FEATURE [Part::Feature] Face140
  shape: bbox 3.5 x 17.8 x 2e-07 mm, 1 faces, 0 solids (baked)
FEATURE [Part::Revolution] Revolve148  label="removeToCreateScrewAndThreadedInsertHole054"
  Angle = 360
  Axis = (0,1,0)
  Base = (0,0,0)
  FaceMakerClass = Part::FaceMakerBullseye
  Placement = pos=(109.5,4.7,68.5) rot=(0,0,1;0rad)
  Solid = false
  Source = -> Face140
  Symmetric = false
FEATURE [Part::MultiFuse] Fusion114  label="removeToCreateScrewAndThreadedInsertHole055"
  Shapes = -> [Revolve148,Revolve147,Revolve146,Revolve145,Revolve144,Revolve143]
FEATURE [Part::Cut] Cut047  label="casePillars004"
  Base = -> Cut037
  Tool = -> Fusion114
FEATURE [Part::Feature] Face141
  shape: bbox 3.5 x 17.8 x 2e-07 mm, 1 faces, 0 solids (baked)
FEATURE [Part::Feature] Face142
  shape: bbox 3.5 x 17.8 x 2e-07 mm, 1 faces, 0 solids (baked)
FEATURE [Part::Feature] Face143
  shape: bbox 3.5 x 17.8 x 2e-07 mm, 1 faces, 0 solids (baked)
FEATURE [Part::Revolution] Revolve149  label="removeToCreateScrewAndThreadedInsertHole057"
  Angle = 360
  Axis = (0,1,0)
  Base = (0,0,0)
  FaceMakerClass = Part::FaceMakerBullseye
  Placement = pos=(12.5,0,10) rot=(0,0,1;0rad)
  Solid = false
  Source = -> Face141
  Symmetric = false
FEATURE [Part::Feature] Face144
  shape: bbox 3.5 x 17.8 x 2e-07 mm, 1 faces, 0 solids (baked)
FEATURE [Part::Feature] Face145
  shape: bbox 3.5 x 17.8 x 2e-07 mm, 1 faces, 0 solids (baked)
FEATURE [Part::Feature] Face146
  shape: bbox 3.5 x 17.8 x 2e-07 mm, 1 faces, 0 solids (baked)
FEATURE [Part::Revolution] Revolve150  label="removeToCreateScrewAndThreadedInsertHole058"
  Angle = 360
  Axis = (0,1,0)
  Base = (0,0,0)
  FaceMakerClass = Part::FaceMakerBullseye
  Placement = pos=(12.5,0,62) rot=(0,0,1;0rad)
  Solid = false
  Source = -> Face146
  Symmetric = false
FEATURE [Part::Revolution] Revolve151  label="removeToCreateScrewAndThreadedInsertHole059"
  Angle = 360
  Axis = (0,1,0)
  Base = (0,0,0)
  FaceMakerClass = Part::FaceMakerBullseye
  Placement = pos=(89.5,0,68.5) rot=(0,0,1;0rad)
  Solid = false
  Source = -> Face143
  Symmetric = false
FEATURE [Part::Revolution] Revolve152  label="removeToCreateScrewAndThreadedInsertHole060"
  Angle = 360
  Axis = (0,1,0)
  Base = (0,0,0)
  FaceMakerClass = Part::FaceMakerBullseye
  Placement = pos=(89.5,0,3.5) rot=(0,0,1;0rad)
  Solid = false
  Source = -> Face142
  Symmetric = false
FEATURE [Part::Revolution] Revolve153  label="removeToCreateScrewAndThreadedInsertHole061"
  Angle = 360
  Axis = (0,1,0)
  Base = (0,0,0)
  FaceMakerClass = Part::FaceMakerBullseye
  Placement = pos=(109.5,4.7,3.5) rot=(0,0,1;0rad)
  Solid = false
  Source = -> Face145
  Symmetric = false
FEATURE [Part::Revolution] Revolve154  label="removeToCreateScrewAndThreadedInsertHole062"
  Angle = 360
  Axis = (0,1,0)
  Base = (0,0,0)
  FaceMakerClass = Part::FaceMakerBullseye
  Placement = pos=(109.5,4.7,68.5) rot=(0,0,1;0rad)
  Solid = false
  Source = -> Face144
  Symmetric = false
FEATURE [Part::MultiFuse] Fusion115  label="removeToCreateScrewAndThreadedInsertHole056"
  Shapes = -> [Revolve154,Revolve153,Revolve152,Revolve151,Revolve150,Revolve149]
FEATURE [Part::Feature] Face147
  shape: bbox 9.8 x 26.5 x 2e-07 mm, 1 faces, 0 solids (baked)
FEATURE [Part::Revolution] Revolve155
  Angle = 360
  Axis = (0,1,0)
  Base = (0,0,0)
  FaceMakerClass = Part::FaceMakerBullseye
  Placement = pos=(0,0,0) rot=(0,0,1;1.5708rad)
  Solid = false
  Source = -> Face147
  Symmetric = false
FEATURE [Part::Feature] Face148
  shape: bbox 9.8 x 26.5 x 2e-07 mm, 1 faces, 0 solids (baked)
FEATURE [Part::Revolution] Revolve156
  Angle = 360
  Axis = (0,1,0)
  Base = (0,0,0)
  FaceMakerClass = Part::FaceMakerBullseye
  Placement = pos=(0,0,0) rot=(0,0,1;1.5708rad)
  Solid = false
  Source = -> Face148
  Symmetric = false
FEATURE [Part::MultiFuse] Fusion116
  Placement = pos=(-18,19,36) rot=(0,0,1;0rad)
  Shapes = -> [Revolve156,Revolve155]
FEATURE [Part::Box] Box029  label="Cube016"
  AttacherType = Attacher::AttachEngine3D
  Height = 28
  Length = 3
  Placement = pos=(110.7,19,22) rot=(0,0,1;0rad)
  Width = 15.7
FEATURE [Part::Cylinder] Cylinder046
  Angle = 360
  AttacherType = Attacher::AttachEngine3D
  Height = 10
  Placement = pos=(0,0,36.15) rot=(0,0,1;0rad)
  Radius = 4
FEATURE [Part::Cylinder] Cylinder047
  Angle = 360
  AttacherType = Attacher::AttachEngine3D
  Height = 20
  Placement = pos=(0,0,36.15) rot=(0,0,1;0rad)
  Radius = 10.3
FEATURE [Part::MultiFuse] Fusion117  label="removeToCreteHoleForPlugHousing041"
  Placement = pos=(70,19,36) rot=(0,1,0;1.5708rad)
  Shapes = -> [Cylinder047,Cylinder046]
FEATURE [Part::Cut] Cut049  label="plugHousingTab004"
  Base = -> Box029
  Placement = pos=(-107.4,-14,0) rot=(0,0,1;0rad)
  Tool = -> Fusion117
FEATURE [Part::Box] Box030  label="Cube017"
  AttacherType = Attacher::AttachEngine3D
  Height = 28
  Length = 3
  Placement = pos=(110.7,19,22) rot=(0,0,1;0rad)
  Width = 15.7
FEATURE [Part::Cylinder] Cylinder048
  Angle = 360
  AttacherType = Attacher::AttachEngine3D
  Height = 10
  Placement = pos=(0,0,36.15) rot=(0,0,1;0rad)
  Radius = 4
FEATURE [Part::Cylinder] Cylinder049
  Angle = 360
  AttacherType = Attacher::AttachEngine3D
  Height = 20
  Placement = pos=(0,0,36.15) rot=(0,0,1;0rad)
  Radius = 10.3
FEATURE [Part::MultiFuse] Fusion118  label="removeToCreteHoleForPlugHousing042"
  Placement = pos=(70,19,36) rot=(0,1,0;1.5708rad)
  Shapes = -> [Cylinder049,Cylinder048]
FEATURE [Part::Cut] Cut050  label="plugHousingTab005"
  Base = -> Box030
  Placement = pos=(-107.4,-14,0) rot=(0,0,1;0rad)
  Tool = -> Fusion118
FEATURE [Part::MultiFuse] Fusion119
  Placement = pos=(9.6,23,0) rot=(0,0,1;3.14159rad)
  Shapes = -> [Cut049,Cut050]
FEATURE [Part::Box] Box031  label="Cube018"
  AttacherType = Attacher::AttachEngine3D
  Height = 10
  Length = 3
  Placement = pos=(3.3,4,12) rot=(0,0,1;0rad)
  Width = 10
FEATURE [Part::Fillet] Fillet044
  Base = -> Box031
  Edges = 1 edges r=2: [Edge11]
FEATURE [Part::Box] Box032  label="Cube019"
  AttacherType = Attacher::AttachEngine3D
  Height = 10
  Length = 3
  Placement = pos=(3.3,4,50) rot=(0,0,1;0rad)
  Width = 10
FEATURE [Part::Fillet] Fillet045
  Base = -> Box032
  Edges = 1 edges r=2: [Edge12]
FEATURE [Part::Box] Box033  label="Cube020"
  AttacherType = Attacher::AttachEngine3D
  Height = 28
  Length = 4
  Placement = pos=(5,0,22) rot=(0,0,1;0rad)
  Width = 10
FEATURE [Part::Fillet] Fillet046
  Base = -> Box033
  Edges = 1 edges r=1: [Edge7]
FEATURE [Part::Fillet] Fillet047
  Base = -> Fillet046
  Edges = 1 edges r=2: [Edge5]
FEATURE [Part::Fillet] Fillet048
  Base = -> Fillet047
  Edges = 1 edges r=2: [Edge2]
FEATURE [Part::Cylinder] Cylinder050
  Angle = 360
  AttacherType = Attacher::AttachEngine3D
  Height = 20
  Placement = pos=(0,0,36.15) rot=(0,0,1;0rad)
  Radius = 8.2
FEATURE [Part::Cylinder] Cylinder051
  Angle = 360
  AttacherType = Attacher::AttachEngine3D
  Height = 10
  Placement = pos=(0,0,36.15) rot=(0,0,1;0rad)
  Radius = 4
FEATURE [Part::MultiFuse] Fusion120  label="removeToCreteHoleForPlugHousing043"
  Placement = pos=(-42,19,36) rot=(0,1,0;1.5708rad)
  Shapes = -> [Cylinder050,Cylinder051]
FEATURE [Sketcher::SketchObject] Sketch067  label="topSketch018"
  FullyConstrained = true
  sketch-geometry (4):
    g0: LineSegment StartX=16.8446 StartY=31.512 StartZ=0 EndX=16.3251 EndY=34.4666 EndZ=0
    g1: ArcOfCircle CenterX=19 CenterY=19.2524 CenterZ=0 NormalX=0 NormalY=0 NormalZ=1 AngleXU=0 Radius=15.4476 StartAngle=1.74483 EndAngle=2.72717
    g2: ArcOfCircle CenterX=19 CenterY=19.2524 CenterZ=0 NormalX=0 NormalY=0 NormalZ=1 AngleXU=0 Radius=12.4476 StartAngle=1.74483 EndAngle=2.73189
    g3: LineSegment StartX=4.86004 StartY=25.4725 StartZ=0 EndX=7.58253 EndY=24.2107 EndZ=0
  constraints (7):
    c: Block(g0)
    c: Coincident(g1,g0)
    c: Coincident(g2,g0)
    c: Coincident(g3,g1)
    c: Coincident(g3,g2)
    c: Block(g1)
    c: Block(g2)
FEATURE [Part::Extrusion] Extrude058
  Base = -> Sketch067
  Dir = (0,0,1)
  DirMode = 2
  FaceMakerClass = Part::FaceMakerBullseye
  LengthFwd = 10
  LengthRev = 0
  Placement = pos=(0,0,31) rot=(0,0,1;0rad)
  Solid = true
  Symmetric = false
FEATURE [Part::Cut] Cut051
  Base = -> Extrude058
  Tool = -> Fusion120
FEATURE [Part::Fillet] Fillet049
  Base = -> Cut051
  Edges = 1 edges r=2: [Edge1]
FEATURE [Part::Fillet] Fillet050
  Base = -> Fillet049
  Edges = 1 edges r=2.5: [Edge1]
FEATURE [Part::Fillet] Fillet051
  Base = -> Fillet050
  Edges = 1 edges r=2.5: [Edge2]
FEATURE [Part::MultiFuse] Fusion121  label="wireHolder003"
  Shapes = -> [Fusion116,Fillet051]
FEATURE [Part::MultiFuse] Fusion122
  Shapes = -> [Fillet045,Fusion121]
FEATURE [Part::MultiFuse] Fusion123  label="wireHolder004"
  Shapes = -> [Fusion122,Fillet048]
FEATURE [Part::MultiFuse] Fusion124  label="wireHolder005"
  Shapes = -> [Fillet044,Fusion119,Fusion123]
FEATURE [Sketcher::SketchObject] Sketch068  label="topSketch019"
  FullyConstrained = true
  sketch-geometry (6):
    g0: LineSegment StartX=19 StartY=38 StartZ=0 EndX=117 EndY=38 EndZ=0
    g1: ArcOfCircle CenterX=19 CenterY=19 CenterZ=0 NormalX=0 NormalY=0 NormalZ=1 AngleXU=0 Radius=19 StartAngle=1.5708 EndAngle=3.14159
    g2: LineSegment StartX=117 StartY=38 StartZ=0 EndX=117 EndY=19 EndZ=0
    g3: LineSegment StartX=98 StartY=1.0161e-12 StartZ=0 EndX=5.22862e-06 EndY=1.0161e-12 EndZ=0
    g4: LineSegment StartX=5.22862e-06 StartY=19 StartZ=0 EndX=5.22862e-06 EndY=1.0161e-12 EndZ=0
    g5: ArcOfCircle CenterX=98 CenterY=19 CenterZ=0 NormalX=0 NormalY=0 NormalZ=1 AngleXU=0 Radius=19 StartAngle=4.71239 EndAngle=6.28319
  constraints (16):
    c: Horizontal(g0)
    c: Distance(g0) = 98
    c: Coincident(g1,g0)
    c: Block(g1)
    c: Coincident(g2,g0)
    c: Vertical(g2)
    c: Distance(g2) = 19
    c: Horizontal(g3)
    c: Coincident(g4,g1)
    c: Vertical(g4)
    c: Coincident(g3,g4)
    c: Block(g3)
    c: Coincident(g5,g2)
    c: Coincident(g5,g3)
    c: Block(g0)
    c: Block(g5)
FEATURE [Part::Extrusion] Extrude059  label="sideA002"
  Base = -> Sketch068
  Dir = (0,0,1)
  DirMode = 2
  FaceMakerClass = Part::FaceMakerBullseye
  LengthFwd = 3
  LengthRev = 0
  Placement = pos=(0,0,-2.7) rot=(0,0,1;0rad)
  Solid = true
  Symmetric = false
FEATURE [Sketcher::SketchObject] Sketch069  label="topSketch020"
  FullyConstrained = true
  sketch-geometry (6):
    g0: LineSegment StartX=19 StartY=38 StartZ=0 EndX=117 EndY=38 EndZ=0
    g1: ArcOfCircle CenterX=19 CenterY=19 CenterZ=0 NormalX=0 NormalY=0 NormalZ=1 AngleXU=0 Radius=19 StartAngle=1.5708 EndAngle=3.14159
    g2: LineSegment StartX=117 StartY=38 StartZ=0 EndX=117 EndY=19 EndZ=0
    g3: LineSegment StartX=98 StartY=1.0161e-12 StartZ=0 EndX=5.22862e-06 EndY=1.0161e-12 EndZ=0
    g4: LineSegment StartX=5.22862e-06 StartY=19 StartZ=0 EndX=5.22862e-06 EndY=1.0161e-12 EndZ=0
    g5: ArcOfCircle CenterX=98 CenterY=19 CenterZ=0 NormalX=0 NormalY=0 NormalZ=1 AngleXU=0 Radius=19 StartAngle=4.71239 EndAngle=6.28319
  constraints (16):
    c: Horizontal(g0)
    c: Distance(g0) = 98
    c: Coincident(g1,g0)
    c: Block(g1)
    c: Coincident(g2,g0)
    c: Vertical(g2)
    c: Distance(g2) = 19
    c: Horizontal(g3)
    c: Coincident(g4,g1)
    c: Vertical(g4)
    c: Coincident(g3,g4)
    c: Block(g3)
    c: Coincident(g5,g2)
    c: Coincident(g5,g3)
    c: Block(g0)
    c: Block(g5)
FEATURE [Part::Extrusion] Extrude060  label="sideB002"
  Base = -> Sketch069
  Dir = (0,0,1)
  DirMode = 2
  FaceMakerClass = Part::FaceMakerBullseye
  LengthFwd = 3
  LengthRev = 0
  Placement = pos=(0,0,71.7) rot=(0,0,1;0rad)
  Solid = true
  Symmetric = false
FEATURE [Part::MultiFuse] Fusion127  label="removeFromBottom001"
  Placement = pos=(2,0,0) rot=(0,0,1;0rad)
  Shapes = -> [Extrude059,Extrude060]
FEATURE [Part::Cylinder] Cylinder052
  Angle = 360
  AttacherType = Attacher::AttachEngine3D
  Height = 20
  Placement = pos=(0,0,36.15) rot=(0,0,1;0rad)
  Radius = 14
FEATURE [Part::Cylinder] Cylinder053
  Angle = 360
  AttacherType = Attacher::AttachEngine3D
  Height = 10
  Placement = pos=(0,0,36.15) rot=(0,0,1;0rad)
  Radius = 4
FEATURE [Part::MultiFuse] Fusion128  label="removeToCreteHoleForPlugHousing044"
  Placement = pos=(70,19,36) rot=(0,1,0;1.5708rad)
  Shapes = -> [Cylinder052,Cylinder053]
FEATURE [Part::Cut] Cut052  label="bottom011"
  Base = -> Extrude043
  Tool = -> Fusion128
FEATURE [Part::Cut] Cut054  label="bottom012"
  Base = -> Cut052
  Tool = -> Fusion115
FEATURE [Sketcher::SketchObject] Sketch070
  FullyConstrained = true
  Placement = pos=(117,19,0) rot=(0.57735,0.57735,0.57735;2.0944rad)
  sketch-geometry (48):
    g0: LineSegment StartX=-49.19 StartY=69.25 StartZ=0 EndX=-49.19 EndY=66.25 EndZ=0
    g1: LineSegment StartX=-49.19 StartY=63.5 StartZ=0 EndX=-49.19 EndY=60.5 EndZ=0
    g2: LineSegment StartX=-49.19 StartY=57.75 StartZ=0 EndX=-49.19 EndY=54.75 EndZ=0
    g3: LineSegment StartX=-49.19 StartY=52 StartZ=0 EndX=-49.19 EndY=49 EndZ=0
    g4: LineSegment StartX=-49.19 StartY=46.25 StartZ=0 EndX=-49.19 EndY=43.25 EndZ=0
    g5: LineSegment StartX=-49.19 StartY=40.5 StartZ=0 EndX=-49.19 EndY=37.5 EndZ=0
    g6: LineSegment StartX=-49.19 StartY=34.5 StartZ=0 EndX=-49.19 EndY=31.5 EndZ=0
    g7: LineSegment StartX=-49.19 StartY=28.75 StartZ=0 EndX=-49.19 EndY=25.75 EndZ=0
    g8: LineSegment StartX=-49.19 StartY=23 StartZ=0 EndX=-49.19 EndY=20 EndZ=0
    g9: LineSegment StartX=-49.19 StartY=17.25 StartZ=0 EndX=-49.19 EndY=14.25 EndZ=0
    g10: LineSegment StartX=-49.19 StartY=11.5 StartZ=0 EndX=-49.19 EndY=8.5 EndZ=0
    g11: LineSegment StartX=-49.19 StartY=5.75 StartZ=0 EndX=-49.19 EndY=2.75 EndZ=0
    g12: ArcOfCircle CenterX=-1.5 CenterY=67.75 CenterZ=0 NormalX=0 NormalY=0 NormalZ=1 AngleXU=0 Radius=1.5 StartAngle=4.71239 EndAngle=7.85398
    g13: ArcOfCircle CenterX=-1.5 CenterY=62 CenterZ=0 NormalX=0 NormalY=0 NormalZ=1 AngleXU=0 Radius=1.5 StartAngle=4.71239 EndAngle=7.85398
    g14: ArcOfCircle CenterX=-1.5 CenterY=56.25 CenterZ=0 NormalX=0 NormalY=0 NormalZ=1 AngleXU=0 Radius=1.5 StartAngle=4.71239 EndAngle=7.85398
    g15: ArcOfCircle CenterX=-11.49 CenterY=50.5 CenterZ=0 NormalX=0 NormalY=0 NormalZ=1 AngleXU=0 Radius=1.5 StartAngle=4.71239 EndAngle=7.85398
    g16: ArcOfCircle CenterX=-16.28 CenterY=44.75 CenterZ=0 NormalX=0 NormalY=0 NormalZ=1 AngleXU=0 Radius=1.5 StartAngle=4.71239 EndAngle=7.85398
    g17: ArcOfCircle CenterX=-18.2337 CenterY=39 CenterZ=0 NormalX=0 NormalY=0 NormalZ=1 AngleXU=0 Radius=1.5 StartAngle=4.71485 EndAngle=7.85398
    g18: ArcOfCircle CenterX=-16.2837 CenterY=27.25 CenterZ=0 NormalX=0 NormalY=0 NormalZ=1 AngleXU=0 Radius=1.5 StartAngle=4.71485 EndAngle=7.85398
    g19: ArcOfCircle CenterX=-18.2337 CenterY=33 CenterZ=0 NormalX=0 NormalY=0 NormalZ=1 AngleXU=0 Radius=1.5 StartAngle=4.71485 EndAngle=7.85398
    g20: ArcOfCircle CenterX=-11.49 CenterY=21.5 CenterZ=0 NormalX=0 NormalY=0 NormalZ=1 AngleXU=0 Radius=1.5 StartAngle=4.71239 EndAngle=7.85398
    g21: ArcOfCircle CenterX=-1.5 CenterY=4.25 CenterZ=0 NormalX=0 NormalY=0 NormalZ=1 AngleXU=0 Radius=1.5 StartAngle=4.71239 EndAngle=7.85398
    g22: ArcOfCircle CenterX=-1.5 CenterY=10 CenterZ=0 NormalX=0 NormalY=0 NormalZ=1 AngleXU=0 Radius=1.5 StartAngle=4.71239 EndAngle=7.85398
    g23: ArcOfCircle CenterX=-1.5 CenterY=15.75 CenterZ=0 NormalX=0 NormalY=0 NormalZ=1 AngleXU=0 Radius=1.5 StartAngle=4.71239 EndAngle=7.85398
    g24: LineSegment StartX=-49.19 StartY=69.25 StartZ=0 EndX=-1.5 EndY=69.25 EndZ=0
    g25: LineSegment StartX=-49.19 StartY=66.25 StartZ=0 EndX=-1.5 EndY=66.25 EndZ=0
    g26: LineSegment StartX=-49.19 StartY=63.5 StartZ=0 EndX=-1.5 EndY=63.5 EndZ=0
    g27: LineSegment StartX=-49.19 StartY=60.5 StartZ=0 EndX=-1.5 EndY=60.5 EndZ=0
    g28: LineSegment StartX=-49.19 StartY=57.75 StartZ=0 EndX=-1.5 EndY=57.75 EndZ=0
    g29: LineSegment StartX=-49.19 StartY=54.75 StartZ=0 EndX=-1.5 EndY=54.75 EndZ=0
    g30: LineSegment StartX=-49.19 StartY=52 StartZ=0 EndX=-11.49 EndY=52 EndZ=0
    g31: LineSegment StartX=-49.19 StartY=49 StartZ=0 EndX=-11.49 EndY=49 EndZ=0
    g32: LineSegment StartX=-49.19 StartY=46.25 StartZ=0 EndX=-16.28 EndY=46.25 EndZ=0
    g33: LineSegment StartX=-49.19 StartY=43.25 StartZ=0 EndX=-16.28 EndY=43.25 EndZ=0
    g34: LineSegment StartX=-49.19 StartY=40.5 StartZ=0 EndX=-18.2337 EndY=40.5 EndZ=0
    g35: LineSegment StartX=-49.19 StartY=37.5 StartZ=0 EndX=-18.23 EndY=37.5 EndZ=0
    g36: LineSegment StartX=-49.19 StartY=34.5 StartZ=0 EndX=-18.2337 EndY=34.5 EndZ=0
    g37: LineSegment StartX=-49.19 StartY=31.5 StartZ=0 EndX=-18.23 EndY=31.5 EndZ=0
    g38: LineSegment StartX=-49.19 StartY=28.75 StartZ=0 EndX=-16.2837 EndY=28.75 EndZ=0
    g39: LineSegment StartX=-49.19 StartY=25.75 StartZ=0 EndX=-16.28 EndY=25.75 EndZ=0
    g40: LineSegment StartX=-49.19 StartY=23 StartZ=0 EndX=-11.49 EndY=23 EndZ=0
    g41: LineSegment StartX=-49.19 StartY=20 StartZ=0 EndX=-11.49 EndY=20 EndZ=0
    g42: LineSegment StartX=-49.19 StartY=17.25 StartZ=0 EndX=-1.5 EndY=17.25 EndZ=0
    g43: LineSegment StartX=-49.19 StartY=14.25 StartZ=0 EndX=-1.5 EndY=14.25 EndZ=0
    g44: LineSegment StartX=-49.19 StartY=11.5 StartZ=0 EndX=-1.5 EndY=11.5 EndZ=0
    g45: LineSegment StartX=-49.19 StartY=8.5 StartZ=0 EndX=-1.5 EndY=8.5 EndZ=0
    g46: LineSegment StartX=-49.19 StartY=5.75 StartZ=0 EndX=-1.5 EndY=5.75 EndZ=0
    g47: LineSegment StartX=-49.19 StartY=2.75 StartZ=0 EndX=-1.5 EndY=2.75 EndZ=0
  constraints (120):
    c: Vertical(g0)
    c: Distance(g0) = 3
    c: Block(g0)
    c: Vertical(g1)
    c: Distance(g1) = 3
    c: Vertical(g2)
    c: Equal(g0,g2) = 3
    c: Block(g2)
    c: Vertical(g3)
    c: Equal(g1,g3) = 3
    c: Vertical(g4)
    c: Equal(g0,g4) = 3
    c: Block(g4)
    c: Vertical(g5)
    c: Equal(g1,g5) = 3
    c: Vertical(g6)
    c: Equal(g0,g6) = 3
    c: Block(g6)
    c: Vertical(g7)
    c: Equal(g1,g7) = 3
    c: Vertical(g8)
    c: Equal(g0,g8) = 3
    c: Block(g8)
    c: Vertical(g9)
    c: Equal(g1,g9) = 3
    c: Vertical(g10)
    c: Equal(g0,g10) = 3
    c: Block(g10)
    c: Vertical(g11)
    c: Equal(g1,g11) = 3
    c: Block(g12)
    c: Block(g13)
    c: Block(g14)
    c: Block(g15)
    c: Block(g16)
    c: Block(g17)
    c: Block(g18)
    c: Block(g19)
    c: Block(g20)
    c: Block(g21)
    c: Block(g22)
    c: Block(g23)
    c: Block(g11)
    c: Block(g9)
    c: Block(g7)
    c: Block(g5)
    c: Block(g3)
    c: Block(g1)
    c: Coincident(g24,g0)
    c: Coincident(g24,g12)
    c: Horizontal(g24)
    c: Coincident(g25,g0)
    c: Coincident(g25,g12)
    c: Horizontal(g25)
    c: Coincident(g26,g1)
    c: Coincident(g26,g13)
    c: Horizontal(g26)
    c: Coincident(g27,g1)
    c: Coincident(g27,g13)
    c: Horizontal(g27)
    c: Coincident(g28,g2)
    c: Coincident(g28,g14)
    c: Horizontal(g28)
    c: Coincident(g29,g2)
    c: Coincident(g29,g14)
    c: Horizontal(g29)
    c: Coincident(g30,g3)
    c: Coincident(g30,g15)
    c: Horizontal(g30)
    c: Coincident(g31,g3)
    c: Coincident(g31,g15)
    c: Horizontal(g31)
    c: Coincident(g32,g4)
    c: Coincident(g32,g16)
    c: Horizontal(g32)
    c: Coincident(g33,g4)
    c: Coincident(g33,g16)
    c: Horizontal(g33)
    c: Coincident(g34,g5)
    c: Coincident(g34,g17)
    c: Horizontal(g34)
    c: Coincident(g35,g5)
    c: Coincident(g35,g17)
    c: Horizontal(g35)
    c: Coincident(g36,g6)
    c: Coincident(g36,g19)
    c: Horizontal(g36)
    c: Coincident(g37,g6)
    c: Coincident(g37,g19)
    c: Horizontal(g37)
    c: Coincident(g38,g7)
    c: Coincident(g38,g18)
    c: Horizontal(g38)
    c: Coincident(g39,g7)
    c: Coincident(g39,g18)
    c: Horizontal(g39)
    c: Coincident(g40,g8)
    c: Coincident(g40,g20)
    c: Horizontal(g40)
    c: Coincident(g41,g8)
    c: Coincident(g41,g20)
    c: Horizontal(g41)
    c: Coincident(g42,g9)
    c: Coincident(g42,g23)
    c: Horizontal(g42)
    c: Coincident(g43,g9)
    c: Coincident(g43,g23)
    c: Horizontal(g43)
    c: Coincident(g44,g10)
    c: Coincident(g44,g22)
    c: Horizontal(g44)
    c: Coincident(g45,g10)
    c: Coincident(g45,g22)
    c: Horizontal(g45)
    c: Coincident(g46,g11)
    c: Coincident(g46,g21)
    c: Horizontal(g46)
    c: Coincident(g47,g11)
    c: Coincident(g47,g21)
    c: Horizontal(g47)
FEATURE [Part::Extrusion] Extrude061
  Base = -> Sketch070
  Dir = (1,0,0)
  DirMode = 2
  FaceMakerClass = Part::FaceMakerBullseye
  LengthFwd = 23
  LengthRev = 0
  Placement = pos=(-19,0,0) rot=(0,0,1;0rad)
  Solid = true
  Symmetric = false
FEATURE [Part::Fillet] Fillet052  label="removeToCreateVentalationHoles002"
  Base = -> Extrude061
  Edges = <same value as first occurrence — deduplicated (x6 in doc)>
  Placement = pos=(7,0.02,0) rot=(0,0,1;0rad)
FEATURE [Part::MultiFuse] Fusion130  label="bottom013"
  Shapes = -> [Cut054,Cut034]
FEATURE [Part::Cut] Cut055
  Base = -> Fusion130
  Tool = -> Fillet052
FEATURE [Part::Cylinder] Cylinder054
  Angle = 360
  AttacherType = Attacher::AttachEngine3D
  Height = 20
  Placement = pos=(0,0,36.15) rot=(0,0,1;0rad)
  Radius = 4
FEATURE [Sketcher::SketchObject] Sketch071  label="bottomSketch002"
  FullyConstrained = true
  sketch-geometry (32):
    g0: LineSegment StartX=3.3 StartY=-6.03275e-07 StartZ=0 EndX=98 EndY=-6.03275e-07 EndZ=0
    g1: ArcOfCircle CenterX=98 CenterY=19 CenterZ=0 NormalX=0 NormalY=0 NormalZ=1 AngleXU=0 Radius=19 StartAngle=4.71239 EndAngle=5.71103
    g2: LineSegment StartX=6.3 StartY=8 StartZ=0 EndX=3.3 EndY=8 EndZ=0
    g3: LineSegment StartX=3.3 StartY=8 StartZ=0 EndX=3.3 EndY=-6.03275e-07 EndZ=0
    g4: ArcOfCircle CenterX=8.3 CenterY=5 CenterZ=0 NormalX=0 NormalY=0 NormalZ=1 AngleXU=0 Radius=2 StartAngle=3.14159 EndAngle=4.71239
    g5: LineSegment StartX=6.3 StartY=8 StartZ=0 EndX=6.3 EndY=5 EndZ=0
    g6: ArcOfCircle CenterX=98 CenterY=19 CenterZ=0 NormalX=0 NormalY=0 NormalZ=1 AngleXU=0 Radius=12.7 StartAngle=4.71239 EndAngle=6.28319
    g7: LineSegment StartX=94.7 StartY=3 StartZ=0 EndX=8.3 EndY=3 EndZ=0
    g8-g12: Circle x5 (B-spline internal-alignment scaffolding for g13; pole/knot coordinates omitted)
    g13: BSplineCurve PolesCount=5 KnotsCount=3 Degree=3 IsPeriodic=0
    g14: GeomPoint X=98 Y=6.3 Z=0
    g15: GeomPoint X=96.3938 Y=4.71946 Z=0
    g16: GeomPoint X=94.7 Y=3 Z=0
    g17-g23: Circle x7 (B-spline internal-alignment scaffolding for g24; pole/knot coordinates omitted)
    g24: BSplineCurve PolesCount=7 KnotsCount=5 Degree=3 IsPeriodic=0
    g25-g29: GeomPoint x5 (B-spline internal-alignment scaffolding for g24; pole/knot coordinates omitted)
    g30: ArcOfCircle CenterX=98 CenterY=19 CenterZ=0 NormalX=0 NormalY=0 NormalZ=1 AngleXU=0 Radius=15.7 StartAngle=5.81226 EndAngle=6.28319
    g31: LineSegment StartX=110.7 StartY=19 StartZ=0 EndX=113.7 EndY=19 EndZ=0
  constraints (41):
    c: Horizontal(g0)
    c: Coincident(g1,g0)
    c: Block(g1)
    c: Horizontal(g2)
    c: Distance(g2) = 3
    c: Coincident(g3,g2)
    c: Vertical(g3)
    c: Coincident(g3,g0)
    c: Block(g4)
    c: Block(g2)
    c: Coincident(g5,g2)
    c: Coincident(g5,g4)
    c: Vertical(g5)
    c: Coincident(g6,g1)
    c: Block(g6)
    c: Coincident(g7,g4)
    c: Horizontal(g7)
    c: Block(g0)
    c: Block(g7)
    c: Block(g3)
    c: Coincident(g13,g6)
    c: Weight(g8) = 1
    c: Equal(g8, g9-g12) x4
    c: Coincident(g13,g7)
    c: InternalAlignment(g8-g12 -> g13) x5
    c: InternalAlignment(g14,g13)
    c: InternalAlignment(g15,g13)
    c: InternalAlignment(g16,g13)
    c: Block(g13)
    c: Weight(g17) = 1
    c: Equal(g17, g18-g23) x6
    c: Coincident(g24,g1)
    c: InternalAlignment(g17-g23 -> g24) x7
    c: InternalAlignment(g25-g29 -> g24) x5
    c: Block(g24)
    c: Coincident(g30,g24)
    c: Coincident(g31,g6)
    c: Coincident(g31,g30)
    c: Horizontal(g31)
    c: Block(g31)
    c: Block(g30)
FEATURE [Part::Extrusion] Extrude062  label="bottom014"
  Base = -> Sketch071
  Dir = (0,0,1)
  DirMode = 2
  FaceMakerClass = Part::FaceMakerBullseye
  LengthFwd = 71.4
  LengthRev = 0
  Placement = pos=(0,0,0.3) rot=(0,0,1;0rad)
  Solid = true
  Symmetric = false
FEATURE [Part::Fillet] Fillet054
  Base = -> Extrude062
  Edges = 1 edges r=2.4: [Edge17]
FEATURE [Part::Fillet] Fillet055  label="bottom015"
  Base = -> Fillet054
  Edges = 1 edges r=2.4: [Edge36]
FEATURE [Part::Cylinder] Cylinder055
  Angle = 360
  AttacherType = Attacher::AttachEngine3D
  Height = 10
  Placement = pos=(0,0,36.15) rot=(0,0,1;0rad)
  Radius = 4
FEATURE [Part::MultiFuse] Fusion131  label="removeToCreateHoleForPlugHousing002"
  Placement = pos=(70,19,36.15) rot=(0,1,0;1.5708rad)
  Shapes = -> [Cylinder054,Cylinder055]
FEATURE [Part::Cut] Cut056  label="Bottom001"
  Base = -> Fillet055
  Placement = pos=(9,0,0) rot=(0,0,1;0rad)
  Tool = -> Fusion131
FEATURE [Part::Cut] Cut057
  Base = -> Cut055
  Tool = -> Cut056
FEATURE [Sketcher::SketchObject] Sketch072  label="topSketch021"
  FullyConstrained = true
  sketch-geometry (4):
    g0: ArcOfCircle CenterX=105 CenterY=19 CenterZ=0 NormalX=0 NormalY=0 NormalZ=1 AngleXU=0 Radius=20.6155 StartAngle=5.54125 EndAngle=6.28319
    g1: ArcOfCircle CenterX=105 CenterY=19 CenterZ=0 NormalX=0 NormalY=0 NormalZ=1 AngleXU=0 Radius=13 StartAngle=5.54125 EndAngle=6.28319
    g2: LineSegment StartX=118 StartY=19 StartZ=0 EndX=125.616 EndY=19 EndZ=0
    g3: LineSegment StartX=114.583 StartY=10.2157 StartZ=0 EndX=120.197 EndY=5.06982 EndZ=0
  constraints (7):
    c: Block(g0)
    c: Block(g1)
    c: Coincident(g2,g1)
    c: Coincident(g2,g0)
    c: Horizontal(g2)
    c: Coincident(g3,g1)
    c: Coincident(g3,g0)
FEATURE [Part::Extrusion] Extrude063  label="bottomPlugHousingBit003"
  Base = -> Sketch072
  Dir = (0,0,1)
  DirMode = 2
  FaceMakerClass = Part::FaceMakerBullseye
  LengthFwd = 72
  LengthRev = 0
  Solid = true
  Symmetric = false
FEATURE [Part::Cylinder] Cylinder056
  Angle = 360
  AttacherType = Attacher::AttachEngine3D
  Height = 20
  Placement = pos=(0,0,36.15) rot=(0,0,1;0rad)
  Radius = 14.3
FEATURE [Part::Cylinder] Cylinder057
  Angle = 360
  AttacherType = Attacher::AttachEngine3D
  Height = 10
  Placement = pos=(0,0,36.15) rot=(0,0,1;0rad)
  Radius = 4
FEATURE [Part::Box] Box034  label="removeToCreteHoleForPlugHousing047"
  AttacherType = Attacher::AttachEngine3D
  Height = 28.6
  Length = 20
  Placement = pos=(106.15,0,21.7) rot=(0,0,1;0rad)
  Width = 19
FEATURE [Part::Cylinder] Cylinder058
  Angle = 360
  AttacherType = Attacher::AttachEngine3D
  Height = 20
  Placement = pos=(0,0,36.15) rot=(0,0,1;0rad)
  Radius = 14.3
FEATURE [Part::Cylinder] Cylinder059
  Angle = 360
  AttacherType = Attacher::AttachEngine3D
  Height = 10
  Placement = pos=(0,0,36.15) rot=(0,0,1;0rad)
  Radius = 4
FEATURE [Part::MultiFuse] Fusion134  label="removeToCreteHoleForPlugHousing046"
  Placement = pos=(70,19,36) rot=(0,1,0;1.5708rad)
  Shapes = -> [Cylinder058,Cylinder059]
FEATURE [Part::Cylinder] Cylinder060
  Angle = 360
  AttacherType = Attacher::AttachEngine3D
  Height = 20
  Placement = pos=(0,0,36.15) rot=(0,0,1;0rad)
  Radius = 14
FEATURE [Part::Cylinder] Cylinder061
  Angle = 360
  AttacherType = Attacher::AttachEngine3D
  Height = 10
  Placement = pos=(0,0,36.15) rot=(0,0,1;0rad)
  Radius = 4
FEATURE [Part::MultiFuse] Fusion135  label="removeToCreteHoleForPlugHousing048"
  Placement = pos=(70,19,36) rot=(0,1,0;1.5708rad)
  Shapes = -> [Cylinder060,Cylinder061]
FEATURE [Part::Box] Box035  label="removeToCreteHoleForPlugHousing049"
  AttacherType = Attacher::AttachEngine3D
  Height = 28.6
  Length = 20
  Placement = pos=(106.15,0,21.7) rot=(0,0,1;0rad)
  Width = 19
FEATURE [Part::MultiFuse] Fusion133  label="removeToCreteHoleForPlugHousing045"
  Placement = pos=(0,0,-28.3) rot=(0,0,1;0rad)
  Shapes = -> [Box035,Fusion134]
FEATURE [Part::MultiFuse] Fusion138  label="removeToCreteHoleForPlugHousing051"
  Placement = pos=(70,19,36) rot=(0,1,0;1.5708rad)
  Shapes = -> [Cylinder056,Cylinder057]
FEATURE [Part::MultiFuse] Fusion137  label="removeToCreteHoleForPlugHousing050"
  Placement = pos=(0,0,28.3) rot=(0,0,1;0rad)
  Shapes = -> [Box034,Fusion138]
FEATURE [Part::MultiFuse] Fusion132  label="removeToCreatePlugHousingBottomBit002"
  Shapes = -> [Fusion133,Fusion137]
FEATURE [Part::MultiFuse] Fusion136  label="removeToCreatePlugHousingBottomBit003"
  Shapes = -> [Fusion135,Fusion132]
FEATURE [Part::Cut] Cut058  label="bottomPlugHousingBit002"
  Base = -> Extrude063
  Placement = pos=(-0.09,0,0) rot=(0,0,1;0rad)
  Tool = -> Fusion136
FEATURE [Sketcher::SketchObject] Sketch073  label="bottomSketch003"
  FullyConstrained = true
  sketch-geometry (45):
    g0: LineSegment StartX=6.29999 StartY=8 StartZ=0 EndX=3.29999 EndY=8 EndZ=0
    g1: LineSegment StartX=3.29999 StartY=8 StartZ=0 EndX=3.29999 EndY=-6.03275e-07 EndZ=0
    g2: ArcOfCircle CenterX=8.29999 CenterY=5 CenterZ=0 NormalX=0 NormalY=0 NormalZ=1 AngleXU=0 Radius=2 StartAngle=3.14159 EndAngle=4.71239
    g3: LineSegment StartX=6.29999 StartY=8 StartZ=0 EndX=6.29999 EndY=5 EndZ=0
    g4: ArcOfCircle CenterX=105 CenterY=19 CenterZ=0 NormalX=0 NormalY=0 NormalZ=1 AngleXU=0 Radius=12.7 StartAngle=4.71239 EndAngle=5.94289
    g5-g11: Circle x7 (B-spline internal-alignment scaffolding for g12; pole/knot coordinates omitted)
    g12: BSplineCurve PolesCount=7 KnotsCount=5 Degree=3 IsPeriodic=0
    g13-g17: GeomPoint x5 (B-spline internal-alignment scaffolding for g12; pole/knot coordinates omitted)
    g18: ArcOfCircle CenterX=105 CenterY=19 CenterZ=0 NormalX=0 NormalY=0 NormalZ=1 AngleXU=0 Radius=15.7 StartAngle=5.81226 EndAngle=6.28319
    g19: BSplineCurve PolesCount=5 KnotsCount=3 Degree=3 IsPeriodic=0
    g20: LineSegment StartX=8.29999 StartY=3 StartZ=0 EndX=101.7 EndY=3 EndZ=0
    g21: LineSegment StartX=3.29999 StartY=-6.03275e-07 StartZ=0 EndX=105 EndY=-6.03275e-07 EndZ=0
    g22: LineSegment StartX=120.974 StartY=8.71251 StartZ=0 EndX=122.332 EndY=7.83778 EndZ=0
    g23: LineSegment StartX=105 StartY=-6.03274e-07 StartZ=0 EndX=113 EndY=-6.03274e-07 EndZ=0
    g24: ArcOfCircle CenterX=105 CenterY=19 CenterZ=0 NormalX=0 NormalY=0 NormalZ=1 AngleXU=0 Radius=20.6155 StartAngle=5.11091 EndAngle=5.71103
    g25: ArcOfCircle CenterX=117.7 CenterY=19 CenterZ=0 NormalX=0 NormalY=0 NormalZ=1 AngleXU=0 Radius=3 StartAngle=1.2e-15 EndAngle=2.10468
    g26: Circle CenterX=116.345 CenterY=16.3232 CenterZ=0 NormalX=0 NormalY=0 NormalZ=1 AngleXU=0 Radius=1
    g27: Circle CenterX=117.24 CenterY=15.7584 CenterZ=0 NormalX=0 NormalY=0 NormalZ=1 AngleXU=0 Radius=1
    g28: Circle CenterX=116.972 CenterY=14.7612 CenterZ=0 NormalX=0 NormalY=0 NormalZ=1 AngleXU=0 Radius=1
    g29: BSplineCurve PolesCount=3 KnotsCount=2 Degree=2 IsPeriodic=0
    g30: GeomPoint X=116.345 Y=16.3232 Z=0
    g31: GeomPoint X=116.972 Y=14.7612 Z=0
    g32: Circle CenterX=115.828 CenterY=17.157 CenterZ=0 NormalX=0 NormalY=0 NormalZ=1 AngleXU=0 Radius=1
    g33: Circle CenterX=115.841 CenterY=16.639 CenterZ=0 NormalX=0 NormalY=0 NormalZ=1 AngleXU=0 Radius=1
    g34: Circle CenterX=116.345 CenterY=16.3232 CenterZ=0 NormalX=0 NormalY=0 NormalZ=1 AngleXU=0 Radius=1
    g35: BSplineCurve PolesCount=3 KnotsCount=2 Degree=2 IsPeriodic=0
    g36: GeomPoint X=115.828 Y=17.157 Z=0
    g37: GeomPoint X=116.345 Y=16.3232 Z=0
    g38: LineSegment StartX=115.828 StartY=17.157 StartZ=0 EndX=115.828 EndY=20.8307 EndZ=0
    g39: Circle CenterX=115.828 CenterY=20.8307 CenterZ=0 NormalX=0 NormalY=0 NormalZ=1 AngleXU=0 Radius=1
    g40: Circle CenterX=115.831 CenterY=21.3396 CenterZ=0 NormalX=0 NormalY=0 NormalZ=1 AngleXU=0 Radius=1
    g41: Circle CenterX=116.173 CenterY=21.5825 CenterZ=0 NormalX=0 NormalY=0 NormalZ=1 AngleXU=0 Radius=1
    g42: BSplineCurve PolesCount=3 KnotsCount=2 Degree=2 IsPeriodic=0
    g43: GeomPoint X=115.828 Y=20.8307 Z=0
    g44: GeomPoint X=116.173 Y=21.5825 Z=0
  constraints (70):
    c: Horizontal(g0)
    c: Distance(g0) = 3
    c: Coincident(g1,g0)
    c: Vertical(g1)
    c: Block(g2)
    c: Block(g0)
    c: Coincident(g3,g0)
    c: Coincident(g3,g2)
    c: Vertical(g3)
    c: Block(g1)
    c: Block(g4)
    c: Coincident(g19,g4)
    c: Block(g19)
    c: Equal(g5, g6-g11) x6
    c: InternalAlignment(g5-g11 -> g12) x7
    c: InternalAlignment(g13-g17 -> g12) x5
    c: Block(g12)
    c: Coincident(g18,g12)
    c: Block(g18)
    c: Coincident(g20,g2)
    c: Coincident(g20,g19)
    c: Horizontal(g20)
    c: Distance(g20) = 93.4
    c: Coincident(g21,g1)
    c: Horizontal(g21)
    c: Distance(g21) = 101.7
    c: Horizontal(g23)
    c: Distance(g23) = 8
    c: Coincident(g24,g23)
    c: Block(g23)
    c: Coincident(g22,g24)
    c: Block(g24)
    c: Block(g22)
    c: Distance(g22) = 1.61553
    c: Coincident(g25,g18)
    c: Block(g25)
    c: Weight(g26) = 1
    c: Equal(g26,g27)
    c: Equal(g26,g28)
    c: Coincident(g29,g4)
    c: InternalAlignment(g26,g29)
    c: InternalAlignment(g27,g29)
    c: InternalAlignment(g28,g29)
    c: InternalAlignment(g30,g29)
    c: InternalAlignment(g31,g29)
    c: Block(g29)
    c: Weight(g32) = 1
    c: Equal(g32,g33)
    c: Equal(g32,g34)
    c: Coincident(g35,g29)
    c: InternalAlignment(g32,g35)
    c: InternalAlignment(g33,g35)
    c: InternalAlignment(g34,g35)
    c: InternalAlignment(g36,g35)
    c: InternalAlignment(g37,g35)
    c: Block(g35)
    c: Coincident(g38,g35)
    c: Vertical(g38)
    c: Block(g38)
    c: Coincident(g42,g38)
    c: Weight(g39) = 1
    c: Equal(g39,g40)
    c: Equal(g39,g41)
    c: Coincident(g42,g25)
    c: InternalAlignment(g39,g42)
    c: InternalAlignment(g40,g42)
    c: InternalAlignment(g41,g42)
    c: InternalAlignment(g43,g42)
    c: InternalAlignment(g44,g42)
    c: Block(g42)
FEATURE [Part::Extrusion] Extrude064  label="bottom016"
  Base = -> Sketch073
  Dir = (0,0,1)
  DirMode = 2
  FaceMakerClass = Part::FaceMakerBullseye
  LengthFwd = 71.4
  LengthRev = 0
  Placement = pos=(0,0,0.3) rot=(0,0,1;0rad)
  Solid = true
  Symmetric = false
FEATURE [Part::Revolution] Revolve157  label="removeToCreateScrewAndThreadedInsertHole063"
  Angle = 360
  Axis = (0,1,0)
  Base = (0,0,0)
  FaceMakerClass = Part::FaceMakerBullseye
  Placement = pos=(12.5,0,10) rot=(0,0,1;0rad)
  Solid = false
  Source = -> Face141
  Symmetric = false
FEATURE [Sketcher::SketchObject] Sketch074
  FullyConstrained = true
  Placement = pos=(117,19,0) rot=(0.57735,0.57735,0.57735;2.0944rad)
  sketch-geometry (48):
    g0: LineSegment StartX=-49.19 StartY=69.25 StartZ=0 EndX=-49.19 EndY=66.25 EndZ=0
    g1: LineSegment StartX=-49.19 StartY=63.5 StartZ=0 EndX=-49.19 EndY=60.5 EndZ=0
    g2: LineSegment StartX=-49.19 StartY=57.75 StartZ=0 EndX=-49.19 EndY=54.75 EndZ=0
    g3: LineSegment StartX=-49.19 StartY=52 StartZ=0 EndX=-49.19 EndY=49 EndZ=0
    g4: LineSegment StartX=-49.19 StartY=46.25 StartZ=0 EndX=-49.19 EndY=43.25 EndZ=0
    g5: LineSegment StartX=-49.19 StartY=40.5 StartZ=0 EndX=-49.19 EndY=37.5 EndZ=0
    g6: LineSegment StartX=-49.19 StartY=34.5 StartZ=0 EndX=-49.19 EndY=31.5 EndZ=0
    g7: LineSegment StartX=-49.19 StartY=28.75 StartZ=0 EndX=-49.19 EndY=25.75 EndZ=0
    g8: LineSegment StartX=-49.19 StartY=23 StartZ=0 EndX=-49.19 EndY=20 EndZ=0
    g9: LineSegment StartX=-49.19 StartY=17.25 StartZ=0 EndX=-49.19 EndY=14.25 EndZ=0
    g10: LineSegment StartX=-49.19 StartY=11.5 StartZ=0 EndX=-49.19 EndY=8.5 EndZ=0
    g11: LineSegment StartX=-49.19 StartY=5.75 StartZ=0 EndX=-49.19 EndY=2.75 EndZ=0
    g12: ArcOfCircle CenterX=-1.5 CenterY=67.75 CenterZ=0 NormalX=0 NormalY=0 NormalZ=1 AngleXU=0 Radius=1.5 StartAngle=4.71239 EndAngle=7.85398
    g13: ArcOfCircle CenterX=-1.5 CenterY=62 CenterZ=0 NormalX=0 NormalY=0 NormalZ=1 AngleXU=0 Radius=1.5 StartAngle=4.71239 EndAngle=7.85398
    g14: ArcOfCircle CenterX=-1.5 CenterY=56.25 CenterZ=0 NormalX=0 NormalY=0 NormalZ=1 AngleXU=0 Radius=1.5 StartAngle=4.71239 EndAngle=7.85398
    g15: ArcOfCircle CenterX=-11.49 CenterY=50.5 CenterZ=0 NormalX=0 NormalY=0 NormalZ=1 AngleXU=0 Radius=1.5 StartAngle=4.71239 EndAngle=7.85398
    g16: ArcOfCircle CenterX=-16.28 CenterY=44.75 CenterZ=0 NormalX=0 NormalY=0 NormalZ=1 AngleXU=0 Radius=1.5 StartAngle=4.71239 EndAngle=7.85398
    g17: ArcOfCircle CenterX=-18.2337 CenterY=39 CenterZ=0 NormalX=0 NormalY=0 NormalZ=1 AngleXU=0 Radius=1.5 StartAngle=4.71485 EndAngle=7.85398
    g18: ArcOfCircle CenterX=-16.2837 CenterY=27.25 CenterZ=0 NormalX=0 NormalY=0 NormalZ=1 AngleXU=0 Radius=1.5 StartAngle=4.71485 EndAngle=7.85398
    g19: ArcOfCircle CenterX=-18.2337 CenterY=33 CenterZ=0 NormalX=0 NormalY=0 NormalZ=1 AngleXU=0 Radius=1.5 StartAngle=4.71485 EndAngle=7.85398
    g20: ArcOfCircle CenterX=-11.49 CenterY=21.5 CenterZ=0 NormalX=0 NormalY=0 NormalZ=1 AngleXU=0 Radius=1.5 StartAngle=4.71239 EndAngle=7.85398
    g21: ArcOfCircle CenterX=-1.5 CenterY=4.25 CenterZ=0 NormalX=0 NormalY=0 NormalZ=1 AngleXU=0 Radius=1.5 StartAngle=4.71239 EndAngle=7.85398
    g22: ArcOfCircle CenterX=-1.5 CenterY=10 CenterZ=0 NormalX=0 NormalY=0 NormalZ=1 AngleXU=0 Radius=1.5 StartAngle=4.71239 EndAngle=7.85398
    g23: ArcOfCircle CenterX=-1.5 CenterY=15.75 CenterZ=0 NormalX=0 NormalY=0 NormalZ=1 AngleXU=0 Radius=1.5 StartAngle=4.71239 EndAngle=7.85398
    g24: LineSegment StartX=-49.19 StartY=69.25 StartZ=0 EndX=-1.5 EndY=69.25 EndZ=0
    g25: LineSegment StartX=-49.19 StartY=66.25 StartZ=0 EndX=-1.5 EndY=66.25 EndZ=0
    g26: LineSegment StartX=-49.19 StartY=63.5 StartZ=0 EndX=-1.5 EndY=63.5 EndZ=0
    g27: LineSegment StartX=-49.19 StartY=60.5 StartZ=0 EndX=-1.5 EndY=60.5 EndZ=0
    g28: LineSegment StartX=-49.19 StartY=57.75 StartZ=0 EndX=-1.5 EndY=57.75 EndZ=0
    g29: LineSegment StartX=-49.19 StartY=54.75 StartZ=0 EndX=-1.5 EndY=54.75 EndZ=0
    g30: LineSegment StartX=-49.19 StartY=52 StartZ=0 EndX=-11.49 EndY=52 EndZ=0
    g31: LineSegment StartX=-49.19 StartY=49 StartZ=0 EndX=-11.49 EndY=49 EndZ=0
    g32: LineSegment StartX=-49.19 StartY=46.25 StartZ=0 EndX=-16.28 EndY=46.25 EndZ=0
    g33: LineSegment StartX=-49.19 StartY=43.25 StartZ=0 EndX=-16.28 EndY=43.25 EndZ=0
    g34: LineSegment StartX=-49.19 StartY=40.5 StartZ=0 EndX=-18.2337 EndY=40.5 EndZ=0
    g35: LineSegment StartX=-49.19 StartY=37.5 StartZ=0 EndX=-18.23 EndY=37.5 EndZ=0
    g36: LineSegment StartX=-49.19 StartY=34.5 StartZ=0 EndX=-18.2337 EndY=34.5 EndZ=0
    g37: LineSegment StartX=-49.19 StartY=31.5 StartZ=0 EndX=-18.23 EndY=31.5 EndZ=0
    g38: LineSegment StartX=-49.19 StartY=28.75 StartZ=0 EndX=-16.2837 EndY=28.75 EndZ=0
    g39: LineSegment StartX=-49.19 StartY=25.75 StartZ=0 EndX=-16.28 EndY=25.75 EndZ=0
    g40: LineSegment StartX=-49.19 StartY=23 StartZ=0 EndX=-11.49 EndY=23 EndZ=0
    g41: LineSegment StartX=-49.19 StartY=20 StartZ=0 EndX=-11.49 EndY=20 EndZ=0
    g42: LineSegment StartX=-49.19 StartY=17.25 StartZ=0 EndX=-1.5 EndY=17.25 EndZ=0
    g43: LineSegment StartX=-49.19 StartY=14.25 StartZ=0 EndX=-1.5 EndY=14.25 EndZ=0
    g44: LineSegment StartX=-49.19 StartY=11.5 StartZ=0 EndX=-1.5 EndY=11.5 EndZ=0
    g45: LineSegment StartX=-49.19 StartY=8.5 StartZ=0 EndX=-1.5 EndY=8.5 EndZ=0
    g46: LineSegment StartX=-49.19 StartY=5.75 StartZ=0 EndX=-1.5 EndY=5.75 EndZ=0
    g47: LineSegment StartX=-49.19 StartY=2.75 StartZ=0 EndX=-1.5 EndY=2.75 EndZ=0
  constraints (120):
    c: Vertical(g0)
    c: Distance(g0) = 3
    c: Block(g0)
    c: Vertical(g1)
    c: Distance(g1) = 3
    c: Vertical(g2)
    c: Equal(g0,g2) = 3
    c: Block(g2)
    c: Vertical(g3)
    c: Equal(g1,g3) = 3
    c: Vertical(g4)
    c: Equal(g0,g4) = 3
    c: Block(g4)
    c: Vertical(g5)
    c: Equal(g1,g5) = 3
    c: Vertical(g6)
    c: Equal(g0,g6) = 3
    c: Block(g6)
    c: Vertical(g7)
    c: Equal(g1,g7) = 3
    c: Vertical(g8)
    c: Equal(g0,g8) = 3
    c: Block(g8)
    c: Vertical(g9)
    c: Equal(g1,g9) = 3
    c: Vertical(g10)
    c: Equal(g0,g10) = 3
    c: Block(g10)
    c: Vertical(g11)
    c: Equal(g1,g11) = 3
    c: Block(g12)
    c: Block(g13)
    c: Block(g14)
    c: Block(g15)
    c: Block(g16)
    c: Block(g17)
    c: Block(g18)
    c: Block(g19)
    c: Block(g20)
    c: Block(g21)
    c: Block(g22)
    c: Block(g23)
    c: Block(g11)
    c: Block(g9)
    c: Block(g7)
    c: Block(g5)
    c: Block(g3)
    c: Block(g1)
    c: Coincident(g24,g0)
    c: Coincident(g24,g12)
    c: Horizontal(g24)
    c: Coincident(g25,g0)
    c: Coincident(g25,g12)
    c: Horizontal(g25)
    c: Coincident(g26,g1)
    c: Coincident(g26,g13)
    c: Horizontal(g26)
    c: Coincident(g27,g1)
    c: Coincident(g27,g13)
    c: Horizontal(g27)
    c: Coincident(g28,g2)
    c: Coincident(g28,g14)
    c: Horizontal(g28)
    c: Coincident(g29,g2)
    c: Coincident(g29,g14)
    c: Horizontal(g29)
    c: Coincident(g30,g3)
    c: Coincident(g30,g15)
    c: Horizontal(g30)
    c: Coincident(g31,g3)
    c: Coincident(g31,g15)
    c: Horizontal(g31)
    c: Coincident(g32,g4)
    c: Coincident(g32,g16)
    c: Horizontal(g32)
    c: Coincident(g33,g4)
    c: Coincident(g33,g16)
    c: Horizontal(g33)
    c: Coincident(g34,g5)
    c: Coincident(g34,g17)
    c: Horizontal(g34)
    c: Coincident(g35,g5)
    c: Coincident(g35,g17)
    c: Horizontal(g35)
    c: Coincident(g36,g6)
    c: Coincident(g36,g19)
    c: Horizontal(g36)
    c: Coincident(g37,g6)
    c: Coincident(g37,g19)
    c: Horizontal(g37)
    c: Coincident(g38,g7)
    c: Coincident(g38,g18)
    c: Horizontal(g38)
    c: Coincident(g39,g7)
    c: Coincident(g39,g18)
    c: Horizontal(g39)
    c: Coincident(g40,g8)
    c: Coincident(g40,g20)
    c: Horizontal(g40)
    c: Coincident(g41,g8)
    c: Coincident(g41,g20)
    c: Horizontal(g41)
    c: Coincident(g42,g9)
    c: Coincident(g42,g23)
    c: Horizontal(g42)
    c: Coincident(g43,g9)
    c: Coincident(g43,g23)
    c: Horizontal(g43)
    c: Coincident(g44,g10)
    c: Coincident(g44,g22)
    c: Horizontal(g44)
    c: Coincident(g45,g10)
    c: Coincident(g45,g22)
    c: Horizontal(g45)
    c: Coincident(g46,g11)
    c: Coincident(g46,g21)
    c: Horizontal(g46)
    c: Coincident(g47,g11)
    c: Coincident(g47,g21)
    c: Horizontal(g47)
FEATURE [Part::Extrusion] Extrude065
  Base = -> Sketch074
  Dir = (1,0,0)
  DirMode = 2
  FaceMakerClass = Part::FaceMakerBullseye
  LengthFwd = 23
  LengthRev = 0
  Placement = pos=(-19,0,0) rot=(0,0,1;0rad)
  Solid = true
  Symmetric = false
FEATURE [Part::Fillet] Fillet056  label="removeToCreateVentalationHoles003"
  Base = -> Extrude065
  Edges = <same value as first occurrence — deduplicated (x6 in doc)>
  Placement = pos=(7,0.02,0) rot=(0,0,1;0rad)
FEATURE [Part::Revolution] Revolve158  label="removeToCreateScrewAndThreadedInsertHole065"
  Angle = 360
  Axis = (0,1,0)
  Base = (0,0,0)
  FaceMakerClass = Part::FaceMakerBullseye
  Placement = pos=(12.5,0,62) rot=(0,0,1;0rad)
  Solid = false
  Source = -> Face146
  Symmetric = false
FEATURE [Part::Revolution] Revolve159  label="removeToCreateScrewAndThreadedInsertHole066"
  Angle = 360
  Axis = (0,1,0)
  Base = (0,0,0)
  FaceMakerClass = Part::FaceMakerBullseye
  Placement = pos=(89.5,0,68.5) rot=(0,0,1;0rad)
  Solid = false
  Source = -> Face143
  Symmetric = false
FEATURE [Part::Revolution] Revolve160  label="removeToCreateScrewAndThreadedInsertHole067"
  Angle = 360
  Axis = (0,1,0)
  Base = (0,0,0)
  FaceMakerClass = Part::FaceMakerBullseye
  Placement = pos=(89.5,0,3.5) rot=(0,0,1;0rad)
  Solid = false
  Source = -> Face142
  Symmetric = false
FEATURE [Part::Revolution] Revolve161  label="removeToCreateScrewAndThreadedInsertHole068"
  Angle = 360
  Axis = (0,1,0)
  Base = (0,0,0)
  FaceMakerClass = Part::FaceMakerBullseye
  Placement = pos=(109.5,4.7,3.5) rot=(0,0,1;0rad)
  Solid = false
  Source = -> Face145
  Symmetric = false
FEATURE [Part::Revolution] Revolve162  label="removeToCreateScrewAndThreadedInsertHole069"
  Angle = 360
  Axis = (0,1,0)
  Base = (0,0,0)
  FaceMakerClass = Part::FaceMakerBullseye
  Placement = pos=(109.5,4.7,68.5) rot=(0,0,1;0rad)
  Solid = false
  Source = -> Face144
  Symmetric = false
FEATURE [Part::MultiFuse] Fusion141  label="removeToCreateScrewAndThreadedInsertHole064"
  Shapes = -> [Revolve162,Revolve161,Revolve160,Revolve159,Revolve158,Revolve157]
FEATURE [Part::Cylinder] Cylinder062
  Angle = 360
  AttacherType = Attacher::AttachEngine3D
  Height = 20
  Placement = pos=(0,0,36.15) rot=(0,0,1;0rad)
  Radius = 14
FEATURE [Part::Cylinder] Cylinder063
  Angle = 360
  AttacherType = Attacher::AttachEngine3D
  Height = 10
  Placement = pos=(0,0,36.15) rot=(0,0,1;0rad)
  Radius = 4
FEATURE [Part::MultiFuse] Fusion139  label="removeToCreteHoleForPlugHousing052"
  Placement = pos=(70,19,36) rot=(0,1,0;1.5708rad)
  Shapes = -> [Cylinder062,Cylinder063]
FEATURE [Part::Cut] Cut060  label="bottom017"
  Base = -> Extrude064
  Tool = -> Fusion139
FEATURE [Part::Cut] Cut061  label="bottom019"
  Base = -> Cut060
  Tool = -> Fusion141
FEATURE [Part::MultiFuse] Fusion140  label="bottom018"
  Shapes = -> [Cut061,Cut058]
FEATURE [Part::Cut] Cut059  label="bottom020"
  Base = -> Fusion140
  Tool = -> Fillet056
FEATURE [Part::Box] Box036  label="Cube021"
  AttacherType = Attacher::AttachEngine3D
  Height = 80
  Length = 26
  Placement = pos=(0,-1,-5) rot=(0,0,1;0rad)
  Width = 11
FEATURE [Part::Cut] Cut062  label="removeFromBottom002"
  Base = -> Cut057
  Tool = -> Box036
FEATURE [Part::Cut] Cut063
  Base = -> Cut059
  Tool = -> Cut062
FEATURE [Part::Cut] Cut064  label="pcbStands"
  Base = -> Fusion095
  Tool = -> Fusion127
FEATURE [Sketcher::SketchObject] Sketch075  label="topSketch022"
  FullyConstrained = true
  sketch-geometry (6):
    g0: LineSegment StartX=19 StartY=38 StartZ=0 EndX=117 EndY=38 EndZ=0
    g1: ArcOfCircle CenterX=19 CenterY=19 CenterZ=0 NormalX=0 NormalY=0 NormalZ=1 AngleXU=0 Radius=19 StartAngle=1.5708 EndAngle=3.14159
    g2: LineSegment StartX=117 StartY=38 StartZ=0 EndX=117 EndY=19 EndZ=0
    g3: LineSegment StartX=98 StartY=1.0161e-12 StartZ=0 EndX=5.22862e-06 EndY=1.0161e-12 EndZ=0
    g4: LineSegment StartX=5.22862e-06 StartY=19 StartZ=0 EndX=5.22862e-06 EndY=1.0161e-12 EndZ=0
    g5: ArcOfCircle CenterX=98 CenterY=19 CenterZ=0 NormalX=0 NormalY=0 NormalZ=1 AngleXU=0 Radius=19 StartAngle=4.71239 EndAngle=6.28319
  constraints (16):
    c: Horizontal(g0)
    c: Distance(g0) = 98
    c: Coincident(g1,g0)
    c: Block(g1)
    c: Coincident(g2,g0)
    c: Vertical(g2)
    c: Distance(g2) = 19
    c: Horizontal(g3)
    c: Coincident(g4,g1)
    c: Vertical(g4)
    c: Coincident(g3,g4)
    c: Block(g3)
    c: Coincident(g5,g2)
    c: Coincident(g5,g3)
    c: Block(g0)
    c: Block(g5)
FEATURE [Part::Extrusion] Extrude067  label="sideB003"
  Base = -> Sketch075
  Dir = (0,0,1)
  DirMode = 2
  FaceMakerClass = Part::FaceMakerBullseye
  LengthFwd = 3
  LengthRev = 0
  Placement = pos=(0,0,71.7) rot=(0,0,1;0rad)
  Solid = true
  Symmetric = false
FEATURE [Sketcher::SketchObject] Sketch076  label="topSketch023"
  FullyConstrained = true
  sketch-geometry (6):
    g0: LineSegment StartX=19 StartY=38 StartZ=0 EndX=117 EndY=38 EndZ=0
    g1: ArcOfCircle CenterX=19 CenterY=19 CenterZ=0 NormalX=0 NormalY=0 NormalZ=1 AngleXU=0 Radius=19 StartAngle=1.5708 EndAngle=3.14159
    g2: LineSegment StartX=117 StartY=38 StartZ=0 EndX=117 EndY=19 EndZ=0
    g3: LineSegment StartX=98 StartY=1.0161e-12 StartZ=0 EndX=5.22862e-06 EndY=1.0161e-12 EndZ=0
    g4: LineSegment StartX=5.22862e-06 StartY=19 StartZ=0 EndX=5.22862e-06 EndY=1.0161e-12 EndZ=0
    g5: ArcOfCircle CenterX=98 CenterY=19 CenterZ=0 NormalX=0 NormalY=0 NormalZ=1 AngleXU=0 Radius=19 StartAngle=4.71239 EndAngle=6.28319
  constraints (16):
    c: Horizontal(g0)
    c: Distance(g0) = 98
    c: Coincident(g1,g0)
    c: Block(g1)
    c: Coincident(g2,g0)
    c: Vertical(g2)
    c: Distance(g2) = 19
    c: Horizontal(g3)
    c: Coincident(g4,g1)
    c: Vertical(g4)
    c: Coincident(g3,g4)
    c: Block(g3)
    c: Coincident(g5,g2)
    c: Coincident(g5,g3)
    c: Block(g0)
    c: Block(g5)
FEATURE [Part::Extrusion] Extrude066  label="sideA003"
  Base = -> Sketch076
  Dir = (0,0,1)
  DirMode = 2
  FaceMakerClass = Part::FaceMakerBullseye
  LengthFwd = 3
  LengthRev = 0
  Placement = pos=(0,0,-2.7) rot=(0,0,1;0rad)
  Solid = true
  Symmetric = false
FEATURE [Part::MultiFuse] Fusion142  label="removeFromBottom003"
  Placement = pos=(2,0,0) rot=(0,0,1;0rad)
  Shapes = -> [Extrude066,Extrude067]
FEATURE [Part::Cut] Cut065  label="screwRetainers002"
  Base = -> Fusion096
  Tool = -> Fusion142
FEATURE [Sketcher::SketchObject] Sketch077
  FullyConstrained = true
  Placement = pos=(117,19,0) rot=(0.57735,0.57735,0.57735;2.0944rad)
  sketch-geometry (8):
    g0: LineSegment StartX=-49.19 StartY=63.5 StartZ=0 EndX=-49.19 EndY=60.5 EndZ=0
    g1: LineSegment StartX=-49.19 StartY=11.5 StartZ=0 EndX=-49.19 EndY=8.5 EndZ=0
    g2: ArcOfCircle CenterX=-1.5 CenterY=62 CenterZ=0 NormalX=0 NormalY=0 NormalZ=1 AngleXU=0 Radius=1.5 StartAngle=4.71239 EndAngle=7.85398
    g3: ArcOfCircle CenterX=-1.5 CenterY=10 CenterZ=0 NormalX=0 NormalY=0 NormalZ=1 AngleXU=0 Radius=1.5 StartAngle=4.71239 EndAngle=7.85398
    g4: LineSegment StartX=-49.19 StartY=63.5 StartZ=0 EndX=-1.5 EndY=63.5 EndZ=0
    g5: LineSegment StartX=-49.19 StartY=60.5 StartZ=0 EndX=-1.5 EndY=60.5 EndZ=0
    g6: LineSegment StartX=-49.19 StartY=11.5 StartZ=0 EndX=-1.5 EndY=11.5 EndZ=0
    g7: LineSegment StartX=-49.19 StartY=8.5 StartZ=0 EndX=-1.5 EndY=8.5 EndZ=0
  constraints (19):
    c: Vertical(g0)
    c: Distance(g0) = 3
    c: Vertical(g1)
    c: Block(g1)
    c: Block(g2)
    c: Block(g3)
    c: Block(g0)
    c: Coincident(g4,g0)
    c: Coincident(g4,g2)
    c: Horizontal(g4)
    c: Coincident(g5,g0)
    c: Coincident(g5,g2)
    c: Horizontal(g5)
    c: Coincident(g6,g1)
    c: Coincident(g6,g3)
    c: Horizontal(g6)
    c: Coincident(g7,g1)
    c: Coincident(g7,g3)
    c: Horizontal(g7)
FEATURE [Part::Extrusion] Extrude068
  Base = -> Sketch077
  Dir = (1,0,0)
  DirMode = 2
  FaceMakerClass = Part::FaceMakerBullseye
  LengthFwd = 10
  LengthRev = 0
  Solid = true
  Symmetric = false
FEATURE [Part::Fillet] Fillet057  label="removeFromtMoreFrontCaseScrewRetainers002"
  Base = -> Extrude068
  Edges = 4 edges r=1.49: [Edge6,Edge11,Edge18,Edge23]
  Placement = pos=(-12,0,0) rot=(0,0,1;0rad)
FEATURE [Sketcher::SketchObject] Sketch078
  FullyConstrained = true
  Placement = pos=(117,19,0) rot=(0.57735,0.57735,0.57735;2.0944rad)
  sketch-geometry (8):
    g0: LineSegment StartX=-49.19 StartY=69.25 StartZ=0 EndX=-49.19 EndY=66.25 EndZ=0
    g1: LineSegment StartX=-49.19 StartY=5.75 StartZ=0 EndX=-49.19 EndY=2.75 EndZ=0
    g2: ArcOfCircle CenterX=-1.5 CenterY=67.75 CenterZ=0 NormalX=0 NormalY=0 NormalZ=1 AngleXU=0 Radius=1.5 StartAngle=4.71239 EndAngle=7.85398
    g3: ArcOfCircle CenterX=-1.5 CenterY=4.25 CenterZ=0 NormalX=0 NormalY=0 NormalZ=1 AngleXU=0 Radius=1.5 StartAngle=4.71239 EndAngle=7.85398
    g4: LineSegment StartX=-49.19 StartY=69.25 StartZ=0 EndX=-1.5 EndY=69.25 EndZ=0
    g5: LineSegment StartX=-49.19 StartY=66.25 StartZ=0 EndX=-1.5 EndY=66.25 EndZ=0
    g6: LineSegment StartX=-49.19 StartY=5.75 StartZ=0 EndX=-1.5 EndY=5.75 EndZ=0
    g7: LineSegment StartX=-49.19 StartY=2.75 StartZ=0 EndX=-1.5 EndY=2.75 EndZ=0
  constraints (19):
    c: Vertical(g0)
    c: Distance(g0) = 3
    c: Block(g0)
    c: Vertical(g1)
    c: Block(g2)
    c: Block(g3)
    c: Block(g1)
    c: Coincident(g4,g0)
    c: Coincident(g4,g2)
    c: Horizontal(g4)
    c: Coincident(g5,g0)
    c: Coincident(g5,g2)
    c: Horizontal(g5)
    c: Coincident(g6,g1)
    c: Coincident(g6,g3)
    c: Horizontal(g6)
    c: Coincident(g7,g1)
    c: Coincident(g7,g3)
    c: Horizontal(g7)
FEATURE [Part::Extrusion] Extrude069
  Base = -> Sketch078
  Dir = (1,0,0)
  DirMode = 2
  FaceMakerClass = Part::FaceMakerBullseye
  LengthFwd = 10
  LengthRev = 0
  Solid = true
  Symmetric = false
FEATURE [Part::Fillet] Fillet058  label="removeFromtMoreFrontCaseScrewRetainers003"
  Base = -> Extrude069
  Edges = 4 edges r=1.49: [Edge6,Edge11,Edge18,Edge23]
  Placement = pos=(-4,0,0) rot=(0,0,1;0rad)
FEATURE [Part::Cut] Cut066
  Base = -> Cut065
  Tool = -> Fillet058
FEATURE [Part::Cut] Cut067  label="screwPillars"
  Base = -> Cut066
  Tool = -> Fillet057
FEATURE [Part::MultiFuse] Fusion143  label="bottom021"
  Shapes = -> [Cut031,Cut063]
FEATURE [Part::Cylinder] Cylinder
  Angle = 360
  AttacherType = Attacher::AttachEngine3D
  Height = 10
  Placement = pos=(20.65,12,4.68) rot=(1,0,0;1.5708rad)
  Radius = 2
FEATURE [Part::Cylinder] Cylinder064
  Angle = 360
  AttacherType = Attacher::AttachEngine3D
  Height = 10
  Placement = pos=(20.65,12,67.38) rot=(1,0,0;1.5708rad)
  Radius = 2
FEATURE [Part::Cylinder] Cylinder065
  Angle = 360
  AttacherType = Attacher::AttachEngine3D
  Height = 10
  Placement = pos=(77.15,12,67.38) rot=(1,0,0;1.5708rad)
  Radius = 2
FEATURE [Part::Cylinder] Cylinder066
  Angle = 360
  AttacherType = Attacher::AttachEngine3D
  Height = 10
  Placement = pos=(77.15,12,4.68) rot=(1,0,0;1.5708rad)
  Radius = 2
FEATURE [Part::MultiFuse] Fusion144  label="removeFromThreadedInsertHousing"
  Shapes = -> [Cylinder065,Cylinder064,Cylinder,Cylinder066]
FEATURE [Part::Cut] Cut068  label="pcbStands001"
  Base = -> Cut064
  Tool = -> Fusion144
FEATURE [Part::MultiFuse] Fusion145
  Shapes = -> [Cut068,Fusion143]
FEATURE [Part::MultiFuse] Fusion146
  Shapes = -> [Fusion145]
FEATURE [Part::MultiFuse] Fusion147  label="bottom022"
  Shapes = -> [Cut067,Fusion146]
FEATURE [Part::MultiFuse] Fusion148  label="casePillars005"
  Shapes = -> [Cut047,Fusion092]
FEATURE [Part::MultiFuse] Fusion149  label="bottom023"
  Shapes = -> [Fusion124,Fusion113,Fusion147]
FEATURE [Part::MultiFuse] Fusion150  label="topBits"
  Shapes = -> [Cut025,Fusion148,Cut030,Fillet034]
FEATURE [Part::Feature] Face149 .. Face152  x4 (patterned run collapsed; names and placements below)
  shape: bbox 3.2 x 1.5 x 2e-07 mm, 1 faces, 0 solids (baked)
FEATURE [Part::Feature] Face153
  shape: bbox 3.6 x 3.2 x 2e-07 mm, 1 faces, 0 solids (baked)
FEATURE [Part::Feature] Face154
  shape: bbox 3.6 x 3.2 x 2e-07 mm, 1 faces, 0 solids (baked)
FEATURE [Sketcher::SketchObject] Sketch079  label="topSketch024"
  FullyConstrained = true
  sketch-geometry (6):
    g0: LineSegment StartX=19 StartY=38 StartZ=0 EndX=117 EndY=38 EndZ=0
    g1: ArcOfCircle CenterX=19 CenterY=19 CenterZ=0 NormalX=0 NormalY=0 NormalZ=1 AngleXU=0 Radius=19 StartAngle=1.5708 EndAngle=3.14159
    g2: LineSegment StartX=117 StartY=38 StartZ=0 EndX=117 EndY=19 EndZ=0
    g3: LineSegment StartX=98 StartY=1.0161e-12 StartZ=0 EndX=5.22862e-06 EndY=1.0161e-12 EndZ=0
    g4: LineSegment StartX=5.22862e-06 StartY=19 StartZ=0 EndX=5.22862e-06 EndY=1.0161e-12 EndZ=0
    g5: ArcOfCircle CenterX=98 CenterY=19 CenterZ=0 NormalX=0 NormalY=0 NormalZ=1 AngleXU=0 Radius=19 StartAngle=4.71239 EndAngle=6.28319
  constraints (16):
    c: Horizontal(g0)
    c: Distance(g0) = 98
    c: Coincident(g1,g0)
    c: Block(g1)
    c: Coincident(g2,g0)
    c: Vertical(g2)
    c: Distance(g2) = 19
    c: Horizontal(g3)
    c: Coincident(g4,g1)
    c: Vertical(g4)
    c: Coincident(g3,g4)
    c: Block(g3)
    c: Coincident(g5,g2)
    c: Coincident(g5,g3)
    c: Block(g0)
    c: Block(g5)
FEATURE [Sketcher::SketchObject] Sketch080  label="topSketch025"
  FullyConstrained = true
  sketch-geometry (6):
    g0: LineSegment StartX=19 StartY=38 StartZ=0 EndX=117 EndY=38 EndZ=0
    g1: ArcOfCircle CenterX=19 CenterY=19 CenterZ=0 NormalX=0 NormalY=0 NormalZ=1 AngleXU=0 Radius=19 StartAngle=1.5708 EndAngle=3.14159
    g2: LineSegment StartX=117 StartY=38 StartZ=0 EndX=117 EndY=19 EndZ=0
    g3: LineSegment StartX=98 StartY=1.0161e-12 StartZ=0 EndX=5.22862e-06 EndY=1.0161e-12 EndZ=0
    g4: LineSegment StartX=5.22862e-06 StartY=19 StartZ=0 EndX=5.22862e-06 EndY=1.0161e-12 EndZ=0
    g5: ArcOfCircle CenterX=98 CenterY=19 CenterZ=0 NormalX=0 NormalY=0 NormalZ=1 AngleXU=0 Radius=19 StartAngle=4.71239 EndAngle=6.28319
  constraints (16):
    c: Horizontal(g0)
    c: Distance(g0) = 98
    c: Coincident(g1,g0)
    c: Block(g1)
    c: Coincident(g2,g0)
    c: Vertical(g2)
    c: Distance(g2) = 19
    c: Horizontal(g3)
    c: Coincident(g4,g1)
    c: Vertical(g4)
    c: Coincident(g3,g4)
    c: Block(g3)
    c: Coincident(g5,g2)
    c: Coincident(g5,g3)
    c: Block(g0)
    c: Block(g5)
FEATURE [Part::Extrusion] Extrude070  label="sideA004"
  Base = -> Sketch080
  Dir = (0,0,1)
  DirMode = 2
  FaceMakerClass = Part::FaceMakerBullseye
  LengthFwd = 3
  LengthRev = 0
  Placement = pos=(0,0,-2.7) rot=(0,0,1;0rad)
  Solid = true
  Symmetric = false
FEATURE [Sketcher::SketchObject] Sketch081
  FullyConstrained = true
  Placement = pos=(117,19,0) rot=(0.57735,0.57735,0.57735;2.0944rad)
  sketch-geometry (8):
    g0: LineSegment StartX=-49.19 StartY=63.5 StartZ=0 EndX=-49.19 EndY=60.5 EndZ=0
    g1: LineSegment StartX=-49.19 StartY=11.5 StartZ=0 EndX=-49.19 EndY=8.5 EndZ=0
    g2: ArcOfCircle CenterX=-1.5 CenterY=62 CenterZ=0 NormalX=0 NormalY=0 NormalZ=1 AngleXU=0 Radius=1.5 StartAngle=4.71239 EndAngle=7.85398
    g3: ArcOfCircle CenterX=-1.5 CenterY=10 CenterZ=0 NormalX=0 NormalY=0 NormalZ=1 AngleXU=0 Radius=1.5 StartAngle=4.71239 EndAngle=7.85398
    g4: LineSegment StartX=-49.19 StartY=63.5 StartZ=0 EndX=-1.5 EndY=63.5 EndZ=0
    g5: LineSegment StartX=-49.19 StartY=60.5 StartZ=0 EndX=-1.5 EndY=60.5 EndZ=0
    g6: LineSegment StartX=-49.19 StartY=11.5 StartZ=0 EndX=-1.5 EndY=11.5 EndZ=0
    g7: LineSegment StartX=-49.19 StartY=8.5 StartZ=0 EndX=-1.5 EndY=8.5 EndZ=0
  constraints (19):
    c: Vertical(g0)
    c: Distance(g0) = 3
    c: Vertical(g1)
    c: Block(g1)
    c: Block(g2)
    c: Block(g3)
    c: Block(g0)
    c: Coincident(g4,g0)
    c: Coincident(g4,g2)
    c: Horizontal(g4)
    c: Coincident(g5,g0)
    c: Coincident(g5,g2)
    c: Horizontal(g5)
    c: Coincident(g6,g1)
    c: Coincident(g6,g3)
    c: Horizontal(g6)
    c: Coincident(g7,g1)
    c: Coincident(g7,g3)
    c: Horizontal(g7)
FEATURE [Part::Extrusion] Extrude071  label="sideB004"
  Base = -> Sketch079
  Dir = (0,0,1)
  DirMode = 2
  FaceMakerClass = Part::FaceMakerBullseye
  LengthFwd = 3
  LengthRev = 0
  Placement = pos=(0,0,71.7) rot=(0,0,1;0rad)
  Solid = true
  Symmetric = false
FEATURE [Part::MultiFuse] Fusion152  label="removeFromBottom004"
  Placement = pos=(2,0,0) rot=(0,0,1;0rad)
  Shapes = -> [Extrude070,Extrude071]
FEATURE [Part::Extrusion] Extrude072
  Base = -> Sketch081
  Dir = (1,0,0)
  DirMode = 2
  FaceMakerClass = Part::FaceMakerBullseye
  LengthFwd = 10
  LengthRev = 0
  Solid = true
  Symmetric = false
FEATURE [Part::Fillet] Fillet059  label="removeFromtMoreFrontCaseScrewRetainers004"
  Base = -> Extrude072
  Edges = 4 edges r=1.49: [Edge6,Edge11,Edge18,Edge23]
  Placement = pos=(-12,0,0) rot=(0,0,1;0rad)
FEATURE [Sketcher::SketchObject] Sketch082
  FullyConstrained = true
  Placement = pos=(117,19,0) rot=(0.57735,0.57735,0.57735;2.0944rad)
  sketch-geometry (8):
    g0: LineSegment StartX=-49.19 StartY=69.25 StartZ=0 EndX=-49.19 EndY=66.25 EndZ=0
    g1: LineSegment StartX=-49.19 StartY=5.75 StartZ=0 EndX=-49.19 EndY=2.75 EndZ=0
    g2: ArcOfCircle CenterX=-1.5 CenterY=67.75 CenterZ=0 NormalX=0 NormalY=0 NormalZ=1 AngleXU=0 Radius=1.5 StartAngle=4.71239 EndAngle=7.85398
    g3: ArcOfCircle CenterX=-1.5 CenterY=4.25 CenterZ=0 NormalX=0 NormalY=0 NormalZ=1 AngleXU=0 Radius=1.5 StartAngle=4.71239 EndAngle=7.85398
    g4: LineSegment StartX=-49.19 StartY=69.25 StartZ=0 EndX=-1.5 EndY=69.25 EndZ=0
    g5: LineSegment StartX=-49.19 StartY=66.25 StartZ=0 EndX=-1.5 EndY=66.25 EndZ=0
    g6: LineSegment StartX=-49.19 StartY=5.75 StartZ=0 EndX=-1.5 EndY=5.75 EndZ=0
    g7: LineSegment StartX=-49.19 StartY=2.75 StartZ=0 EndX=-1.5 EndY=2.75 EndZ=0
  constraints (19):
    c: Vertical(g0)
    c: Distance(g0) = 3
    c: Block(g0)
    c: Vertical(g1)
    c: Block(g2)
    c: Block(g3)
    c: Block(g1)
    c: Coincident(g4,g0)
    c: Coincident(g4,g2)
    c: Horizontal(g4)
    c: Coincident(g5,g0)
    c: Coincident(g5,g2)
    c: Horizontal(g5)
    c: Coincident(g6,g1)
    c: Coincident(g6,g3)
    c: Horizontal(g6)
    c: Coincident(g7,g1)
    c: Coincident(g7,g3)
    c: Horizontal(g7)
FEATURE [Part::Extrusion] Extrude073
  Base = -> Sketch082
  Dir = (1,0,0)
  DirMode = 2
  FaceMakerClass = Part::FaceMakerBullseye
  LengthFwd = 10
  LengthRev = 0
  Solid = true
  Symmetric = false
FEATURE [Part::Fillet] Fillet060  label="removeFromtMoreFrontCaseScrewRetainers005"
  Base = -> Extrude073
  Edges = 4 edges r=1.49: [Edge6,Edge11,Edge18,Edge23]
  Placement = pos=(-4,0,0) rot=(0,0,1;0rad)
FEATURE [Part::Revolution] Revolve163  label="backCaseScrewRetainer004"
  Angle = 360
  Axis = (0,1,0)
  Base = (0,0,0)
  FaceMakerClass = Part::FaceMakerBullseye
  Placement = pos=(12.5,3,62) rot=(0,0,1;0rad)
  Solid = false
  Source = -> Face149
  Symmetric = false
FEATURE [Part::Revolution] Revolve164  label="frontCaseScrewRetainer006"
  Angle = 360
  Axis = (0,1,0)
  Base = (0,0,0)
  FaceMakerClass = Part::FaceMakerBullseye
  Placement = pos=(89.5,3,68.5) rot=(0,0,1;0rad)
  Solid = false
  Source = -> Face151
  Symmetric = false
FEATURE [Part::Revolution] Revolve165  label="frontCaseScrewRetainer007"
  Angle = 360
  Axis = (0,1,0)
  Base = (0,0,0)
  FaceMakerClass = Part::FaceMakerBullseye
  Placement = pos=(89.5,3,3.5) rot=(0,0,1;0rad)
  Solid = false
  Source = -> Face152
  Symmetric = false
FEATURE [Part::Revolution] Revolve166  label="backCaseScrewRetainer005"
  Angle = 360
  Axis = (0,1,0)
  Base = (0,0,0)
  FaceMakerClass = Part::FaceMakerBullseye
  Placement = pos=(12.5,3,10) rot=(0,0,1;0rad)
  Solid = false
  Source = -> Face150
  Symmetric = false
FEATURE [Part::Revolution] Revolve167  label="moreFrontCaseScrewRetainer006"
  Angle = 360
  Axis = (0,1,0)
  Base = (0,0,0)
  FaceMakerClass = Part::FaceMakerBullseye
  Placement = pos=(109.5,4.5,68.5) rot=(0,0,1;0rad)
  Solid = false
  Source = -> Face153
  Symmetric = false
FEATURE [Part::Revolution] Revolve168  label="moreFrontCaseScrewRetainer007"
  Angle = 360
  Axis = (0,1,0)
  Base = (0,0,0)
  FaceMakerClass = Part::FaceMakerBullseye
  Placement = pos=(109.5,4.5,3.5) rot=(0,0,1;0rad)
  Solid = false
  Source = -> Face154
  Symmetric = false
FEATURE [Part::MultiFuse] Fusion151  label="screwRetainers003"
  Shapes = -> [Revolve168,Revolve167,Revolve166,Revolve165,Revolve164,Revolve163]
FEATURE [Part::Cut] Cut069  label="screwRetainers004"
  Base = -> Fusion151
  Tool = -> Fusion152
FEATURE [Part::Cut] Cut070
  Base = -> Cut069
  Tool = -> Fillet060
FEATURE [Part::Cut] Cut071  label="screwPillars001"
  Base = -> Cut070
  Tool = -> Fillet059
FEATURE [Part::MultiFuse] Fusion153  label="bottom024"
  Shapes = -> [Fusion149,Cut071]
FEATURE [Part::Cylinder] Cylinder067
  Angle = 360
  AttacherType = Attacher::AttachEngine3D
  Height = 10
  Placement = pos=(20.65,12,4.68) rot=(1,0,0;1.5708rad)
  Radius = 2
FEATURE [Part::Cylinder] Cylinder068
  Angle = 360
  AttacherType = Attacher::AttachEngine3D
  Height = 10
  Placement = pos=(20.65,12,67.38) rot=(1,0,0;1.5708rad)
  Radius = 2
FEATURE [Part::Cylinder] Cylinder069
  Angle = 360
  AttacherType = Attacher::AttachEngine3D
  Height = 10
  Placement = pos=(77.15,12,67.38) rot=(1,0,0;1.5708rad)
  Radius = 2
FEATURE [Part::Cylinder] Cylinder070
  Angle = 360
  AttacherType = Attacher::AttachEngine3D
  Height = 10
  Placement = pos=(77.15,12,4.68) rot=(1,0,0;1.5708rad)
  Radius = 2
FEATURE [Part::MultiFuse] Fusion154  label="removeFromThreadedInsertHousing001"
  Shapes = -> [Cylinder069,Cylinder068,Cylinder067,Cylinder070]
FEATURE [Part::Cut] Cut072  label="bottom025"
  Base = -> Fusion153
  Tool = -> Fusion154
FEATURE [Image::ImagePlane] ImagePlane
  XSize = 339
  YSize = 72
FEATURE [Sketcher::SketchObject] Sketch083
  FullyConstrained = false
  MapMode = 5
  Support = -> [XY_Plane]
  sketch-geometry (144):
    g0: LineSegment StartX=-151.619 StartY=28.8932 StartZ=0 EndX=-140.819 EndY=28.8932 EndZ=0
    g1: LineSegment StartX=-151.619 StartY=24.0313 StartZ=0 EndX=-151.619 EndY=28.8932 EndZ=0
    g2: LineSegment StartX=-140.819 StartY=17.7713 StartZ=0 EndX=-151.619 EndY=17.7713 EndZ=0
    g3: LineSegment StartX=-151.619 StartY=17.7713 StartZ=0 EndX=-151.619 EndY=22.6313 EndZ=0
    g4: LineSegment StartX=-151.619 StartY=22.6313 StartZ=0 EndX=-145.128 EndY=22.6313 EndZ=0
    g5: LineSegment StartX=-145.128 StartY=24.0313 StartZ=0 EndX=-140.819 EndY=28.8932 EndZ=0
    g6: LineSegment StartX=-145.128 StartY=22.6313 StartZ=0 EndX=-140.819 EndY=17.7713 EndZ=0
    g7: ArcOfCircle CenterX=-155.157 CenterY=23.3323 CenterZ=0 NormalX=0 NormalY=0 NormalZ=1 AngleXU=0 Radius=6.92354 StartAngle=1.03434 EndAngle=5.24885
    g8: ArcOfCircle CenterX=-155.157 CenterY=23.3323 CenterZ=0 NormalX=0 NormalY=0 NormalZ=1 AngleXU=0 Radius=12.6269 StartAngle=1.28675 EndAngle=4.99643
    g9: LineSegment StartX=-151.619 StartY=35.4532 StartZ=0 EndX=-151.619 EndY=29.2832 EndZ=0
    g10: LineSegment StartX=-151.619 StartY=17.3813 StartZ=0 EndX=-151.619 EndY=11.2113 EndZ=0
    g11-g21: Circle x11 (B-spline internal-alignment scaffolding for g22; pole/knot coordinates omitted)
    g22: BSplineCurve PolesCount=11 KnotsCount=9 Degree=3 IsPeriodic=0
    g23-g31: GeomPoint x9 (B-spline internal-alignment scaffolding for g22; pole/knot coordinates omitted)
    g32-g49: Circle x18 (B-spline internal-alignment scaffolding for g50; pole/knot coordinates omitted)
    g50: BSplineCurve PolesCount=18 KnotsCount=16 Degree=3 IsPeriodic=0
    g51-g66: GeomPoint x16 (B-spline internal-alignment scaffolding for g50; pole/knot coordinates omitted)
    g67: LineSegment StartX=-117.124 StartY=30.093 StartZ=0 EndX=-117.603 EndY=26.5272 EndZ=0
    g68: LineSegment StartX=-117.603 StartY=17.8472 StartZ=0 EndX=-117.124 EndY=14.2659 EndZ=0
    g69: Ellipse CenterX=-109.671 CenterY=20.025 CenterZ=0 NormalX=0 NormalY=0 NormalZ=1 MajorRadius=3.34798 MinorRadius=2.71052 AngleXU=-1.56793
    g70: GeomPoint X=-109.666 Y=18.0598 Z=0
    g71: GeomPoint X=-109.677 Y=21.9902 Z=0
    g72: Ellipse CenterX=-109.671 CenterY=20.0123 CenterZ=0 NormalX=0 NormalY=0 NormalZ=1 MajorRadius=6.93002 MinorRadius=6.36273 AngleXU=-3.13976
    g73: GeomPoint X=-112.417 Y=20.0073 Z=0
    g74: GeomPoint X=-106.925 Y=20.0173 Z=0
    g75: Ellipse CenterX=-51.7682 CenterY=20.1463 CenterZ=0 NormalX=0 NormalY=0 NormalZ=1 MajorRadius=3.19279 MinorRadius=2.71052 AngleXU=-1.52774
    g76: GeomPoint X=-51.6955 Y=18.4606 Z=0
    g77: GeomPoint X=-51.8408 Y=21.832 Z=0
    g78: GeomPoint X=-54.5142 Y=20.1413 Z=0
    g79: GeomPoint X=-49.0221 Y=20.1513 Z=0
    g80: Ellipse CenterX=-51.7682 CenterY=20.1463 CenterZ=0 NormalX=0 NormalY=0 NormalZ=1 MajorRadius=6.93002 MinorRadius=6.36273 AngleXU=-3.13976
    g81: Ellipse CenterX=-22.8436 CenterY=20.1783 CenterZ=0 NormalX=0 NormalY=0 NormalZ=1 MajorRadius=3.31512 MinorRadius=2.71052 AngleXU=-1.60214
    g82: GeomPoint X=-22.9034 Y=18.2706 Z=0
    g83: GeomPoint X=-22.7838 Y=22.0861 Z=0
    g84: GeomPoint X=-25.5897 Y=20.1733 Z=0
    g85: GeomPoint X=-20.0976 Y=20.1833 Z=0
    g86: Ellipse CenterX=-22.8436 CenterY=20.1783 CenterZ=0 NormalX=0 NormalY=0 NormalZ=1 MajorRadius=6.93002 MinorRadius=6.36273 AngleXU=-3.13976
    g87: LineSegment StartX=-101.889 StartY=14.1107 StartZ=0 EndX=-97.7455 EndY=14.1107 EndZ=0
    g88: LineSegment StartX=-93.8155 StartY=14.1107 StartZ=0 EndX=-89.6755 EndY=14.1107 EndZ=0
    g89: LineSegment StartX=-85.7455 StartY=14.1107 StartZ=0 EndX=-81.6055 EndY=14.1107 EndZ=0
    g90: LineSegment StartX=-101.889 StartY=14.1107 StartZ=0 EndX=-101.889 EndY=25.9907 EndZ=0
    g91: LineSegment StartX=-101.889 StartY=25.9907 StartZ=0 EndX=-97.8594 EndY=25.9907 EndZ=0
    g92: LineSegment StartX=-97.8594 StartY=25.9907 StartZ=0 EndX=-97.8594 EndY=24.0907 EndZ=0
    g93: LineSegment StartX=-97.7455 StartY=14.1107 StartZ=0 EndX=-97.7455 EndY=19.9107 EndZ=0
    g94: LineSegment StartX=-89.6755 StartY=14.1107 StartZ=0 EndX=-89.6755 EndY=19.9107 EndZ=0
    g95: LineSegment StartX=-93.8155 StartY=14.1107 StartZ=0 EndX=-93.8155 EndY=21.0107 EndZ=0
    g96-g106: Circle x11 (B-spline internal-alignment scaffolding for g107; pole/knot coordinates omitted)
    g107: BSplineCurve PolesCount=11 KnotsCount=9 Degree=3 IsPeriodic=0
    g108-g116: GeomPoint x9 (B-spline internal-alignment scaffolding for g107; pole/knot coordinates omitted)
    g117: BSplineCurve PolesCount=11 KnotsCount=9 Degree=3 IsPeriodic=0
    g118-g125: Circle x8 (B-spline internal-alignment scaffolding for g126; pole/knot coordinates omitted)
    g126: BSplineCurve PolesCount=8 KnotsCount=6 Degree=3 IsPeriodic=0
    g127-g132: GeomPoint x6 (B-spline internal-alignment scaffolding for g126; pole/knot coordinates omitted)
    g133: LineSegment StartX=-143.549 StartY=24.0313 StartZ=0 EndX=-143.549 EndY=28.8932 EndZ=0
    g134: BSplineCurve PolesCount=8 KnotsCount=6 Degree=3 IsPeriodic=0
    g135: LineSegment StartX=-85.7455 StartY=21.0107 StartZ=0 EndX=-85.7455 EndY=14.1107 EndZ=0
    g136: LineSegment StartX=-81.6055 StartY=14.1107 StartZ=0 EndX=-81.6055 EndY=21.5868 EndZ=0
    g137-g140: Circle x4 (B-spline internal-alignment scaffolding for g141; pole/knot coordinates omitted)
    g141: BSplineCurve PolesCount=4 KnotsCount=2 Degree=3 IsPeriodic=0
    g142: GeomPoint X=-81.6055 Y=21.5868 Z=0
    g143: GeomPoint X=-82.0394 Y=24.0907 Z=0
  constraints (117):
    c: Coincident(g1,g0)
    c: Horizontal(g0)
    c: Vertical(g1)
    c: Coincident(g2,g3)
    c: Coincident(g3,g4)
    c: Horizontal(g4)
    c: Horizontal(g2)
    c: Vertical(g3)
    c: Block(g1)
    c: Distance(g3) = 4.86
    c: Block(g4)
    c: Distance(g0) = 10.8
    c: Distance(g2) = 10.8
    c: Coincident(g5,g0)
    c: Coincident(g6,g4)
    c: Coincident(g6,g2)
    c: Block(g8)
    c: Block(g7)
    c: Coincident(g9,g8)
    c: Coincident(g9,g7)
    c: Vertical(g9)
    c: Coincident(g10,g7)
    c: Coincident(g10,g8)
    c: Vertical(g10)
    c: Weight(g11) = 1
    c: Equal(g11, g12-g21) x10
    c: InternalAlignment(g11-g21 -> g22) x11
    c: InternalAlignment(g23-g31 -> g22) x9
    c: Block(g22)
    c: Weight(g32) = 1
    c: Equal(g32, g33-g49) x17
    c: InternalAlignment(g32-g49 -> g50) x18
    c: InternalAlignment(g51-g66 -> g50) x16
    c: Block(g50)
    c: Coincident(g67,g50)
    c: Coincident(g67,g22)
    c: Coincident(g68,g22)
    c: Coincident(g68,g50)
    c: InternalAlignment(g70,g69)
    c: InternalAlignment(g71,g69)
    c: Block(g69)
    c: InternalAlignment(g73,g72)
    c: InternalAlignment(g74,g72)
    c: Block(g72)
    c: InternalAlignment(g76,g75)
    c: InternalAlignment(g77,g75)
    c: InternalAlignment(g78,g80)
    c: InternalAlignment(g79,g80)
    c: Block(g80)
    c: Coincident(g75,g80)
    c: Block(g75)
    c: InternalAlignment(g82,g81)
    c: InternalAlignment(g83,g81)
    c: InternalAlignment(g84,g86)
    c: InternalAlignment(g85,g86)
    c: Block(g86)
    c: Coincident(g81,g86)
    c: Block(g81)
    c: Horizontal(g87)
    c: Block(g87)
    c: Horizontal(g88)
    c: Distance(g88) = 4.14
    c: Horizontal(g89)
    c: Equal(g88,g89) = 4.14
    c: Block(g89)
    c: Block(g88)
    c: Coincident(g90,g87)
    c: Vertical(g90)
    c: Distance(g90) = 11.88
    c: Coincident(g91,g90)
    c: Horizontal(g91)
    c: Coincident(g92,g91)
    c: Vertical(g92)
    c: Distance(g91) = 4.03
    c: Distance(g92) = 1.9
    c: Coincident(g93,g87)
    c: Vertical(g93)
    c: Vertical(g94)
    c: Coincident(g94,g88)
    c: Distance(g93) = 5.8
    c: Distance(g94) = 5.8
    c: Vertical(g95)
    c: Coincident(g95,g88)
    c: Distance(g95) = 6.9
    c: Coincident(g107,g92)
    c: Weight(g96) = 1
    c: Equal(g96, g97-g106) x10
    c: InternalAlignment(g96-g106 -> g107) x11
    c: InternalAlignment(g108-g116 -> g107) x9
    c: Block(g107)
    c: Block(g117)
    c: Coincident(g126,g93)
    c: Weight(g118) = 1
    c: Equal(g118, g119-g125) x7
    c: Coincident(g126,g95)
    c: InternalAlignment(g118-g125 -> g126) x8
    c: InternalAlignment(g127-g132 -> g126) x6
    c: Vertical(g133)
    c: Block(g133)
    c: Coincident(g134,g94)
    c: Block(g126)
    c: Block(g134)
    c: Coincident(g135,g134)
    c: Coincident(g135,g89)
    c: Vertical(g135)
    c: Coincident(g136,g89)
    c: Vertical(g136)
    c: Coincident(g141,g136)
    c: Weight(g137) = 1
    c: Equal(g137,g138)
    c: Equal(g137,g139)
    c: Equal(g137,g140)
    c: Coincident(g141,g117)
    c: InternalAlignment(g137-g140 -> g141) x4
    c: InternalAlignment(g142,g141)
    c: InternalAlignment(g143,g141)
    c: Block(g141)
FEATURE [PartDesign::Body] Body
  Group = -> [Sketch083]
  Origin = -> Origin
FEATURE [Sketcher::SketchObject] Sketch084
  FullyConstrained = true
  MapMode = 5
  Support = -> [XY_Plane001]
FEATURE [PartDesign::Body] Body001
  Group = -> [Sketch084]
  Origin = -> Origin001
